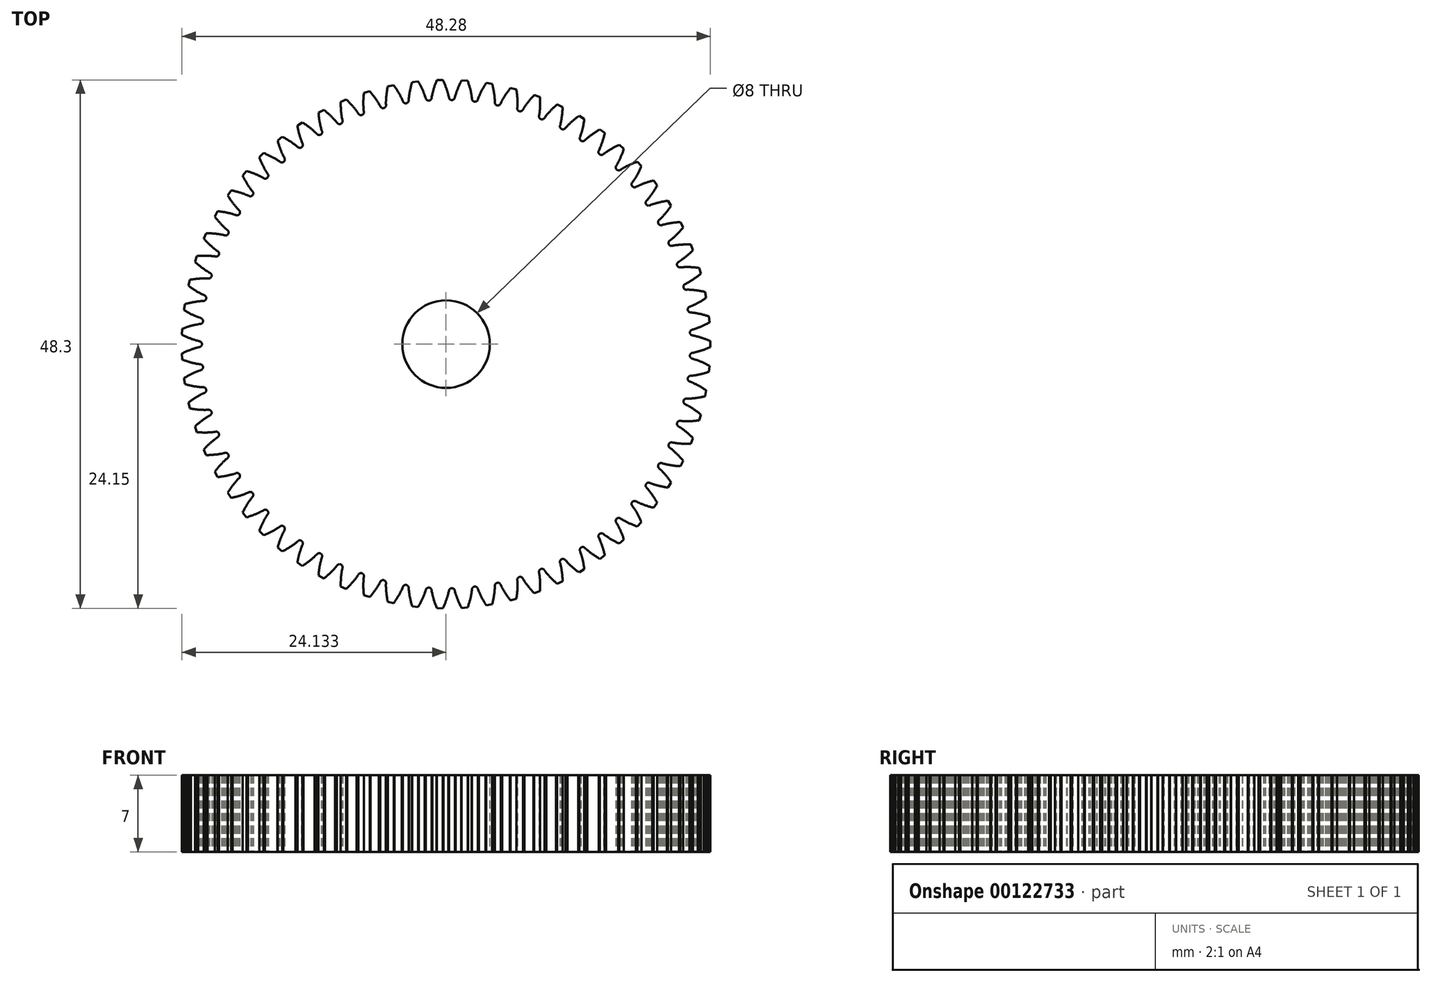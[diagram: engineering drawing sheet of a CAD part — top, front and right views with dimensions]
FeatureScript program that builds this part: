
annotation { "Feature Type Name" : "Feature", "Feature Type Description" : "" }
export const myFeature = defineFeature(function(context is Context, id is Id, definition is map)
    precondition{}
    {
        {
            var Q0;
            Q0=qCreatedBy(makeId("Top.planeOp"),FACE);
            var sketch = newSketch(context, id + "F0", { "sketchPlane" : qUnion([Q0])});
            skLineSegment(sketch, "E0", {"start": v(22.55, -0.79) * mm, "end": v(22.62, -0.77) * mm});
            skLineSegment(sketch, "E1", {"start": v(22.62, -0.77) * mm, "end": v(22.71, -0.75) * mm});
            skLineSegment(sketch, "E2", {"start": v(22.71, -0.75) * mm, "end": v(22.8, -0.73) * mm});
            skLineSegment(sketch, "E3", {"start": v(22.8, -0.73) * mm, "end": v(22.86, -0.72) * mm});
            skLineSegment(sketch, "E4", {"start": v(22.86, -0.72) * mm, "end": v(22.91, -0.7) * mm});
            skLineSegment(sketch, "E5", {"start": v(22.91, -0.7) * mm, "end": v(22.97, -0.7) * mm});
            skLineSegment(sketch, "E6", {"start": v(22.97, -0.7) * mm, "end": v(23.02, -0.68) * mm});
            skLineSegment(sketch, "E7", {"start": v(23.02, -0.68) * mm, "end": v(23.08, -0.66) * mm});
            skLineSegment(sketch, "E8", {"start": v(23.08, -0.66) * mm, "end": v(23.14, -0.64) * mm});
            skLineSegment(sketch, "E9", {"start": v(23.14, -0.64) * mm, "end": v(23.2, -0.63) * mm});
            skLineSegment(sketch, "E10", {"start": v(23.2, -0.63) * mm, "end": v(23.26, -0.6) * mm});
            skLineSegment(sketch, "E11", {"start": v(23.26, -0.6) * mm, "end": v(23.33, -0.59) * mm});
            skLineSegment(sketch, "E12", {"start": v(23.33, -0.59) * mm, "end": v(23.4, -0.57) * mm});
            skLineSegment(sketch, "E13", {"start": v(23.4, -0.57) * mm, "end": v(23.46, -0.54) * mm});
            skLineSegment(sketch, "E14", {"start": v(23.46, -0.54) * mm, "end": v(23.52, -0.52) * mm});
            skLineSegment(sketch, "E15", {"start": v(23.52, -0.52) * mm, "end": v(23.6, -0.5) * mm});
            skLineSegment(sketch, "E16", {"start": v(23.6, -0.5) * mm, "end": v(23.66, -0.47) * mm});
            skLineSegment(sketch, "E17", {"start": v(23.66, -0.47) * mm, "end": v(23.73, -0.44) * mm});
            skLineSegment(sketch, "E18", {"start": v(23.73, -0.44) * mm, "end": v(23.8, -0.42) * mm});
            skLineSegment(sketch, "E19", {"start": v(23.8, -0.42) * mm, "end": v(23.88, -0.39) * mm});
            skLineSegment(sketch, "E20", {"start": v(23.88, -0.39) * mm, "end": v(23.96, -0.36) * mm});
            skLineSegment(sketch, "E21", {"start": v(23.96, -0.36) * mm, "end": v(24.03, -0.32) * mm});
            skLineSegment(sketch, "E22", {"start": v(24.03, -0.32) * mm, "end": v(24.14, -0.28) * mm});
            skLineSegment(sketch, "E23", {"start": v(24.14, -0.28) * mm, "end": v(24.14, 0.28) * mm});
            skLineSegment(sketch, "E24", {"start": v(24.14, 0.28) * mm, "end": v(24.03, 0.32) * mm});
            skLineSegment(sketch, "E25", {"start": v(24.03, 0.32) * mm, "end": v(23.96, 0.36) * mm});
            skLineSegment(sketch, "E26", {"start": v(23.96, 0.36) * mm, "end": v(23.88, 0.39) * mm});
            skLineSegment(sketch, "E27", {"start": v(23.88, 0.39) * mm, "end": v(23.8, 0.42) * mm});
            skLineSegment(sketch, "E28", {"start": v(23.8, 0.42) * mm, "end": v(23.73, 0.44) * mm});
            skLineSegment(sketch, "E29", {"start": v(23.73, 0.44) * mm, "end": v(23.66, 0.47) * mm});
            skLineSegment(sketch, "E30", {"start": v(23.66, 0.47) * mm, "end": v(23.6, 0.5) * mm});
            skLineSegment(sketch, "E31", {"start": v(23.6, 0.5) * mm, "end": v(23.52, 0.52) * mm});
            skLineSegment(sketch, "E32", {"start": v(23.52, 0.52) * mm, "end": v(23.46, 0.54) * mm});
            skLineSegment(sketch, "E33", {"start": v(23.46, 0.54) * mm, "end": v(23.4, 0.57) * mm});
            skLineSegment(sketch, "E34", {"start": v(23.4, 0.57) * mm, "end": v(23.33, 0.59) * mm});
            skLineSegment(sketch, "E35", {"start": v(23.33, 0.59) * mm, "end": v(23.26, 0.6) * mm});
            skLineSegment(sketch, "E36", {"start": v(23.26, 0.6) * mm, "end": v(23.2, 0.63) * mm});
            skLineSegment(sketch, "E37", {"start": v(23.2, 0.63) * mm, "end": v(23.14, 0.64) * mm});
            skLineSegment(sketch, "E38", {"start": v(23.14, 0.64) * mm, "end": v(23.08, 0.66) * mm});
            skLineSegment(sketch, "E39", {"start": v(23.08, 0.66) * mm, "end": v(23.02, 0.68) * mm});
            skLineSegment(sketch, "E40", {"start": v(23.02, 0.68) * mm, "end": v(22.97, 0.7) * mm});
            skLineSegment(sketch, "E41", {"start": v(22.97, 0.7) * mm, "end": v(22.91, 0.7) * mm});
            skLineSegment(sketch, "E42", {"start": v(22.91, 0.7) * mm, "end": v(22.86, 0.72) * mm});
            skLineSegment(sketch, "E43", {"start": v(22.86, 0.72) * mm, "end": v(22.8, 0.73) * mm});
            skLineSegment(sketch, "E44", {"start": v(22.8, 0.73) * mm, "end": v(22.71, 0.75) * mm});
            skLineSegment(sketch, "E45", {"start": v(22.71, 0.75) * mm, "end": v(22.62, 0.77) * mm});
            skLineSegment(sketch, "E46", {"start": v(22.62, 0.77) * mm, "end": v(22.55, 0.79) * mm});
            skArc(sketch, "E47", {"start": v(22.55, 0.79) * mm, "mid": v(22.28, 1.05) * mm, "end": v(22.53, 1.33) * mm});
            skLineSegment(sketch, "E48", {"start": v(22.53, 1.33) * mm, "end": v(22.6, 1.35) * mm});
            skLineSegment(sketch, "E49", {"start": v(22.6, 1.35) * mm, "end": v(22.68, 1.38) * mm});
            skLineSegment(sketch, "E50", {"start": v(22.68, 1.38) * mm, "end": v(22.78, 1.4) * mm});
            skLineSegment(sketch, "E51", {"start": v(22.78, 1.4) * mm, "end": v(22.83, 1.43) * mm});
            skLineSegment(sketch, "E52", {"start": v(22.83, 1.43) * mm, "end": v(22.88, 1.44) * mm});
            skLineSegment(sketch, "E53", {"start": v(22.88, 1.44) * mm, "end": v(22.93, 1.46) * mm});
            skLineSegment(sketch, "E54", {"start": v(22.93, 1.46) * mm, "end": v(22.99, 1.48) * mm});
            skLineSegment(sketch, "E55", {"start": v(22.99, 1.48) * mm, "end": v(23.04, 1.5) * mm});
            skLineSegment(sketch, "E56", {"start": v(23.04, 1.5) * mm, "end": v(23.1, 1.53) * mm});
            skLineSegment(sketch, "E57", {"start": v(23.1, 1.53) * mm, "end": v(23.16, 1.55) * mm});
            skLineSegment(sketch, "E58", {"start": v(23.16, 1.55) * mm, "end": v(23.22, 1.58) * mm});
            skLineSegment(sketch, "E59", {"start": v(23.22, 1.58) * mm, "end": v(23.28, 1.6) * mm});
            skLineSegment(sketch, "E60", {"start": v(23.28, 1.6) * mm, "end": v(23.34, 1.63) * mm});
            skLineSegment(sketch, "E61", {"start": v(23.34, 1.63) * mm, "end": v(23.4, 1.66) * mm});
            skLineSegment(sketch, "E62", {"start": v(23.4, 1.66) * mm, "end": v(23.47, 1.69) * mm});
            skLineSegment(sketch, "E63", {"start": v(23.47, 1.69) * mm, "end": v(23.54, 1.72) * mm});
            skLineSegment(sketch, "E64", {"start": v(23.54, 1.72) * mm, "end": v(23.6, 1.75) * mm});
            skLineSegment(sketch, "E65", {"start": v(23.6, 1.75) * mm, "end": v(23.67, 1.78) * mm});
            skLineSegment(sketch, "E66", {"start": v(23.67, 1.78) * mm, "end": v(23.74, 1.82) * mm});
            skLineSegment(sketch, "E67", {"start": v(23.74, 1.82) * mm, "end": v(23.81, 1.85) * mm});
            skLineSegment(sketch, "E68", {"start": v(23.81, 1.85) * mm, "end": v(23.88, 1.9) * mm});
            skLineSegment(sketch, "E69", {"start": v(23.88, 1.9) * mm, "end": v(23.96, 1.93) * mm});
            skLineSegment(sketch, "E70", {"start": v(23.96, 1.93) * mm, "end": v(24.06, 1.99) * mm});
            skLineSegment(sketch, "E71", {"start": v(24.06, 1.99) * mm, "end": v(24, 2.54) * mm});
            skLineSegment(sketch, "E72", {"start": v(24, 2.54) * mm, "end": v(23.9, 2.57) * mm});
            skLineSegment(sketch, "E73", {"start": v(23.9, 2.57) * mm, "end": v(23.82, 2.6) * mm});
            skLineSegment(sketch, "E74", {"start": v(23.82, 2.6) * mm, "end": v(23.74, 2.62) * mm});
            skLineSegment(sketch, "E75", {"start": v(23.74, 2.62) * mm, "end": v(23.66, 2.64) * mm});
            skLineSegment(sketch, "E76", {"start": v(23.66, 2.64) * mm, "end": v(23.59, 2.66) * mm});
            skLineSegment(sketch, "E77", {"start": v(23.59, 2.66) * mm, "end": v(23.51, 2.68) * mm});
            skLineSegment(sketch, "E78", {"start": v(23.51, 2.68) * mm, "end": v(23.44, 2.7) * mm});
            skLineSegment(sketch, "E79", {"start": v(23.44, 2.7) * mm, "end": v(23.37, 2.72) * mm});
            skLineSegment(sketch, "E80", {"start": v(23.37, 2.72) * mm, "end": v(23.3, 2.74) * mm});
            skLineSegment(sketch, "E81", {"start": v(23.3, 2.74) * mm, "end": v(23.23, 2.75) * mm});
            skLineSegment(sketch, "E82", {"start": v(23.23, 2.75) * mm, "end": v(23.17, 2.77) * mm});
            skLineSegment(sketch, "E83", {"start": v(23.17, 2.77) * mm, "end": v(23.1, 2.78) * mm});
            skLineSegment(sketch, "E84", {"start": v(23.1, 2.78) * mm, "end": v(23.04, 2.8) * mm});
            skLineSegment(sketch, "E85", {"start": v(23.04, 2.8) * mm, "end": v(22.98, 2.8) * mm});
            skLineSegment(sketch, "E86", {"start": v(22.98, 2.8) * mm, "end": v(22.92, 2.82) * mm});
            skLineSegment(sketch, "E87", {"start": v(22.92, 2.82) * mm, "end": v(22.86, 2.83) * mm});
            skLineSegment(sketch, "E88", {"start": v(22.86, 2.83) * mm, "end": v(22.8, 2.84) * mm});
            skLineSegment(sketch, "E89", {"start": v(22.8, 2.84) * mm, "end": v(22.75, 2.85) * mm});
            skLineSegment(sketch, "E90", {"start": v(22.75, 2.85) * mm, "end": v(22.7, 2.86) * mm});
            skLineSegment(sketch, "E91", {"start": v(22.7, 2.86) * mm, "end": v(22.64, 2.86) * mm});
            skLineSegment(sketch, "E92", {"start": v(22.64, 2.86) * mm, "end": v(22.54, 2.88) * mm});
            skLineSegment(sketch, "E93", {"start": v(22.54, 2.88) * mm, "end": v(22.45, 2.89) * mm});
            skLineSegment(sketch, "E94", {"start": v(22.45, 2.89) * mm, "end": v(22.38, 2.9) * mm});
            skArc(sketch, "E95", {"start": v(22.38, 2.9) * mm, "mid": v(22.08, 3.13) * mm, "end": v(22.3, 3.44) * mm});
            skLineSegment(sketch, "E96", {"start": v(22.3, 3.44) * mm, "end": v(22.37, 3.46) * mm});
            skLineSegment(sketch, "E97", {"start": v(22.37, 3.46) * mm, "end": v(22.45, 3.5) * mm});
            skLineSegment(sketch, "E98", {"start": v(22.45, 3.5) * mm, "end": v(22.55, 3.54) * mm});
            skLineSegment(sketch, "E99", {"start": v(22.55, 3.54) * mm, "end": v(22.6, 3.56) * mm});
            skLineSegment(sketch, "E100", {"start": v(22.6, 3.56) * mm, "end": v(22.64, 3.58) * mm});
            skLineSegment(sketch, "E101", {"start": v(22.64, 3.58) * mm, "end": v(22.7, 3.6) * mm});
            skLineSegment(sketch, "E102", {"start": v(22.7, 3.6) * mm, "end": v(22.75, 3.63) * mm});
            skLineSegment(sketch, "E103", {"start": v(22.75, 3.63) * mm, "end": v(22.8, 3.66) * mm});
            skLineSegment(sketch, "E104", {"start": v(22.8, 3.66) * mm, "end": v(22.85, 3.68) * mm});
            skLineSegment(sketch, "E105", {"start": v(22.85, 3.68) * mm, "end": v(22.91, 3.71) * mm});
            skLineSegment(sketch, "E106", {"start": v(22.91, 3.71) * mm, "end": v(22.97, 3.74) * mm});
            skLineSegment(sketch, "E107", {"start": v(22.97, 3.74) * mm, "end": v(23.03, 3.77) * mm});
            skLineSegment(sketch, "E108", {"start": v(23.03, 3.77) * mm, "end": v(23.09, 3.8) * mm});
            skLineSegment(sketch, "E109", {"start": v(23.09, 3.8) * mm, "end": v(23.15, 3.84) * mm});
            skLineSegment(sketch, "E110", {"start": v(23.15, 3.84) * mm, "end": v(23.2, 3.88) * mm});
            skLineSegment(sketch, "E111", {"start": v(23.2, 3.88) * mm, "end": v(23.27, 3.91) * mm});
            skLineSegment(sketch, "E112", {"start": v(23.27, 3.91) * mm, "end": v(23.34, 3.95) * mm});
            skLineSegment(sketch, "E113", {"start": v(23.34, 3.95) * mm, "end": v(23.4, 4) * mm});
            skLineSegment(sketch, "E114", {"start": v(23.4, 4) * mm, "end": v(23.47, 4.03) * mm});
            skLineSegment(sketch, "E115", {"start": v(23.47, 4.03) * mm, "end": v(23.53, 4.08) * mm});
            skLineSegment(sketch, "E116", {"start": v(23.53, 4.08) * mm, "end": v(23.6, 4.12) * mm});
            skLineSegment(sketch, "E117", {"start": v(23.6, 4.12) * mm, "end": v(23.67, 4.16) * mm});
            skLineSegment(sketch, "E118", {"start": v(23.67, 4.16) * mm, "end": v(23.77, 4.23) * mm});
            skLineSegment(sketch, "E119", {"start": v(23.77, 4.23) * mm, "end": v(23.67, 4.77) * mm});
            skLineSegment(sketch, "E120", {"start": v(23.67, 4.77) * mm, "end": v(23.55, 4.8) * mm});
            skLineSegment(sketch, "E121", {"start": v(23.55, 4.8) * mm, "end": v(23.47, 4.82) * mm});
            skLineSegment(sketch, "E122", {"start": v(23.47, 4.82) * mm, "end": v(23.4, 4.83) * mm});
            skLineSegment(sketch, "E123", {"start": v(23.4, 4.83) * mm, "end": v(23.31, 4.85) * mm});
            skLineSegment(sketch, "E124", {"start": v(23.31, 4.85) * mm, "end": v(23.24, 4.86) * mm});
            skLineSegment(sketch, "E125", {"start": v(23.24, 4.86) * mm, "end": v(23.16, 4.88) * mm});
            skLineSegment(sketch, "E126", {"start": v(23.16, 4.88) * mm, "end": v(23.09, 4.89) * mm});
            skLineSegment(sketch, "E127", {"start": v(23.09, 4.89) * mm, "end": v(23.01, 4.9) * mm});
            skLineSegment(sketch, "E128", {"start": v(23.01, 4.9) * mm, "end": v(22.94, 4.9) * mm});
            skLineSegment(sketch, "E129", {"start": v(22.94, 4.9) * mm, "end": v(22.87, 4.92) * mm});
            skLineSegment(sketch, "E130", {"start": v(22.87, 4.92) * mm, "end": v(22.8, 4.93) * mm});
            skLineSegment(sketch, "E131", {"start": v(22.8, 4.93) * mm, "end": v(22.74, 4.93) * mm});
            skLineSegment(sketch, "E132", {"start": v(22.74, 4.93) * mm, "end": v(22.68, 4.94) * mm});
            skLineSegment(sketch, "E133", {"start": v(22.68, 4.94) * mm, "end": v(22.61, 4.95) * mm});
            skLineSegment(sketch, "E134", {"start": v(22.61, 4.95) * mm, "end": v(22.55, 4.95) * mm});
            skLineSegment(sketch, "E135", {"start": v(22.55, 4.95) * mm, "end": v(22.5, 4.96) * mm});
            skLineSegment(sketch, "E136", {"start": v(22.5, 4.96) * mm, "end": v(22.44, 4.96) * mm});
            skLineSegment(sketch, "E137", {"start": v(22.44, 4.96) * mm, "end": v(22.38, 4.97) * mm});
            skLineSegment(sketch, "E138", {"start": v(22.38, 4.97) * mm, "end": v(22.33, 4.97) * mm});
            skLineSegment(sketch, "E139", {"start": v(22.33, 4.97) * mm, "end": v(22.27, 4.97) * mm});
            skLineSegment(sketch, "E140", {"start": v(22.27, 4.97) * mm, "end": v(22.17, 4.98) * mm});
            skLineSegment(sketch, "E141", {"start": v(22.17, 4.98) * mm, "end": v(22.08, 4.98) * mm});
            skLineSegment(sketch, "E142", {"start": v(22.08, 4.98) * mm, "end": v(22.01, 4.98) * mm});
            skArc(sketch, "E143", {"start": v(22.01, 4.98) * mm, "mid": v(21.7, 5.18) * mm, "end": v(21.89, 5.5) * mm});
            skLineSegment(sketch, "E144", {"start": v(21.89, 5.5) * mm, "end": v(21.94, 5.54) * mm});
            skLineSegment(sketch, "E145", {"start": v(21.94, 5.54) * mm, "end": v(22.03, 5.58) * mm});
            skLineSegment(sketch, "E146", {"start": v(22.03, 5.58) * mm, "end": v(22.12, 5.63) * mm});
            skLineSegment(sketch, "E147", {"start": v(22.12, 5.63) * mm, "end": v(22.16, 5.66) * mm});
            skLineSegment(sketch, "E148", {"start": v(22.16, 5.66) * mm, "end": v(22.2, 5.69) * mm});
            skLineSegment(sketch, "E149", {"start": v(22.2, 5.69) * mm, "end": v(22.26, 5.71) * mm});
            skLineSegment(sketch, "E150", {"start": v(22.26, 5.71) * mm, "end": v(22.3, 5.74) * mm});
            skLineSegment(sketch, "E151", {"start": v(22.3, 5.74) * mm, "end": v(22.36, 5.78) * mm});
            skLineSegment(sketch, "E152", {"start": v(22.36, 5.78) * mm, "end": v(22.4, 5.8) * mm});
            skLineSegment(sketch, "E153", {"start": v(22.4, 5.8) * mm, "end": v(22.46, 5.84) * mm});
            skLineSegment(sketch, "E154", {"start": v(22.46, 5.84) * mm, "end": v(22.52, 5.88) * mm});
            skLineSegment(sketch, "E155", {"start": v(22.52, 5.88) * mm, "end": v(22.57, 5.91) * mm});
            skLineSegment(sketch, "E156", {"start": v(22.57, 5.91) * mm, "end": v(22.63, 5.95) * mm});
            skLineSegment(sketch, "E157", {"start": v(22.63, 5.95) * mm, "end": v(22.68, 6) * mm});
            skLineSegment(sketch, "E158", {"start": v(22.68, 6) * mm, "end": v(22.74, 6.03) * mm});
            skLineSegment(sketch, "E159", {"start": v(22.74, 6.03) * mm, "end": v(22.8, 6.08) * mm});
            skLineSegment(sketch, "E160", {"start": v(22.8, 6.08) * mm, "end": v(22.86, 6.12) * mm});
            skLineSegment(sketch, "E161", {"start": v(22.86, 6.12) * mm, "end": v(22.92, 6.17) * mm});
            skLineSegment(sketch, "E162", {"start": v(22.92, 6.17) * mm, "end": v(22.99, 6.21) * mm});
            skLineSegment(sketch, "E163", {"start": v(22.99, 6.21) * mm, "end": v(23.05, 6.26) * mm});
            skLineSegment(sketch, "E164", {"start": v(23.05, 6.26) * mm, "end": v(23.11, 6.31) * mm});
            skLineSegment(sketch, "E165", {"start": v(23.11, 6.31) * mm, "end": v(23.18, 6.36) * mm});
            skLineSegment(sketch, "E166", {"start": v(23.18, 6.36) * mm, "end": v(23.27, 6.44) * mm});
            skLineSegment(sketch, "E167", {"start": v(23.27, 6.44) * mm, "end": v(23.12, 6.97) * mm});
            skLineSegment(sketch, "E168", {"start": v(23.12, 6.97) * mm, "end": v(23, 6.99) * mm});
            skLineSegment(sketch, "E169", {"start": v(23, 6.99) * mm, "end": v(22.92, 7) * mm});
            skLineSegment(sketch, "E170", {"start": v(22.92, 7) * mm, "end": v(22.83, 7) * mm});
            skLineSegment(sketch, "E171", {"start": v(22.83, 7) * mm, "end": v(22.76, 7.01) * mm});
            skLineSegment(sketch, "E172", {"start": v(22.76, 7.01) * mm, "end": v(22.68, 7.02) * mm});
            skLineSegment(sketch, "E173", {"start": v(22.68, 7.02) * mm, "end": v(22.6, 7.02) * mm});
            skLineSegment(sketch, "E174", {"start": v(22.6, 7.02) * mm, "end": v(22.53, 7.03) * mm});
            skLineSegment(sketch, "E175", {"start": v(22.53, 7.03) * mm, "end": v(22.45, 7.03) * mm});
            skLineSegment(sketch, "E176", {"start": v(22.45, 7.03) * mm, "end": v(22.38, 7.04) * mm});
            skLineSegment(sketch, "E177", {"start": v(22.38, 7.04) * mm, "end": v(22.31, 7.04) * mm});
            skLineSegment(sketch, "E178", {"start": v(22.31, 7.04) * mm, "end": v(22.25, 7.04) * mm});
            skLineSegment(sketch, "E179", {"start": v(22.25, 7.04) * mm, "end": v(22.18, 7.04) * mm});
            skLineSegment(sketch, "E180", {"start": v(22.18, 7.04) * mm, "end": v(22.11, 7.04) * mm});
            skLineSegment(sketch, "E181", {"start": v(22.11, 7.04) * mm, "end": v(22.05, 7.04) * mm});
            skLineSegment(sketch, "E182", {"start": v(22.05, 7.04) * mm, "end": v(22, 7.04) * mm});
            skLineSegment(sketch, "E183", {"start": v(22, 7.04) * mm, "end": v(21.93, 7.04) * mm});
            skLineSegment(sketch, "E184", {"start": v(21.93, 7.04) * mm, "end": v(21.87, 7.04) * mm});
            skLineSegment(sketch, "E185", {"start": v(21.87, 7.04) * mm, "end": v(21.82, 7.04) * mm});
            skLineSegment(sketch, "E186", {"start": v(21.82, 7.04) * mm, "end": v(21.76, 7.04) * mm});
            skLineSegment(sketch, "E187", {"start": v(21.76, 7.04) * mm, "end": v(21.7, 7.04) * mm});
            skLineSegment(sketch, "E188", {"start": v(21.7, 7.04) * mm, "end": v(21.6, 7.03) * mm});
            skLineSegment(sketch, "E189", {"start": v(21.6, 7.03) * mm, "end": v(21.52, 7.02) * mm});
            skLineSegment(sketch, "E190", {"start": v(21.52, 7.02) * mm, "end": v(21.45, 7.02) * mm});
            skArc(sketch, "E191", {"start": v(21.45, 7.02) * mm, "mid": v(21.11, 7.2) * mm, "end": v(21.27, 7.54) * mm});
            skLineSegment(sketch, "E192", {"start": v(21.27, 7.54) * mm, "end": v(21.33, 7.57) * mm});
            skLineSegment(sketch, "E193", {"start": v(21.33, 7.57) * mm, "end": v(21.4, 7.62) * mm});
            skLineSegment(sketch, "E194", {"start": v(21.4, 7.62) * mm, "end": v(21.5, 7.68) * mm});
            skLineSegment(sketch, "E195", {"start": v(21.5, 7.68) * mm, "end": v(21.53, 7.7) * mm});
            skLineSegment(sketch, "E196", {"start": v(21.53, 7.7) * mm, "end": v(21.58, 7.74) * mm});
            skLineSegment(sketch, "E197", {"start": v(21.58, 7.74) * mm, "end": v(21.62, 7.77) * mm});
            skLineSegment(sketch, "E198", {"start": v(21.62, 7.77) * mm, "end": v(21.67, 7.8) * mm});
            skLineSegment(sketch, "E199", {"start": v(21.67, 7.8) * mm, "end": v(21.72, 7.84) * mm});
            skLineSegment(sketch, "E200", {"start": v(21.72, 7.84) * mm, "end": v(21.77, 7.88) * mm});
            skLineSegment(sketch, "E201", {"start": v(21.77, 7.88) * mm, "end": v(21.82, 7.92) * mm});
            skLineSegment(sketch, "E202", {"start": v(21.82, 7.92) * mm, "end": v(21.87, 7.96) * mm});
            skLineSegment(sketch, "E203", {"start": v(21.87, 7.96) * mm, "end": v(21.92, 8) * mm});
            skLineSegment(sketch, "E204", {"start": v(21.92, 8) * mm, "end": v(21.97, 8.05) * mm});
            skLineSegment(sketch, "E205", {"start": v(21.97, 8.05) * mm, "end": v(22.02, 8.1) * mm});
            skLineSegment(sketch, "E206", {"start": v(22.02, 8.1) * mm, "end": v(22.08, 8.14) * mm});
            skLineSegment(sketch, "E207", {"start": v(22.08, 8.14) * mm, "end": v(22.13, 8.19) * mm});
            skLineSegment(sketch, "E208", {"start": v(22.13, 8.19) * mm, "end": v(22.19, 8.23) * mm});
            skLineSegment(sketch, "E209", {"start": v(22.19, 8.23) * mm, "end": v(22.25, 8.29) * mm});
            skLineSegment(sketch, "E210", {"start": v(22.25, 8.29) * mm, "end": v(22.3, 8.34) * mm});
            skLineSegment(sketch, "E211", {"start": v(22.3, 8.34) * mm, "end": v(22.36, 8.4) * mm});
            skLineSegment(sketch, "E212", {"start": v(22.36, 8.4) * mm, "end": v(22.42, 8.45) * mm});
            skLineSegment(sketch, "E213", {"start": v(22.42, 8.45) * mm, "end": v(22.48, 8.5) * mm});
            skLineSegment(sketch, "E214", {"start": v(22.48, 8.5) * mm, "end": v(22.56, 8.59) * mm});
            skLineSegment(sketch, "E215", {"start": v(22.56, 8.59) * mm, "end": v(22.36, 9.1) * mm});
            skLineSegment(sketch, "E216", {"start": v(22.36, 9.1) * mm, "end": v(22.24, 9.1) * mm});
            skLineSegment(sketch, "E217", {"start": v(22.24, 9.1) * mm, "end": v(22.16, 9.11) * mm});
            skLineSegment(sketch, "E218", {"start": v(22.16, 9.11) * mm, "end": v(22.08, 9.11) * mm});
            skLineSegment(sketch, "E219", {"start": v(22.08, 9.11) * mm, "end": v(22, 9.11) * mm});
            skLineSegment(sketch, "E220", {"start": v(22, 9.11) * mm, "end": v(21.92, 9.11) * mm});
            skLineSegment(sketch, "E221", {"start": v(21.92, 9.11) * mm, "end": v(21.84, 9.1) * mm});
            skLineSegment(sketch, "E222", {"start": v(21.84, 9.1) * mm, "end": v(21.77, 9.1) * mm});
            skLineSegment(sketch, "E223", {"start": v(21.77, 9.1) * mm, "end": v(21.7, 9.1) * mm});
            skLineSegment(sketch, "E224", {"start": v(21.7, 9.1) * mm, "end": v(21.63, 9.1) * mm});
            skLineSegment(sketch, "E225", {"start": v(21.63, 9.1) * mm, "end": v(21.56, 9.1) * mm});
            skLineSegment(sketch, "E226", {"start": v(21.56, 9.1) * mm, "end": v(21.49, 9.1) * mm});
            skLineSegment(sketch, "E227", {"start": v(21.49, 9.1) * mm, "end": v(21.42, 9.09) * mm});
            skLineSegment(sketch, "E228", {"start": v(21.42, 9.09) * mm, "end": v(21.36, 9.08) * mm});
            skLineSegment(sketch, "E229", {"start": v(21.36, 9.08) * mm, "end": v(21.3, 9.08) * mm});
            skLineSegment(sketch, "E230", {"start": v(21.3, 9.08) * mm, "end": v(21.23, 9.07) * mm});
            skLineSegment(sketch, "E231", {"start": v(21.23, 9.07) * mm, "end": v(21.17, 9.07) * mm});
            skLineSegment(sketch, "E232", {"start": v(21.17, 9.07) * mm, "end": v(21.12, 9.06) * mm});
            skLineSegment(sketch, "E233", {"start": v(21.12, 9.06) * mm, "end": v(21.06, 9.05) * mm});
            skLineSegment(sketch, "E234", {"start": v(21.06, 9.05) * mm, "end": v(21, 9.05) * mm});
            skLineSegment(sketch, "E235", {"start": v(21, 9.05) * mm, "end": v(20.96, 9.04) * mm});
            skLineSegment(sketch, "E236", {"start": v(20.96, 9.04) * mm, "end": v(20.86, 9.02) * mm});
            skLineSegment(sketch, "E237", {"start": v(20.86, 9.02) * mm, "end": v(20.76, 9) * mm});
            skLineSegment(sketch, "E238", {"start": v(20.76, 9) * mm, "end": v(20.7, 9) * mm});
            skArc(sketch, "E239", {"start": v(20.7, 9) * mm, "mid": v(20.35, 9.14) * mm, "end": v(20.47, 9.5) * mm});
            skLineSegment(sketch, "E240", {"start": v(20.47, 9.5) * mm, "end": v(20.53, 9.54) * mm});
            skLineSegment(sketch, "E241", {"start": v(20.53, 9.54) * mm, "end": v(20.6, 9.6) * mm});
            skLineSegment(sketch, "E242", {"start": v(20.6, 9.6) * mm, "end": v(20.68, 9.66) * mm});
            skLineSegment(sketch, "E243", {"start": v(20.68, 9.66) * mm, "end": v(20.72, 9.7) * mm});
            skLineSegment(sketch, "E244", {"start": v(20.72, 9.7) * mm, "end": v(20.76, 9.73) * mm});
            skLineSegment(sketch, "E245", {"start": v(20.76, 9.73) * mm, "end": v(20.8, 9.77) * mm});
            skLineSegment(sketch, "E246", {"start": v(20.8, 9.77) * mm, "end": v(20.84, 9.8) * mm});
            skLineSegment(sketch, "E247", {"start": v(20.84, 9.8) * mm, "end": v(20.89, 9.84) * mm});
            skLineSegment(sketch, "E248", {"start": v(20.89, 9.84) * mm, "end": v(20.93, 9.89) * mm});
            skLineSegment(sketch, "E249", {"start": v(20.93, 9.89) * mm, "end": v(20.98, 9.93) * mm});
            skLineSegment(sketch, "E250", {"start": v(20.98, 9.93) * mm, "end": v(21.02, 9.97) * mm});
            skLineSegment(sketch, "E251", {"start": v(21.02, 9.97) * mm, "end": v(21.07, 10.02) * mm});
            skLineSegment(sketch, "E252", {"start": v(21.07, 10.02) * mm, "end": v(21.12, 10.07) * mm});
            skLineSegment(sketch, "E253", {"start": v(21.12, 10.07) * mm, "end": v(21.17, 10.12) * mm});
            skLineSegment(sketch, "E254", {"start": v(21.17, 10.12) * mm, "end": v(21.22, 10.17) * mm});
            skLineSegment(sketch, "E255", {"start": v(21.22, 10.17) * mm, "end": v(21.27, 10.22) * mm});
            skLineSegment(sketch, "E256", {"start": v(21.27, 10.22) * mm, "end": v(21.32, 10.28) * mm});
            skLineSegment(sketch, "E257", {"start": v(21.32, 10.28) * mm, "end": v(21.37, 10.33) * mm});
            skLineSegment(sketch, "E258", {"start": v(21.37, 10.33) * mm, "end": v(21.42, 10.4) * mm});
            skLineSegment(sketch, "E259", {"start": v(21.42, 10.4) * mm, "end": v(21.48, 10.45) * mm});
            skLineSegment(sketch, "E260", {"start": v(21.48, 10.45) * mm, "end": v(21.53, 10.51) * mm});
            skLineSegment(sketch, "E261", {"start": v(21.53, 10.51) * mm, "end": v(21.58, 10.58) * mm});
            skLineSegment(sketch, "E262", {"start": v(21.58, 10.58) * mm, "end": v(21.66, 10.67) * mm});
            skLineSegment(sketch, "E263", {"start": v(21.66, 10.67) * mm, "end": v(21.41, 11.16) * mm});
            skLineSegment(sketch, "E264", {"start": v(21.41, 11.16) * mm, "end": v(21.3, 11.15) * mm});
            skLineSegment(sketch, "E265", {"start": v(21.3, 11.15) * mm, "end": v(21.2, 11.15) * mm});
            skLineSegment(sketch, "E266", {"start": v(21.2, 11.15) * mm, "end": v(21.13, 11.14) * mm});
            skLineSegment(sketch, "E267", {"start": v(21.13, 11.14) * mm, "end": v(21.05, 11.13) * mm});
            skLineSegment(sketch, "E268", {"start": v(21.05, 11.13) * mm, "end": v(20.97, 11.12) * mm});
            skLineSegment(sketch, "E269", {"start": v(20.97, 11.12) * mm, "end": v(20.9, 11.12) * mm});
            skLineSegment(sketch, "E270", {"start": v(20.9, 11.12) * mm, "end": v(20.82, 11.1) * mm});
            skLineSegment(sketch, "E271", {"start": v(20.82, 11.1) * mm, "end": v(20.75, 11.1) * mm});
            skLineSegment(sketch, "E272", {"start": v(20.75, 11.1) * mm, "end": v(20.68, 11.09) * mm});
            skLineSegment(sketch, "E273", {"start": v(20.68, 11.09) * mm, "end": v(20.6, 11.08) * mm});
            skLineSegment(sketch, "E274", {"start": v(20.6, 11.08) * mm, "end": v(20.54, 11.07) * mm});
            skLineSegment(sketch, "E275", {"start": v(20.54, 11.07) * mm, "end": v(20.48, 11.06) * mm});
            skLineSegment(sketch, "E276", {"start": v(20.48, 11.06) * mm, "end": v(20.41, 11.05) * mm});
            skLineSegment(sketch, "E277", {"start": v(20.41, 11.05) * mm, "end": v(20.35, 11.03) * mm});
            skLineSegment(sketch, "E278", {"start": v(20.35, 11.03) * mm, "end": v(20.3, 11.02) * mm});
            skLineSegment(sketch, "E279", {"start": v(20.3, 11.02) * mm, "end": v(20.23, 11.01) * mm});
            skLineSegment(sketch, "E280", {"start": v(20.23, 11.01) * mm, "end": v(20.18, 11) * mm});
            skLineSegment(sketch, "E281", {"start": v(20.18, 11) * mm, "end": v(20.12, 10.99) * mm});
            skLineSegment(sketch, "E282", {"start": v(20.12, 10.99) * mm, "end": v(20.07, 10.97) * mm});
            skLineSegment(sketch, "E283", {"start": v(20.07, 10.97) * mm, "end": v(20.02, 10.96) * mm});
            skLineSegment(sketch, "E284", {"start": v(20.02, 10.96) * mm, "end": v(19.92, 10.94) * mm});
            skLineSegment(sketch, "E285", {"start": v(19.92, 10.94) * mm, "end": v(19.83, 10.91) * mm});
            skLineSegment(sketch, "E286", {"start": v(19.83, 10.91) * mm, "end": v(19.76, 10.9) * mm});
            skArc(sketch, "E287", {"start": v(19.76, 10.9) * mm, "mid": v(19.4, 11) * mm, "end": v(19.5, 11.37) * mm});
            skLineSegment(sketch, "E288", {"start": v(19.5, 11.37) * mm, "end": v(19.54, 11.42) * mm});
            skLineSegment(sketch, "E289", {"start": v(19.54, 11.42) * mm, "end": v(19.61, 11.48) * mm});
            skLineSegment(sketch, "E290", {"start": v(19.61, 11.48) * mm, "end": v(19.68, 11.55) * mm});
            skLineSegment(sketch, "E291", {"start": v(19.68, 11.55) * mm, "end": v(19.72, 11.6) * mm});
            skLineSegment(sketch, "E292", {"start": v(19.72, 11.6) * mm, "end": v(19.76, 11.63) * mm});
            skLineSegment(sketch, "E293", {"start": v(19.76, 11.63) * mm, "end": v(19.8, 11.67) * mm});
            skLineSegment(sketch, "E294", {"start": v(19.8, 11.67) * mm, "end": v(19.83, 11.71) * mm});
            skLineSegment(sketch, "E295", {"start": v(19.83, 11.71) * mm, "end": v(19.87, 11.76) * mm});
            skLineSegment(sketch, "E296", {"start": v(19.87, 11.76) * mm, "end": v(19.91, 11.8) * mm});
            skLineSegment(sketch, "E297", {"start": v(19.91, 11.8) * mm, "end": v(19.96, 11.85) * mm});
            skLineSegment(sketch, "E298", {"start": v(19.96, 11.85) * mm, "end": v(20, 11.9) * mm});
            skLineSegment(sketch, "E299", {"start": v(20, 11.9) * mm, "end": v(20.04, 11.95) * mm});
            skLineSegment(sketch, "E300", {"start": v(20.04, 11.95) * mm, "end": v(20.08, 12) * mm});
            skLineSegment(sketch, "E301", {"start": v(20.08, 12) * mm, "end": v(20.13, 12.06) * mm});
            skLineSegment(sketch, "E302", {"start": v(20.13, 12.06) * mm, "end": v(20.17, 12.11) * mm});
            skLineSegment(sketch, "E303", {"start": v(20.17, 12.11) * mm, "end": v(20.22, 12.17) * mm});
            skLineSegment(sketch, "E304", {"start": v(20.22, 12.17) * mm, "end": v(20.26, 12.23) * mm});
            skLineSegment(sketch, "E305", {"start": v(20.26, 12.23) * mm, "end": v(20.31, 12.29) * mm});
            skLineSegment(sketch, "E306", {"start": v(20.31, 12.29) * mm, "end": v(20.36, 12.35) * mm});
            skLineSegment(sketch, "E307", {"start": v(20.36, 12.35) * mm, "end": v(20.4, 12.42) * mm});
            skLineSegment(sketch, "E308", {"start": v(20.4, 12.42) * mm, "end": v(20.45, 12.48) * mm});
            skLineSegment(sketch, "E309", {"start": v(20.45, 12.48) * mm, "end": v(20.5, 12.55) * mm});
            skLineSegment(sketch, "E310", {"start": v(20.5, 12.55) * mm, "end": v(20.57, 12.65) * mm});
            skLineSegment(sketch, "E311", {"start": v(20.57, 12.65) * mm, "end": v(20.27, 13.12) * mm});
            skLineSegment(sketch, "E312", {"start": v(20.27, 13.12) * mm, "end": v(20.15, 13.1) * mm});
            skLineSegment(sketch, "E313", {"start": v(20.15, 13.1) * mm, "end": v(20.07, 13.08) * mm});
            skLineSegment(sketch, "E314", {"start": v(20.07, 13.08) * mm, "end": v(20, 13.07) * mm});
            skLineSegment(sketch, "E315", {"start": v(20, 13.07) * mm, "end": v(19.91, 13.05) * mm});
            skLineSegment(sketch, "E316", {"start": v(19.91, 13.05) * mm, "end": v(19.84, 13.04) * mm});
            skLineSegment(sketch, "E317", {"start": v(19.84, 13.04) * mm, "end": v(19.76, 13.02) * mm});
            skLineSegment(sketch, "E318", {"start": v(19.76, 13.02) * mm, "end": v(19.69, 13) * mm});
            skLineSegment(sketch, "E319", {"start": v(19.69, 13) * mm, "end": v(19.62, 13) * mm});
            skLineSegment(sketch, "E320", {"start": v(19.62, 13) * mm, "end": v(19.55, 12.98) * mm});
            skLineSegment(sketch, "E321", {"start": v(19.55, 12.98) * mm, "end": v(19.48, 12.96) * mm});
            skLineSegment(sketch, "E322", {"start": v(19.48, 12.96) * mm, "end": v(19.42, 12.94) * mm});
            skLineSegment(sketch, "E323", {"start": v(19.42, 12.94) * mm, "end": v(19.35, 12.93) * mm});
            skLineSegment(sketch, "E324", {"start": v(19.35, 12.93) * mm, "end": v(19.29, 12.9) * mm});
            skLineSegment(sketch, "E325", {"start": v(19.29, 12.9) * mm, "end": v(19.23, 12.9) * mm});
            skLineSegment(sketch, "E326", {"start": v(19.23, 12.9) * mm, "end": v(19.17, 12.87) * mm});
            skLineSegment(sketch, "E327", {"start": v(19.17, 12.87) * mm, "end": v(19.11, 12.86) * mm});
            skLineSegment(sketch, "E328", {"start": v(19.11, 12.86) * mm, "end": v(19.06, 12.84) * mm});
            skLineSegment(sketch, "E329", {"start": v(19.06, 12.84) * mm, "end": v(19, 12.82) * mm});
            skLineSegment(sketch, "E330", {"start": v(19, 12.82) * mm, "end": v(18.95, 12.8) * mm});
            skLineSegment(sketch, "E331", {"start": v(18.95, 12.8) * mm, "end": v(18.9, 12.79) * mm});
            skLineSegment(sketch, "E332", {"start": v(18.9, 12.79) * mm, "end": v(18.8, 12.76) * mm});
            skLineSegment(sketch, "E333", {"start": v(18.8, 12.76) * mm, "end": v(18.72, 12.72) * mm});
            skLineSegment(sketch, "E334", {"start": v(18.72, 12.72) * mm, "end": v(18.66, 12.7) * mm});
            skArc(sketch, "E335", {"start": v(18.66, 12.7) * mm, "mid": v(18.29, 12.77) * mm, "end": v(18.34, 13.15) * mm});
            skLineSegment(sketch, "E336", {"start": v(18.34, 13.15) * mm, "end": v(18.39, 13.2) * mm});
            skLineSegment(sketch, "E337", {"start": v(18.39, 13.2) * mm, "end": v(18.45, 13.27) * mm});
            skLineSegment(sketch, "E338", {"start": v(18.45, 13.27) * mm, "end": v(18.51, 13.35) * mm});
            skLineSegment(sketch, "E339", {"start": v(18.51, 13.35) * mm, "end": v(18.55, 13.39) * mm});
            skLineSegment(sketch, "E340", {"start": v(18.55, 13.39) * mm, "end": v(18.58, 13.43) * mm});
            skLineSegment(sketch, "E341", {"start": v(18.58, 13.43) * mm, "end": v(18.61, 13.47) * mm});
            skLineSegment(sketch, "E342", {"start": v(18.61, 13.47) * mm, "end": v(18.65, 13.52) * mm});
            skLineSegment(sketch, "E343", {"start": v(18.65, 13.52) * mm, "end": v(18.69, 13.57) * mm});
            skLineSegment(sketch, "E344", {"start": v(18.69, 13.57) * mm, "end": v(18.72, 13.62) * mm});
            skLineSegment(sketch, "E345", {"start": v(18.72, 13.62) * mm, "end": v(18.76, 13.67) * mm});
            skLineSegment(sketch, "E346", {"start": v(18.76, 13.67) * mm, "end": v(18.8, 13.72) * mm});
            skLineSegment(sketch, "E347", {"start": v(18.8, 13.72) * mm, "end": v(18.83, 13.78) * mm});
            skLineSegment(sketch, "E348", {"start": v(18.83, 13.78) * mm, "end": v(18.87, 13.83) * mm});
            skLineSegment(sketch, "E349", {"start": v(18.87, 13.83) * mm, "end": v(18.91, 13.89) * mm});
            skLineSegment(sketch, "E350", {"start": v(18.91, 13.89) * mm, "end": v(18.95, 13.95) * mm});
            skLineSegment(sketch, "E351", {"start": v(18.95, 13.95) * mm, "end": v(19, 14.01) * mm});
            skLineSegment(sketch, "E352", {"start": v(19, 14.01) * mm, "end": v(19.03, 14.07) * mm});
            skLineSegment(sketch, "E353", {"start": v(19.03, 14.07) * mm, "end": v(19.07, 14.14) * mm});
            skLineSegment(sketch, "E354", {"start": v(19.07, 14.14) * mm, "end": v(19.11, 14.2) * mm});
            skLineSegment(sketch, "E355", {"start": v(19.11, 14.2) * mm, "end": v(19.15, 14.27) * mm});
            skLineSegment(sketch, "E356", {"start": v(19.15, 14.27) * mm, "end": v(19.2, 14.34) * mm});
            skLineSegment(sketch, "E357", {"start": v(19.2, 14.34) * mm, "end": v(19.23, 14.42) * mm});
            skLineSegment(sketch, "E358", {"start": v(19.23, 14.42) * mm, "end": v(19.3, 14.52) * mm});
            skLineSegment(sketch, "E359", {"start": v(19.3, 14.52) * mm, "end": v(18.95, 14.96) * mm});
            skLineSegment(sketch, "E360", {"start": v(18.95, 14.96) * mm, "end": v(18.84, 14.93) * mm});
            skLineSegment(sketch, "E361", {"start": v(18.84, 14.93) * mm, "end": v(18.76, 14.9) * mm});
            skLineSegment(sketch, "E362", {"start": v(18.76, 14.9) * mm, "end": v(18.68, 14.88) * mm});
            skLineSegment(sketch, "E363", {"start": v(18.68, 14.88) * mm, "end": v(18.6, 14.86) * mm});
            skLineSegment(sketch, "E364", {"start": v(18.6, 14.86) * mm, "end": v(18.53, 14.84) * mm});
            skLineSegment(sketch, "E365", {"start": v(18.53, 14.84) * mm, "end": v(18.46, 14.82) * mm});
            skLineSegment(sketch, "E366", {"start": v(18.46, 14.82) * mm, "end": v(18.39, 14.8) * mm});
            skLineSegment(sketch, "E367", {"start": v(18.39, 14.8) * mm, "end": v(18.32, 14.77) * mm});
            skLineSegment(sketch, "E368", {"start": v(18.32, 14.77) * mm, "end": v(18.25, 14.75) * mm});
            skLineSegment(sketch, "E369", {"start": v(18.25, 14.75) * mm, "end": v(18.18, 14.73) * mm});
            skLineSegment(sketch, "E370", {"start": v(18.18, 14.73) * mm, "end": v(18.12, 14.7) * mm});
            skLineSegment(sketch, "E371", {"start": v(18.12, 14.7) * mm, "end": v(18.06, 14.68) * mm});
            skLineSegment(sketch, "E372", {"start": v(18.06, 14.68) * mm, "end": v(18, 14.66) * mm});
            skLineSegment(sketch, "E373", {"start": v(18, 14.66) * mm, "end": v(17.94, 14.64) * mm});
            skLineSegment(sketch, "E374", {"start": v(17.94, 14.64) * mm, "end": v(17.88, 14.61) * mm});
            skLineSegment(sketch, "E375", {"start": v(17.88, 14.61) * mm, "end": v(17.82, 14.6) * mm});
            skLineSegment(sketch, "E376", {"start": v(17.82, 14.6) * mm, "end": v(17.77, 14.57) * mm});
            skLineSegment(sketch, "E377", {"start": v(17.77, 14.57) * mm, "end": v(17.72, 14.55) * mm});
            skLineSegment(sketch, "E378", {"start": v(17.72, 14.55) * mm, "end": v(17.67, 14.53) * mm});
            skLineSegment(sketch, "E379", {"start": v(17.67, 14.53) * mm, "end": v(17.62, 14.5) * mm});
            skLineSegment(sketch, "E380", {"start": v(17.62, 14.5) * mm, "end": v(17.53, 14.46) * mm});
            skLineSegment(sketch, "E381", {"start": v(17.53, 14.46) * mm, "end": v(17.45, 14.42) * mm});
            skLineSegment(sketch, "E382", {"start": v(17.45, 14.42) * mm, "end": v(17.39, 14.4) * mm});
            skArc(sketch, "E383", {"start": v(17.39, 14.4) * mm, "mid": v(17, 14.43) * mm, "end": v(17.03, 14.8) * mm});
            skLineSegment(sketch, "E384", {"start": v(17.03, 14.8) * mm, "end": v(17.07, 14.86) * mm});
            skLineSegment(sketch, "E385", {"start": v(17.07, 14.86) * mm, "end": v(17.13, 14.94) * mm});
            skLineSegment(sketch, "E386", {"start": v(17.13, 14.94) * mm, "end": v(17.18, 15.02) * mm});
            skLineSegment(sketch, "E387", {"start": v(17.18, 15.02) * mm, "end": v(17.21, 15.07) * mm});
            skLineSegment(sketch, "E388", {"start": v(17.21, 15.07) * mm, "end": v(17.24, 15.11) * mm});
            skLineSegment(sketch, "E389", {"start": v(17.24, 15.11) * mm, "end": v(17.27, 15.16) * mm});
            skLineSegment(sketch, "E390", {"start": v(17.27, 15.16) * mm, "end": v(17.3, 15.2) * mm});
            skLineSegment(sketch, "E391", {"start": v(17.3, 15.2) * mm, "end": v(17.33, 15.26) * mm});
            skLineSegment(sketch, "E392", {"start": v(17.33, 15.26) * mm, "end": v(17.36, 15.31) * mm});
            skLineSegment(sketch, "E393", {"start": v(17.36, 15.31) * mm, "end": v(17.4, 15.37) * mm});
            skLineSegment(sketch, "E394", {"start": v(17.4, 15.37) * mm, "end": v(17.43, 15.42) * mm});
            skLineSegment(sketch, "E395", {"start": v(17.43, 15.42) * mm, "end": v(17.46, 15.48) * mm});
            skLineSegment(sketch, "E396", {"start": v(17.46, 15.48) * mm, "end": v(17.5, 15.54) * mm});
            skLineSegment(sketch, "E397", {"start": v(17.5, 15.54) * mm, "end": v(17.53, 15.6) * mm});
            skLineSegment(sketch, "E398", {"start": v(17.53, 15.6) * mm, "end": v(17.56, 15.66) * mm});
            skLineSegment(sketch, "E399", {"start": v(17.56, 15.66) * mm, "end": v(17.6, 15.73) * mm});
            skLineSegment(sketch, "E400", {"start": v(17.6, 15.73) * mm, "end": v(17.63, 15.8) * mm});
            skLineSegment(sketch, "E401", {"start": v(17.63, 15.8) * mm, "end": v(17.66, 15.86) * mm});
            skLineSegment(sketch, "E402", {"start": v(17.66, 15.86) * mm, "end": v(17.7, 15.93) * mm});
            skLineSegment(sketch, "E403", {"start": v(17.7, 15.93) * mm, "end": v(17.73, 16) * mm});
            skLineSegment(sketch, "E404", {"start": v(17.73, 16) * mm, "end": v(17.77, 16.08) * mm});
            skLineSegment(sketch, "E405", {"start": v(17.77, 16.08) * mm, "end": v(17.8, 16.15) * mm});
            skLineSegment(sketch, "E406", {"start": v(17.8, 16.15) * mm, "end": v(17.85, 16.26) * mm});
            skLineSegment(sketch, "E407", {"start": v(17.85, 16.26) * mm, "end": v(17.47, 16.67) * mm});
            skLineSegment(sketch, "E408", {"start": v(17.47, 16.67) * mm, "end": v(17.36, 16.63) * mm});
            skLineSegment(sketch, "E409", {"start": v(17.36, 16.63) * mm, "end": v(17.28, 16.6) * mm});
            skLineSegment(sketch, "E410", {"start": v(17.28, 16.6) * mm, "end": v(17.2, 16.57) * mm});
            skLineSegment(sketch, "E411", {"start": v(17.2, 16.57) * mm, "end": v(17.13, 16.54) * mm});
            skLineSegment(sketch, "E412", {"start": v(17.13, 16.54) * mm, "end": v(17.06, 16.51) * mm});
            skLineSegment(sketch, "E413", {"start": v(17.06, 16.51) * mm, "end": v(16.99, 16.48) * mm});
            skLineSegment(sketch, "E414", {"start": v(16.99, 16.48) * mm, "end": v(16.92, 16.45) * mm});
            skLineSegment(sketch, "E415", {"start": v(16.92, 16.45) * mm, "end": v(16.85, 16.42) * mm});
            skLineSegment(sketch, "E416", {"start": v(16.85, 16.42) * mm, "end": v(16.79, 16.4) * mm});
            skLineSegment(sketch, "E417", {"start": v(16.79, 16.4) * mm, "end": v(16.72, 16.37) * mm});
            skLineSegment(sketch, "E418", {"start": v(16.72, 16.37) * mm, "end": v(16.66, 16.34) * mm});
            skLineSegment(sketch, "E419", {"start": v(16.66, 16.34) * mm, "end": v(16.6, 16.3) * mm});
            skLineSegment(sketch, "E420", {"start": v(16.6, 16.3) * mm, "end": v(16.54, 16.28) * mm});
            skLineSegment(sketch, "E421", {"start": v(16.54, 16.28) * mm, "end": v(16.49, 16.25) * mm});
            skLineSegment(sketch, "E422", {"start": v(16.49, 16.25) * mm, "end": v(16.43, 16.22) * mm});
            skLineSegment(sketch, "E423", {"start": v(16.43, 16.22) * mm, "end": v(16.38, 16.2) * mm});
            skLineSegment(sketch, "E424", {"start": v(16.38, 16.2) * mm, "end": v(16.33, 16.17) * mm});
            skLineSegment(sketch, "E425", {"start": v(16.33, 16.17) * mm, "end": v(16.28, 16.14) * mm});
            skLineSegment(sketch, "E426", {"start": v(16.28, 16.14) * mm, "end": v(16.23, 16.12) * mm});
            skLineSegment(sketch, "E427", {"start": v(16.23, 16.12) * mm, "end": v(16.19, 16.1) * mm});
            skLineSegment(sketch, "E428", {"start": v(16.19, 16.1) * mm, "end": v(16.1, 16.04) * mm});
            skLineSegment(sketch, "E429", {"start": v(16.1, 16.04) * mm, "end": v(16.02, 16) * mm});
            skLineSegment(sketch, "E430", {"start": v(16.02, 16) * mm, "end": v(15.96, 15.96) * mm});
            skArc(sketch, "E431", {"start": v(15.96, 15.96) * mm, "mid": v(15.58, 15.96) * mm, "end": v(15.57, 16.34) * mm});
            skLineSegment(sketch, "E432", {"start": v(15.57, 16.34) * mm, "end": v(15.6, 16.4) * mm});
            skLineSegment(sketch, "E433", {"start": v(15.6, 16.4) * mm, "end": v(15.65, 16.48) * mm});
            skLineSegment(sketch, "E434", {"start": v(15.65, 16.48) * mm, "end": v(15.7, 16.57) * mm});
            skLineSegment(sketch, "E435", {"start": v(15.7, 16.57) * mm, "end": v(15.73, 16.61) * mm});
            skLineSegment(sketch, "E436", {"start": v(15.73, 16.61) * mm, "end": v(15.75, 16.66) * mm});
            skLineSegment(sketch, "E437", {"start": v(15.75, 16.66) * mm, "end": v(15.78, 16.71) * mm});
            skLineSegment(sketch, "E438", {"start": v(15.78, 16.71) * mm, "end": v(15.8, 16.76) * mm});
            skLineSegment(sketch, "E439", {"start": v(15.8, 16.76) * mm, "end": v(15.83, 16.82) * mm});
            skLineSegment(sketch, "E440", {"start": v(15.83, 16.82) * mm, "end": v(15.85, 16.87) * mm});
            skLineSegment(sketch, "E441", {"start": v(15.85, 16.87) * mm, "end": v(15.88, 16.93) * mm});
            skLineSegment(sketch, "E442", {"start": v(15.88, 16.93) * mm, "end": v(15.9, 16.99) * mm});
            skLineSegment(sketch, "E443", {"start": v(15.9, 16.99) * mm, "end": v(15.94, 17.05) * mm});
            skLineSegment(sketch, "E444", {"start": v(15.94, 17.05) * mm, "end": v(15.96, 17.1) * mm});
            skLineSegment(sketch, "E445", {"start": v(15.96, 17.1) * mm, "end": v(15.99, 17.17) * mm});
            skLineSegment(sketch, "E446", {"start": v(15.99, 17.17) * mm, "end": v(16.02, 17.24) * mm});
            skLineSegment(sketch, "E447", {"start": v(16.02, 17.24) * mm, "end": v(16.04, 17.3) * mm});
            skLineSegment(sketch, "E448", {"start": v(16.04, 17.3) * mm, "end": v(16.07, 17.38) * mm});
            skLineSegment(sketch, "E449", {"start": v(16.07, 17.38) * mm, "end": v(16.1, 17.45) * mm});
            skLineSegment(sketch, "E450", {"start": v(16.1, 17.45) * mm, "end": v(16.13, 17.52) * mm});
            skLineSegment(sketch, "E451", {"start": v(16.13, 17.52) * mm, "end": v(16.15, 17.6) * mm});
            skLineSegment(sketch, "E452", {"start": v(16.15, 17.6) * mm, "end": v(16.18, 17.67) * mm});
            skLineSegment(sketch, "E453", {"start": v(16.18, 17.67) * mm, "end": v(16.2, 17.75) * mm});
            skLineSegment(sketch, "E454", {"start": v(16.2, 17.75) * mm, "end": v(16.25, 17.86) * mm});
            skLineSegment(sketch, "E455", {"start": v(16.25, 17.86) * mm, "end": v(15.83, 18.23) * mm});
            skLineSegment(sketch, "E456", {"start": v(15.83, 18.23) * mm, "end": v(15.73, 18.18) * mm});
            skLineSegment(sketch, "E457", {"start": v(15.73, 18.18) * mm, "end": v(15.65, 18.14) * mm});
            skLineSegment(sketch, "E458", {"start": v(15.65, 18.14) * mm, "end": v(15.58, 18.1) * mm});
            skLineSegment(sketch, "E459", {"start": v(15.58, 18.1) * mm, "end": v(15.5, 18.07) * mm});
            skLineSegment(sketch, "E460", {"start": v(15.5, 18.07) * mm, "end": v(15.44, 18.04) * mm});
            skLineSegment(sketch, "E461", {"start": v(15.44, 18.04) * mm, "end": v(15.37, 18) * mm});
            skLineSegment(sketch, "E462", {"start": v(15.37, 18) * mm, "end": v(15.3, 17.97) * mm});
            skLineSegment(sketch, "E463", {"start": v(15.3, 17.97) * mm, "end": v(15.24, 17.93) * mm});
            skLineSegment(sketch, "E464", {"start": v(15.24, 17.93) * mm, "end": v(15.18, 17.9) * mm});
            skLineSegment(sketch, "E465", {"start": v(15.18, 17.9) * mm, "end": v(15.12, 17.86) * mm});
            skLineSegment(sketch, "E466", {"start": v(15.12, 17.86) * mm, "end": v(15.06, 17.83) * mm});
            skLineSegment(sketch, "E467", {"start": v(15.06, 17.83) * mm, "end": v(15, 17.8) * mm});
            skLineSegment(sketch, "E468", {"start": v(15, 17.8) * mm, "end": v(14.95, 17.76) * mm});
            skLineSegment(sketch, "E469", {"start": v(14.95, 17.76) * mm, "end": v(14.9, 17.73) * mm});
            skLineSegment(sketch, "E470", {"start": v(14.9, 17.73) * mm, "end": v(14.84, 17.7) * mm});
            skLineSegment(sketch, "E471", {"start": v(14.84, 17.7) * mm, "end": v(14.8, 17.66) * mm});
            skLineSegment(sketch, "E472", {"start": v(14.8, 17.66) * mm, "end": v(14.74, 17.63) * mm});
            skLineSegment(sketch, "E473", {"start": v(14.74, 17.63) * mm, "end": v(14.7, 17.6) * mm});
            skLineSegment(sketch, "E474", {"start": v(14.7, 17.6) * mm, "end": v(14.65, 17.57) * mm});
            skLineSegment(sketch, "E475", {"start": v(14.65, 17.57) * mm, "end": v(14.6, 17.54) * mm});
            skLineSegment(sketch, "E476", {"start": v(14.6, 17.54) * mm, "end": v(14.53, 17.48) * mm});
            skLineSegment(sketch, "E477", {"start": v(14.53, 17.48) * mm, "end": v(14.45, 17.42) * mm});
            skLineSegment(sketch, "E478", {"start": v(14.45, 17.42) * mm, "end": v(14.4, 17.38) * mm});
            skArc(sketch, "E479", {"start": v(14.4, 17.38) * mm, "mid": v(14.02, 17.35) * mm, "end": v(13.97, 17.73) * mm});
            skLineSegment(sketch, "E480", {"start": v(13.97, 17.73) * mm, "end": v(14, 17.79) * mm});
            skLineSegment(sketch, "E481", {"start": v(14, 17.79) * mm, "end": v(14.04, 17.87) * mm});
            skLineSegment(sketch, "E482", {"start": v(14.04, 17.87) * mm, "end": v(14.08, 17.96) * mm});
            skLineSegment(sketch, "E483", {"start": v(14.08, 17.96) * mm, "end": v(14.1, 18.01) * mm});
            skLineSegment(sketch, "E484", {"start": v(14.1, 18.01) * mm, "end": v(14.12, 18.06) * mm});
            skLineSegment(sketch, "E485", {"start": v(14.12, 18.06) * mm, "end": v(14.14, 18.11) * mm});
            skLineSegment(sketch, "E486", {"start": v(14.14, 18.11) * mm, "end": v(14.16, 18.17) * mm});
            skLineSegment(sketch, "E487", {"start": v(14.16, 18.17) * mm, "end": v(14.18, 18.22) * mm});
            skLineSegment(sketch, "E488", {"start": v(14.18, 18.22) * mm, "end": v(14.2, 18.28) * mm});
            skLineSegment(sketch, "E489", {"start": v(14.2, 18.28) * mm, "end": v(14.23, 18.34) * mm});
            skLineSegment(sketch, "E490", {"start": v(14.23, 18.34) * mm, "end": v(14.25, 18.4) * mm});
            skLineSegment(sketch, "E491", {"start": v(14.25, 18.4) * mm, "end": v(14.27, 18.46) * mm});
            skLineSegment(sketch, "E492", {"start": v(14.27, 18.46) * mm, "end": v(14.3, 18.53) * mm});
            skLineSegment(sketch, "E493", {"start": v(14.3, 18.53) * mm, "end": v(14.31, 18.6) * mm});
            skLineSegment(sketch, "E494", {"start": v(14.31, 18.6) * mm, "end": v(14.33, 18.66) * mm});
            skLineSegment(sketch, "E495", {"start": v(14.33, 18.66) * mm, "end": v(14.35, 18.73) * mm});
            skLineSegment(sketch, "E496", {"start": v(14.35, 18.73) * mm, "end": v(14.37, 18.8) * mm});
            skLineSegment(sketch, "E497", {"start": v(14.37, 18.8) * mm, "end": v(14.4, 18.88) * mm});
            skLineSegment(sketch, "E498", {"start": v(14.4, 18.88) * mm, "end": v(14.42, 18.95) * mm});
            skLineSegment(sketch, "E499", {"start": v(14.42, 18.95) * mm, "end": v(14.44, 19.03) * mm});
            skLineSegment(sketch, "E500", {"start": v(14.44, 19.03) * mm, "end": v(14.46, 19.11) * mm});
            skLineSegment(sketch, "E501", {"start": v(14.46, 19.11) * mm, "end": v(14.48, 19.2) * mm});
            skLineSegment(sketch, "E502", {"start": v(14.48, 19.2) * mm, "end": v(14.5, 19.3) * mm});
            skLineSegment(sketch, "E503", {"start": v(14.5, 19.3) * mm, "end": v(14.06, 19.63) * mm});
            skLineSegment(sketch, "E504", {"start": v(14.06, 19.63) * mm, "end": v(13.95, 19.57) * mm});
            skLineSegment(sketch, "E505", {"start": v(13.95, 19.57) * mm, "end": v(13.88, 19.53) * mm});
            skLineSegment(sketch, "E506", {"start": v(13.88, 19.53) * mm, "end": v(13.81, 19.49) * mm});
            skLineSegment(sketch, "E507", {"start": v(13.81, 19.49) * mm, "end": v(13.75, 19.45) * mm});
            skLineSegment(sketch, "E508", {"start": v(13.75, 19.45) * mm, "end": v(13.68, 19.4) * mm});
            skLineSegment(sketch, "E509", {"start": v(13.68, 19.4) * mm, "end": v(13.62, 19.36) * mm});
            skLineSegment(sketch, "E510", {"start": v(13.62, 19.36) * mm, "end": v(13.55, 19.32) * mm});
            skLineSegment(sketch, "E511", {"start": v(13.55, 19.32) * mm, "end": v(13.5, 19.28) * mm});
            skLineSegment(sketch, "E512", {"start": v(13.5, 19.28) * mm, "end": v(13.44, 19.24) * mm});
            skLineSegment(sketch, "E513", {"start": v(13.44, 19.24) * mm, "end": v(13.38, 19.2) * mm});
            skLineSegment(sketch, "E514", {"start": v(13.38, 19.2) * mm, "end": v(13.32, 19.16) * mm});
            skLineSegment(sketch, "E515", {"start": v(13.32, 19.16) * mm, "end": v(13.27, 19.12) * mm});
            skLineSegment(sketch, "E516", {"start": v(13.27, 19.12) * mm, "end": v(13.22, 19.08) * mm});
            skLineSegment(sketch, "E517", {"start": v(13.22, 19.08) * mm, "end": v(13.17, 19.04) * mm});
            skLineSegment(sketch, "E518", {"start": v(13.17, 19.04) * mm, "end": v(13.12, 19) * mm});
            skLineSegment(sketch, "E519", {"start": v(13.12, 19) * mm, "end": v(13.07, 18.97) * mm});
            skLineSegment(sketch, "E520", {"start": v(13.07, 18.97) * mm, "end": v(13.03, 18.93) * mm});
            skLineSegment(sketch, "E521", {"start": v(13.03, 18.93) * mm, "end": v(12.98, 18.9) * mm});
            skLineSegment(sketch, "E522", {"start": v(12.98, 18.9) * mm, "end": v(12.94, 18.86) * mm});
            skLineSegment(sketch, "E523", {"start": v(12.94, 18.86) * mm, "end": v(12.9, 18.83) * mm});
            skLineSegment(sketch, "E524", {"start": v(12.9, 18.83) * mm, "end": v(12.83, 18.76) * mm});
            skLineSegment(sketch, "E525", {"start": v(12.83, 18.76) * mm, "end": v(12.76, 18.7) * mm});
            skLineSegment(sketch, "E526", {"start": v(12.76, 18.7) * mm, "end": v(12.7, 18.65) * mm});
            skArc(sketch, "E527", {"start": v(12.7, 18.65) * mm, "mid": v(12.33, 18.59) * mm, "end": v(12.25, 18.96) * mm});
            skLineSegment(sketch, "E528", {"start": v(12.25, 18.96) * mm, "end": v(12.27, 19.02) * mm});
            skLineSegment(sketch, "E529", {"start": v(12.27, 19.02) * mm, "end": v(12.3, 19.1) * mm});
            skLineSegment(sketch, "E530", {"start": v(12.3, 19.1) * mm, "end": v(12.34, 19.2) * mm});
            skLineSegment(sketch, "E531", {"start": v(12.34, 19.2) * mm, "end": v(12.35, 19.25) * mm});
            skLineSegment(sketch, "E532", {"start": v(12.35, 19.25) * mm, "end": v(12.37, 19.3) * mm});
            skLineSegment(sketch, "E533", {"start": v(12.37, 19.3) * mm, "end": v(12.38, 19.36) * mm});
            skLineSegment(sketch, "E534", {"start": v(12.38, 19.36) * mm, "end": v(12.4, 19.42) * mm});
            skLineSegment(sketch, "E535", {"start": v(12.4, 19.42) * mm, "end": v(12.41, 19.47) * mm});
            skLineSegment(sketch, "E536", {"start": v(12.41, 19.47) * mm, "end": v(12.43, 19.53) * mm});
            skLineSegment(sketch, "E537", {"start": v(12.43, 19.53) * mm, "end": v(12.45, 19.6) * mm});
            skLineSegment(sketch, "E538", {"start": v(12.45, 19.6) * mm, "end": v(12.46, 19.66) * mm});
            skLineSegment(sketch, "E539", {"start": v(12.46, 19.66) * mm, "end": v(12.48, 19.72) * mm});
            skLineSegment(sketch, "E540", {"start": v(12.48, 19.72) * mm, "end": v(12.5, 19.79) * mm});
            skLineSegment(sketch, "E541", {"start": v(12.5, 19.79) * mm, "end": v(12.5, 19.85) * mm});
            skLineSegment(sketch, "E542", {"start": v(12.5, 19.85) * mm, "end": v(12.52, 19.92) * mm});
            skLineSegment(sketch, "E543", {"start": v(12.52, 19.92) * mm, "end": v(12.54, 20) * mm});
            skLineSegment(sketch, "E544", {"start": v(12.54, 20) * mm, "end": v(12.55, 20.07) * mm});
            skLineSegment(sketch, "E545", {"start": v(12.55, 20.07) * mm, "end": v(12.56, 20.14) * mm});
            skLineSegment(sketch, "E546", {"start": v(12.56, 20.14) * mm, "end": v(12.58, 20.22) * mm});
            skLineSegment(sketch, "E547", {"start": v(12.58, 20.22) * mm, "end": v(12.59, 20.3) * mm});
            skLineSegment(sketch, "E548", {"start": v(12.59, 20.3) * mm, "end": v(12.6, 20.38) * mm});
            skLineSegment(sketch, "E549", {"start": v(12.6, 20.38) * mm, "end": v(12.61, 20.46) * mm});
            skLineSegment(sketch, "E550", {"start": v(12.61, 20.46) * mm, "end": v(12.63, 20.58) * mm});
            skLineSegment(sketch, "E551", {"start": v(12.63, 20.58) * mm, "end": v(12.16, 20.86) * mm});
            skLineSegment(sketch, "E552", {"start": v(12.16, 20.86) * mm, "end": v(12.06, 20.8) * mm});
            skLineSegment(sketch, "E553", {"start": v(12.06, 20.8) * mm, "end": v(12, 20.75) * mm});
            skLineSegment(sketch, "E554", {"start": v(12, 20.75) * mm, "end": v(11.93, 20.7) * mm});
            skLineSegment(sketch, "E555", {"start": v(11.93, 20.7) * mm, "end": v(11.86, 20.65) * mm});
            skLineSegment(sketch, "E556", {"start": v(11.86, 20.65) * mm, "end": v(11.8, 20.6) * mm});
            skLineSegment(sketch, "E557", {"start": v(11.8, 20.6) * mm, "end": v(11.74, 20.55) * mm});
            skLineSegment(sketch, "E558", {"start": v(11.74, 20.55) * mm, "end": v(11.69, 20.5) * mm});
            skLineSegment(sketch, "E559", {"start": v(11.69, 20.5) * mm, "end": v(11.63, 20.46) * mm});
            skLineSegment(sketch, "E560", {"start": v(11.63, 20.46) * mm, "end": v(11.57, 20.41) * mm});
            skLineSegment(sketch, "E561", {"start": v(11.57, 20.41) * mm, "end": v(11.52, 20.37) * mm});
            skLineSegment(sketch, "E562", {"start": v(11.52, 20.37) * mm, "end": v(11.47, 20.32) * mm});
            skLineSegment(sketch, "E563", {"start": v(11.47, 20.32) * mm, "end": v(11.42, 20.28) * mm});
            skLineSegment(sketch, "E564", {"start": v(11.42, 20.28) * mm, "end": v(11.37, 20.24) * mm});
            skLineSegment(sketch, "E565", {"start": v(11.37, 20.24) * mm, "end": v(11.33, 20.2) * mm});
            skLineSegment(sketch, "E566", {"start": v(11.33, 20.2) * mm, "end": v(11.28, 20.15) * mm});
            skLineSegment(sketch, "E567", {"start": v(11.28, 20.15) * mm, "end": v(11.24, 20.11) * mm});
            skLineSegment(sketch, "E568", {"start": v(11.24, 20.11) * mm, "end": v(11.2, 20.07) * mm});
            skLineSegment(sketch, "E569", {"start": v(11.2, 20.07) * mm, "end": v(11.16, 20.03) * mm});
            skLineSegment(sketch, "E570", {"start": v(11.16, 20.03) * mm, "end": v(11.12, 20) * mm});
            skLineSegment(sketch, "E571", {"start": v(11.12, 20) * mm, "end": v(11.08, 19.95) * mm});
            skLineSegment(sketch, "E572", {"start": v(11.08, 19.95) * mm, "end": v(11.01, 19.88) * mm});
            skLineSegment(sketch, "E573", {"start": v(11.01, 19.88) * mm, "end": v(10.95, 19.81) * mm});
            skLineSegment(sketch, "E574", {"start": v(10.95, 19.81) * mm, "end": v(10.9, 19.76) * mm});
            skArc(sketch, "E575", {"start": v(10.9, 19.76) * mm, "mid": v(10.54, 19.66) * mm, "end": v(10.42, 20.02) * mm});
            skLineSegment(sketch, "E576", {"start": v(10.42, 20.02) * mm, "end": v(10.44, 20.09) * mm});
            skLineSegment(sketch, "E577", {"start": v(10.44, 20.09) * mm, "end": v(10.46, 20.18) * mm});
            skLineSegment(sketch, "E578", {"start": v(10.46, 20.18) * mm, "end": v(10.48, 20.27) * mm});
            skLineSegment(sketch, "E579", {"start": v(10.48, 20.27) * mm, "end": v(10.5, 20.33) * mm});
            skLineSegment(sketch, "E580", {"start": v(10.5, 20.33) * mm, "end": v(10.5, 20.38) * mm});
            skLineSegment(sketch, "E581", {"start": v(10.5, 20.38) * mm, "end": v(10.52, 20.44) * mm});
            skLineSegment(sketch, "E582", {"start": v(10.52, 20.44) * mm, "end": v(10.53, 20.5) * mm});
            skLineSegment(sketch, "E583", {"start": v(10.53, 20.5) * mm, "end": v(10.54, 20.55) * mm});
            skLineSegment(sketch, "E584", {"start": v(10.54, 20.55) * mm, "end": v(10.55, 20.61) * mm});
            skLineSegment(sketch, "E585", {"start": v(10.55, 20.61) * mm, "end": v(10.56, 20.67) * mm});
            skLineSegment(sketch, "E586", {"start": v(10.56, 20.67) * mm, "end": v(10.57, 20.74) * mm});
            skLineSegment(sketch, "E587", {"start": v(10.57, 20.74) * mm, "end": v(10.58, 20.8) * mm});
            skLineSegment(sketch, "E588", {"start": v(10.58, 20.8) * mm, "end": v(10.58, 20.87) * mm});
            skLineSegment(sketch, "E589", {"start": v(10.58, 20.87) * mm, "end": v(10.6, 20.94) * mm});
            skLineSegment(sketch, "E590", {"start": v(10.6, 20.94) * mm, "end": v(10.6, 21.01) * mm});
            skLineSegment(sketch, "E591", {"start": v(10.6, 21.01) * mm, "end": v(10.6, 21.08) * mm});
            skLineSegment(sketch, "E592", {"start": v(10.6, 21.08) * mm, "end": v(10.62, 21.16) * mm});
            skLineSegment(sketch, "E593", {"start": v(10.62, 21.16) * mm, "end": v(10.62, 21.23) * mm});
            skLineSegment(sketch, "E594", {"start": v(10.62, 21.23) * mm, "end": v(10.63, 21.31) * mm});
            skLineSegment(sketch, "E595", {"start": v(10.63, 21.31) * mm, "end": v(10.63, 21.4) * mm});
            skLineSegment(sketch, "E596", {"start": v(10.63, 21.4) * mm, "end": v(10.64, 21.47) * mm});
            skLineSegment(sketch, "E597", {"start": v(10.64, 21.47) * mm, "end": v(10.64, 21.55) * mm});
            skLineSegment(sketch, "E598", {"start": v(10.64, 21.55) * mm, "end": v(10.65, 21.67) * mm});
            skLineSegment(sketch, "E599", {"start": v(10.65, 21.67) * mm, "end": v(10.15, 21.91) * mm});
            skLineSegment(sketch, "E600", {"start": v(10.15, 21.91) * mm, "end": v(10.06, 21.83) * mm});
            skLineSegment(sketch, "E601", {"start": v(10.06, 21.83) * mm, "end": v(10, 21.78) * mm});
            skLineSegment(sketch, "E602", {"start": v(10, 21.78) * mm, "end": v(9.94, 21.72) * mm});
            skLineSegment(sketch, "E603", {"start": v(9.94, 21.72) * mm, "end": v(9.88, 21.67) * mm});
            skLineSegment(sketch, "E604", {"start": v(9.88, 21.67) * mm, "end": v(9.82, 21.62) * mm});
            skLineSegment(sketch, "E605", {"start": v(9.82, 21.62) * mm, "end": v(9.77, 21.56) * mm});
            skLineSegment(sketch, "E606", {"start": v(9.77, 21.56) * mm, "end": v(9.71, 21.5) * mm});
            skLineSegment(sketch, "E607", {"start": v(9.71, 21.5) * mm, "end": v(9.66, 21.46) * mm});
            skLineSegment(sketch, "E608", {"start": v(9.66, 21.46) * mm, "end": v(9.61, 21.4) * mm});
            skLineSegment(sketch, "E609", {"start": v(9.61, 21.4) * mm, "end": v(9.56, 21.36) * mm});
            skLineSegment(sketch, "E610", {"start": v(9.56, 21.36) * mm, "end": v(9.52, 21.3) * mm});
            skLineSegment(sketch, "E611", {"start": v(9.52, 21.3) * mm, "end": v(9.47, 21.26) * mm});
            skLineSegment(sketch, "E612", {"start": v(9.47, 21.26) * mm, "end": v(9.43, 21.21) * mm});
            skLineSegment(sketch, "E613", {"start": v(9.43, 21.21) * mm, "end": v(9.39, 21.17) * mm});
            skLineSegment(sketch, "E614", {"start": v(9.39, 21.17) * mm, "end": v(9.35, 21.12) * mm});
            skLineSegment(sketch, "E615", {"start": v(9.35, 21.12) * mm, "end": v(9.3, 21.07) * mm});
            skLineSegment(sketch, "E616", {"start": v(9.3, 21.07) * mm, "end": v(9.27, 21.03) * mm});
            skLineSegment(sketch, "E617", {"start": v(9.27, 21.03) * mm, "end": v(9.23, 20.99) * mm});
            skLineSegment(sketch, "E618", {"start": v(9.23, 20.99) * mm, "end": v(9.2, 20.95) * mm});
            skLineSegment(sketch, "E619", {"start": v(9.2, 20.95) * mm, "end": v(9.16, 20.9) * mm});
            skLineSegment(sketch, "E620", {"start": v(9.16, 20.9) * mm, "end": v(9.1, 20.83) * mm});
            skLineSegment(sketch, "E621", {"start": v(9.1, 20.83) * mm, "end": v(9.04, 20.75) * mm});
            skLineSegment(sketch, "E622", {"start": v(9.04, 20.75) * mm, "end": v(9, 20.7) * mm});
            skArc(sketch, "E623", {"start": v(9, 20.7) * mm, "mid": v(8.65, 20.56) * mm, "end": v(8.5, 20.91) * mm});
            skLineSegment(sketch, "E624", {"start": v(8.5, 20.91) * mm, "end": v(8.51, 20.98) * mm});
            skLineSegment(sketch, "E625", {"start": v(8.51, 20.98) * mm, "end": v(8.53, 21.07) * mm});
            skLineSegment(sketch, "E626", {"start": v(8.53, 21.07) * mm, "end": v(8.54, 21.17) * mm});
            skLineSegment(sketch, "E627", {"start": v(8.54, 21.17) * mm, "end": v(8.54, 21.22) * mm});
            skLineSegment(sketch, "E628", {"start": v(8.54, 21.22) * mm, "end": v(8.55, 21.27) * mm});
            skLineSegment(sketch, "E629", {"start": v(8.55, 21.27) * mm, "end": v(8.56, 21.33) * mm});
            skLineSegment(sketch, "E630", {"start": v(8.56, 21.33) * mm, "end": v(8.56, 21.39) * mm});
            skLineSegment(sketch, "E631", {"start": v(8.56, 21.39) * mm, "end": v(8.57, 21.45) * mm});
            skLineSegment(sketch, "E632", {"start": v(8.57, 21.45) * mm, "end": v(8.57, 21.5) * mm});
            skLineSegment(sketch, "E633", {"start": v(8.57, 21.5) * mm, "end": v(8.57, 21.57) * mm});
            skLineSegment(sketch, "E634", {"start": v(8.57, 21.57) * mm, "end": v(8.58, 21.64) * mm});
            skLineSegment(sketch, "E635", {"start": v(8.58, 21.64) * mm, "end": v(8.58, 21.7) * mm});
            skLineSegment(sketch, "E636", {"start": v(8.58, 21.7) * mm, "end": v(8.58, 21.77) * mm});
            skLineSegment(sketch, "E637", {"start": v(8.58, 21.77) * mm, "end": v(8.59, 21.84) * mm});
            skLineSegment(sketch, "E638", {"start": v(8.59, 21.84) * mm, "end": v(8.59, 21.91) * mm});
            skLineSegment(sketch, "E639", {"start": v(8.59, 21.91) * mm, "end": v(8.59, 21.98) * mm});
            skLineSegment(sketch, "E640", {"start": v(8.59, 21.98) * mm, "end": v(8.59, 22.06) * mm});
            skLineSegment(sketch, "E641", {"start": v(8.59, 22.06) * mm, "end": v(8.59, 22.14) * mm});
            skLineSegment(sketch, "E642", {"start": v(8.59, 22.14) * mm, "end": v(8.59, 22.21) * mm});
            skLineSegment(sketch, "E643", {"start": v(8.59, 22.21) * mm, "end": v(8.58, 22.3) * mm});
            skLineSegment(sketch, "E644", {"start": v(8.58, 22.3) * mm, "end": v(8.58, 22.37) * mm});
            skLineSegment(sketch, "E645", {"start": v(8.58, 22.37) * mm, "end": v(8.58, 22.46) * mm});
            skLineSegment(sketch, "E646", {"start": v(8.58, 22.46) * mm, "end": v(8.57, 22.58) * mm});
            skLineSegment(sketch, "E647", {"start": v(8.57, 22.58) * mm, "end": v(8.05, 22.77) * mm});
            skLineSegment(sketch, "E648", {"start": v(8.05, 22.77) * mm, "end": v(7.97, 22.68) * mm});
            skLineSegment(sketch, "E649", {"start": v(7.97, 22.68) * mm, "end": v(7.91, 22.62) * mm});
            skLineSegment(sketch, "E650", {"start": v(7.91, 22.62) * mm, "end": v(7.86, 22.56) * mm});
            skLineSegment(sketch, "E651", {"start": v(7.86, 22.56) * mm, "end": v(7.8, 22.5) * mm});
            skLineSegment(sketch, "E652", {"start": v(7.8, 22.5) * mm, "end": v(7.76, 22.44) * mm});
            skLineSegment(sketch, "E653", {"start": v(7.76, 22.44) * mm, "end": v(7.7, 22.38) * mm});
            skLineSegment(sketch, "E654", {"start": v(7.7, 22.38) * mm, "end": v(7.66, 22.33) * mm});
            skLineSegment(sketch, "E655", {"start": v(7.66, 22.33) * mm, "end": v(7.61, 22.27) * mm});
            skLineSegment(sketch, "E656", {"start": v(7.61, 22.27) * mm, "end": v(7.57, 22.21) * mm});
            skLineSegment(sketch, "E657", {"start": v(7.57, 22.21) * mm, "end": v(7.52, 22.16) * mm});
            skLineSegment(sketch, "E658", {"start": v(7.52, 22.16) * mm, "end": v(7.48, 22.1) * mm});
            skLineSegment(sketch, "E659", {"start": v(7.48, 22.1) * mm, "end": v(7.44, 22.05) * mm});
            skLineSegment(sketch, "E660", {"start": v(7.44, 22.05) * mm, "end": v(7.4, 22) * mm});
            skLineSegment(sketch, "E661", {"start": v(7.4, 22) * mm, "end": v(7.36, 21.95) * mm});
            skLineSegment(sketch, "E662", {"start": v(7.36, 21.95) * mm, "end": v(7.33, 21.9) * mm});
            skLineSegment(sketch, "E663", {"start": v(7.33, 21.9) * mm, "end": v(7.3, 21.85) * mm});
            skLineSegment(sketch, "E664", {"start": v(7.3, 21.85) * mm, "end": v(7.26, 21.8) * mm});
            skLineSegment(sketch, "E665", {"start": v(7.26, 21.8) * mm, "end": v(7.23, 21.76) * mm});
            skLineSegment(sketch, "E666", {"start": v(7.23, 21.76) * mm, "end": v(7.2, 21.72) * mm});
            skLineSegment(sketch, "E667", {"start": v(7.2, 21.72) * mm, "end": v(7.17, 21.67) * mm});
            skLineSegment(sketch, "E668", {"start": v(7.17, 21.67) * mm, "end": v(7.11, 21.59) * mm});
            skLineSegment(sketch, "E669", {"start": v(7.11, 21.59) * mm, "end": v(7.06, 21.5) * mm});
            skLineSegment(sketch, "E670", {"start": v(7.06, 21.5) * mm, "end": v(7.03, 21.45) * mm});
            skArc(sketch, "E671", {"start": v(7.03, 21.45) * mm, "mid": v(6.69, 21.28) * mm, "end": v(6.5, 21.62) * mm});
            skLineSegment(sketch, "E672", {"start": v(6.5, 21.62) * mm, "end": v(6.51, 21.68) * mm});
            skLineSegment(sketch, "E673", {"start": v(6.51, 21.68) * mm, "end": v(6.52, 21.77) * mm});
            skLineSegment(sketch, "E674", {"start": v(6.52, 21.77) * mm, "end": v(6.52, 21.88) * mm});
            skLineSegment(sketch, "E675", {"start": v(6.52, 21.88) * mm, "end": v(6.52, 21.93) * mm});
            skLineSegment(sketch, "E676", {"start": v(6.52, 21.93) * mm, "end": v(6.52, 21.98) * mm});
            skLineSegment(sketch, "E677", {"start": v(6.52, 21.98) * mm, "end": v(6.52, 22.04) * mm});
            skLineSegment(sketch, "E678", {"start": v(6.52, 22.04) * mm, "end": v(6.52, 22.1) * mm});
            skLineSegment(sketch, "E679", {"start": v(6.52, 22.1) * mm, "end": v(6.52, 22.16) * mm});
            skLineSegment(sketch, "E680", {"start": v(6.52, 22.16) * mm, "end": v(6.52, 22.22) * mm});
            skLineSegment(sketch, "E681", {"start": v(6.52, 22.22) * mm, "end": v(6.52, 22.28) * mm});
            skLineSegment(sketch, "E682", {"start": v(6.52, 22.28) * mm, "end": v(6.51, 22.34) * mm});
            skLineSegment(sketch, "E683", {"start": v(6.51, 22.34) * mm, "end": v(6.51, 22.41) * mm});
            skLineSegment(sketch, "E684", {"start": v(6.51, 22.41) * mm, "end": v(6.5, 22.48) * mm});
            skLineSegment(sketch, "E685", {"start": v(6.5, 22.48) * mm, "end": v(6.5, 22.55) * mm});
            skLineSegment(sketch, "E686", {"start": v(6.5, 22.55) * mm, "end": v(6.5, 22.62) * mm});
            skLineSegment(sketch, "E687", {"start": v(6.5, 22.62) * mm, "end": v(6.5, 22.7) * mm});
            skLineSegment(sketch, "E688", {"start": v(6.5, 22.7) * mm, "end": v(6.48, 22.77) * mm});
            skLineSegment(sketch, "E689", {"start": v(6.48, 22.77) * mm, "end": v(6.48, 22.84) * mm});
            skLineSegment(sketch, "E690", {"start": v(6.48, 22.84) * mm, "end": v(6.47, 22.92) * mm});
            skLineSegment(sketch, "E691", {"start": v(6.47, 22.92) * mm, "end": v(6.46, 23) * mm});
            skLineSegment(sketch, "E692", {"start": v(6.46, 23) * mm, "end": v(6.45, 23.08) * mm});
            skLineSegment(sketch, "E693", {"start": v(6.45, 23.08) * mm, "end": v(6.44, 23.16) * mm});
            skLineSegment(sketch, "E694", {"start": v(6.44, 23.16) * mm, "end": v(6.42, 23.28) * mm});
            skLineSegment(sketch, "E695", {"start": v(6.42, 23.28) * mm, "end": v(5.88, 23.42) * mm});
            skLineSegment(sketch, "E696", {"start": v(5.88, 23.42) * mm, "end": v(5.81, 23.33) * mm});
            skLineSegment(sketch, "E697", {"start": v(5.81, 23.33) * mm, "end": v(5.76, 23.26) * mm});
            skLineSegment(sketch, "E698", {"start": v(5.76, 23.26) * mm, "end": v(5.71, 23.2) * mm});
            skLineSegment(sketch, "E699", {"start": v(5.71, 23.2) * mm, "end": v(5.67, 23.13) * mm});
            skLineSegment(sketch, "E700", {"start": v(5.67, 23.13) * mm, "end": v(5.62, 23.07) * mm});
            skLineSegment(sketch, "E701", {"start": v(5.62, 23.07) * mm, "end": v(5.58, 23) * mm});
            skLineSegment(sketch, "E702", {"start": v(5.58, 23) * mm, "end": v(5.53, 22.95) * mm});
            skLineSegment(sketch, "E703", {"start": v(5.53, 22.95) * mm, "end": v(5.5, 22.88) * mm});
            skLineSegment(sketch, "E704", {"start": v(5.5, 22.88) * mm, "end": v(5.45, 22.83) * mm});
            skLineSegment(sketch, "E705", {"start": v(5.45, 22.83) * mm, "end": v(5.41, 22.77) * mm});
            skLineSegment(sketch, "E706", {"start": v(5.41, 22.77) * mm, "end": v(5.38, 22.71) * mm});
            skLineSegment(sketch, "E707", {"start": v(5.38, 22.71) * mm, "end": v(5.34, 22.65) * mm});
            skLineSegment(sketch, "E708", {"start": v(5.34, 22.65) * mm, "end": v(5.3, 22.6) * mm});
            skLineSegment(sketch, "E709", {"start": v(5.3, 22.6) * mm, "end": v(5.27, 22.55) * mm});
            skLineSegment(sketch, "E710", {"start": v(5.27, 22.55) * mm, "end": v(5.24, 22.5) * mm});
            skLineSegment(sketch, "E711", {"start": v(5.24, 22.5) * mm, "end": v(5.21, 22.44) * mm});
            skLineSegment(sketch, "E712", {"start": v(5.21, 22.44) * mm, "end": v(5.18, 22.4) * mm});
            skLineSegment(sketch, "E713", {"start": v(5.18, 22.4) * mm, "end": v(5.16, 22.34) * mm});
            skLineSegment(sketch, "E714", {"start": v(5.16, 22.34) * mm, "end": v(5.13, 22.3) * mm});
            skLineSegment(sketch, "E715", {"start": v(5.13, 22.3) * mm, "end": v(5.1, 22.25) * mm});
            skLineSegment(sketch, "E716", {"start": v(5.1, 22.25) * mm, "end": v(5.06, 22.16) * mm});
            skLineSegment(sketch, "E717", {"start": v(5.06, 22.16) * mm, "end": v(5.02, 22.07) * mm});
            skLineSegment(sketch, "E718", {"start": v(5.02, 22.07) * mm, "end": v(4.99, 22.02) * mm});
            skArc(sketch, "E719", {"start": v(4.99, 22.02) * mm, "mid": v(4.67, 21.82) * mm, "end": v(4.45, 22.13) * mm});
            skLineSegment(sketch, "E720", {"start": v(4.45, 22.13) * mm, "end": v(4.45, 22.2) * mm});
            skLineSegment(sketch, "E721", {"start": v(4.45, 22.2) * mm, "end": v(4.45, 22.29) * mm});
            skLineSegment(sketch, "E722", {"start": v(4.45, 22.29) * mm, "end": v(4.44, 22.4) * mm});
            skLineSegment(sketch, "E723", {"start": v(4.44, 22.4) * mm, "end": v(4.44, 22.44) * mm});
            skLineSegment(sketch, "E724", {"start": v(4.44, 22.44) * mm, "end": v(4.43, 22.5) * mm});
            skLineSegment(sketch, "E725", {"start": v(4.43, 22.5) * mm, "end": v(4.43, 22.55) * mm});
            skLineSegment(sketch, "E726", {"start": v(4.43, 22.55) * mm, "end": v(4.42, 22.61) * mm});
            skLineSegment(sketch, "E727", {"start": v(4.42, 22.61) * mm, "end": v(4.42, 22.67) * mm});
            skLineSegment(sketch, "E728", {"start": v(4.42, 22.67) * mm, "end": v(4.4, 22.73) * mm});
            skLineSegment(sketch, "E729", {"start": v(4.4, 22.73) * mm, "end": v(4.4, 22.8) * mm});
            skLineSegment(sketch, "E730", {"start": v(4.4, 22.8) * mm, "end": v(4.4, 22.86) * mm});
            skLineSegment(sketch, "E731", {"start": v(4.4, 22.86) * mm, "end": v(4.38, 22.92) * mm});
            skLineSegment(sketch, "E732", {"start": v(4.38, 22.92) * mm, "end": v(4.37, 23) * mm});
            skLineSegment(sketch, "E733", {"start": v(4.37, 23) * mm, "end": v(4.36, 23.06) * mm});
            skLineSegment(sketch, "E734", {"start": v(4.36, 23.06) * mm, "end": v(4.35, 23.13) * mm});
            skLineSegment(sketch, "E735", {"start": v(4.35, 23.13) * mm, "end": v(4.34, 23.2) * mm});
            skLineSegment(sketch, "E736", {"start": v(4.34, 23.2) * mm, "end": v(4.32, 23.27) * mm});
            skLineSegment(sketch, "E737", {"start": v(4.32, 23.27) * mm, "end": v(4.3, 23.35) * mm});
            skLineSegment(sketch, "E738", {"start": v(4.3, 23.35) * mm, "end": v(4.3, 23.43) * mm});
            skLineSegment(sketch, "E739", {"start": v(4.3, 23.43) * mm, "end": v(4.28, 23.5) * mm});
            skLineSegment(sketch, "E740", {"start": v(4.28, 23.5) * mm, "end": v(4.26, 23.58) * mm});
            skLineSegment(sketch, "E741", {"start": v(4.26, 23.58) * mm, "end": v(4.24, 23.66) * mm});
            skLineSegment(sketch, "E742", {"start": v(4.24, 23.66) * mm, "end": v(4.21, 23.78) * mm});
            skLineSegment(sketch, "E743", {"start": v(4.21, 23.78) * mm, "end": v(3.67, 23.87) * mm});
            skLineSegment(sketch, "E744", {"start": v(3.67, 23.87) * mm, "end": v(3.6, 23.77) * mm});
            skLineSegment(sketch, "E745", {"start": v(3.6, 23.77) * mm, "end": v(3.56, 23.7) * mm});
            skLineSegment(sketch, "E746", {"start": v(3.56, 23.7) * mm, "end": v(3.52, 23.63) * mm});
            skLineSegment(sketch, "E747", {"start": v(3.52, 23.63) * mm, "end": v(3.47, 23.56) * mm});
            skLineSegment(sketch, "E748", {"start": v(3.47, 23.56) * mm, "end": v(3.43, 23.5) * mm});
            skLineSegment(sketch, "E749", {"start": v(3.43, 23.5) * mm, "end": v(3.4, 23.43) * mm});
            skLineSegment(sketch, "E750", {"start": v(3.4, 23.43) * mm, "end": v(3.36, 23.36) * mm});
            skLineSegment(sketch, "E751", {"start": v(3.36, 23.36) * mm, "end": v(3.32, 23.3) * mm});
            skLineSegment(sketch, "E752", {"start": v(3.32, 23.3) * mm, "end": v(3.3, 23.24) * mm});
            skLineSegment(sketch, "E753", {"start": v(3.3, 23.24) * mm, "end": v(3.26, 23.17) * mm});
            skLineSegment(sketch, "E754", {"start": v(3.26, 23.17) * mm, "end": v(3.23, 23.11) * mm});
            skLineSegment(sketch, "E755", {"start": v(3.23, 23.11) * mm, "end": v(3.2, 23.06) * mm});
            skLineSegment(sketch, "E756", {"start": v(3.2, 23.06) * mm, "end": v(3.17, 23) * mm});
            skLineSegment(sketch, "E757", {"start": v(3.17, 23) * mm, "end": v(3.14, 22.94) * mm});
            skLineSegment(sketch, "E758", {"start": v(3.14, 22.94) * mm, "end": v(3.11, 22.89) * mm});
            skLineSegment(sketch, "E759", {"start": v(3.11, 22.89) * mm, "end": v(3.09, 22.83) * mm});
            skLineSegment(sketch, "E760", {"start": v(3.09, 22.83) * mm, "end": v(3.06, 22.78) * mm});
            skLineSegment(sketch, "E761", {"start": v(3.06, 22.78) * mm, "end": v(3.04, 22.73) * mm});
            skLineSegment(sketch, "E762", {"start": v(3.04, 22.73) * mm, "end": v(3.02, 22.68) * mm});
            skLineSegment(sketch, "E763", {"start": v(3.02, 22.68) * mm, "end": v(3, 22.63) * mm});
            skLineSegment(sketch, "E764", {"start": v(3, 22.63) * mm, "end": v(2.96, 22.54) * mm});
            skLineSegment(sketch, "E765", {"start": v(2.96, 22.54) * mm, "end": v(2.93, 22.45) * mm});
            skLineSegment(sketch, "E766", {"start": v(2.93, 22.45) * mm, "end": v(2.9, 22.39) * mm});
            skArc(sketch, "E767", {"start": v(2.9, 22.39) * mm, "mid": v(2.6, 22.16) * mm, "end": v(2.36, 22.45) * mm});
            skLineSegment(sketch, "E768", {"start": v(2.36, 22.45) * mm, "end": v(2.35, 22.52) * mm});
            skLineSegment(sketch, "E769", {"start": v(2.35, 22.52) * mm, "end": v(2.34, 22.6) * mm});
            skLineSegment(sketch, "E770", {"start": v(2.34, 22.6) * mm, "end": v(2.33, 22.7) * mm});
            skLineSegment(sketch, "E771", {"start": v(2.33, 22.7) * mm, "end": v(2.32, 22.76) * mm});
            skLineSegment(sketch, "E772", {"start": v(2.32, 22.76) * mm, "end": v(2.3, 22.81) * mm});
            skLineSegment(sketch, "E773", {"start": v(2.3, 22.81) * mm, "end": v(2.3, 22.87) * mm});
            skLineSegment(sketch, "E774", {"start": v(2.3, 22.87) * mm, "end": v(2.29, 22.93) * mm});
            skLineSegment(sketch, "E775", {"start": v(2.29, 22.93) * mm, "end": v(2.27, 22.98) * mm});
            skLineSegment(sketch, "E776", {"start": v(2.27, 22.98) * mm, "end": v(2.26, 23.04) * mm});
            skLineSegment(sketch, "E777", {"start": v(2.26, 23.04) * mm, "end": v(2.25, 23.1) * mm});
            skLineSegment(sketch, "E778", {"start": v(2.25, 23.1) * mm, "end": v(2.23, 23.17) * mm});
            skLineSegment(sketch, "E779", {"start": v(2.23, 23.17) * mm, "end": v(2.22, 23.23) * mm});
            skLineSegment(sketch, "E780", {"start": v(2.22, 23.23) * mm, "end": v(2.2, 23.3) * mm});
            skLineSegment(sketch, "E781", {"start": v(2.2, 23.3) * mm, "end": v(2.18, 23.37) * mm});
            skLineSegment(sketch, "E782", {"start": v(2.18, 23.37) * mm, "end": v(2.17, 23.44) * mm});
            skLineSegment(sketch, "E783", {"start": v(2.17, 23.44) * mm, "end": v(2.15, 23.5) * mm});
            skLineSegment(sketch, "E784", {"start": v(2.15, 23.5) * mm, "end": v(2.13, 23.58) * mm});
            skLineSegment(sketch, "E785", {"start": v(2.13, 23.58) * mm, "end": v(2.1, 23.65) * mm});
            skLineSegment(sketch, "E786", {"start": v(2.1, 23.65) * mm, "end": v(2.08, 23.73) * mm});
            skLineSegment(sketch, "E787", {"start": v(2.08, 23.73) * mm, "end": v(2.06, 23.8) * mm});
            skLineSegment(sketch, "E788", {"start": v(2.06, 23.8) * mm, "end": v(2.03, 23.88) * mm});
            skLineSegment(sketch, "E789", {"start": v(2.03, 23.88) * mm, "end": v(2, 23.96) * mm});
            skLineSegment(sketch, "E790", {"start": v(2, 23.96) * mm, "end": v(1.97, 24.07) * mm});
            skLineSegment(sketch, "E791", {"start": v(1.97, 24.07) * mm, "end": v(1.41, 24.1) * mm});
            skLineSegment(sketch, "E792", {"start": v(1.41, 24.1) * mm, "end": v(1.36, 24) * mm});
            skLineSegment(sketch, "E793", {"start": v(1.36, 24) * mm, "end": v(1.32, 23.93) * mm});
            skLineSegment(sketch, "E794", {"start": v(1.32, 23.93) * mm, "end": v(1.29, 23.86) * mm});
            skLineSegment(sketch, "E795", {"start": v(1.29, 23.86) * mm, "end": v(1.25, 23.78) * mm});
            skLineSegment(sketch, "E796", {"start": v(1.25, 23.78) * mm, "end": v(1.22, 23.71) * mm});
            skLineSegment(sketch, "E797", {"start": v(1.22, 23.71) * mm, "end": v(1.19, 23.64) * mm});
            skLineSegment(sketch, "E798", {"start": v(1.19, 23.64) * mm, "end": v(1.16, 23.58) * mm});
            skLineSegment(sketch, "E799", {"start": v(1.16, 23.58) * mm, "end": v(1.13, 23.5) * mm});
            skLineSegment(sketch, "E800", {"start": v(1.13, 23.5) * mm, "end": v(1.1, 23.44) * mm});
            skLineSegment(sketch, "E801", {"start": v(1.1, 23.44) * mm, "end": v(1.07, 23.38) * mm});
            skLineSegment(sketch, "E802", {"start": v(1.07, 23.38) * mm, "end": v(1.05, 23.32) * mm});
            skLineSegment(sketch, "E803", {"start": v(1.05, 23.32) * mm, "end": v(1.02, 23.25) * mm});
            skLineSegment(sketch, "E804", {"start": v(1.02, 23.25) * mm, "end": v(1, 23.2) * mm});
            skLineSegment(sketch, "E805", {"start": v(1, 23.2) * mm, "end": v(0.98, 23.13) * mm});
            skLineSegment(sketch, "E806", {"start": v(0.98, 23.13) * mm, "end": v(0.96, 23.08) * mm});
            skLineSegment(sketch, "E807", {"start": v(0.96, 23.08) * mm, "end": v(0.94, 23.02) * mm});
            skLineSegment(sketch, "E808", {"start": v(0.94, 23.02) * mm, "end": v(0.92, 22.97) * mm});
            skLineSegment(sketch, "E809", {"start": v(0.92, 22.97) * mm, "end": v(0.9, 22.91) * mm});
            skLineSegment(sketch, "E810", {"start": v(0.9, 22.91) * mm, "end": v(0.88, 22.86) * mm});
            skLineSegment(sketch, "E811", {"start": v(0.88, 22.86) * mm, "end": v(0.87, 22.81) * mm});
            skLineSegment(sketch, "E812", {"start": v(0.87, 22.81) * mm, "end": v(0.84, 22.71) * mm});
            skLineSegment(sketch, "E813", {"start": v(0.84, 22.71) * mm, "end": v(0.81, 22.62) * mm});
            skLineSegment(sketch, "E814", {"start": v(0.81, 22.62) * mm, "end": v(0.8, 22.56) * mm});
            skArc(sketch, "E815", {"start": v(0.8, 22.56) * mm, "mid": v(0.52, 22.3) * mm, "end": v(0.25, 22.57) * mm});
            skLineSegment(sketch, "E816", {"start": v(0.25, 22.57) * mm, "end": v(0.24, 22.64) * mm});
            skLineSegment(sketch, "E817", {"start": v(0.24, 22.64) * mm, "end": v(0.21, 22.73) * mm});
            skLineSegment(sketch, "E818", {"start": v(0.21, 22.73) * mm, "end": v(0.19, 22.83) * mm});
            skLineSegment(sketch, "E819", {"start": v(0.19, 22.83) * mm, "end": v(0.18, 22.88) * mm});
            skLineSegment(sketch, "E820", {"start": v(0.18, 22.88) * mm, "end": v(0.16, 22.93) * mm});
            skLineSegment(sketch, "E821", {"start": v(0.16, 22.93) * mm, "end": v(0.15, 22.98) * mm});
            skLineSegment(sketch, "E822", {"start": v(0.15, 22.98) * mm, "end": v(0.13, 23.04) * mm});
            skLineSegment(sketch, "E823", {"start": v(0.13, 23.04) * mm, "end": v(0.11, 23.1) * mm});
            skLineSegment(sketch, "E824", {"start": v(0.11, 23.1) * mm, "end": v(0.1, 23.16) * mm});
            skLineSegment(sketch, "E825", {"start": v(0.1, 23.16) * mm, "end": v(0.07, 23.22) * mm});
            skLineSegment(sketch, "E826", {"start": v(0.07, 23.22) * mm, "end": v(0.05, 23.28) * mm});
            skLineSegment(sketch, "E827", {"start": v(0.05, 23.28) * mm, "end": v(0.03, 23.34) * mm});
            skLineSegment(sketch, "E828", {"start": v(0.03, 23.34) * mm, "end": v(0, 23.4) * mm});
            skLineSegment(sketch, "E829", {"start": v(0, 23.4) * mm, "end": v(-0.01, 23.47) * mm});
            skLineSegment(sketch, "E830", {"start": v(-0.01, 23.47) * mm, "end": v(-0.04, 23.54) * mm});
            skLineSegment(sketch, "E831", {"start": v(-0.04, 23.54) * mm, "end": v(-0.06, 23.6) * mm});
            skLineSegment(sketch, "E832", {"start": v(-0.06, 23.6) * mm, "end": v(-0.1, 23.67) * mm});
            skLineSegment(sketch, "E833", {"start": v(-0.1, 23.67) * mm, "end": v(-0.12, 23.74) * mm});
            skLineSegment(sketch, "E834", {"start": v(-0.12, 23.74) * mm, "end": v(-0.15, 23.82) * mm});
            skLineSegment(sketch, "E835", {"start": v(-0.15, 23.82) * mm, "end": v(-0.18, 23.9) * mm});
            skLineSegment(sketch, "E836", {"start": v(-0.18, 23.9) * mm, "end": v(-0.21, 23.96) * mm});
            skLineSegment(sketch, "E837", {"start": v(-0.21, 23.96) * mm, "end": v(-0.25, 24.04) * mm});
            skLineSegment(sketch, "E838", {"start": v(-0.25, 24.04) * mm, "end": v(-0.3, 24.15) * mm});
            skLineSegment(sketch, "E839", {"start": v(-0.3, 24.15) * mm, "end": v(-0.85, 24.14) * mm});
            skLineSegment(sketch, "E840", {"start": v(-0.85, 24.14) * mm, "end": v(-0.9, 24.03) * mm});
            skLineSegment(sketch, "E841", {"start": v(-0.9, 24.03) * mm, "end": v(-0.92, 23.95) * mm});
            skLineSegment(sketch, "E842", {"start": v(-0.92, 23.95) * mm, "end": v(-0.95, 23.87) * mm});
            skLineSegment(sketch, "E843", {"start": v(-0.95, 23.87) * mm, "end": v(-0.98, 23.8) * mm});
            skLineSegment(sketch, "E844", {"start": v(-0.98, 23.8) * mm, "end": v(-1, 23.72) * mm});
            skLineSegment(sketch, "E845", {"start": v(-1, 23.72) * mm, "end": v(-1.03, 23.65) * mm});
            skLineSegment(sketch, "E846", {"start": v(-1.03, 23.65) * mm, "end": v(-1.06, 23.58) * mm});
            skLineSegment(sketch, "E847", {"start": v(-1.06, 23.58) * mm, "end": v(-1.08, 23.51) * mm});
            skLineSegment(sketch, "E848", {"start": v(-1.08, 23.51) * mm, "end": v(-1.1, 23.44) * mm});
            skLineSegment(sketch, "E849", {"start": v(-1.1, 23.44) * mm, "end": v(-1.12, 23.38) * mm});
            skLineSegment(sketch, "E850", {"start": v(-1.12, 23.38) * mm, "end": v(-1.14, 23.31) * mm});
            skLineSegment(sketch, "E851", {"start": v(-1.14, 23.31) * mm, "end": v(-1.16, 23.25) * mm});
            skLineSegment(sketch, "E852", {"start": v(-1.16, 23.25) * mm, "end": v(-1.18, 23.19) * mm});
            skLineSegment(sketch, "E853", {"start": v(-1.18, 23.19) * mm, "end": v(-1.2, 23.13) * mm});
            skLineSegment(sketch, "E854", {"start": v(-1.2, 23.13) * mm, "end": v(-1.2, 23.07) * mm});
            skLineSegment(sketch, "E855", {"start": v(-1.2, 23.07) * mm, "end": v(-1.22, 23) * mm});
            skLineSegment(sketch, "E856", {"start": v(-1.22, 23) * mm, "end": v(-1.24, 22.95) * mm});
            skLineSegment(sketch, "E857", {"start": v(-1.24, 22.95) * mm, "end": v(-1.25, 22.9) * mm});
            skLineSegment(sketch, "E858", {"start": v(-1.25, 22.9) * mm, "end": v(-1.26, 22.84) * mm});
            skLineSegment(sketch, "E859", {"start": v(-1.26, 22.84) * mm, "end": v(-1.27, 22.8) * mm});
            skLineSegment(sketch, "E860", {"start": v(-1.27, 22.8) * mm, "end": v(-1.3, 22.7) * mm});
            skLineSegment(sketch, "E861", {"start": v(-1.3, 22.7) * mm, "end": v(-1.3, 22.6) * mm});
            skLineSegment(sketch, "E862", {"start": v(-1.3, 22.6) * mm, "end": v(-1.32, 22.54) * mm});
            skArc(sketch, "E863", {"start": v(-1.32, 22.54) * mm, "mid": v(-1.57, 22.26) * mm, "end": v(-1.87, 22.5) * mm});
            skLineSegment(sketch, "E864", {"start": v(-1.87, 22.5) * mm, "end": v(-1.89, 22.56) * mm});
            skLineSegment(sketch, "E865", {"start": v(-1.89, 22.56) * mm, "end": v(-1.92, 22.65) * mm});
            skLineSegment(sketch, "E866", {"start": v(-1.92, 22.65) * mm, "end": v(-1.95, 22.75) * mm});
            skLineSegment(sketch, "E867", {"start": v(-1.95, 22.75) * mm, "end": v(-1.97, 22.8) * mm});
            skLineSegment(sketch, "E868", {"start": v(-1.97, 22.8) * mm, "end": v(-1.99, 22.85) * mm});
            skLineSegment(sketch, "E869", {"start": v(-1.99, 22.85) * mm, "end": v(-2, 22.9) * mm});
            skLineSegment(sketch, "E870", {"start": v(-2, 22.9) * mm, "end": v(-2.03, 22.95) * mm});
            skLineSegment(sketch, "E871", {"start": v(-2.03, 22.95) * mm, "end": v(-2.05, 23) * mm});
            skLineSegment(sketch, "E872", {"start": v(-2.05, 23) * mm, "end": v(-2.08, 23.06) * mm});
            skLineSegment(sketch, "E873", {"start": v(-2.08, 23.06) * mm, "end": v(-2.1, 23.12) * mm});
            skLineSegment(sketch, "E874", {"start": v(-2.1, 23.12) * mm, "end": v(-2.13, 23.18) * mm});
            skLineSegment(sketch, "E875", {"start": v(-2.13, 23.18) * mm, "end": v(-2.15, 23.24) * mm});
            skLineSegment(sketch, "E876", {"start": v(-2.15, 23.24) * mm, "end": v(-2.18, 23.3) * mm});
            skLineSegment(sketch, "E877", {"start": v(-2.18, 23.3) * mm, "end": v(-2.21, 23.37) * mm});
            skLineSegment(sketch, "E878", {"start": v(-2.21, 23.37) * mm, "end": v(-2.24, 23.43) * mm});
            skLineSegment(sketch, "E879", {"start": v(-2.24, 23.43) * mm, "end": v(-2.27, 23.5) * mm});
            skLineSegment(sketch, "E880", {"start": v(-2.27, 23.5) * mm, "end": v(-2.3, 23.56) * mm});
            skLineSegment(sketch, "E881", {"start": v(-2.3, 23.56) * mm, "end": v(-2.34, 23.63) * mm});
            skLineSegment(sketch, "E882", {"start": v(-2.34, 23.63) * mm, "end": v(-2.38, 23.7) * mm});
            skLineSegment(sketch, "E883", {"start": v(-2.38, 23.7) * mm, "end": v(-2.42, 23.77) * mm});
            skLineSegment(sketch, "E884", {"start": v(-2.42, 23.77) * mm, "end": v(-2.46, 23.84) * mm});
            skLineSegment(sketch, "E885", {"start": v(-2.46, 23.84) * mm, "end": v(-2.5, 23.91) * mm});
            skLineSegment(sketch, "E886", {"start": v(-2.5, 23.91) * mm, "end": v(-2.56, 24.02) * mm});
            skLineSegment(sketch, "E887", {"start": v(-2.56, 24.02) * mm, "end": v(-3.1, 23.95) * mm});
            skLineSegment(sketch, "E888", {"start": v(-3.1, 23.95) * mm, "end": v(-3.14, 23.84) * mm});
            skLineSegment(sketch, "E889", {"start": v(-3.14, 23.84) * mm, "end": v(-3.16, 23.76) * mm});
            skLineSegment(sketch, "E890", {"start": v(-3.16, 23.76) * mm, "end": v(-3.18, 23.68) * mm});
            skLineSegment(sketch, "E891", {"start": v(-3.18, 23.68) * mm, "end": v(-3.2, 23.6) * mm});
            skLineSegment(sketch, "E892", {"start": v(-3.2, 23.6) * mm, "end": v(-3.22, 23.53) * mm});
            skLineSegment(sketch, "E893", {"start": v(-3.22, 23.53) * mm, "end": v(-3.24, 23.45) * mm});
            skLineSegment(sketch, "E894", {"start": v(-3.24, 23.45) * mm, "end": v(-3.26, 23.38) * mm});
            skLineSegment(sketch, "E895", {"start": v(-3.26, 23.38) * mm, "end": v(-3.28, 23.3) * mm});
            skLineSegment(sketch, "E896", {"start": v(-3.28, 23.3) * mm, "end": v(-3.3, 23.24) * mm});
            skLineSegment(sketch, "E897", {"start": v(-3.3, 23.24) * mm, "end": v(-3.3, 23.17) * mm});
            skLineSegment(sketch, "E898", {"start": v(-3.3, 23.17) * mm, "end": v(-3.32, 23.1) * mm});
            skLineSegment(sketch, "E899", {"start": v(-3.32, 23.1) * mm, "end": v(-3.33, 23.04) * mm});
            skLineSegment(sketch, "E900", {"start": v(-3.33, 23.04) * mm, "end": v(-3.34, 22.97) * mm});
            skLineSegment(sketch, "E901", {"start": v(-3.34, 22.97) * mm, "end": v(-3.35, 22.91) * mm});
            skLineSegment(sketch, "E902", {"start": v(-3.35, 22.91) * mm, "end": v(-3.36, 22.85) * mm});
            skLineSegment(sketch, "E903", {"start": v(-3.36, 22.85) * mm, "end": v(-3.37, 22.8) * mm});
            skLineSegment(sketch, "E904", {"start": v(-3.37, 22.8) * mm, "end": v(-3.38, 22.74) * mm});
            skLineSegment(sketch, "E905", {"start": v(-3.38, 22.74) * mm, "end": v(-3.39, 22.68) * mm});
            skLineSegment(sketch, "E906", {"start": v(-3.39, 22.68) * mm, "end": v(-3.4, 22.63) * mm});
            skLineSegment(sketch, "E907", {"start": v(-3.4, 22.63) * mm, "end": v(-3.4, 22.57) * mm});
            skLineSegment(sketch, "E908", {"start": v(-3.4, 22.57) * mm, "end": v(-3.41, 22.47) * mm});
            skLineSegment(sketch, "E909", {"start": v(-3.41, 22.47) * mm, "end": v(-3.42, 22.38) * mm});
            skLineSegment(sketch, "E910", {"start": v(-3.42, 22.38) * mm, "end": v(-3.43, 22.31) * mm});
            skArc(sketch, "E911", {"start": v(-3.43, 22.31) * mm, "mid": v(-3.65, 22.01) * mm, "end": v(-3.96, 22.23) * mm});
            skLineSegment(sketch, "E912", {"start": v(-3.96, 22.23) * mm, "end": v(-4, 22.29) * mm});
            skLineSegment(sketch, "E913", {"start": v(-4, 22.29) * mm, "end": v(-4.03, 22.37) * mm});
            skLineSegment(sketch, "E914", {"start": v(-4.03, 22.37) * mm, "end": v(-4.07, 22.46) * mm});
            skLineSegment(sketch, "E915", {"start": v(-4.07, 22.46) * mm, "end": v(-4.1, 22.51) * mm});
            skLineSegment(sketch, "E916", {"start": v(-4.1, 22.51) * mm, "end": v(-4.12, 22.56) * mm});
            skLineSegment(sketch, "E917", {"start": v(-4.12, 22.56) * mm, "end": v(-4.14, 22.61) * mm});
            skLineSegment(sketch, "E918", {"start": v(-4.14, 22.61) * mm, "end": v(-4.17, 22.66) * mm});
            skLineSegment(sketch, "E919", {"start": v(-4.17, 22.66) * mm, "end": v(-4.2, 22.71) * mm});
            skLineSegment(sketch, "E920", {"start": v(-4.2, 22.71) * mm, "end": v(-4.23, 22.77) * mm});
            skLineSegment(sketch, "E921", {"start": v(-4.23, 22.77) * mm, "end": v(-4.26, 22.82) * mm});
            skLineSegment(sketch, "E922", {"start": v(-4.26, 22.82) * mm, "end": v(-4.29, 22.88) * mm});
            skLineSegment(sketch, "E923", {"start": v(-4.29, 22.88) * mm, "end": v(-4.32, 22.94) * mm});
            skLineSegment(sketch, "E924", {"start": v(-4.32, 22.94) * mm, "end": v(-4.35, 23) * mm});
            skLineSegment(sketch, "E925", {"start": v(-4.35, 23) * mm, "end": v(-4.39, 23.06) * mm});
            skLineSegment(sketch, "E926", {"start": v(-4.39, 23.06) * mm, "end": v(-4.43, 23.12) * mm});
            skLineSegment(sketch, "E927", {"start": v(-4.43, 23.12) * mm, "end": v(-4.46, 23.18) * mm});
            skLineSegment(sketch, "E928", {"start": v(-4.46, 23.18) * mm, "end": v(-4.5, 23.24) * mm});
            skLineSegment(sketch, "E929", {"start": v(-4.5, 23.24) * mm, "end": v(-4.55, 23.3) * mm});
            skLineSegment(sketch, "E930", {"start": v(-4.55, 23.3) * mm, "end": v(-4.59, 23.37) * mm});
            skLineSegment(sketch, "E931", {"start": v(-4.59, 23.37) * mm, "end": v(-4.63, 23.44) * mm});
            skLineSegment(sketch, "E932", {"start": v(-4.63, 23.44) * mm, "end": v(-4.68, 23.5) * mm});
            skLineSegment(sketch, "E933", {"start": v(-4.68, 23.5) * mm, "end": v(-4.73, 23.57) * mm});
            skLineSegment(sketch, "E934", {"start": v(-4.73, 23.57) * mm, "end": v(-4.8, 23.67) * mm});
            skLineSegment(sketch, "E935", {"start": v(-4.8, 23.67) * mm, "end": v(-5.34, 23.55) * mm});
            skLineSegment(sketch, "E936", {"start": v(-5.34, 23.55) * mm, "end": v(-5.36, 23.44) * mm});
            skLineSegment(sketch, "E937", {"start": v(-5.36, 23.44) * mm, "end": v(-5.37, 23.36) * mm});
            skLineSegment(sketch, "E938", {"start": v(-5.37, 23.36) * mm, "end": v(-5.39, 23.28) * mm});
            skLineSegment(sketch, "E939", {"start": v(-5.39, 23.28) * mm, "end": v(-5.4, 23.2) * mm});
            skLineSegment(sketch, "E940", {"start": v(-5.4, 23.2) * mm, "end": v(-5.41, 23.12) * mm});
            skLineSegment(sketch, "E941", {"start": v(-5.41, 23.12) * mm, "end": v(-5.42, 23.05) * mm});
            skLineSegment(sketch, "E942", {"start": v(-5.42, 23.05) * mm, "end": v(-5.43, 22.97) * mm});
            skLineSegment(sketch, "E943", {"start": v(-5.43, 22.97) * mm, "end": v(-5.44, 22.9) * mm});
            skLineSegment(sketch, "E944", {"start": v(-5.44, 22.9) * mm, "end": v(-5.45, 22.83) * mm});
            skLineSegment(sketch, "E945", {"start": v(-5.45, 22.83) * mm, "end": v(-5.46, 22.76) * mm});
            skLineSegment(sketch, "E946", {"start": v(-5.46, 22.76) * mm, "end": v(-5.47, 22.7) * mm});
            skLineSegment(sketch, "E947", {"start": v(-5.47, 22.7) * mm, "end": v(-5.47, 22.63) * mm});
            skLineSegment(sketch, "E948", {"start": v(-5.47, 22.63) * mm, "end": v(-5.48, 22.56) * mm});
            skLineSegment(sketch, "E949", {"start": v(-5.48, 22.56) * mm, "end": v(-5.48, 22.5) * mm});
            skLineSegment(sketch, "E950", {"start": v(-5.48, 22.5) * mm, "end": v(-5.49, 22.44) * mm});
            skLineSegment(sketch, "E951", {"start": v(-5.49, 22.44) * mm, "end": v(-5.5, 22.38) * mm});
            skLineSegment(sketch, "E952", {"start": v(-5.5, 22.38) * mm, "end": v(-5.5, 22.32) * mm});
            skLineSegment(sketch, "E953", {"start": v(-5.5, 22.32) * mm, "end": v(-5.5, 22.26) * mm});
            skLineSegment(sketch, "E954", {"start": v(-5.5, 22.26) * mm, "end": v(-5.5, 22.2) * mm});
            skLineSegment(sketch, "E955", {"start": v(-5.5, 22.2) * mm, "end": v(-5.5, 22.16) * mm});
            skLineSegment(sketch, "E956", {"start": v(-5.5, 22.16) * mm, "end": v(-5.5, 22.06) * mm});
            skLineSegment(sketch, "E957", {"start": v(-5.5, 22.06) * mm, "end": v(-5.5, 21.96) * mm});
            skLineSegment(sketch, "E958", {"start": v(-5.5, 21.96) * mm, "end": v(-5.5, 21.9) * mm});
            skArc(sketch, "E959", {"start": v(-5.5, 21.9) * mm, "mid": v(-5.7, 21.57) * mm, "end": v(-6.03, 21.76) * mm});
            skLineSegment(sketch, "E960", {"start": v(-6.03, 21.76) * mm, "end": v(-6.06, 21.82) * mm});
            skLineSegment(sketch, "E961", {"start": v(-6.06, 21.82) * mm, "end": v(-6.1, 21.9) * mm});
            skLineSegment(sketch, "E962", {"start": v(-6.1, 21.9) * mm, "end": v(-6.16, 21.98) * mm});
            skLineSegment(sketch, "E963", {"start": v(-6.16, 21.98) * mm, "end": v(-6.18, 22.03) * mm});
            skLineSegment(sketch, "E964", {"start": v(-6.18, 22.03) * mm, "end": v(-6.21, 22.08) * mm});
            skLineSegment(sketch, "E965", {"start": v(-6.21, 22.08) * mm, "end": v(-6.24, 22.12) * mm});
            skLineSegment(sketch, "E966", {"start": v(-6.24, 22.12) * mm, "end": v(-6.27, 22.17) * mm});
            skLineSegment(sketch, "E967", {"start": v(-6.27, 22.17) * mm, "end": v(-6.3, 22.22) * mm});
            skLineSegment(sketch, "E968", {"start": v(-6.3, 22.22) * mm, "end": v(-6.34, 22.27) * mm});
            skLineSegment(sketch, "E969", {"start": v(-6.34, 22.27) * mm, "end": v(-6.37, 22.33) * mm});
            skLineSegment(sketch, "E970", {"start": v(-6.37, 22.33) * mm, "end": v(-6.41, 22.38) * mm});
            skLineSegment(sketch, "E971", {"start": v(-6.41, 22.38) * mm, "end": v(-6.45, 22.43) * mm});
            skLineSegment(sketch, "E972", {"start": v(-6.45, 22.43) * mm, "end": v(-6.49, 22.49) * mm});
            skLineSegment(sketch, "E973", {"start": v(-6.49, 22.49) * mm, "end": v(-6.53, 22.54) * mm});
            skLineSegment(sketch, "E974", {"start": v(-6.53, 22.54) * mm, "end": v(-6.57, 22.6) * mm});
            skLineSegment(sketch, "E975", {"start": v(-6.57, 22.6) * mm, "end": v(-6.62, 22.66) * mm});
            skLineSegment(sketch, "E976", {"start": v(-6.62, 22.66) * mm, "end": v(-6.66, 22.72) * mm});
            skLineSegment(sketch, "E977", {"start": v(-6.66, 22.72) * mm, "end": v(-6.7, 22.78) * mm});
            skLineSegment(sketch, "E978", {"start": v(-6.7, 22.78) * mm, "end": v(-6.76, 22.84) * mm});
            skLineSegment(sketch, "E979", {"start": v(-6.76, 22.84) * mm, "end": v(-6.8, 22.9) * mm});
            skLineSegment(sketch, "E980", {"start": v(-6.8, 22.9) * mm, "end": v(-6.86, 22.97) * mm});
            skLineSegment(sketch, "E981", {"start": v(-6.86, 22.97) * mm, "end": v(-6.91, 23.03) * mm});
            skLineSegment(sketch, "E982", {"start": v(-6.91, 23.03) * mm, "end": v(-6.99, 23.12) * mm});
            skLineSegment(sketch, "E983", {"start": v(-6.99, 23.12) * mm, "end": v(-7.52, 22.95) * mm});
            skLineSegment(sketch, "E984", {"start": v(-7.52, 22.95) * mm, "end": v(-7.53, 22.83) * mm});
            skLineSegment(sketch, "E985", {"start": v(-7.53, 22.83) * mm, "end": v(-7.54, 22.75) * mm});
            skLineSegment(sketch, "E986", {"start": v(-7.54, 22.75) * mm, "end": v(-7.54, 22.67) * mm});
            skLineSegment(sketch, "E987", {"start": v(-7.54, 22.67) * mm, "end": v(-7.55, 22.6) * mm});
            skLineSegment(sketch, "E988", {"start": v(-7.55, 22.6) * mm, "end": v(-7.55, 22.51) * mm});
            skLineSegment(sketch, "E989", {"start": v(-7.55, 22.51) * mm, "end": v(-7.56, 22.44) * mm});
            skLineSegment(sketch, "E990", {"start": v(-7.56, 22.44) * mm, "end": v(-7.56, 22.36) * mm});
            skLineSegment(sketch, "E991", {"start": v(-7.56, 22.36) * mm, "end": v(-7.56, 22.29) * mm});
            skLineSegment(sketch, "E992", {"start": v(-7.56, 22.29) * mm, "end": v(-7.57, 22.22) * mm});
            skLineSegment(sketch, "E993", {"start": v(-7.57, 22.22) * mm, "end": v(-7.57, 22.15) * mm});
            skLineSegment(sketch, "E994", {"start": v(-7.57, 22.15) * mm, "end": v(-7.57, 22.08) * mm});
            skLineSegment(sketch, "E995", {"start": v(-7.57, 22.08) * mm, "end": v(-7.57, 22.01) * mm});
            skLineSegment(sketch, "E996", {"start": v(-7.57, 22.01) * mm, "end": v(-7.57, 21.95) * mm});
            skLineSegment(sketch, "E997", {"start": v(-7.57, 21.95) * mm, "end": v(-7.57, 21.89) * mm});
            skLineSegment(sketch, "E998", {"start": v(-7.57, 21.89) * mm, "end": v(-7.57, 21.83) * mm});
            skLineSegment(sketch, "E999", {"start": v(-7.57, 21.83) * mm, "end": v(-7.56, 21.77) * mm});
            skLineSegment(sketch, "E1000", {"start": v(-7.56, 21.77) * mm, "end": v(-7.56, 21.7) * mm});
            skLineSegment(sketch, "E1001", {"start": v(-7.56, 21.7) * mm, "end": v(-7.56, 21.65) * mm});
            skLineSegment(sketch, "E1002", {"start": v(-7.56, 21.65) * mm, "end": v(-7.55, 21.6) * mm});
            skLineSegment(sketch, "E1003", {"start": v(-7.55, 21.6) * mm, "end": v(-7.55, 21.55) * mm});
            skLineSegment(sketch, "E1004", {"start": v(-7.55, 21.55) * mm, "end": v(-7.54, 21.44) * mm});
            skLineSegment(sketch, "E1005", {"start": v(-7.54, 21.44) * mm, "end": v(-7.53, 21.35) * mm});
            skLineSegment(sketch, "E1006", {"start": v(-7.53, 21.35) * mm, "end": v(-7.53, 21.29) * mm});
            skArc(sketch, "E1007", {"start": v(-7.53, 21.29) * mm, "mid": v(-7.7, 20.95) * mm, "end": v(-8.04, 21.1) * mm});
            skLineSegment(sketch, "E1008", {"start": v(-8.04, 21.1) * mm, "end": v(-8.08, 21.15) * mm});
            skLineSegment(sketch, "E1009", {"start": v(-8.08, 21.15) * mm, "end": v(-8.13, 21.23) * mm});
            skLineSegment(sketch, "E1010", {"start": v(-8.13, 21.23) * mm, "end": v(-8.19, 21.31) * mm});
            skLineSegment(sketch, "E1011", {"start": v(-8.19, 21.31) * mm, "end": v(-8.22, 21.35) * mm});
            skLineSegment(sketch, "E1012", {"start": v(-8.22, 21.35) * mm, "end": v(-8.25, 21.4) * mm});
            skLineSegment(sketch, "E1013", {"start": v(-8.25, 21.4) * mm, "end": v(-8.29, 21.44) * mm});
            skLineSegment(sketch, "E1014", {"start": v(-8.29, 21.44) * mm, "end": v(-8.32, 21.49) * mm});
            skLineSegment(sketch, "E1015", {"start": v(-8.32, 21.49) * mm, "end": v(-8.36, 21.53) * mm});
            skLineSegment(sketch, "E1016", {"start": v(-8.36, 21.53) * mm, "end": v(-8.4, 21.58) * mm});
            skLineSegment(sketch, "E1017", {"start": v(-8.4, 21.58) * mm, "end": v(-8.44, 21.63) * mm});
            skLineSegment(sketch, "E1018", {"start": v(-8.44, 21.63) * mm, "end": v(-8.48, 21.68) * mm});
            skLineSegment(sketch, "E1019", {"start": v(-8.48, 21.68) * mm, "end": v(-8.52, 21.73) * mm});
            skLineSegment(sketch, "E1020", {"start": v(-8.52, 21.73) * mm, "end": v(-8.57, 21.78) * mm});
            skLineSegment(sketch, "E1021", {"start": v(-8.57, 21.78) * mm, "end": v(-8.61, 21.83) * mm});
            skLineSegment(sketch, "E1022", {"start": v(-8.61, 21.83) * mm, "end": v(-8.66, 21.89) * mm});
            skLineSegment(sketch, "E1023", {"start": v(-8.66, 21.89) * mm, "end": v(-8.7, 21.94) * mm});
            skLineSegment(sketch, "E1024", {"start": v(-8.7, 21.94) * mm, "end": v(-8.76, 22) * mm});
            skLineSegment(sketch, "E1025", {"start": v(-8.76, 22) * mm, "end": v(-8.81, 22.05) * mm});
            skLineSegment(sketch, "E1026", {"start": v(-8.81, 22.05) * mm, "end": v(-8.87, 22.1) * mm});
            skLineSegment(sketch, "E1027", {"start": v(-8.87, 22.1) * mm, "end": v(-8.92, 22.17) * mm});
            skLineSegment(sketch, "E1028", {"start": v(-8.92, 22.17) * mm, "end": v(-8.98, 22.22) * mm});
            skLineSegment(sketch, "E1029", {"start": v(-8.98, 22.22) * mm, "end": v(-9.04, 22.28) * mm});
            skLineSegment(sketch, "E1030", {"start": v(-9.04, 22.28) * mm, "end": v(-9.12, 22.36) * mm});
            skLineSegment(sketch, "E1031", {"start": v(-9.12, 22.36) * mm, "end": v(-9.63, 22.15) * mm});
            skLineSegment(sketch, "E1032", {"start": v(-9.63, 22.15) * mm, "end": v(-9.63, 22.03) * mm});
            skLineSegment(sketch, "E1033", {"start": v(-9.63, 22.03) * mm, "end": v(-9.63, 21.95) * mm});
            skLineSegment(sketch, "E1034", {"start": v(-9.63, 21.95) * mm, "end": v(-9.63, 21.87) * mm});
            skLineSegment(sketch, "E1035", {"start": v(-9.63, 21.87) * mm, "end": v(-9.63, 21.79) * mm});
            skLineSegment(sketch, "E1036", {"start": v(-9.63, 21.79) * mm, "end": v(-9.63, 21.7) * mm});
            skLineSegment(sketch, "E1037", {"start": v(-9.63, 21.7) * mm, "end": v(-9.63, 21.63) * mm});
            skLineSegment(sketch, "E1038", {"start": v(-9.63, 21.63) * mm, "end": v(-9.62, 21.56) * mm});
            skLineSegment(sketch, "E1039", {"start": v(-9.62, 21.56) * mm, "end": v(-9.62, 21.48) * mm});
            skLineSegment(sketch, "E1040", {"start": v(-9.62, 21.48) * mm, "end": v(-9.61, 21.41) * mm});
            skLineSegment(sketch, "E1041", {"start": v(-9.61, 21.41) * mm, "end": v(-9.6, 21.34) * mm});
            skLineSegment(sketch, "E1042", {"start": v(-9.6, 21.34) * mm, "end": v(-9.6, 21.28) * mm});
            skLineSegment(sketch, "E1043", {"start": v(-9.6, 21.28) * mm, "end": v(-9.6, 21.2) * mm});
            skLineSegment(sketch, "E1044", {"start": v(-9.6, 21.2) * mm, "end": v(-9.59, 21.15) * mm});
            skLineSegment(sketch, "E1045", {"start": v(-9.59, 21.15) * mm, "end": v(-9.58, 21.08) * mm});
            skLineSegment(sketch, "E1046", {"start": v(-9.58, 21.08) * mm, "end": v(-9.58, 21.02) * mm});
            skLineSegment(sketch, "E1047", {"start": v(-9.58, 21.02) * mm, "end": v(-9.57, 20.96) * mm});
            skLineSegment(sketch, "E1048", {"start": v(-9.57, 20.96) * mm, "end": v(-9.56, 20.9) * mm});
            skLineSegment(sketch, "E1049", {"start": v(-9.56, 20.9) * mm, "end": v(-9.55, 20.85) * mm});
            skLineSegment(sketch, "E1050", {"start": v(-9.55, 20.85) * mm, "end": v(-9.54, 20.8) * mm});
            skLineSegment(sketch, "E1051", {"start": v(-9.54, 20.8) * mm, "end": v(-9.54, 20.74) * mm});
            skLineSegment(sketch, "E1052", {"start": v(-9.54, 20.74) * mm, "end": v(-9.52, 20.64) * mm});
            skLineSegment(sketch, "E1053", {"start": v(-9.52, 20.64) * mm, "end": v(-9.5, 20.55) * mm});
            skLineSegment(sketch, "E1054", {"start": v(-9.5, 20.55) * mm, "end": v(-9.49, 20.49) * mm});
            skArc(sketch, "E1055", {"start": v(-9.49, 20.49) * mm, "mid": v(-9.62, 20.13) * mm, "end": v(-9.98, 20.25) * mm});
            skLineSegment(sketch, "E1056", {"start": v(-9.98, 20.25) * mm, "end": v(-10.02, 20.3) * mm});
            skLineSegment(sketch, "E1057", {"start": v(-10.02, 20.3) * mm, "end": v(-10.08, 20.38) * mm});
            skLineSegment(sketch, "E1058", {"start": v(-10.08, 20.38) * mm, "end": v(-10.15, 20.45) * mm});
            skLineSegment(sketch, "E1059", {"start": v(-10.15, 20.45) * mm, "end": v(-10.18, 20.5) * mm});
            skLineSegment(sketch, "E1060", {"start": v(-10.18, 20.5) * mm, "end": v(-10.22, 20.53) * mm});
            skLineSegment(sketch, "E1061", {"start": v(-10.22, 20.53) * mm, "end": v(-10.26, 20.57) * mm});
            skLineSegment(sketch, "E1062", {"start": v(-10.26, 20.57) * mm, "end": v(-10.3, 20.62) * mm});
            skLineSegment(sketch, "E1063", {"start": v(-10.3, 20.62) * mm, "end": v(-10.34, 20.66) * mm});
            skLineSegment(sketch, "E1064", {"start": v(-10.34, 20.66) * mm, "end": v(-10.38, 20.7) * mm});
            skLineSegment(sketch, "E1065", {"start": v(-10.38, 20.7) * mm, "end": v(-10.43, 20.75) * mm});
            skLineSegment(sketch, "E1066", {"start": v(-10.43, 20.75) * mm, "end": v(-10.47, 20.8) * mm});
            skLineSegment(sketch, "E1067", {"start": v(-10.47, 20.8) * mm, "end": v(-10.52, 20.84) * mm});
            skLineSegment(sketch, "E1068", {"start": v(-10.52, 20.84) * mm, "end": v(-10.57, 20.89) * mm});
            skLineSegment(sketch, "E1069", {"start": v(-10.57, 20.89) * mm, "end": v(-10.62, 20.93) * mm});
            skLineSegment(sketch, "E1070", {"start": v(-10.62, 20.93) * mm, "end": v(-10.67, 20.98) * mm});
            skLineSegment(sketch, "E1071", {"start": v(-10.67, 20.98) * mm, "end": v(-10.73, 21.03) * mm});
            skLineSegment(sketch, "E1072", {"start": v(-10.73, 21.03) * mm, "end": v(-10.78, 21.08) * mm});
            skLineSegment(sketch, "E1073", {"start": v(-10.78, 21.08) * mm, "end": v(-10.84, 21.13) * mm});
            skLineSegment(sketch, "E1074", {"start": v(-10.84, 21.13) * mm, "end": v(-10.9, 21.18) * mm});
            skLineSegment(sketch, "E1075", {"start": v(-10.9, 21.18) * mm, "end": v(-10.96, 21.23) * mm});
            skLineSegment(sketch, "E1076", {"start": v(-10.96, 21.23) * mm, "end": v(-11.02, 21.28) * mm});
            skLineSegment(sketch, "E1077", {"start": v(-11.02, 21.28) * mm, "end": v(-11.09, 21.34) * mm});
            skLineSegment(sketch, "E1078", {"start": v(-11.09, 21.34) * mm, "end": v(-11.18, 21.41) * mm});
            skLineSegment(sketch, "E1079", {"start": v(-11.18, 21.41) * mm, "end": v(-11.67, 21.15) * mm});
            skLineSegment(sketch, "E1080", {"start": v(-11.67, 21.15) * mm, "end": v(-11.66, 21.03) * mm});
            skLineSegment(sketch, "E1081", {"start": v(-11.66, 21.03) * mm, "end": v(-11.65, 20.95) * mm});
            skLineSegment(sketch, "E1082", {"start": v(-11.65, 20.95) * mm, "end": v(-11.64, 20.87) * mm});
            skLineSegment(sketch, "E1083", {"start": v(-11.64, 20.87) * mm, "end": v(-11.63, 20.79) * mm});
            skLineSegment(sketch, "E1084", {"start": v(-11.63, 20.79) * mm, "end": v(-11.62, 20.71) * mm});
            skLineSegment(sketch, "E1085", {"start": v(-11.62, 20.71) * mm, "end": v(-11.6, 20.64) * mm});
            skLineSegment(sketch, "E1086", {"start": v(-11.6, 20.64) * mm, "end": v(-11.6, 20.56) * mm});
            skLineSegment(sketch, "E1087", {"start": v(-11.6, 20.56) * mm, "end": v(-11.59, 20.49) * mm});
            skLineSegment(sketch, "E1088", {"start": v(-11.59, 20.49) * mm, "end": v(-11.58, 20.42) * mm});
            skLineSegment(sketch, "E1089", {"start": v(-11.58, 20.42) * mm, "end": v(-11.56, 20.35) * mm});
            skLineSegment(sketch, "E1090", {"start": v(-11.56, 20.35) * mm, "end": v(-11.55, 20.28) * mm});
            skLineSegment(sketch, "E1091", {"start": v(-11.55, 20.28) * mm, "end": v(-11.54, 20.22) * mm});
            skLineSegment(sketch, "E1092", {"start": v(-11.54, 20.22) * mm, "end": v(-11.53, 20.16) * mm});
            skLineSegment(sketch, "E1093", {"start": v(-11.53, 20.16) * mm, "end": v(-11.52, 20.1) * mm});
            skLineSegment(sketch, "E1094", {"start": v(-11.52, 20.1) * mm, "end": v(-11.5, 20.03) * mm});
            skLineSegment(sketch, "E1095", {"start": v(-11.5, 20.03) * mm, "end": v(-11.49, 19.98) * mm});
            skLineSegment(sketch, "E1096", {"start": v(-11.49, 19.98) * mm, "end": v(-11.48, 19.92) * mm});
            skLineSegment(sketch, "E1097", {"start": v(-11.48, 19.92) * mm, "end": v(-11.46, 19.86) * mm});
            skLineSegment(sketch, "E1098", {"start": v(-11.46, 19.86) * mm, "end": v(-11.45, 19.81) * mm});
            skLineSegment(sketch, "E1099", {"start": v(-11.45, 19.81) * mm, "end": v(-11.44, 19.76) * mm});
            skLineSegment(sketch, "E1100", {"start": v(-11.44, 19.76) * mm, "end": v(-11.4, 19.66) * mm});
            skLineSegment(sketch, "E1101", {"start": v(-11.4, 19.66) * mm, "end": v(-11.38, 19.57) * mm});
            skLineSegment(sketch, "E1102", {"start": v(-11.38, 19.57) * mm, "end": v(-11.36, 19.51) * mm});
            skArc(sketch, "E1103", {"start": v(-11.36, 19.51) * mm, "mid": v(-11.46, 19.15) * mm, "end": v(-11.83, 19.23) * mm});
            skLineSegment(sketch, "E1104", {"start": v(-11.83, 19.23) * mm, "end": v(-11.88, 19.28) * mm});
            skLineSegment(sketch, "E1105", {"start": v(-11.88, 19.28) * mm, "end": v(-11.95, 19.34) * mm});
            skLineSegment(sketch, "E1106", {"start": v(-11.95, 19.34) * mm, "end": v(-12.02, 19.41) * mm});
            skLineSegment(sketch, "E1107", {"start": v(-12.02, 19.41) * mm, "end": v(-12.06, 19.45) * mm});
            skLineSegment(sketch, "E1108", {"start": v(-12.06, 19.45) * mm, "end": v(-12.1, 19.49) * mm});
            skLineSegment(sketch, "E1109", {"start": v(-12.1, 19.49) * mm, "end": v(-12.14, 19.52) * mm});
            skLineSegment(sketch, "E1110", {"start": v(-12.14, 19.52) * mm, "end": v(-12.18, 19.56) * mm});
            skLineSegment(sketch, "E1111", {"start": v(-12.18, 19.56) * mm, "end": v(-12.23, 19.6) * mm});
            skLineSegment(sketch, "E1112", {"start": v(-12.23, 19.6) * mm, "end": v(-12.27, 19.64) * mm});
            skLineSegment(sketch, "E1113", {"start": v(-12.27, 19.64) * mm, "end": v(-12.32, 19.68) * mm});
            skLineSegment(sketch, "E1114", {"start": v(-12.32, 19.68) * mm, "end": v(-12.37, 19.72) * mm});
            skLineSegment(sketch, "E1115", {"start": v(-12.37, 19.72) * mm, "end": v(-12.42, 19.76) * mm});
            skLineSegment(sketch, "E1116", {"start": v(-12.42, 19.76) * mm, "end": v(-12.48, 19.8) * mm});
            skLineSegment(sketch, "E1117", {"start": v(-12.48, 19.8) * mm, "end": v(-12.53, 19.85) * mm});
            skLineSegment(sketch, "E1118", {"start": v(-12.53, 19.85) * mm, "end": v(-12.59, 19.9) * mm});
            skLineSegment(sketch, "E1119", {"start": v(-12.59, 19.9) * mm, "end": v(-12.65, 19.93) * mm});
            skLineSegment(sketch, "E1120", {"start": v(-12.65, 19.93) * mm, "end": v(-12.7, 19.98) * mm});
            skLineSegment(sketch, "E1121", {"start": v(-12.7, 19.98) * mm, "end": v(-12.77, 20.02) * mm});
            skLineSegment(sketch, "E1122", {"start": v(-12.77, 20.02) * mm, "end": v(-12.83, 20.07) * mm});
            skLineSegment(sketch, "E1123", {"start": v(-12.83, 20.07) * mm, "end": v(-12.9, 20.11) * mm});
            skLineSegment(sketch, "E1124", {"start": v(-12.9, 20.11) * mm, "end": v(-12.97, 20.16) * mm});
            skLineSegment(sketch, "E1125", {"start": v(-12.97, 20.16) * mm, "end": v(-13.03, 20.2) * mm});
            skLineSegment(sketch, "E1126", {"start": v(-13.03, 20.2) * mm, "end": v(-13.13, 20.27) * mm});
            skLineSegment(sketch, "E1127", {"start": v(-13.13, 20.27) * mm, "end": v(-13.6, 19.96) * mm});
            skLineSegment(sketch, "E1128", {"start": v(-13.6, 19.96) * mm, "end": v(-13.57, 19.85) * mm});
            skLineSegment(sketch, "E1129", {"start": v(-13.57, 19.85) * mm, "end": v(-13.56, 19.77) * mm});
            skLineSegment(sketch, "E1130", {"start": v(-13.56, 19.77) * mm, "end": v(-13.54, 19.69) * mm});
            skLineSegment(sketch, "E1131", {"start": v(-13.54, 19.69) * mm, "end": v(-13.52, 19.6) * mm});
            skLineSegment(sketch, "E1132", {"start": v(-13.52, 19.6) * mm, "end": v(-13.5, 19.53) * mm});
            skLineSegment(sketch, "E1133", {"start": v(-13.5, 19.53) * mm, "end": v(-13.5, 19.46) * mm});
            skLineSegment(sketch, "E1134", {"start": v(-13.5, 19.46) * mm, "end": v(-13.47, 19.39) * mm});
            skLineSegment(sketch, "E1135", {"start": v(-13.47, 19.39) * mm, "end": v(-13.46, 19.32) * mm});
            skLineSegment(sketch, "E1136", {"start": v(-13.46, 19.32) * mm, "end": v(-13.44, 19.25) * mm});
            skLineSegment(sketch, "E1137", {"start": v(-13.44, 19.25) * mm, "end": v(-13.42, 19.18) * mm});
            skLineSegment(sketch, "E1138", {"start": v(-13.42, 19.18) * mm, "end": v(-13.4, 19.11) * mm});
            skLineSegment(sketch, "E1139", {"start": v(-13.4, 19.11) * mm, "end": v(-13.38, 19.05) * mm});
            skLineSegment(sketch, "E1140", {"start": v(-13.38, 19.05) * mm, "end": v(-13.36, 18.99) * mm});
            skLineSegment(sketch, "E1141", {"start": v(-13.36, 18.99) * mm, "end": v(-13.35, 18.93) * mm});
            skLineSegment(sketch, "E1142", {"start": v(-13.35, 18.93) * mm, "end": v(-13.33, 18.87) * mm});
            skLineSegment(sketch, "E1143", {"start": v(-13.33, 18.87) * mm, "end": v(-13.3, 18.81) * mm});
            skLineSegment(sketch, "E1144", {"start": v(-13.3, 18.81) * mm, "end": v(-13.3, 18.76) * mm});
            skLineSegment(sketch, "E1145", {"start": v(-13.3, 18.76) * mm, "end": v(-13.27, 18.7) * mm});
            skLineSegment(sketch, "E1146", {"start": v(-13.27, 18.7) * mm, "end": v(-13.25, 18.65) * mm});
            skLineSegment(sketch, "E1147", {"start": v(-13.25, 18.65) * mm, "end": v(-13.24, 18.6) * mm});
            skLineSegment(sketch, "E1148", {"start": v(-13.24, 18.6) * mm, "end": v(-13.2, 18.5) * mm});
            skLineSegment(sketch, "E1149", {"start": v(-13.2, 18.5) * mm, "end": v(-13.17, 18.42) * mm});
            skLineSegment(sketch, "E1150", {"start": v(-13.17, 18.42) * mm, "end": v(-13.14, 18.36) * mm});
            skArc(sketch, "E1151", {"start": v(-13.14, 18.36) * mm, "mid": v(-13.2, 17.99) * mm, "end": v(-13.58, 18.04) * mm});
            skLineSegment(sketch, "E1152", {"start": v(-13.58, 18.04) * mm, "end": v(-13.63, 18.08) * mm});
            skLineSegment(sketch, "E1153", {"start": v(-13.63, 18.08) * mm, "end": v(-13.7, 18.14) * mm});
            skLineSegment(sketch, "E1154", {"start": v(-13.7, 18.14) * mm, "end": v(-13.78, 18.2) * mm});
            skLineSegment(sketch, "E1155", {"start": v(-13.78, 18.2) * mm, "end": v(-13.83, 18.23) * mm});
            skLineSegment(sketch, "E1156", {"start": v(-13.83, 18.23) * mm, "end": v(-13.87, 18.27) * mm});
            skLineSegment(sketch, "E1157", {"start": v(-13.87, 18.27) * mm, "end": v(-13.91, 18.3) * mm});
            skLineSegment(sketch, "E1158", {"start": v(-13.91, 18.3) * mm, "end": v(-13.96, 18.33) * mm});
            skLineSegment(sketch, "E1159", {"start": v(-13.96, 18.33) * mm, "end": v(-14, 18.37) * mm});
            skLineSegment(sketch, "E1160", {"start": v(-14, 18.37) * mm, "end": v(-14.06, 18.4) * mm});
            skLineSegment(sketch, "E1161", {"start": v(-14.06, 18.4) * mm, "end": v(-14.11, 18.44) * mm});
            skLineSegment(sketch, "E1162", {"start": v(-14.11, 18.44) * mm, "end": v(-14.16, 18.48) * mm});
            skLineSegment(sketch, "E1163", {"start": v(-14.16, 18.48) * mm, "end": v(-14.22, 18.51) * mm});
            skLineSegment(sketch, "E1164", {"start": v(-14.22, 18.51) * mm, "end": v(-14.28, 18.55) * mm});
            skLineSegment(sketch, "E1165", {"start": v(-14.28, 18.55) * mm, "end": v(-14.34, 18.59) * mm});
            skLineSegment(sketch, "E1166", {"start": v(-14.34, 18.59) * mm, "end": v(-14.4, 18.62) * mm});
            skLineSegment(sketch, "E1167", {"start": v(-14.4, 18.62) * mm, "end": v(-14.46, 18.66) * mm});
            skLineSegment(sketch, "E1168", {"start": v(-14.46, 18.66) * mm, "end": v(-14.52, 18.7) * mm});
            skLineSegment(sketch, "E1169", {"start": v(-14.52, 18.7) * mm, "end": v(-14.59, 18.74) * mm});
            skLineSegment(sketch, "E1170", {"start": v(-14.59, 18.74) * mm, "end": v(-14.66, 18.78) * mm});
            skLineSegment(sketch, "E1171", {"start": v(-14.66, 18.78) * mm, "end": v(-14.73, 18.82) * mm});
            skLineSegment(sketch, "E1172", {"start": v(-14.73, 18.82) * mm, "end": v(-14.8, 18.86) * mm});
            skLineSegment(sketch, "E1173", {"start": v(-14.8, 18.86) * mm, "end": v(-14.87, 18.9) * mm});
            skLineSegment(sketch, "E1174", {"start": v(-14.87, 18.9) * mm, "end": v(-14.97, 18.95) * mm});
            skLineSegment(sketch, "E1175", {"start": v(-14.97, 18.95) * mm, "end": v(-15.4, 18.6) * mm});
            skLineSegment(sketch, "E1176", {"start": v(-15.4, 18.6) * mm, "end": v(-15.37, 18.5) * mm});
            skLineSegment(sketch, "E1177", {"start": v(-15.37, 18.5) * mm, "end": v(-15.35, 18.41) * mm});
            skLineSegment(sketch, "E1178", {"start": v(-15.35, 18.41) * mm, "end": v(-15.33, 18.33) * mm});
            skLineSegment(sketch, "E1179", {"start": v(-15.33, 18.33) * mm, "end": v(-15.3, 18.26) * mm});
            skLineSegment(sketch, "E1180", {"start": v(-15.3, 18.26) * mm, "end": v(-15.28, 18.18) * mm});
            skLineSegment(sketch, "E1181", {"start": v(-15.28, 18.18) * mm, "end": v(-15.25, 18.11) * mm});
            skLineSegment(sketch, "E1182", {"start": v(-15.25, 18.11) * mm, "end": v(-15.23, 18.04) * mm});
            skLineSegment(sketch, "E1183", {"start": v(-15.23, 18.04) * mm, "end": v(-15.2, 17.97) * mm});
            skLineSegment(sketch, "E1184", {"start": v(-15.2, 17.97) * mm, "end": v(-15.18, 17.9) * mm});
            skLineSegment(sketch, "E1185", {"start": v(-15.18, 17.9) * mm, "end": v(-15.16, 17.84) * mm});
            skLineSegment(sketch, "E1186", {"start": v(-15.16, 17.84) * mm, "end": v(-15.13, 17.78) * mm});
            skLineSegment(sketch, "E1187", {"start": v(-15.13, 17.78) * mm, "end": v(-15.1, 17.71) * mm});
            skLineSegment(sketch, "E1188", {"start": v(-15.1, 17.71) * mm, "end": v(-15.08, 17.65) * mm});
            skLineSegment(sketch, "E1189", {"start": v(-15.08, 17.65) * mm, "end": v(-15.06, 17.6) * mm});
            skLineSegment(sketch, "E1190", {"start": v(-15.06, 17.6) * mm, "end": v(-15.04, 17.54) * mm});
            skLineSegment(sketch, "E1191", {"start": v(-15.04, 17.54) * mm, "end": v(-15.01, 17.48) * mm});
            skLineSegment(sketch, "E1192", {"start": v(-15.01, 17.48) * mm, "end": v(-14.99, 17.43) * mm});
            skLineSegment(sketch, "E1193", {"start": v(-14.99, 17.43) * mm, "end": v(-14.97, 17.38) * mm});
            skLineSegment(sketch, "E1194", {"start": v(-14.97, 17.38) * mm, "end": v(-14.94, 17.33) * mm});
            skLineSegment(sketch, "E1195", {"start": v(-14.94, 17.33) * mm, "end": v(-14.92, 17.28) * mm});
            skLineSegment(sketch, "E1196", {"start": v(-14.92, 17.28) * mm, "end": v(-14.88, 17.2) * mm});
            skLineSegment(sketch, "E1197", {"start": v(-14.88, 17.2) * mm, "end": v(-14.83, 17.1) * mm});
            skLineSegment(sketch, "E1198", {"start": v(-14.83, 17.1) * mm, "end": v(-14.8, 17.05) * mm});
            skArc(sketch, "E1199", {"start": v(-14.8, 17.05) * mm, "mid": v(-14.83, 16.67) * mm, "end": v(-15.21, 16.69) * mm});
            skLineSegment(sketch, "E1200", {"start": v(-15.21, 16.69) * mm, "end": v(-15.26, 16.73) * mm});
            skLineSegment(sketch, "E1201", {"start": v(-15.26, 16.73) * mm, "end": v(-15.34, 16.78) * mm});
            skLineSegment(sketch, "E1202", {"start": v(-15.34, 16.78) * mm, "end": v(-15.43, 16.83) * mm});
            skLineSegment(sketch, "E1203", {"start": v(-15.43, 16.83) * mm, "end": v(-15.47, 16.86) * mm});
            skLineSegment(sketch, "E1204", {"start": v(-15.47, 16.86) * mm, "end": v(-15.52, 16.89) * mm});
            skLineSegment(sketch, "E1205", {"start": v(-15.52, 16.89) * mm, "end": v(-15.57, 16.92) * mm});
            skLineSegment(sketch, "E1206", {"start": v(-15.57, 16.92) * mm, "end": v(-15.62, 16.95) * mm});
            skLineSegment(sketch, "E1207", {"start": v(-15.62, 16.95) * mm, "end": v(-15.67, 16.98) * mm});
            skLineSegment(sketch, "E1208", {"start": v(-15.67, 16.98) * mm, "end": v(-15.72, 17) * mm});
            skLineSegment(sketch, "E1209", {"start": v(-15.72, 17) * mm, "end": v(-15.78, 17.04) * mm});
            skLineSegment(sketch, "E1210", {"start": v(-15.78, 17.04) * mm, "end": v(-15.83, 17.07) * mm});
            skLineSegment(sketch, "E1211", {"start": v(-15.83, 17.07) * mm, "end": v(-15.9, 17.1) * mm});
            skLineSegment(sketch, "E1212", {"start": v(-15.9, 17.1) * mm, "end": v(-15.95, 17.13) * mm});
            skLineSegment(sketch, "E1213", {"start": v(-15.95, 17.13) * mm, "end": v(-16.01, 17.16) * mm});
            skLineSegment(sketch, "E1214", {"start": v(-16.01, 17.16) * mm, "end": v(-16.08, 17.2) * mm});
            skLineSegment(sketch, "E1215", {"start": v(-16.08, 17.2) * mm, "end": v(-16.14, 17.23) * mm});
            skLineSegment(sketch, "E1216", {"start": v(-16.14, 17.23) * mm, "end": v(-16.21, 17.26) * mm});
            skLineSegment(sketch, "E1217", {"start": v(-16.21, 17.26) * mm, "end": v(-16.28, 17.3) * mm});
            skLineSegment(sketch, "E1218", {"start": v(-16.28, 17.3) * mm, "end": v(-16.35, 17.33) * mm});
            skLineSegment(sketch, "E1219", {"start": v(-16.35, 17.33) * mm, "end": v(-16.42, 17.36) * mm});
            skLineSegment(sketch, "E1220", {"start": v(-16.42, 17.36) * mm, "end": v(-16.5, 17.4) * mm});
            skLineSegment(sketch, "E1221", {"start": v(-16.5, 17.4) * mm, "end": v(-16.57, 17.42) * mm});
            skLineSegment(sketch, "E1222", {"start": v(-16.57, 17.42) * mm, "end": v(-16.68, 17.47) * mm});
            skLineSegment(sketch, "E1223", {"start": v(-16.68, 17.47) * mm, "end": v(-17.08, 17.08) * mm});
            skLineSegment(sketch, "E1224", {"start": v(-17.08, 17.08) * mm, "end": v(-17.04, 16.97) * mm});
            skLineSegment(sketch, "E1225", {"start": v(-17.04, 16.97) * mm, "end": v(-17, 16.9) * mm});
            skLineSegment(sketch, "E1226", {"start": v(-17, 16.9) * mm, "end": v(-16.97, 16.82) * mm});
            skLineSegment(sketch, "E1227", {"start": v(-16.97, 16.82) * mm, "end": v(-16.94, 16.74) * mm});
            skLineSegment(sketch, "E1228", {"start": v(-16.94, 16.74) * mm, "end": v(-16.91, 16.67) * mm});
            skLineSegment(sketch, "E1229", {"start": v(-16.91, 16.67) * mm, "end": v(-16.88, 16.6) * mm});
            skLineSegment(sketch, "E1230", {"start": v(-16.88, 16.6) * mm, "end": v(-16.85, 16.54) * mm});
            skLineSegment(sketch, "E1231", {"start": v(-16.85, 16.54) * mm, "end": v(-16.82, 16.47) * mm});
            skLineSegment(sketch, "E1232", {"start": v(-16.82, 16.47) * mm, "end": v(-16.8, 16.4) * mm});
            skLineSegment(sketch, "E1233", {"start": v(-16.8, 16.4) * mm, "end": v(-16.76, 16.34) * mm});
            skLineSegment(sketch, "E1234", {"start": v(-16.76, 16.34) * mm, "end": v(-16.73, 16.28) * mm});
            skLineSegment(sketch, "E1235", {"start": v(-16.73, 16.28) * mm, "end": v(-16.7, 16.22) * mm});
            skLineSegment(sketch, "E1236", {"start": v(-16.7, 16.22) * mm, "end": v(-16.67, 16.16) * mm});
            skLineSegment(sketch, "E1237", {"start": v(-16.67, 16.16) * mm, "end": v(-16.64, 16.1) * mm});
            skLineSegment(sketch, "E1238", {"start": v(-16.64, 16.1) * mm, "end": v(-16.61, 16.05) * mm});
            skLineSegment(sketch, "E1239", {"start": v(-16.61, 16.05) * mm, "end": v(-16.58, 16) * mm});
            skLineSegment(sketch, "E1240", {"start": v(-16.58, 16) * mm, "end": v(-16.56, 15.95) * mm});
            skLineSegment(sketch, "E1241", {"start": v(-16.56, 15.95) * mm, "end": v(-16.53, 15.9) * mm});
            skLineSegment(sketch, "E1242", {"start": v(-16.53, 15.9) * mm, "end": v(-16.5, 15.86) * mm});
            skLineSegment(sketch, "E1243", {"start": v(-16.5, 15.86) * mm, "end": v(-16.47, 15.81) * mm});
            skLineSegment(sketch, "E1244", {"start": v(-16.47, 15.81) * mm, "end": v(-16.42, 15.72) * mm});
            skLineSegment(sketch, "E1245", {"start": v(-16.42, 15.72) * mm, "end": v(-16.37, 15.65) * mm});
            skLineSegment(sketch, "E1246", {"start": v(-16.37, 15.65) * mm, "end": v(-16.33, 15.6) * mm});
            skArc(sketch, "E1247", {"start": v(-16.33, 15.6) * mm, "mid": v(-16.33, 15.21) * mm, "end": v(-16.7, 15.2) * mm});
            skLineSegment(sketch, "E1248", {"start": v(-16.7, 15.2) * mm, "end": v(-16.76, 15.22) * mm});
            skLineSegment(sketch, "E1249", {"start": v(-16.76, 15.22) * mm, "end": v(-16.85, 15.27) * mm});
            skLineSegment(sketch, "E1250", {"start": v(-16.85, 15.27) * mm, "end": v(-16.94, 15.31) * mm});
            skLineSegment(sketch, "E1251", {"start": v(-16.94, 15.31) * mm, "end": v(-16.98, 15.34) * mm});
            skLineSegment(sketch, "E1252", {"start": v(-16.98, 15.34) * mm, "end": v(-17.03, 15.36) * mm});
            skLineSegment(sketch, "E1253", {"start": v(-17.03, 15.36) * mm, "end": v(-17.08, 15.39) * mm});
            skLineSegment(sketch, "E1254", {"start": v(-17.08, 15.39) * mm, "end": v(-17.13, 15.41) * mm});
            skLineSegment(sketch, "E1255", {"start": v(-17.13, 15.41) * mm, "end": v(-17.19, 15.44) * mm});
            skLineSegment(sketch, "E1256", {"start": v(-17.19, 15.44) * mm, "end": v(-17.24, 15.46) * mm});
            skLineSegment(sketch, "E1257", {"start": v(-17.24, 15.46) * mm, "end": v(-17.3, 15.49) * mm});
            skLineSegment(sketch, "E1258", {"start": v(-17.3, 15.49) * mm, "end": v(-17.36, 15.51) * mm});
            skLineSegment(sketch, "E1259", {"start": v(-17.36, 15.51) * mm, "end": v(-17.42, 15.54) * mm});
            skLineSegment(sketch, "E1260", {"start": v(-17.42, 15.54) * mm, "end": v(-17.49, 15.56) * mm});
            skLineSegment(sketch, "E1261", {"start": v(-17.49, 15.56) * mm, "end": v(-17.55, 15.59) * mm});
            skLineSegment(sketch, "E1262", {"start": v(-17.55, 15.59) * mm, "end": v(-17.62, 15.62) * mm});
            skLineSegment(sketch, "E1263", {"start": v(-17.62, 15.62) * mm, "end": v(-17.69, 15.64) * mm});
            skLineSegment(sketch, "E1264", {"start": v(-17.69, 15.64) * mm, "end": v(-17.76, 15.67) * mm});
            skLineSegment(sketch, "E1265", {"start": v(-17.76, 15.67) * mm, "end": v(-17.83, 15.7) * mm});
            skLineSegment(sketch, "E1266", {"start": v(-17.83, 15.7) * mm, "end": v(-17.9, 15.72) * mm});
            skLineSegment(sketch, "E1267", {"start": v(-17.9, 15.72) * mm, "end": v(-17.98, 15.74) * mm});
            skLineSegment(sketch, "E1268", {"start": v(-17.98, 15.74) * mm, "end": v(-18.05, 15.77) * mm});
            skLineSegment(sketch, "E1269", {"start": v(-18.05, 15.77) * mm, "end": v(-18.13, 15.8) * mm});
            skLineSegment(sketch, "E1270", {"start": v(-18.13, 15.8) * mm, "end": v(-18.25, 15.83) * mm});
            skLineSegment(sketch, "E1271", {"start": v(-18.25, 15.83) * mm, "end": v(-18.6, 15.4) * mm});
            skLineSegment(sketch, "E1272", {"start": v(-18.6, 15.4) * mm, "end": v(-18.55, 15.3) * mm});
            skLineSegment(sketch, "E1273", {"start": v(-18.55, 15.3) * mm, "end": v(-18.51, 15.23) * mm});
            skLineSegment(sketch, "E1274", {"start": v(-18.51, 15.23) * mm, "end": v(-18.48, 15.16) * mm});
            skLineSegment(sketch, "E1275", {"start": v(-18.48, 15.16) * mm, "end": v(-18.44, 15.09) * mm});
            skLineSegment(sketch, "E1276", {"start": v(-18.44, 15.09) * mm, "end": v(-18.4, 15.02) * mm});
            skLineSegment(sketch, "E1277", {"start": v(-18.4, 15.02) * mm, "end": v(-18.36, 14.95) * mm});
            skLineSegment(sketch, "E1278", {"start": v(-18.36, 14.95) * mm, "end": v(-18.33, 14.89) * mm});
            skLineSegment(sketch, "E1279", {"start": v(-18.33, 14.89) * mm, "end": v(-18.29, 14.82) * mm});
            skLineSegment(sketch, "E1280", {"start": v(-18.29, 14.82) * mm, "end": v(-18.25, 14.76) * mm});
            skLineSegment(sketch, "E1281", {"start": v(-18.25, 14.76) * mm, "end": v(-18.22, 14.7) * mm});
            skLineSegment(sketch, "E1282", {"start": v(-18.22, 14.7) * mm, "end": v(-18.18, 14.64) * mm});
            skLineSegment(sketch, "E1283", {"start": v(-18.18, 14.64) * mm, "end": v(-18.15, 14.59) * mm});
            skLineSegment(sketch, "E1284", {"start": v(-18.15, 14.59) * mm, "end": v(-18.11, 14.53) * mm});
            skLineSegment(sketch, "E1285", {"start": v(-18.11, 14.53) * mm, "end": v(-18.08, 14.48) * mm});
            skLineSegment(sketch, "E1286", {"start": v(-18.08, 14.48) * mm, "end": v(-18.04, 14.43) * mm});
            skLineSegment(sketch, "E1287", {"start": v(-18.04, 14.43) * mm, "end": v(-18, 14.38) * mm});
            skLineSegment(sketch, "E1288", {"start": v(-18, 14.38) * mm, "end": v(-17.98, 14.33) * mm});
            skLineSegment(sketch, "E1289", {"start": v(-17.98, 14.33) * mm, "end": v(-17.94, 14.29) * mm});
            skLineSegment(sketch, "E1290", {"start": v(-17.94, 14.29) * mm, "end": v(-17.91, 14.24) * mm});
            skLineSegment(sketch, "E1291", {"start": v(-17.91, 14.24) * mm, "end": v(-17.88, 14.2) * mm});
            skLineSegment(sketch, "E1292", {"start": v(-17.88, 14.2) * mm, "end": v(-17.82, 14.12) * mm});
            skLineSegment(sketch, "E1293", {"start": v(-17.82, 14.12) * mm, "end": v(-17.76, 14.04) * mm});
            skLineSegment(sketch, "E1294", {"start": v(-17.76, 14.04) * mm, "end": v(-17.72, 14) * mm});
            skArc(sketch, "E1295", {"start": v(-17.72, 14) * mm, "mid": v(-17.68, 13.62) * mm, "end": v(-18.06, 13.56) * mm});
            skLineSegment(sketch, "E1296", {"start": v(-18.06, 13.56) * mm, "end": v(-18.12, 13.59) * mm});
            skLineSegment(sketch, "E1297", {"start": v(-18.12, 13.59) * mm, "end": v(-18.2, 13.62) * mm});
            skLineSegment(sketch, "E1298", {"start": v(-18.2, 13.62) * mm, "end": v(-18.3, 13.66) * mm});
            skLineSegment(sketch, "E1299", {"start": v(-18.3, 13.66) * mm, "end": v(-18.34, 13.68) * mm});
            skLineSegment(sketch, "E1300", {"start": v(-18.34, 13.68) * mm, "end": v(-18.4, 13.7) * mm});
            skLineSegment(sketch, "E1301", {"start": v(-18.4, 13.7) * mm, "end": v(-18.45, 13.72) * mm});
            skLineSegment(sketch, "E1302", {"start": v(-18.45, 13.72) * mm, "end": v(-18.5, 13.74) * mm});
            skLineSegment(sketch, "E1303", {"start": v(-18.5, 13.74) * mm, "end": v(-18.56, 13.76) * mm});
            skLineSegment(sketch, "E1304", {"start": v(-18.56, 13.76) * mm, "end": v(-18.62, 13.78) * mm});
            skLineSegment(sketch, "E1305", {"start": v(-18.62, 13.78) * mm, "end": v(-18.68, 13.8) * mm});
            skLineSegment(sketch, "E1306", {"start": v(-18.68, 13.8) * mm, "end": v(-18.74, 13.82) * mm});
            skLineSegment(sketch, "E1307", {"start": v(-18.74, 13.82) * mm, "end": v(-18.8, 13.84) * mm});
            skLineSegment(sketch, "E1308", {"start": v(-18.8, 13.84) * mm, "end": v(-18.87, 13.86) * mm});
            skLineSegment(sketch, "E1309", {"start": v(-18.87, 13.86) * mm, "end": v(-18.93, 13.88) * mm});
            skLineSegment(sketch, "E1310", {"start": v(-18.93, 13.88) * mm, "end": v(-19, 13.9) * mm});
            skLineSegment(sketch, "E1311", {"start": v(-19, 13.9) * mm, "end": v(-19.07, 13.92) * mm});
            skLineSegment(sketch, "E1312", {"start": v(-19.07, 13.92) * mm, "end": v(-19.14, 13.94) * mm});
            skLineSegment(sketch, "E1313", {"start": v(-19.14, 13.94) * mm, "end": v(-19.22, 13.96) * mm});
            skLineSegment(sketch, "E1314", {"start": v(-19.22, 13.96) * mm, "end": v(-19.3, 13.97) * mm});
            skLineSegment(sketch, "E1315", {"start": v(-19.3, 13.97) * mm, "end": v(-19.37, 14) * mm});
            skLineSegment(sketch, "E1316", {"start": v(-19.37, 14) * mm, "end": v(-19.45, 14.01) * mm});
            skLineSegment(sketch, "E1317", {"start": v(-19.45, 14.01) * mm, "end": v(-19.53, 14.03) * mm});
            skLineSegment(sketch, "E1318", {"start": v(-19.53, 14.03) * mm, "end": v(-19.65, 14.05) * mm});
            skLineSegment(sketch, "E1319", {"start": v(-19.65, 14.05) * mm, "end": v(-19.96, 13.6) * mm});
            skLineSegment(sketch, "E1320", {"start": v(-19.96, 13.6) * mm, "end": v(-19.9, 13.5) * mm});
            skLineSegment(sketch, "E1321", {"start": v(-19.9, 13.5) * mm, "end": v(-19.86, 13.43) * mm});
            skLineSegment(sketch, "E1322", {"start": v(-19.86, 13.43) * mm, "end": v(-19.81, 13.36) * mm});
            skLineSegment(sketch, "E1323", {"start": v(-19.81, 13.36) * mm, "end": v(-19.77, 13.3) * mm});
            skLineSegment(sketch, "E1324", {"start": v(-19.77, 13.3) * mm, "end": v(-19.73, 13.23) * mm});
            skLineSegment(sketch, "E1325", {"start": v(-19.73, 13.23) * mm, "end": v(-19.68, 13.17) * mm});
            skLineSegment(sketch, "E1326", {"start": v(-19.68, 13.17) * mm, "end": v(-19.64, 13.1) * mm});
            skLineSegment(sketch, "E1327", {"start": v(-19.64, 13.1) * mm, "end": v(-19.6, 13.05) * mm});
            skLineSegment(sketch, "E1328", {"start": v(-19.6, 13.05) * mm, "end": v(-19.56, 12.99) * mm});
            skLineSegment(sketch, "E1329", {"start": v(-19.56, 12.99) * mm, "end": v(-19.51, 12.93) * mm});
            skLineSegment(sketch, "E1330", {"start": v(-19.51, 12.93) * mm, "end": v(-19.47, 12.88) * mm});
            skLineSegment(sketch, "E1331", {"start": v(-19.47, 12.88) * mm, "end": v(-19.43, 12.82) * mm});
            skLineSegment(sketch, "E1332", {"start": v(-19.43, 12.82) * mm, "end": v(-19.4, 12.77) * mm});
            skLineSegment(sketch, "E1333", {"start": v(-19.4, 12.77) * mm, "end": v(-19.35, 12.72) * mm});
            skLineSegment(sketch, "E1334", {"start": v(-19.35, 12.72) * mm, "end": v(-19.31, 12.68) * mm});
            skLineSegment(sketch, "E1335", {"start": v(-19.31, 12.68) * mm, "end": v(-19.28, 12.63) * mm});
            skLineSegment(sketch, "E1336", {"start": v(-19.28, 12.63) * mm, "end": v(-19.24, 12.59) * mm});
            skLineSegment(sketch, "E1337", {"start": v(-19.24, 12.59) * mm, "end": v(-19.2, 12.54) * mm});
            skLineSegment(sketch, "E1338", {"start": v(-19.2, 12.54) * mm, "end": v(-19.17, 12.5) * mm});
            skLineSegment(sketch, "E1339", {"start": v(-19.17, 12.5) * mm, "end": v(-19.13, 12.46) * mm});
            skLineSegment(sketch, "E1340", {"start": v(-19.13, 12.46) * mm, "end": v(-19.06, 12.39) * mm});
            skLineSegment(sketch, "E1341", {"start": v(-19.06, 12.39) * mm, "end": v(-19, 12.32) * mm});
            skLineSegment(sketch, "E1342", {"start": v(-19, 12.32) * mm, "end": v(-18.95, 12.27) * mm});
            skArc(sketch, "E1343", {"start": v(-18.95, 12.27) * mm, "mid": v(-18.88, 11.9) * mm, "end": v(-19.25, 11.81) * mm});
            skLineSegment(sketch, "E1344", {"start": v(-19.25, 11.81) * mm, "end": v(-19.3, 11.83) * mm});
            skLineSegment(sketch, "E1345", {"start": v(-19.3, 11.83) * mm, "end": v(-19.4, 11.86) * mm});
            skLineSegment(sketch, "E1346", {"start": v(-19.4, 11.86) * mm, "end": v(-19.5, 11.89) * mm});
            skLineSegment(sketch, "E1347", {"start": v(-19.5, 11.89) * mm, "end": v(-19.55, 11.9) * mm});
            skLineSegment(sketch, "E1348", {"start": v(-19.55, 11.9) * mm, "end": v(-19.6, 11.92) * mm});
            skLineSegment(sketch, "E1349", {"start": v(-19.6, 11.92) * mm, "end": v(-19.65, 11.93) * mm});
            skLineSegment(sketch, "E1350", {"start": v(-19.65, 11.93) * mm, "end": v(-19.7, 11.95) * mm});
            skLineSegment(sketch, "E1351", {"start": v(-19.7, 11.95) * mm, "end": v(-19.77, 11.96) * mm});
            skLineSegment(sketch, "E1352", {"start": v(-19.77, 11.96) * mm, "end": v(-19.83, 11.98) * mm});
            skLineSegment(sketch, "E1353", {"start": v(-19.83, 11.98) * mm, "end": v(-19.89, 12) * mm});
            skLineSegment(sketch, "E1354", {"start": v(-19.89, 12) * mm, "end": v(-19.95, 12) * mm});
            skLineSegment(sketch, "E1355", {"start": v(-19.95, 12) * mm, "end": v(-20.01, 12.02) * mm});
            skLineSegment(sketch, "E1356", {"start": v(-20.01, 12.02) * mm, "end": v(-20.08, 12.03) * mm});
            skLineSegment(sketch, "E1357", {"start": v(-20.08, 12.03) * mm, "end": v(-20.15, 12.04) * mm});
            skLineSegment(sketch, "E1358", {"start": v(-20.15, 12.04) * mm, "end": v(-20.22, 12.06) * mm});
            skLineSegment(sketch, "E1359", {"start": v(-20.22, 12.06) * mm, "end": v(-20.3, 12.07) * mm});
            skLineSegment(sketch, "E1360", {"start": v(-20.3, 12.07) * mm, "end": v(-20.37, 12.08) * mm});
            skLineSegment(sketch, "E1361", {"start": v(-20.37, 12.08) * mm, "end": v(-20.44, 12.1) * mm});
            skLineSegment(sketch, "E1362", {"start": v(-20.44, 12.1) * mm, "end": v(-20.52, 12.1) * mm});
            skLineSegment(sketch, "E1363", {"start": v(-20.52, 12.1) * mm, "end": v(-20.6, 12.12) * mm});
            skLineSegment(sketch, "E1364", {"start": v(-20.6, 12.12) * mm, "end": v(-20.68, 12.13) * mm});
            skLineSegment(sketch, "E1365", {"start": v(-20.68, 12.13) * mm, "end": v(-20.76, 12.14) * mm});
            skLineSegment(sketch, "E1366", {"start": v(-20.76, 12.14) * mm, "end": v(-20.88, 12.15) * mm});
            skLineSegment(sketch, "E1367", {"start": v(-20.88, 12.15) * mm, "end": v(-21.15, 11.67) * mm});
            skLineSegment(sketch, "E1368", {"start": v(-21.15, 11.67) * mm, "end": v(-21.08, 11.58) * mm});
            skLineSegment(sketch, "E1369", {"start": v(-21.08, 11.58) * mm, "end": v(-21.03, 11.51) * mm});
            skLineSegment(sketch, "E1370", {"start": v(-21.03, 11.51) * mm, "end": v(-20.98, 11.45) * mm});
            skLineSegment(sketch, "E1371", {"start": v(-20.98, 11.45) * mm, "end": v(-20.93, 11.38) * mm});
            skLineSegment(sketch, "E1372", {"start": v(-20.93, 11.38) * mm, "end": v(-20.88, 11.32) * mm});
            skLineSegment(sketch, "E1373", {"start": v(-20.88, 11.32) * mm, "end": v(-20.83, 11.27) * mm});
            skLineSegment(sketch, "E1374", {"start": v(-20.83, 11.27) * mm, "end": v(-20.78, 11.2) * mm});
            skLineSegment(sketch, "E1375", {"start": v(-20.78, 11.2) * mm, "end": v(-20.73, 11.15) * mm});
            skLineSegment(sketch, "E1376", {"start": v(-20.73, 11.15) * mm, "end": v(-20.69, 11.1) * mm});
            skLineSegment(sketch, "E1377", {"start": v(-20.69, 11.1) * mm, "end": v(-20.64, 11.05) * mm});
            skLineSegment(sketch, "E1378", {"start": v(-20.64, 11.05) * mm, "end": v(-20.6, 11) * mm});
            skLineSegment(sketch, "E1379", {"start": v(-20.6, 11) * mm, "end": v(-20.55, 10.95) * mm});
            skLineSegment(sketch, "E1380", {"start": v(-20.55, 10.95) * mm, "end": v(-20.5, 10.9) * mm});
            skLineSegment(sketch, "E1381", {"start": v(-20.5, 10.9) * mm, "end": v(-20.46, 10.86) * mm});
            skLineSegment(sketch, "E1382", {"start": v(-20.46, 10.86) * mm, "end": v(-20.42, 10.81) * mm});
            skLineSegment(sketch, "E1383", {"start": v(-20.42, 10.81) * mm, "end": v(-20.37, 10.77) * mm});
            skLineSegment(sketch, "E1384", {"start": v(-20.37, 10.77) * mm, "end": v(-20.33, 10.73) * mm});
            skLineSegment(sketch, "E1385", {"start": v(-20.33, 10.73) * mm, "end": v(-20.3, 10.7) * mm});
            skLineSegment(sketch, "E1386", {"start": v(-20.3, 10.7) * mm, "end": v(-20.25, 10.65) * mm});
            skLineSegment(sketch, "E1387", {"start": v(-20.25, 10.65) * mm, "end": v(-20.22, 10.62) * mm});
            skLineSegment(sketch, "E1388", {"start": v(-20.22, 10.62) * mm, "end": v(-20.14, 10.55) * mm});
            skLineSegment(sketch, "E1389", {"start": v(-20.14, 10.55) * mm, "end": v(-20.07, 10.49) * mm});
            skLineSegment(sketch, "E1390", {"start": v(-20.07, 10.49) * mm, "end": v(-20.02, 10.44) * mm});
            skArc(sketch, "E1391", {"start": v(-20.02, 10.44) * mm, "mid": v(-19.9, 10.08) * mm, "end": v(-20.27, 9.96) * mm});
            skLineSegment(sketch, "E1392", {"start": v(-20.27, 9.96) * mm, "end": v(-20.33, 9.97) * mm});
            skLineSegment(sketch, "E1393", {"start": v(-20.33, 9.97) * mm, "end": v(-20.42, 10) * mm});
            skLineSegment(sketch, "E1394", {"start": v(-20.42, 10) * mm, "end": v(-20.52, 10.01) * mm});
            skLineSegment(sketch, "E1395", {"start": v(-20.52, 10.01) * mm, "end": v(-20.57, 10.02) * mm});
            skLineSegment(sketch, "E1396", {"start": v(-20.57, 10.02) * mm, "end": v(-20.63, 10.03) * mm});
            skLineSegment(sketch, "E1397", {"start": v(-20.63, 10.03) * mm, "end": v(-20.68, 10.04) * mm});
            skLineSegment(sketch, "E1398", {"start": v(-20.68, 10.04) * mm, "end": v(-20.74, 10.05) * mm});
            skLineSegment(sketch, "E1399", {"start": v(-20.74, 10.05) * mm, "end": v(-20.8, 10.06) * mm});
            skLineSegment(sketch, "E1400", {"start": v(-20.8, 10.06) * mm, "end": v(-20.86, 10.07) * mm});
            skLineSegment(sketch, "E1401", {"start": v(-20.86, 10.07) * mm, "end": v(-20.92, 10.08) * mm});
            skLineSegment(sketch, "E1402", {"start": v(-20.92, 10.08) * mm, "end": v(-20.99, 10.08) * mm});
            skLineSegment(sketch, "E1403", {"start": v(-20.99, 10.08) * mm, "end": v(-21.05, 10.1) * mm});
            skLineSegment(sketch, "E1404", {"start": v(-21.05, 10.1) * mm, "end": v(-21.12, 10.1) * mm});
            skLineSegment(sketch, "E1405", {"start": v(-21.12, 10.1) * mm, "end": v(-21.19, 10.1) * mm});
            skLineSegment(sketch, "E1406", {"start": v(-21.19, 10.1) * mm, "end": v(-21.26, 10.11) * mm});
            skLineSegment(sketch, "E1407", {"start": v(-21.26, 10.11) * mm, "end": v(-21.33, 10.12) * mm});
            skLineSegment(sketch, "E1408", {"start": v(-21.33, 10.12) * mm, "end": v(-21.4, 10.12) * mm});
            skLineSegment(sketch, "E1409", {"start": v(-21.4, 10.12) * mm, "end": v(-21.48, 10.13) * mm});
            skLineSegment(sketch, "E1410", {"start": v(-21.48, 10.13) * mm, "end": v(-21.56, 10.13) * mm});
            skLineSegment(sketch, "E1411", {"start": v(-21.56, 10.13) * mm, "end": v(-21.64, 10.14) * mm});
            skLineSegment(sketch, "E1412", {"start": v(-21.64, 10.14) * mm, "end": v(-21.72, 10.14) * mm});
            skLineSegment(sketch, "E1413", {"start": v(-21.72, 10.14) * mm, "end": v(-21.8, 10.14) * mm});
            skLineSegment(sketch, "E1414", {"start": v(-21.8, 10.14) * mm, "end": v(-21.92, 10.14) * mm});
            skLineSegment(sketch, "E1415", {"start": v(-21.92, 10.14) * mm, "end": v(-22.15, 9.64) * mm});
            skLineSegment(sketch, "E1416", {"start": v(-22.15, 9.64) * mm, "end": v(-22.07, 9.55) * mm});
            skLineSegment(sketch, "E1417", {"start": v(-22.07, 9.55) * mm, "end": v(-22.01, 9.5) * mm});
            skLineSegment(sketch, "E1418", {"start": v(-22.01, 9.5) * mm, "end": v(-21.96, 9.43) * mm});
            skLineSegment(sketch, "E1419", {"start": v(-21.96, 9.43) * mm, "end": v(-21.9, 9.38) * mm});
            skLineSegment(sketch, "E1420", {"start": v(-21.9, 9.38) * mm, "end": v(-21.85, 9.32) * mm});
            skLineSegment(sketch, "E1421", {"start": v(-21.85, 9.32) * mm, "end": v(-21.8, 9.27) * mm});
            skLineSegment(sketch, "E1422", {"start": v(-21.8, 9.27) * mm, "end": v(-21.74, 9.21) * mm});
            skLineSegment(sketch, "E1423", {"start": v(-21.74, 9.21) * mm, "end": v(-21.69, 9.16) * mm});
            skLineSegment(sketch, "E1424", {"start": v(-21.69, 9.16) * mm, "end": v(-21.63, 9.11) * mm});
            skLineSegment(sketch, "E1425", {"start": v(-21.63, 9.11) * mm, "end": v(-21.58, 9.07) * mm});
            skLineSegment(sketch, "E1426", {"start": v(-21.58, 9.07) * mm, "end": v(-21.53, 9.02) * mm});
            skLineSegment(sketch, "E1427", {"start": v(-21.53, 9.02) * mm, "end": v(-21.48, 8.98) * mm});
            skLineSegment(sketch, "E1428", {"start": v(-21.48, 8.98) * mm, "end": v(-21.43, 8.93) * mm});
            skLineSegment(sketch, "E1429", {"start": v(-21.43, 8.93) * mm, "end": v(-21.39, 8.9) * mm});
            skLineSegment(sketch, "E1430", {"start": v(-21.39, 8.9) * mm, "end": v(-21.34, 8.85) * mm});
            skLineSegment(sketch, "E1431", {"start": v(-21.34, 8.85) * mm, "end": v(-21.3, 8.82) * mm});
            skLineSegment(sketch, "E1432", {"start": v(-21.3, 8.82) * mm, "end": v(-21.25, 8.78) * mm});
            skLineSegment(sketch, "E1433", {"start": v(-21.25, 8.78) * mm, "end": v(-21.2, 8.74) * mm});
            skLineSegment(sketch, "E1434", {"start": v(-21.2, 8.74) * mm, "end": v(-21.16, 8.71) * mm});
            skLineSegment(sketch, "E1435", {"start": v(-21.16, 8.71) * mm, "end": v(-21.12, 8.68) * mm});
            skLineSegment(sketch, "E1436", {"start": v(-21.12, 8.68) * mm, "end": v(-21.04, 8.62) * mm});
            skLineSegment(sketch, "E1437", {"start": v(-21.04, 8.62) * mm, "end": v(-20.96, 8.56) * mm});
            skLineSegment(sketch, "E1438", {"start": v(-20.96, 8.56) * mm, "end": v(-20.91, 8.52) * mm});
            skArc(sketch, "E1439", {"start": v(-20.91, 8.52) * mm, "mid": v(-20.77, 8.17) * mm, "end": v(-21.11, 8.02) * mm});
            skLineSegment(sketch, "E1440", {"start": v(-21.11, 8.02) * mm, "end": v(-21.18, 8.03) * mm});
            skLineSegment(sketch, "E1441", {"start": v(-21.18, 8.03) * mm, "end": v(-21.27, 8.04) * mm});
            skLineSegment(sketch, "E1442", {"start": v(-21.27, 8.04) * mm, "end": v(-21.37, 8.05) * mm});
            skLineSegment(sketch, "E1443", {"start": v(-21.37, 8.05) * mm, "end": v(-21.42, 8.05) * mm});
            skLineSegment(sketch, "E1444", {"start": v(-21.42, 8.05) * mm, "end": v(-21.48, 8.06) * mm});
            skLineSegment(sketch, "E1445", {"start": v(-21.48, 8.06) * mm, "end": v(-21.53, 8.06) * mm});
            skLineSegment(sketch, "E1446", {"start": v(-21.53, 8.06) * mm, "end": v(-21.6, 8.06) * mm});
            skLineSegment(sketch, "E1447", {"start": v(-21.6, 8.06) * mm, "end": v(-21.65, 8.07) * mm});
            skLineSegment(sketch, "E1448", {"start": v(-21.65, 8.07) * mm, "end": v(-21.71, 8.07) * mm});
            skLineSegment(sketch, "E1449", {"start": v(-21.71, 8.07) * mm, "end": v(-21.77, 8.07) * mm});
            skLineSegment(sketch, "E1450", {"start": v(-21.77, 8.07) * mm, "end": v(-21.84, 8.08) * mm});
            skLineSegment(sketch, "E1451", {"start": v(-21.84, 8.08) * mm, "end": v(-21.9, 8.08) * mm});
            skLineSegment(sketch, "E1452", {"start": v(-21.9, 8.08) * mm, "end": v(-21.97, 8.08) * mm});
            skLineSegment(sketch, "E1453", {"start": v(-21.97, 8.08) * mm, "end": v(-22.04, 8.08) * mm});
            skLineSegment(sketch, "E1454", {"start": v(-22.04, 8.08) * mm, "end": v(-22.11, 8.08) * mm});
            skLineSegment(sketch, "E1455", {"start": v(-22.11, 8.08) * mm, "end": v(-22.19, 8.08) * mm});
            skLineSegment(sketch, "E1456", {"start": v(-22.19, 8.08) * mm, "end": v(-22.26, 8.07) * mm});
            skLineSegment(sketch, "E1457", {"start": v(-22.26, 8.07) * mm, "end": v(-22.34, 8.07) * mm});
            skLineSegment(sketch, "E1458", {"start": v(-22.34, 8.07) * mm, "end": v(-22.42, 8.07) * mm});
            skLineSegment(sketch, "E1459", {"start": v(-22.42, 8.07) * mm, "end": v(-22.5, 8.07) * mm});
            skLineSegment(sketch, "E1460", {"start": v(-22.5, 8.07) * mm, "end": v(-22.58, 8.06) * mm});
            skLineSegment(sketch, "E1461", {"start": v(-22.58, 8.06) * mm, "end": v(-22.66, 8.06) * mm});
            skLineSegment(sketch, "E1462", {"start": v(-22.66, 8.06) * mm, "end": v(-22.78, 8.05) * mm});
            skLineSegment(sketch, "E1463", {"start": v(-22.78, 8.05) * mm, "end": v(-22.96, 7.52) * mm});
            skLineSegment(sketch, "E1464", {"start": v(-22.96, 7.52) * mm, "end": v(-22.87, 7.44) * mm});
            skLineSegment(sketch, "E1465", {"start": v(-22.87, 7.44) * mm, "end": v(-22.8, 7.39) * mm});
            skLineSegment(sketch, "E1466", {"start": v(-22.8, 7.39) * mm, "end": v(-22.74, 7.34) * mm});
            skLineSegment(sketch, "E1467", {"start": v(-22.74, 7.34) * mm, "end": v(-22.68, 7.28) * mm});
            skLineSegment(sketch, "E1468", {"start": v(-22.68, 7.28) * mm, "end": v(-22.62, 7.23) * mm});
            skLineSegment(sketch, "E1469", {"start": v(-22.62, 7.23) * mm, "end": v(-22.56, 7.19) * mm});
            skLineSegment(sketch, "E1470", {"start": v(-22.56, 7.19) * mm, "end": v(-22.5, 7.14) * mm});
            skLineSegment(sketch, "E1471", {"start": v(-22.5, 7.14) * mm, "end": v(-22.45, 7.1) * mm});
            skLineSegment(sketch, "E1472", {"start": v(-22.45, 7.1) * mm, "end": v(-22.4, 7.05) * mm});
            skLineSegment(sketch, "E1473", {"start": v(-22.4, 7.05) * mm, "end": v(-22.34, 7) * mm});
            skLineSegment(sketch, "E1474", {"start": v(-22.34, 7) * mm, "end": v(-22.28, 6.97) * mm});
            skLineSegment(sketch, "E1475", {"start": v(-22.28, 6.97) * mm, "end": v(-22.23, 6.93) * mm});
            skLineSegment(sketch, "E1476", {"start": v(-22.23, 6.93) * mm, "end": v(-22.18, 6.89) * mm});
            skLineSegment(sketch, "E1477", {"start": v(-22.18, 6.89) * mm, "end": v(-22.13, 6.85) * mm});
            skLineSegment(sketch, "E1478", {"start": v(-22.13, 6.85) * mm, "end": v(-22.08, 6.82) * mm});
            skLineSegment(sketch, "E1479", {"start": v(-22.08, 6.82) * mm, "end": v(-22.03, 6.78) * mm});
            skLineSegment(sketch, "E1480", {"start": v(-22.03, 6.78) * mm, "end": v(-21.98, 6.75) * mm});
            skLineSegment(sketch, "E1481", {"start": v(-21.98, 6.75) * mm, "end": v(-21.93, 6.72) * mm});
            skLineSegment(sketch, "E1482", {"start": v(-21.93, 6.72) * mm, "end": v(-21.89, 6.7) * mm});
            skLineSegment(sketch, "E1483", {"start": v(-21.89, 6.7) * mm, "end": v(-21.84, 6.66) * mm});
            skLineSegment(sketch, "E1484", {"start": v(-21.84, 6.66) * mm, "end": v(-21.75, 6.61) * mm});
            skLineSegment(sketch, "E1485", {"start": v(-21.75, 6.61) * mm, "end": v(-21.67, 6.56) * mm});
            skLineSegment(sketch, "E1486", {"start": v(-21.67, 6.56) * mm, "end": v(-21.62, 6.53) * mm});
            skArc(sketch, "E1487", {"start": v(-21.62, 6.53) * mm, "mid": v(-21.44, 6.2) * mm, "end": v(-21.77, 6) * mm});
            skLineSegment(sketch, "E1488", {"start": v(-21.77, 6) * mm, "end": v(-21.83, 6) * mm});
            skLineSegment(sketch, "E1489", {"start": v(-21.83, 6) * mm, "end": v(-21.93, 6.01) * mm});
            skLineSegment(sketch, "E1490", {"start": v(-21.93, 6.01) * mm, "end": v(-22.03, 6.01) * mm});
            skLineSegment(sketch, "E1491", {"start": v(-22.03, 6.01) * mm, "end": v(-22.08, 6.01) * mm});
            skLineSegment(sketch, "E1492", {"start": v(-22.08, 6.01) * mm, "end": v(-22.14, 6.01) * mm});
            skLineSegment(sketch, "E1493", {"start": v(-22.14, 6.01) * mm, "end": v(-22.2, 6) * mm});
            skLineSegment(sketch, "E1494", {"start": v(-22.2, 6) * mm, "end": v(-22.25, 6) * mm});
            skLineSegment(sketch, "E1495", {"start": v(-22.25, 6) * mm, "end": v(-22.3, 6) * mm});
            skLineSegment(sketch, "E1496", {"start": v(-22.3, 6) * mm, "end": v(-22.37, 6) * mm});
            skLineSegment(sketch, "E1497", {"start": v(-22.37, 6) * mm, "end": v(-22.43, 6) * mm});
            skLineSegment(sketch, "E1498", {"start": v(-22.43, 6) * mm, "end": v(-22.5, 6) * mm});
            skLineSegment(sketch, "E1499", {"start": v(-22.5, 6) * mm, "end": v(-22.56, 6) * mm});
            skLineSegment(sketch, "E1500", {"start": v(-22.56, 6) * mm, "end": v(-22.63, 5.99) * mm});
            skLineSegment(sketch, "E1501", {"start": v(-22.63, 5.99) * mm, "end": v(-22.7, 5.98) * mm});
            skLineSegment(sketch, "E1502", {"start": v(-22.7, 5.98) * mm, "end": v(-22.77, 5.97) * mm});
            skLineSegment(sketch, "E1503", {"start": v(-22.77, 5.97) * mm, "end": v(-22.85, 5.96) * mm});
            skLineSegment(sketch, "E1504", {"start": v(-22.85, 5.96) * mm, "end": v(-22.92, 5.96) * mm});
            skLineSegment(sketch, "E1505", {"start": v(-22.92, 5.96) * mm, "end": v(-23, 5.95) * mm});
            skLineSegment(sketch, "E1506", {"start": v(-23, 5.95) * mm, "end": v(-23.07, 5.94) * mm});
            skLineSegment(sketch, "E1507", {"start": v(-23.07, 5.94) * mm, "end": v(-23.15, 5.92) * mm});
            skLineSegment(sketch, "E1508", {"start": v(-23.15, 5.92) * mm, "end": v(-23.23, 5.91) * mm});
            skLineSegment(sketch, "E1509", {"start": v(-23.23, 5.91) * mm, "end": v(-23.31, 5.9) * mm});
            skLineSegment(sketch, "E1510", {"start": v(-23.31, 5.9) * mm, "end": v(-23.43, 5.88) * mm});
            skLineSegment(sketch, "E1511", {"start": v(-23.43, 5.88) * mm, "end": v(-23.56, 5.34) * mm});
            skLineSegment(sketch, "E1512", {"start": v(-23.56, 5.34) * mm, "end": v(-23.46, 5.27) * mm});
            skLineSegment(sketch, "E1513", {"start": v(-23.46, 5.27) * mm, "end": v(-23.4, 5.22) * mm});
            skLineSegment(sketch, "E1514", {"start": v(-23.4, 5.22) * mm, "end": v(-23.33, 5.17) * mm});
            skLineSegment(sketch, "E1515", {"start": v(-23.33, 5.17) * mm, "end": v(-23.27, 5.13) * mm});
            skLineSegment(sketch, "E1516", {"start": v(-23.27, 5.13) * mm, "end": v(-23.2, 5.08) * mm});
            skLineSegment(sketch, "E1517", {"start": v(-23.2, 5.08) * mm, "end": v(-23.14, 5.04) * mm});
            skLineSegment(sketch, "E1518", {"start": v(-23.14, 5.04) * mm, "end": v(-23.08, 5) * mm});
            skLineSegment(sketch, "E1519", {"start": v(-23.08, 5) * mm, "end": v(-23.01, 4.96) * mm});
            skLineSegment(sketch, "E1520", {"start": v(-23.01, 4.96) * mm, "end": v(-22.95, 4.92) * mm});
            skLineSegment(sketch, "E1521", {"start": v(-22.95, 4.92) * mm, "end": v(-22.9, 4.89) * mm});
            skLineSegment(sketch, "E1522", {"start": v(-22.9, 4.89) * mm, "end": v(-22.84, 4.85) * mm});
            skLineSegment(sketch, "E1523", {"start": v(-22.84, 4.85) * mm, "end": v(-22.78, 4.82) * mm});
            skLineSegment(sketch, "E1524", {"start": v(-22.78, 4.82) * mm, "end": v(-22.72, 4.78) * mm});
            skLineSegment(sketch, "E1525", {"start": v(-22.72, 4.78) * mm, "end": v(-22.67, 4.75) * mm});
            skLineSegment(sketch, "E1526", {"start": v(-22.67, 4.75) * mm, "end": v(-22.62, 4.72) * mm});
            skLineSegment(sketch, "E1527", {"start": v(-22.62, 4.72) * mm, "end": v(-22.56, 4.7) * mm});
            skLineSegment(sketch, "E1528", {"start": v(-22.56, 4.7) * mm, "end": v(-22.51, 4.66) * mm});
            skLineSegment(sketch, "E1529", {"start": v(-22.51, 4.66) * mm, "end": v(-22.46, 4.64) * mm});
            skLineSegment(sketch, "E1530", {"start": v(-22.46, 4.64) * mm, "end": v(-22.42, 4.61) * mm});
            skLineSegment(sketch, "E1531", {"start": v(-22.42, 4.61) * mm, "end": v(-22.37, 4.59) * mm});
            skLineSegment(sketch, "E1532", {"start": v(-22.37, 4.59) * mm, "end": v(-22.28, 4.54) * mm});
            skLineSegment(sketch, "E1533", {"start": v(-22.28, 4.54) * mm, "end": v(-22.2, 4.5) * mm});
            skLineSegment(sketch, "E1534", {"start": v(-22.2, 4.5) * mm, "end": v(-22.13, 4.48) * mm});
            skArc(sketch, "E1535", {"start": v(-22.13, 4.48) * mm, "mid": v(-21.93, 4.16) * mm, "end": v(-22.24, 3.94) * mm});
            skLineSegment(sketch, "E1536", {"start": v(-22.24, 3.94) * mm, "end": v(-22.3, 3.94) * mm});
            skLineSegment(sketch, "E1537", {"start": v(-22.3, 3.94) * mm, "end": v(-22.4, 3.93) * mm});
            skLineSegment(sketch, "E1538", {"start": v(-22.4, 3.93) * mm, "end": v(-22.5, 3.92) * mm});
            skLineSegment(sketch, "E1539", {"start": v(-22.5, 3.92) * mm, "end": v(-22.55, 3.92) * mm});
            skLineSegment(sketch, "E1540", {"start": v(-22.55, 3.92) * mm, "end": v(-22.6, 3.91) * mm});
            skLineSegment(sketch, "E1541", {"start": v(-22.6, 3.91) * mm, "end": v(-22.66, 3.9) * mm});
            skLineSegment(sketch, "E1542", {"start": v(-22.66, 3.9) * mm, "end": v(-22.72, 3.9) * mm});
            skLineSegment(sketch, "E1543", {"start": v(-22.72, 3.9) * mm, "end": v(-22.77, 3.9) * mm});
            skLineSegment(sketch, "E1544", {"start": v(-22.77, 3.9) * mm, "end": v(-22.84, 3.88) * mm});
            skLineSegment(sketch, "E1545", {"start": v(-22.84, 3.88) * mm, "end": v(-22.9, 3.87) * mm});
            skLineSegment(sketch, "E1546", {"start": v(-22.9, 3.87) * mm, "end": v(-22.96, 3.86) * mm});
            skLineSegment(sketch, "E1547", {"start": v(-22.96, 3.86) * mm, "end": v(-23.03, 3.85) * mm});
            skLineSegment(sketch, "E1548", {"start": v(-23.03, 3.85) * mm, "end": v(-23.1, 3.84) * mm});
            skLineSegment(sketch, "E1549", {"start": v(-23.1, 3.84) * mm, "end": v(-23.16, 3.83) * mm});
            skLineSegment(sketch, "E1550", {"start": v(-23.16, 3.83) * mm, "end": v(-23.23, 3.81) * mm});
            skLineSegment(sketch, "E1551", {"start": v(-23.23, 3.81) * mm, "end": v(-23.3, 3.8) * mm});
            skLineSegment(sketch, "E1552", {"start": v(-23.3, 3.8) * mm, "end": v(-23.38, 3.78) * mm});
            skLineSegment(sketch, "E1553", {"start": v(-23.38, 3.78) * mm, "end": v(-23.45, 3.77) * mm});
            skLineSegment(sketch, "E1554", {"start": v(-23.45, 3.77) * mm, "end": v(-23.53, 3.75) * mm});
            skLineSegment(sketch, "E1555", {"start": v(-23.53, 3.75) * mm, "end": v(-23.6, 3.73) * mm});
            skLineSegment(sketch, "E1556", {"start": v(-23.6, 3.73) * mm, "end": v(-23.68, 3.71) * mm});
            skLineSegment(sketch, "E1557", {"start": v(-23.68, 3.71) * mm, "end": v(-23.76, 3.7) * mm});
            skLineSegment(sketch, "E1558", {"start": v(-23.76, 3.7) * mm, "end": v(-23.88, 3.66) * mm});
            skLineSegment(sketch, "E1559", {"start": v(-23.88, 3.66) * mm, "end": v(-23.96, 3.11) * mm});
            skLineSegment(sketch, "E1560", {"start": v(-23.96, 3.11) * mm, "end": v(-23.85, 3.05) * mm});
            skLineSegment(sketch, "E1561", {"start": v(-23.85, 3.05) * mm, "end": v(-23.78, 3) * mm});
            skLineSegment(sketch, "E1562", {"start": v(-23.78, 3) * mm, "end": v(-23.71, 2.97) * mm});
            skLineSegment(sketch, "E1563", {"start": v(-23.71, 2.97) * mm, "end": v(-23.64, 2.93) * mm});
            skLineSegment(sketch, "E1564", {"start": v(-23.64, 2.93) * mm, "end": v(-23.58, 2.89) * mm});
            skLineSegment(sketch, "E1565", {"start": v(-23.58, 2.89) * mm, "end": v(-23.5, 2.85) * mm});
            skLineSegment(sketch, "E1566", {"start": v(-23.5, 2.85) * mm, "end": v(-23.44, 2.82) * mm});
            skLineSegment(sketch, "E1567", {"start": v(-23.44, 2.82) * mm, "end": v(-23.38, 2.78) * mm});
            skLineSegment(sketch, "E1568", {"start": v(-23.38, 2.78) * mm, "end": v(-23.31, 2.75) * mm});
            skLineSegment(sketch, "E1569", {"start": v(-23.31, 2.75) * mm, "end": v(-23.25, 2.72) * mm});
            skLineSegment(sketch, "E1570", {"start": v(-23.25, 2.72) * mm, "end": v(-23.2, 2.7) * mm});
            skLineSegment(sketch, "E1571", {"start": v(-23.2, 2.7) * mm, "end": v(-23.13, 2.66) * mm});
            skLineSegment(sketch, "E1572", {"start": v(-23.13, 2.66) * mm, "end": v(-23.07, 2.63) * mm});
            skLineSegment(sketch, "E1573", {"start": v(-23.07, 2.63) * mm, "end": v(-23.02, 2.6) * mm});
            skLineSegment(sketch, "E1574", {"start": v(-23.02, 2.6) * mm, "end": v(-22.96, 2.58) * mm});
            skLineSegment(sketch, "E1575", {"start": v(-22.96, 2.58) * mm, "end": v(-22.9, 2.56) * mm});
            skLineSegment(sketch, "E1576", {"start": v(-22.9, 2.56) * mm, "end": v(-22.85, 2.54) * mm});
            skLineSegment(sketch, "E1577", {"start": v(-22.85, 2.54) * mm, "end": v(-22.8, 2.52) * mm});
            skLineSegment(sketch, "E1578", {"start": v(-22.8, 2.52) * mm, "end": v(-22.75, 2.5) * mm});
            skLineSegment(sketch, "E1579", {"start": v(-22.75, 2.5) * mm, "end": v(-22.7, 2.48) * mm});
            skLineSegment(sketch, "E1580", {"start": v(-22.7, 2.48) * mm, "end": v(-22.6, 2.44) * mm});
            skLineSegment(sketch, "E1581", {"start": v(-22.6, 2.44) * mm, "end": v(-22.52, 2.4) * mm});
            skLineSegment(sketch, "E1582", {"start": v(-22.52, 2.4) * mm, "end": v(-22.46, 2.39) * mm});
            skArc(sketch, "E1583", {"start": v(-22.46, 2.39) * mm, "mid": v(-22.22, 2.09) * mm, "end": v(-22.5, 1.84) * mm});
            skLineSegment(sketch, "E1584", {"start": v(-22.5, 1.84) * mm, "end": v(-22.57, 1.83) * mm});
            skLineSegment(sketch, "E1585", {"start": v(-22.57, 1.83) * mm, "end": v(-22.66, 1.82) * mm});
            skLineSegment(sketch, "E1586", {"start": v(-22.66, 1.82) * mm, "end": v(-22.76, 1.8) * mm});
            skLineSegment(sketch, "E1587", {"start": v(-22.76, 1.8) * mm, "end": v(-22.82, 1.79) * mm});
            skLineSegment(sketch, "E1588", {"start": v(-22.82, 1.79) * mm, "end": v(-22.87, 1.78) * mm});
            skLineSegment(sketch, "E1589", {"start": v(-22.87, 1.78) * mm, "end": v(-22.92, 1.77) * mm});
            skLineSegment(sketch, "E1590", {"start": v(-22.92, 1.77) * mm, "end": v(-22.98, 1.75) * mm});
            skLineSegment(sketch, "E1591", {"start": v(-22.98, 1.75) * mm, "end": v(-23.04, 1.74) * mm});
            skLineSegment(sketch, "E1592", {"start": v(-23.04, 1.74) * mm, "end": v(-23.1, 1.73) * mm});
            skLineSegment(sketch, "E1593", {"start": v(-23.1, 1.73) * mm, "end": v(-23.16, 1.71) * mm});
            skLineSegment(sketch, "E1594", {"start": v(-23.16, 1.71) * mm, "end": v(-23.22, 1.7) * mm});
            skLineSegment(sketch, "E1595", {"start": v(-23.22, 1.7) * mm, "end": v(-23.29, 1.68) * mm});
            skLineSegment(sketch, "E1596", {"start": v(-23.29, 1.68) * mm, "end": v(-23.35, 1.66) * mm});
            skLineSegment(sketch, "E1597", {"start": v(-23.35, 1.66) * mm, "end": v(-23.42, 1.64) * mm});
            skLineSegment(sketch, "E1598", {"start": v(-23.42, 1.64) * mm, "end": v(-23.49, 1.62) * mm});
            skLineSegment(sketch, "E1599", {"start": v(-23.49, 1.62) * mm, "end": v(-23.56, 1.6) * mm});
            skLineSegment(sketch, "E1600", {"start": v(-23.56, 1.6) * mm, "end": v(-23.63, 1.58) * mm});
            skLineSegment(sketch, "E1601", {"start": v(-23.63, 1.58) * mm, "end": v(-23.7, 1.56) * mm});
            skLineSegment(sketch, "E1602", {"start": v(-23.7, 1.56) * mm, "end": v(-23.77, 1.53) * mm});
            skLineSegment(sketch, "E1603", {"start": v(-23.77, 1.53) * mm, "end": v(-23.85, 1.5) * mm});
            skLineSegment(sketch, "E1604", {"start": v(-23.85, 1.5) * mm, "end": v(-23.93, 1.48) * mm});
            skLineSegment(sketch, "E1605", {"start": v(-23.93, 1.48) * mm, "end": v(-24, 1.45) * mm});
            skLineSegment(sketch, "E1606", {"start": v(-24, 1.45) * mm, "end": v(-24.12, 1.4) * mm});
            skLineSegment(sketch, "E1607", {"start": v(-24.12, 1.4) * mm, "end": v(-24.14, 0.86) * mm});
            skLineSegment(sketch, "E1608", {"start": v(-24.14, 0.86) * mm, "end": v(-24.04, 0.8) * mm});
            skLineSegment(sketch, "E1609", {"start": v(-24.04, 0.8) * mm, "end": v(-23.96, 0.77) * mm});
            skLineSegment(sketch, "E1610", {"start": v(-23.96, 0.77) * mm, "end": v(-23.89, 0.73) * mm});
            skLineSegment(sketch, "E1611", {"start": v(-23.89, 0.73) * mm, "end": v(-23.81, 0.7) * mm});
            skLineSegment(sketch, "E1612", {"start": v(-23.81, 0.7) * mm, "end": v(-23.74, 0.67) * mm});
            skLineSegment(sketch, "E1613", {"start": v(-23.74, 0.67) * mm, "end": v(-23.67, 0.64) * mm});
            skLineSegment(sketch, "E1614", {"start": v(-23.67, 0.64) * mm, "end": v(-23.6, 0.61) * mm});
            skLineSegment(sketch, "E1615", {"start": v(-23.6, 0.61) * mm, "end": v(-23.54, 0.58) * mm});
            skLineSegment(sketch, "E1616", {"start": v(-23.54, 0.58) * mm, "end": v(-23.47, 0.56) * mm});
            skLineSegment(sketch, "E1617", {"start": v(-23.47, 0.56) * mm, "end": v(-23.4, 0.53) * mm});
            skLineSegment(sketch, "E1618", {"start": v(-23.4, 0.53) * mm, "end": v(-23.34, 0.5) * mm});
            skLineSegment(sketch, "E1619", {"start": v(-23.34, 0.5) * mm, "end": v(-23.28, 0.48) * mm});
            skLineSegment(sketch, "E1620", {"start": v(-23.28, 0.48) * mm, "end": v(-23.22, 0.46) * mm});
            skLineSegment(sketch, "E1621", {"start": v(-23.22, 0.46) * mm, "end": v(-23.16, 0.44) * mm});
            skLineSegment(sketch, "E1622", {"start": v(-23.16, 0.44) * mm, "end": v(-23.1, 0.42) * mm});
            skLineSegment(sketch, "E1623", {"start": v(-23.1, 0.42) * mm, "end": v(-23.04, 0.4) * mm});
            skLineSegment(sketch, "E1624", {"start": v(-23.04, 0.4) * mm, "end": v(-22.99, 0.39) * mm});
            skLineSegment(sketch, "E1625", {"start": v(-22.99, 0.39) * mm, "end": v(-22.94, 0.37) * mm});
            skLineSegment(sketch, "E1626", {"start": v(-22.94, 0.37) * mm, "end": v(-22.88, 0.35) * mm});
            skLineSegment(sketch, "E1627", {"start": v(-22.88, 0.35) * mm, "end": v(-22.83, 0.34) * mm});
            skLineSegment(sketch, "E1628", {"start": v(-22.83, 0.34) * mm, "end": v(-22.74, 0.31) * mm});
            skLineSegment(sketch, "E1629", {"start": v(-22.74, 0.31) * mm, "end": v(-22.64, 0.29) * mm});
            skLineSegment(sketch, "E1630", {"start": v(-22.64, 0.29) * mm, "end": v(-22.58, 0.27) * mm});
            skArc(sketch, "E1631", {"start": v(-22.58, 0.27) * mm, "mid": v(-22.32, 0) * mm, "end": v(-22.58, -0.27) * mm});
            skLineSegment(sketch, "E1632", {"start": v(-22.58, -0.27) * mm, "end": v(-22.64, -0.29) * mm});
            skLineSegment(sketch, "E1633", {"start": v(-22.64, -0.29) * mm, "end": v(-22.74, -0.31) * mm});
            skLineSegment(sketch, "E1634", {"start": v(-22.74, -0.31) * mm, "end": v(-22.83, -0.34) * mm});
            skLineSegment(sketch, "E1635", {"start": v(-22.83, -0.34) * mm, "end": v(-22.88, -0.35) * mm});
            skLineSegment(sketch, "E1636", {"start": v(-22.88, -0.35) * mm, "end": v(-22.94, -0.37) * mm});
            skLineSegment(sketch, "E1637", {"start": v(-22.94, -0.37) * mm, "end": v(-22.99, -0.39) * mm});
            skLineSegment(sketch, "E1638", {"start": v(-22.99, -0.39) * mm, "end": v(-23.04, -0.4) * mm});
            skLineSegment(sketch, "E1639", {"start": v(-23.04, -0.4) * mm, "end": v(-23.1, -0.42) * mm});
            skLineSegment(sketch, "E1640", {"start": v(-23.1, -0.42) * mm, "end": v(-23.16, -0.44) * mm});
            skLineSegment(sketch, "E1641", {"start": v(-23.16, -0.44) * mm, "end": v(-23.22, -0.46) * mm});
            skLineSegment(sketch, "E1642", {"start": v(-23.22, -0.46) * mm, "end": v(-23.28, -0.48) * mm});
            skLineSegment(sketch, "E1643", {"start": v(-23.28, -0.48) * mm, "end": v(-23.34, -0.5) * mm});
            skLineSegment(sketch, "E1644", {"start": v(-23.34, -0.5) * mm, "end": v(-23.4, -0.53) * mm});
            skLineSegment(sketch, "E1645", {"start": v(-23.4, -0.53) * mm, "end": v(-23.47, -0.56) * mm});
            skLineSegment(sketch, "E1646", {"start": v(-23.47, -0.56) * mm, "end": v(-23.54, -0.58) * mm});
            skLineSegment(sketch, "E1647", {"start": v(-23.54, -0.58) * mm, "end": v(-23.6, -0.61) * mm});
            skLineSegment(sketch, "E1648", {"start": v(-23.6, -0.61) * mm, "end": v(-23.67, -0.64) * mm});
            skLineSegment(sketch, "E1649", {"start": v(-23.67, -0.64) * mm, "end": v(-23.74, -0.67) * mm});
            skLineSegment(sketch, "E1650", {"start": v(-23.74, -0.67) * mm, "end": v(-23.81, -0.7) * mm});
            skLineSegment(sketch, "E1651", {"start": v(-23.81, -0.7) * mm, "end": v(-23.89, -0.73) * mm});
            skLineSegment(sketch, "E1652", {"start": v(-23.89, -0.73) * mm, "end": v(-23.96, -0.77) * mm});
            skLineSegment(sketch, "E1653", {"start": v(-23.96, -0.77) * mm, "end": v(-24.04, -0.8) * mm});
            skLineSegment(sketch, "E1654", {"start": v(-24.04, -0.8) * mm, "end": v(-24.14, -0.86) * mm});
            skLineSegment(sketch, "E1655", {"start": v(-24.14, -0.86) * mm, "end": v(-24.12, -1.4) * mm});
            skLineSegment(sketch, "E1656", {"start": v(-24.12, -1.4) * mm, "end": v(-24, -1.45) * mm});
            skLineSegment(sketch, "E1657", {"start": v(-24, -1.45) * mm, "end": v(-23.93, -1.48) * mm});
            skLineSegment(sketch, "E1658", {"start": v(-23.93, -1.48) * mm, "end": v(-23.85, -1.5) * mm});
            skLineSegment(sketch, "E1659", {"start": v(-23.85, -1.5) * mm, "end": v(-23.77, -1.53) * mm});
            skLineSegment(sketch, "E1660", {"start": v(-23.77, -1.53) * mm, "end": v(-23.7, -1.56) * mm});
            skLineSegment(sketch, "E1661", {"start": v(-23.7, -1.56) * mm, "end": v(-23.63, -1.58) * mm});
            skLineSegment(sketch, "E1662", {"start": v(-23.63, -1.58) * mm, "end": v(-23.56, -1.6) * mm});
            skLineSegment(sketch, "E1663", {"start": v(-23.56, -1.6) * mm, "end": v(-23.49, -1.62) * mm});
            skLineSegment(sketch, "E1664", {"start": v(-23.49, -1.62) * mm, "end": v(-23.42, -1.64) * mm});
            skLineSegment(sketch, "E1665", {"start": v(-23.42, -1.64) * mm, "end": v(-23.35, -1.66) * mm});
            skLineSegment(sketch, "E1666", {"start": v(-23.35, -1.66) * mm, "end": v(-23.29, -1.68) * mm});
            skLineSegment(sketch, "E1667", {"start": v(-23.29, -1.68) * mm, "end": v(-23.22, -1.7) * mm});
            skLineSegment(sketch, "E1668", {"start": v(-23.22, -1.7) * mm, "end": v(-23.16, -1.71) * mm});
            skLineSegment(sketch, "E1669", {"start": v(-23.16, -1.71) * mm, "end": v(-23.1, -1.73) * mm});
            skLineSegment(sketch, "E1670", {"start": v(-23.1, -1.73) * mm, "end": v(-23.04, -1.74) * mm});
            skLineSegment(sketch, "E1671", {"start": v(-23.04, -1.74) * mm, "end": v(-22.98, -1.75) * mm});
            skLineSegment(sketch, "E1672", {"start": v(-22.98, -1.75) * mm, "end": v(-22.92, -1.77) * mm});
            skLineSegment(sketch, "E1673", {"start": v(-22.92, -1.77) * mm, "end": v(-22.87, -1.78) * mm});
            skLineSegment(sketch, "E1674", {"start": v(-22.87, -1.78) * mm, "end": v(-22.82, -1.79) * mm});
            skLineSegment(sketch, "E1675", {"start": v(-22.82, -1.79) * mm, "end": v(-22.76, -1.8) * mm});
            skLineSegment(sketch, "E1676", {"start": v(-22.76, -1.8) * mm, "end": v(-22.66, -1.82) * mm});
            skLineSegment(sketch, "E1677", {"start": v(-22.66, -1.82) * mm, "end": v(-22.57, -1.83) * mm});
            skLineSegment(sketch, "E1678", {"start": v(-22.57, -1.83) * mm, "end": v(-22.5, -1.84) * mm});
            skArc(sketch, "E1679", {"start": v(-22.5, -1.84) * mm, "mid": v(-22.22, -2.09) * mm, "end": v(-22.46, -2.39) * mm});
            skLineSegment(sketch, "E1680", {"start": v(-22.46, -2.39) * mm, "end": v(-22.52, -2.4) * mm});
            skLineSegment(sketch, "E1681", {"start": v(-22.52, -2.4) * mm, "end": v(-22.6, -2.44) * mm});
            skLineSegment(sketch, "E1682", {"start": v(-22.6, -2.44) * mm, "end": v(-22.7, -2.48) * mm});
            skLineSegment(sketch, "E1683", {"start": v(-22.7, -2.48) * mm, "end": v(-22.75, -2.5) * mm});
            skLineSegment(sketch, "E1684", {"start": v(-22.75, -2.5) * mm, "end": v(-22.8, -2.52) * mm});
            skLineSegment(sketch, "E1685", {"start": v(-22.8, -2.52) * mm, "end": v(-22.85, -2.54) * mm});
            skLineSegment(sketch, "E1686", {"start": v(-22.85, -2.54) * mm, "end": v(-22.9, -2.56) * mm});
            skLineSegment(sketch, "E1687", {"start": v(-22.9, -2.56) * mm, "end": v(-22.96, -2.58) * mm});
            skLineSegment(sketch, "E1688", {"start": v(-22.96, -2.58) * mm, "end": v(-23.02, -2.6) * mm});
            skLineSegment(sketch, "E1689", {"start": v(-23.02, -2.6) * mm, "end": v(-23.07, -2.63) * mm});
            skLineSegment(sketch, "E1690", {"start": v(-23.07, -2.63) * mm, "end": v(-23.13, -2.66) * mm});
            skLineSegment(sketch, "E1691", {"start": v(-23.13, -2.66) * mm, "end": v(-23.2, -2.7) * mm});
            skLineSegment(sketch, "E1692", {"start": v(-23.2, -2.7) * mm, "end": v(-23.25, -2.72) * mm});
            skLineSegment(sketch, "E1693", {"start": v(-23.25, -2.72) * mm, "end": v(-23.31, -2.75) * mm});
            skLineSegment(sketch, "E1694", {"start": v(-23.31, -2.75) * mm, "end": v(-23.38, -2.78) * mm});
            skLineSegment(sketch, "E1695", {"start": v(-23.38, -2.78) * mm, "end": v(-23.44, -2.82) * mm});
            skLineSegment(sketch, "E1696", {"start": v(-23.44, -2.82) * mm, "end": v(-23.5, -2.85) * mm});
            skLineSegment(sketch, "E1697", {"start": v(-23.5, -2.85) * mm, "end": v(-23.58, -2.89) * mm});
            skLineSegment(sketch, "E1698", {"start": v(-23.58, -2.89) * mm, "end": v(-23.64, -2.93) * mm});
            skLineSegment(sketch, "E1699", {"start": v(-23.64, -2.93) * mm, "end": v(-23.71, -2.97) * mm});
            skLineSegment(sketch, "E1700", {"start": v(-23.71, -2.97) * mm, "end": v(-23.78, -3) * mm});
            skLineSegment(sketch, "E1701", {"start": v(-23.78, -3) * mm, "end": v(-23.85, -3.05) * mm});
            skLineSegment(sketch, "E1702", {"start": v(-23.85, -3.05) * mm, "end": v(-23.96, -3.11) * mm});
            skLineSegment(sketch, "E1703", {"start": v(-23.96, -3.11) * mm, "end": v(-23.88, -3.66) * mm});
            skLineSegment(sketch, "E1704", {"start": v(-23.88, -3.66) * mm, "end": v(-23.76, -3.7) * mm});
            skLineSegment(sketch, "E1705", {"start": v(-23.76, -3.7) * mm, "end": v(-23.68, -3.71) * mm});
            skLineSegment(sketch, "E1706", {"start": v(-23.68, -3.71) * mm, "end": v(-23.6, -3.73) * mm});
            skLineSegment(sketch, "E1707", {"start": v(-23.6, -3.73) * mm, "end": v(-23.53, -3.75) * mm});
            skLineSegment(sketch, "E1708", {"start": v(-23.53, -3.75) * mm, "end": v(-23.45, -3.77) * mm});
            skLineSegment(sketch, "E1709", {"start": v(-23.45, -3.77) * mm, "end": v(-23.38, -3.78) * mm});
            skLineSegment(sketch, "E1710", {"start": v(-23.38, -3.78) * mm, "end": v(-23.3, -3.8) * mm});
            skLineSegment(sketch, "E1711", {"start": v(-23.3, -3.8) * mm, "end": v(-23.23, -3.81) * mm});
            skLineSegment(sketch, "E1712", {"start": v(-23.23, -3.81) * mm, "end": v(-23.16, -3.83) * mm});
            skLineSegment(sketch, "E1713", {"start": v(-23.16, -3.83) * mm, "end": v(-23.1, -3.84) * mm});
            skLineSegment(sketch, "E1714", {"start": v(-23.1, -3.84) * mm, "end": v(-23.03, -3.85) * mm});
            skLineSegment(sketch, "E1715", {"start": v(-23.03, -3.85) * mm, "end": v(-22.96, -3.86) * mm});
            skLineSegment(sketch, "E1716", {"start": v(-22.96, -3.86) * mm, "end": v(-22.9, -3.87) * mm});
            skLineSegment(sketch, "E1717", {"start": v(-22.9, -3.87) * mm, "end": v(-22.84, -3.88) * mm});
            skLineSegment(sketch, "E1718", {"start": v(-22.84, -3.88) * mm, "end": v(-22.77, -3.9) * mm});
            skLineSegment(sketch, "E1719", {"start": v(-22.77, -3.9) * mm, "end": v(-22.72, -3.9) * mm});
            skLineSegment(sketch, "E1720", {"start": v(-22.72, -3.9) * mm, "end": v(-22.66, -3.9) * mm});
            skLineSegment(sketch, "E1721", {"start": v(-22.66, -3.9) * mm, "end": v(-22.6, -3.91) * mm});
            skLineSegment(sketch, "E1722", {"start": v(-22.6, -3.91) * mm, "end": v(-22.55, -3.92) * mm});
            skLineSegment(sketch, "E1723", {"start": v(-22.55, -3.92) * mm, "end": v(-22.5, -3.92) * mm});
            skLineSegment(sketch, "E1724", {"start": v(-22.5, -3.92) * mm, "end": v(-22.4, -3.93) * mm});
            skLineSegment(sketch, "E1725", {"start": v(-22.4, -3.93) * mm, "end": v(-22.3, -3.94) * mm});
            skLineSegment(sketch, "E1726", {"start": v(-22.3, -3.94) * mm, "end": v(-22.24, -3.94) * mm});
            skArc(sketch, "E1727", {"start": v(-22.24, -3.94) * mm, "mid": v(-21.93, -4.16) * mm, "end": v(-22.13, -4.48) * mm});
            skLineSegment(sketch, "E1728", {"start": v(-22.13, -4.48) * mm, "end": v(-22.2, -4.5) * mm});
            skLineSegment(sketch, "E1729", {"start": v(-22.2, -4.5) * mm, "end": v(-22.28, -4.54) * mm});
            skLineSegment(sketch, "E1730", {"start": v(-22.28, -4.54) * mm, "end": v(-22.37, -4.59) * mm});
            skLineSegment(sketch, "E1731", {"start": v(-22.37, -4.59) * mm, "end": v(-22.42, -4.61) * mm});
            skLineSegment(sketch, "E1732", {"start": v(-22.42, -4.61) * mm, "end": v(-22.46, -4.64) * mm});
            skLineSegment(sketch, "E1733", {"start": v(-22.46, -4.64) * mm, "end": v(-22.51, -4.66) * mm});
            skLineSegment(sketch, "E1734", {"start": v(-22.51, -4.66) * mm, "end": v(-22.56, -4.7) * mm});
            skLineSegment(sketch, "E1735", {"start": v(-22.56, -4.7) * mm, "end": v(-22.62, -4.72) * mm});
            skLineSegment(sketch, "E1736", {"start": v(-22.62, -4.72) * mm, "end": v(-22.67, -4.75) * mm});
            skLineSegment(sketch, "E1737", {"start": v(-22.67, -4.75) * mm, "end": v(-22.72, -4.78) * mm});
            skLineSegment(sketch, "E1738", {"start": v(-22.72, -4.78) * mm, "end": v(-22.78, -4.82) * mm});
            skLineSegment(sketch, "E1739", {"start": v(-22.78, -4.82) * mm, "end": v(-22.84, -4.85) * mm});
            skLineSegment(sketch, "E1740", {"start": v(-22.84, -4.85) * mm, "end": v(-22.9, -4.89) * mm});
            skLineSegment(sketch, "E1741", {"start": v(-22.9, -4.89) * mm, "end": v(-22.95, -4.92) * mm});
            skLineSegment(sketch, "E1742", {"start": v(-22.95, -4.92) * mm, "end": v(-23.01, -4.96) * mm});
            skLineSegment(sketch, "E1743", {"start": v(-23.01, -4.96) * mm, "end": v(-23.08, -5) * mm});
            skLineSegment(sketch, "E1744", {"start": v(-23.08, -5) * mm, "end": v(-23.14, -5.04) * mm});
            skLineSegment(sketch, "E1745", {"start": v(-23.14, -5.04) * mm, "end": v(-23.2, -5.08) * mm});
            skLineSegment(sketch, "E1746", {"start": v(-23.2, -5.08) * mm, "end": v(-23.27, -5.13) * mm});
            skLineSegment(sketch, "E1747", {"start": v(-23.27, -5.13) * mm, "end": v(-23.33, -5.17) * mm});
            skLineSegment(sketch, "E1748", {"start": v(-23.33, -5.17) * mm, "end": v(-23.4, -5.22) * mm});
            skLineSegment(sketch, "E1749", {"start": v(-23.4, -5.22) * mm, "end": v(-23.46, -5.27) * mm});
            skLineSegment(sketch, "E1750", {"start": v(-23.46, -5.27) * mm, "end": v(-23.56, -5.34) * mm});
            skLineSegment(sketch, "E1751", {"start": v(-23.56, -5.34) * mm, "end": v(-23.43, -5.88) * mm});
            skLineSegment(sketch, "E1752", {"start": v(-23.43, -5.88) * mm, "end": v(-23.31, -5.9) * mm});
            skLineSegment(sketch, "E1753", {"start": v(-23.31, -5.9) * mm, "end": v(-23.23, -5.91) * mm});
            skLineSegment(sketch, "E1754", {"start": v(-23.23, -5.91) * mm, "end": v(-23.15, -5.92) * mm});
            skLineSegment(sketch, "E1755", {"start": v(-23.15, -5.92) * mm, "end": v(-23.07, -5.94) * mm});
            skLineSegment(sketch, "E1756", {"start": v(-23.07, -5.94) * mm, "end": v(-23, -5.95) * mm});
            skLineSegment(sketch, "E1757", {"start": v(-23, -5.95) * mm, "end": v(-22.92, -5.96) * mm});
            skLineSegment(sketch, "E1758", {"start": v(-22.92, -5.96) * mm, "end": v(-22.85, -5.96) * mm});
            skLineSegment(sketch, "E1759", {"start": v(-22.85, -5.96) * mm, "end": v(-22.77, -5.97) * mm});
            skLineSegment(sketch, "E1760", {"start": v(-22.77, -5.97) * mm, "end": v(-22.7, -5.98) * mm});
            skLineSegment(sketch, "E1761", {"start": v(-22.7, -5.98) * mm, "end": v(-22.63, -5.99) * mm});
            skLineSegment(sketch, "E1762", {"start": v(-22.63, -5.99) * mm, "end": v(-22.56, -6) * mm});
            skLineSegment(sketch, "E1763", {"start": v(-22.56, -6) * mm, "end": v(-22.5, -6) * mm});
            skLineSegment(sketch, "E1764", {"start": v(-22.5, -6) * mm, "end": v(-22.43, -6) * mm});
            skLineSegment(sketch, "E1765", {"start": v(-22.43, -6) * mm, "end": v(-22.37, -6) * mm});
            skLineSegment(sketch, "E1766", {"start": v(-22.37, -6) * mm, "end": v(-22.3, -6) * mm});
            skLineSegment(sketch, "E1767", {"start": v(-22.3, -6) * mm, "end": v(-22.25, -6) * mm});
            skLineSegment(sketch, "E1768", {"start": v(-22.25, -6) * mm, "end": v(-22.2, -6) * mm});
            skLineSegment(sketch, "E1769", {"start": v(-22.2, -6) * mm, "end": v(-22.14, -6.01) * mm});
            skLineSegment(sketch, "E1770", {"start": v(-22.14, -6.01) * mm, "end": v(-22.08, -6.01) * mm});
            skLineSegment(sketch, "E1771", {"start": v(-22.08, -6.01) * mm, "end": v(-22.03, -6.01) * mm});
            skLineSegment(sketch, "E1772", {"start": v(-22.03, -6.01) * mm, "end": v(-21.93, -6.01) * mm});
            skLineSegment(sketch, "E1773", {"start": v(-21.93, -6.01) * mm, "end": v(-21.83, -6) * mm});
            skLineSegment(sketch, "E1774", {"start": v(-21.83, -6) * mm, "end": v(-21.77, -6) * mm});
            skArc(sketch, "E1775", {"start": v(-21.77, -6) * mm, "mid": v(-21.44, -6.2) * mm, "end": v(-21.62, -6.53) * mm});
            skLineSegment(sketch, "E1776", {"start": v(-21.62, -6.53) * mm, "end": v(-21.67, -6.56) * mm});
            skLineSegment(sketch, "E1777", {"start": v(-21.67, -6.56) * mm, "end": v(-21.75, -6.61) * mm});
            skLineSegment(sketch, "E1778", {"start": v(-21.75, -6.61) * mm, "end": v(-21.84, -6.66) * mm});
            skLineSegment(sketch, "E1779", {"start": v(-21.84, -6.66) * mm, "end": v(-21.89, -6.7) * mm});
            skLineSegment(sketch, "E1780", {"start": v(-21.89, -6.7) * mm, "end": v(-21.93, -6.72) * mm});
            skLineSegment(sketch, "E1781", {"start": v(-21.93, -6.72) * mm, "end": v(-21.98, -6.75) * mm});
            skLineSegment(sketch, "E1782", {"start": v(-21.98, -6.75) * mm, "end": v(-22.03, -6.78) * mm});
            skLineSegment(sketch, "E1783", {"start": v(-22.03, -6.78) * mm, "end": v(-22.08, -6.82) * mm});
            skLineSegment(sketch, "E1784", {"start": v(-22.08, -6.82) * mm, "end": v(-22.13, -6.85) * mm});
            skLineSegment(sketch, "E1785", {"start": v(-22.13, -6.85) * mm, "end": v(-22.18, -6.89) * mm});
            skLineSegment(sketch, "E1786", {"start": v(-22.18, -6.89) * mm, "end": v(-22.23, -6.93) * mm});
            skLineSegment(sketch, "E1787", {"start": v(-22.23, -6.93) * mm, "end": v(-22.28, -6.97) * mm});
            skLineSegment(sketch, "E1788", {"start": v(-22.28, -6.97) * mm, "end": v(-22.34, -7) * mm});
            skLineSegment(sketch, "E1789", {"start": v(-22.34, -7) * mm, "end": v(-22.4, -7.05) * mm});
            skLineSegment(sketch, "E1790", {"start": v(-22.4, -7.05) * mm, "end": v(-22.45, -7.1) * mm});
            skLineSegment(sketch, "E1791", {"start": v(-22.45, -7.1) * mm, "end": v(-22.5, -7.14) * mm});
            skLineSegment(sketch, "E1792", {"start": v(-22.5, -7.14) * mm, "end": v(-22.56, -7.19) * mm});
            skLineSegment(sketch, "E1793", {"start": v(-22.56, -7.19) * mm, "end": v(-22.62, -7.23) * mm});
            skLineSegment(sketch, "E1794", {"start": v(-22.62, -7.23) * mm, "end": v(-22.68, -7.28) * mm});
            skLineSegment(sketch, "E1795", {"start": v(-22.68, -7.28) * mm, "end": v(-22.74, -7.34) * mm});
            skLineSegment(sketch, "E1796", {"start": v(-22.74, -7.34) * mm, "end": v(-22.8, -7.39) * mm});
            skLineSegment(sketch, "E1797", {"start": v(-22.8, -7.39) * mm, "end": v(-22.87, -7.44) * mm});
            skLineSegment(sketch, "E1798", {"start": v(-22.87, -7.44) * mm, "end": v(-22.96, -7.52) * mm});
            skLineSegment(sketch, "E1799", {"start": v(-22.96, -7.52) * mm, "end": v(-22.78, -8.05) * mm});
            skLineSegment(sketch, "E1800", {"start": v(-22.78, -8.05) * mm, "end": v(-22.66, -8.06) * mm});
            skLineSegment(sketch, "E1801", {"start": v(-22.66, -8.06) * mm, "end": v(-22.58, -8.06) * mm});
            skLineSegment(sketch, "E1802", {"start": v(-22.58, -8.06) * mm, "end": v(-22.5, -8.07) * mm});
            skLineSegment(sketch, "E1803", {"start": v(-22.5, -8.07) * mm, "end": v(-22.42, -8.07) * mm});
            skLineSegment(sketch, "E1804", {"start": v(-22.42, -8.07) * mm, "end": v(-22.34, -8.07) * mm});
            skLineSegment(sketch, "E1805", {"start": v(-22.34, -8.07) * mm, "end": v(-22.26, -8.07) * mm});
            skLineSegment(sketch, "E1806", {"start": v(-22.26, -8.07) * mm, "end": v(-22.19, -8.08) * mm});
            skLineSegment(sketch, "E1807", {"start": v(-22.19, -8.08) * mm, "end": v(-22.11, -8.08) * mm});
            skLineSegment(sketch, "E1808", {"start": v(-22.11, -8.08) * mm, "end": v(-22.04, -8.08) * mm});
            skLineSegment(sketch, "E1809", {"start": v(-22.04, -8.08) * mm, "end": v(-21.97, -8.08) * mm});
            skLineSegment(sketch, "E1810", {"start": v(-21.97, -8.08) * mm, "end": v(-21.9, -8.08) * mm});
            skLineSegment(sketch, "E1811", {"start": v(-21.9, -8.08) * mm, "end": v(-21.84, -8.08) * mm});
            skLineSegment(sketch, "E1812", {"start": v(-21.84, -8.08) * mm, "end": v(-21.77, -8.07) * mm});
            skLineSegment(sketch, "E1813", {"start": v(-21.77, -8.07) * mm, "end": v(-21.71, -8.07) * mm});
            skLineSegment(sketch, "E1814", {"start": v(-21.71, -8.07) * mm, "end": v(-21.65, -8.07) * mm});
            skLineSegment(sketch, "E1815", {"start": v(-21.65, -8.07) * mm, "end": v(-21.6, -8.06) * mm});
            skLineSegment(sketch, "E1816", {"start": v(-21.6, -8.06) * mm, "end": v(-21.53, -8.06) * mm});
            skLineSegment(sketch, "E1817", {"start": v(-21.53, -8.06) * mm, "end": v(-21.48, -8.06) * mm});
            skLineSegment(sketch, "E1818", {"start": v(-21.48, -8.06) * mm, "end": v(-21.42, -8.05) * mm});
            skLineSegment(sketch, "E1819", {"start": v(-21.42, -8.05) * mm, "end": v(-21.37, -8.05) * mm});
            skLineSegment(sketch, "E1820", {"start": v(-21.37, -8.05) * mm, "end": v(-21.27, -8.04) * mm});
            skLineSegment(sketch, "E1821", {"start": v(-21.27, -8.04) * mm, "end": v(-21.18, -8.03) * mm});
            skLineSegment(sketch, "E1822", {"start": v(-21.18, -8.03) * mm, "end": v(-21.11, -8.02) * mm});
            skArc(sketch, "E1823", {"start": v(-21.11, -8.02) * mm, "mid": v(-20.77, -8.17) * mm, "end": v(-20.91, -8.52) * mm});
            skLineSegment(sketch, "E1824", {"start": v(-20.91, -8.52) * mm, "end": v(-20.96, -8.56) * mm});
            skLineSegment(sketch, "E1825", {"start": v(-20.96, -8.56) * mm, "end": v(-21.04, -8.62) * mm});
            skLineSegment(sketch, "E1826", {"start": v(-21.04, -8.62) * mm, "end": v(-21.12, -8.68) * mm});
            skLineSegment(sketch, "E1827", {"start": v(-21.12, -8.68) * mm, "end": v(-21.16, -8.71) * mm});
            skLineSegment(sketch, "E1828", {"start": v(-21.16, -8.71) * mm, "end": v(-21.2, -8.74) * mm});
            skLineSegment(sketch, "E1829", {"start": v(-21.2, -8.74) * mm, "end": v(-21.25, -8.78) * mm});
            skLineSegment(sketch, "E1830", {"start": v(-21.25, -8.78) * mm, "end": v(-21.3, -8.82) * mm});
            skLineSegment(sketch, "E1831", {"start": v(-21.3, -8.82) * mm, "end": v(-21.34, -8.85) * mm});
            skLineSegment(sketch, "E1832", {"start": v(-21.34, -8.85) * mm, "end": v(-21.39, -8.9) * mm});
            skLineSegment(sketch, "E1833", {"start": v(-21.39, -8.9) * mm, "end": v(-21.43, -8.94) * mm});
            skLineSegment(sketch, "E1834", {"start": v(-21.43, -8.94) * mm, "end": v(-21.48, -8.98) * mm});
            skLineSegment(sketch, "E1835", {"start": v(-21.48, -8.98) * mm, "end": v(-21.53, -9.02) * mm});
            skLineSegment(sketch, "E1836", {"start": v(-21.53, -9.02) * mm, "end": v(-21.58, -9.07) * mm});
            skLineSegment(sketch, "E1837", {"start": v(-21.58, -9.07) * mm, "end": v(-21.63, -9.11) * mm});
            skLineSegment(sketch, "E1838", {"start": v(-21.63, -9.11) * mm, "end": v(-21.69, -9.16) * mm});
            skLineSegment(sketch, "E1839", {"start": v(-21.69, -9.16) * mm, "end": v(-21.74, -9.21) * mm});
            skLineSegment(sketch, "E1840", {"start": v(-21.74, -9.21) * mm, "end": v(-21.8, -9.27) * mm});
            skLineSegment(sketch, "E1841", {"start": v(-21.8, -9.27) * mm, "end": v(-21.85, -9.32) * mm});
            skLineSegment(sketch, "E1842", {"start": v(-21.85, -9.32) * mm, "end": v(-21.9, -9.38) * mm});
            skLineSegment(sketch, "E1843", {"start": v(-21.9, -9.38) * mm, "end": v(-21.96, -9.43) * mm});
            skLineSegment(sketch, "E1844", {"start": v(-21.96, -9.43) * mm, "end": v(-22.01, -9.5) * mm});
            skLineSegment(sketch, "E1845", {"start": v(-22.01, -9.5) * mm, "end": v(-22.07, -9.55) * mm});
            skLineSegment(sketch, "E1846", {"start": v(-22.07, -9.55) * mm, "end": v(-22.15, -9.64) * mm});
            skLineSegment(sketch, "E1847", {"start": v(-22.15, -9.64) * mm, "end": v(-21.92, -10.14) * mm});
            skLineSegment(sketch, "E1848", {"start": v(-21.92, -10.14) * mm, "end": v(-21.8, -10.14) * mm});
            skLineSegment(sketch, "E1849", {"start": v(-21.8, -10.14) * mm, "end": v(-21.72, -10.14) * mm});
            skLineSegment(sketch, "E1850", {"start": v(-21.72, -10.14) * mm, "end": v(-21.64, -10.14) * mm});
            skLineSegment(sketch, "E1851", {"start": v(-21.64, -10.14) * mm, "end": v(-21.56, -10.13) * mm});
            skLineSegment(sketch, "E1852", {"start": v(-21.56, -10.13) * mm, "end": v(-21.48, -10.13) * mm});
            skLineSegment(sketch, "E1853", {"start": v(-21.48, -10.13) * mm, "end": v(-21.4, -10.12) * mm});
            skLineSegment(sketch, "E1854", {"start": v(-21.4, -10.12) * mm, "end": v(-21.33, -10.12) * mm});
            skLineSegment(sketch, "E1855", {"start": v(-21.33, -10.12) * mm, "end": v(-21.26, -10.11) * mm});
            skLineSegment(sketch, "E1856", {"start": v(-21.26, -10.11) * mm, "end": v(-21.19, -10.1) * mm});
            skLineSegment(sketch, "E1857", {"start": v(-21.19, -10.1) * mm, "end": v(-21.12, -10.1) * mm});
            skLineSegment(sketch, "E1858", {"start": v(-21.12, -10.1) * mm, "end": v(-21.05, -10.1) * mm});
            skLineSegment(sketch, "E1859", {"start": v(-21.05, -10.1) * mm, "end": v(-20.99, -10.08) * mm});
            skLineSegment(sketch, "E1860", {"start": v(-20.99, -10.08) * mm, "end": v(-20.92, -10.08) * mm});
            skLineSegment(sketch, "E1861", {"start": v(-20.92, -10.08) * mm, "end": v(-20.86, -10.07) * mm});
            skLineSegment(sketch, "E1862", {"start": v(-20.86, -10.07) * mm, "end": v(-20.8, -10.06) * mm});
            skLineSegment(sketch, "E1863", {"start": v(-20.8, -10.06) * mm, "end": v(-20.74, -10.05) * mm});
            skLineSegment(sketch, "E1864", {"start": v(-20.74, -10.05) * mm, "end": v(-20.68, -10.04) * mm});
            skLineSegment(sketch, "E1865", {"start": v(-20.68, -10.04) * mm, "end": v(-20.63, -10.03) * mm});
            skLineSegment(sketch, "E1866", {"start": v(-20.63, -10.03) * mm, "end": v(-20.57, -10.02) * mm});
            skLineSegment(sketch, "E1867", {"start": v(-20.57, -10.02) * mm, "end": v(-20.52, -10.01) * mm});
            skLineSegment(sketch, "E1868", {"start": v(-20.52, -10.01) * mm, "end": v(-20.42, -10) * mm});
            skLineSegment(sketch, "E1869", {"start": v(-20.42, -10) * mm, "end": v(-20.33, -9.97) * mm});
            skLineSegment(sketch, "E1870", {"start": v(-20.33, -9.97) * mm, "end": v(-20.27, -9.96) * mm});
            skArc(sketch, "E1871", {"start": v(-20.27, -9.96) * mm, "mid": v(-19.9, -10.08) * mm, "end": v(-20.02, -10.44) * mm});
            skLineSegment(sketch, "E1872", {"start": v(-20.02, -10.44) * mm, "end": v(-20.07, -10.49) * mm});
            skLineSegment(sketch, "E1873", {"start": v(-20.07, -10.49) * mm, "end": v(-20.14, -10.55) * mm});
            skLineSegment(sketch, "E1874", {"start": v(-20.14, -10.55) * mm, "end": v(-20.22, -10.62) * mm});
            skLineSegment(sketch, "E1875", {"start": v(-20.22, -10.62) * mm, "end": v(-20.25, -10.65) * mm});
            skLineSegment(sketch, "E1876", {"start": v(-20.25, -10.65) * mm, "end": v(-20.3, -10.7) * mm});
            skLineSegment(sketch, "E1877", {"start": v(-20.3, -10.7) * mm, "end": v(-20.33, -10.73) * mm});
            skLineSegment(sketch, "E1878", {"start": v(-20.33, -10.73) * mm, "end": v(-20.37, -10.77) * mm});
            skLineSegment(sketch, "E1879", {"start": v(-20.37, -10.77) * mm, "end": v(-20.42, -10.81) * mm});
            skLineSegment(sketch, "E1880", {"start": v(-20.42, -10.81) * mm, "end": v(-20.46, -10.86) * mm});
            skLineSegment(sketch, "E1881", {"start": v(-20.46, -10.86) * mm, "end": v(-20.5, -10.9) * mm});
            skLineSegment(sketch, "E1882", {"start": v(-20.5, -10.9) * mm, "end": v(-20.55, -10.95) * mm});
            skLineSegment(sketch, "E1883", {"start": v(-20.55, -10.95) * mm, "end": v(-20.6, -11) * mm});
            skLineSegment(sketch, "E1884", {"start": v(-20.6, -11) * mm, "end": v(-20.64, -11.05) * mm});
            skLineSegment(sketch, "E1885", {"start": v(-20.64, -11.05) * mm, "end": v(-20.69, -11.1) * mm});
            skLineSegment(sketch, "E1886", {"start": v(-20.69, -11.1) * mm, "end": v(-20.73, -11.15) * mm});
            skLineSegment(sketch, "E1887", {"start": v(-20.73, -11.15) * mm, "end": v(-20.78, -11.2) * mm});
            skLineSegment(sketch, "E1888", {"start": v(-20.78, -11.2) * mm, "end": v(-20.83, -11.27) * mm});
            skLineSegment(sketch, "E1889", {"start": v(-20.83, -11.27) * mm, "end": v(-20.88, -11.32) * mm});
            skLineSegment(sketch, "E1890", {"start": v(-20.88, -11.32) * mm, "end": v(-20.93, -11.38) * mm});
            skLineSegment(sketch, "E1891", {"start": v(-20.93, -11.38) * mm, "end": v(-20.98, -11.45) * mm});
            skLineSegment(sketch, "E1892", {"start": v(-20.98, -11.45) * mm, "end": v(-21.03, -11.51) * mm});
            skLineSegment(sketch, "E1893", {"start": v(-21.03, -11.51) * mm, "end": v(-21.08, -11.58) * mm});
            skLineSegment(sketch, "E1894", {"start": v(-21.08, -11.58) * mm, "end": v(-21.15, -11.67) * mm});
            skLineSegment(sketch, "E1895", {"start": v(-21.15, -11.67) * mm, "end": v(-20.88, -12.15) * mm});
            skLineSegment(sketch, "E1896", {"start": v(-20.88, -12.15) * mm, "end": v(-20.76, -12.14) * mm});
            skLineSegment(sketch, "E1897", {"start": v(-20.76, -12.14) * mm, "end": v(-20.68, -12.13) * mm});
            skLineSegment(sketch, "E1898", {"start": v(-20.68, -12.13) * mm, "end": v(-20.6, -12.12) * mm});
            skLineSegment(sketch, "E1899", {"start": v(-20.6, -12.12) * mm, "end": v(-20.52, -12.1) * mm});
            skLineSegment(sketch, "E1900", {"start": v(-20.52, -12.1) * mm, "end": v(-20.44, -12.1) * mm});
            skLineSegment(sketch, "E1901", {"start": v(-20.44, -12.1) * mm, "end": v(-20.37, -12.08) * mm});
            skLineSegment(sketch, "E1902", {"start": v(-20.37, -12.08) * mm, "end": v(-20.3, -12.07) * mm});
            skLineSegment(sketch, "E1903", {"start": v(-20.3, -12.07) * mm, "end": v(-20.22, -12.06) * mm});
            skLineSegment(sketch, "E1904", {"start": v(-20.22, -12.06) * mm, "end": v(-20.15, -12.04) * mm});
            skLineSegment(sketch, "E1905", {"start": v(-20.15, -12.04) * mm, "end": v(-20.08, -12.03) * mm});
            skLineSegment(sketch, "E1906", {"start": v(-20.08, -12.03) * mm, "end": v(-20.01, -12.02) * mm});
            skLineSegment(sketch, "E1907", {"start": v(-20.01, -12.02) * mm, "end": v(-19.95, -12) * mm});
            skLineSegment(sketch, "E1908", {"start": v(-19.95, -12) * mm, "end": v(-19.89, -12) * mm});
            skLineSegment(sketch, "E1909", {"start": v(-19.89, -12) * mm, "end": v(-19.83, -11.98) * mm});
            skLineSegment(sketch, "E1910", {"start": v(-19.83, -11.98) * mm, "end": v(-19.77, -11.96) * mm});
            skLineSegment(sketch, "E1911", {"start": v(-19.77, -11.96) * mm, "end": v(-19.7, -11.95) * mm});
            skLineSegment(sketch, "E1912", {"start": v(-19.7, -11.95) * mm, "end": v(-19.65, -11.93) * mm});
            skLineSegment(sketch, "E1913", {"start": v(-19.65, -11.93) * mm, "end": v(-19.6, -11.92) * mm});
            skLineSegment(sketch, "E1914", {"start": v(-19.6, -11.92) * mm, "end": v(-19.55, -11.9) * mm});
            skLineSegment(sketch, "E1915", {"start": v(-19.55, -11.9) * mm, "end": v(-19.5, -11.89) * mm});
            skLineSegment(sketch, "E1916", {"start": v(-19.5, -11.89) * mm, "end": v(-19.4, -11.86) * mm});
            skLineSegment(sketch, "E1917", {"start": v(-19.4, -11.86) * mm, "end": v(-19.3, -11.83) * mm});
            skLineSegment(sketch, "E1918", {"start": v(-19.3, -11.83) * mm, "end": v(-19.25, -11.81) * mm});
            skArc(sketch, "E1919", {"start": v(-19.25, -11.81) * mm, "mid": v(-18.88, -11.9) * mm, "end": v(-18.95, -12.27) * mm});
            skLineSegment(sketch, "E1920", {"start": v(-18.95, -12.27) * mm, "end": v(-19, -12.32) * mm});
            skLineSegment(sketch, "E1921", {"start": v(-19, -12.32) * mm, "end": v(-19.06, -12.39) * mm});
            skLineSegment(sketch, "E1922", {"start": v(-19.06, -12.39) * mm, "end": v(-19.13, -12.46) * mm});
            skLineSegment(sketch, "E1923", {"start": v(-19.13, -12.46) * mm, "end": v(-19.17, -12.5) * mm});
            skLineSegment(sketch, "E1924", {"start": v(-19.17, -12.5) * mm, "end": v(-19.2, -12.54) * mm});
            skLineSegment(sketch, "E1925", {"start": v(-19.2, -12.54) * mm, "end": v(-19.24, -12.59) * mm});
            skLineSegment(sketch, "E1926", {"start": v(-19.24, -12.59) * mm, "end": v(-19.28, -12.63) * mm});
            skLineSegment(sketch, "E1927", {"start": v(-19.28, -12.63) * mm, "end": v(-19.31, -12.68) * mm});
            skLineSegment(sketch, "E1928", {"start": v(-19.31, -12.68) * mm, "end": v(-19.35, -12.72) * mm});
            skLineSegment(sketch, "E1929", {"start": v(-19.35, -12.72) * mm, "end": v(-19.4, -12.77) * mm});
            skLineSegment(sketch, "E1930", {"start": v(-19.4, -12.77) * mm, "end": v(-19.43, -12.82) * mm});
            skLineSegment(sketch, "E1931", {"start": v(-19.43, -12.82) * mm, "end": v(-19.47, -12.88) * mm});
            skLineSegment(sketch, "E1932", {"start": v(-19.47, -12.88) * mm, "end": v(-19.51, -12.93) * mm});
            skLineSegment(sketch, "E1933", {"start": v(-19.51, -12.93) * mm, "end": v(-19.56, -12.99) * mm});
            skLineSegment(sketch, "E1934", {"start": v(-19.56, -12.99) * mm, "end": v(-19.6, -13.05) * mm});
            skLineSegment(sketch, "E1935", {"start": v(-19.6, -13.05) * mm, "end": v(-19.64, -13.1) * mm});
            skLineSegment(sketch, "E1936", {"start": v(-19.64, -13.1) * mm, "end": v(-19.68, -13.17) * mm});
            skLineSegment(sketch, "E1937", {"start": v(-19.68, -13.17) * mm, "end": v(-19.73, -13.23) * mm});
            skLineSegment(sketch, "E1938", {"start": v(-19.73, -13.23) * mm, "end": v(-19.77, -13.3) * mm});
            skLineSegment(sketch, "E1939", {"start": v(-19.77, -13.3) * mm, "end": v(-19.81, -13.36) * mm});
            skLineSegment(sketch, "E1940", {"start": v(-19.81, -13.36) * mm, "end": v(-19.86, -13.43) * mm});
            skLineSegment(sketch, "E1941", {"start": v(-19.86, -13.43) * mm, "end": v(-19.9, -13.5) * mm});
            skLineSegment(sketch, "E1942", {"start": v(-19.9, -13.5) * mm, "end": v(-19.96, -13.6) * mm});
            skLineSegment(sketch, "E1943", {"start": v(-19.96, -13.6) * mm, "end": v(-19.65, -14.05) * mm});
            skLineSegment(sketch, "E1944", {"start": v(-19.65, -14.05) * mm, "end": v(-19.53, -14.03) * mm});
            skLineSegment(sketch, "E1945", {"start": v(-19.53, -14.03) * mm, "end": v(-19.45, -14.01) * mm});
            skLineSegment(sketch, "E1946", {"start": v(-19.45, -14.01) * mm, "end": v(-19.37, -14) * mm});
            skLineSegment(sketch, "E1947", {"start": v(-19.37, -14) * mm, "end": v(-19.3, -13.97) * mm});
            skLineSegment(sketch, "E1948", {"start": v(-19.3, -13.97) * mm, "end": v(-19.22, -13.96) * mm});
            skLineSegment(sketch, "E1949", {"start": v(-19.22, -13.96) * mm, "end": v(-19.14, -13.94) * mm});
            skLineSegment(sketch, "E1950", {"start": v(-19.14, -13.94) * mm, "end": v(-19.07, -13.92) * mm});
            skLineSegment(sketch, "E1951", {"start": v(-19.07, -13.92) * mm, "end": v(-19, -13.9) * mm});
            skLineSegment(sketch, "E1952", {"start": v(-19, -13.9) * mm, "end": v(-18.93, -13.88) * mm});
            skLineSegment(sketch, "E1953", {"start": v(-18.93, -13.88) * mm, "end": v(-18.87, -13.86) * mm});
            skLineSegment(sketch, "E1954", {"start": v(-18.87, -13.86) * mm, "end": v(-18.8, -13.84) * mm});
            skLineSegment(sketch, "E1955", {"start": v(-18.8, -13.84) * mm, "end": v(-18.74, -13.82) * mm});
            skLineSegment(sketch, "E1956", {"start": v(-18.74, -13.82) * mm, "end": v(-18.68, -13.8) * mm});
            skLineSegment(sketch, "E1957", {"start": v(-18.68, -13.8) * mm, "end": v(-18.62, -13.78) * mm});
            skLineSegment(sketch, "E1958", {"start": v(-18.62, -13.78) * mm, "end": v(-18.56, -13.76) * mm});
            skLineSegment(sketch, "E1959", {"start": v(-18.56, -13.76) * mm, "end": v(-18.5, -13.74) * mm});
            skLineSegment(sketch, "E1960", {"start": v(-18.5, -13.74) * mm, "end": v(-18.45, -13.72) * mm});
            skLineSegment(sketch, "E1961", {"start": v(-18.45, -13.72) * mm, "end": v(-18.4, -13.7) * mm});
            skLineSegment(sketch, "E1962", {"start": v(-18.4, -13.7) * mm, "end": v(-18.34, -13.68) * mm});
            skLineSegment(sketch, "E1963", {"start": v(-18.34, -13.68) * mm, "end": v(-18.3, -13.66) * mm});
            skLineSegment(sketch, "E1964", {"start": v(-18.3, -13.66) * mm, "end": v(-18.2, -13.62) * mm});
            skLineSegment(sketch, "E1965", {"start": v(-18.2, -13.62) * mm, "end": v(-18.12, -13.59) * mm});
            skLineSegment(sketch, "E1966", {"start": v(-18.12, -13.59) * mm, "end": v(-18.06, -13.56) * mm});
            skArc(sketch, "E1967", {"start": v(-18.06, -13.56) * mm, "mid": v(-17.68, -13.62) * mm, "end": v(-17.72, -14) * mm});
            skLineSegment(sketch, "E1968", {"start": v(-17.72, -14) * mm, "end": v(-17.76, -14.04) * mm});
            skLineSegment(sketch, "E1969", {"start": v(-17.76, -14.04) * mm, "end": v(-17.82, -14.12) * mm});
            skLineSegment(sketch, "E1970", {"start": v(-17.82, -14.12) * mm, "end": v(-17.88, -14.2) * mm});
            skLineSegment(sketch, "E1971", {"start": v(-17.88, -14.2) * mm, "end": v(-17.91, -14.24) * mm});
            skLineSegment(sketch, "E1972", {"start": v(-17.91, -14.24) * mm, "end": v(-17.94, -14.29) * mm});
            skLineSegment(sketch, "E1973", {"start": v(-17.94, -14.29) * mm, "end": v(-17.98, -14.33) * mm});
            skLineSegment(sketch, "E1974", {"start": v(-17.98, -14.33) * mm, "end": v(-18, -14.38) * mm});
            skLineSegment(sketch, "E1975", {"start": v(-18, -14.38) * mm, "end": v(-18.04, -14.43) * mm});
            skLineSegment(sketch, "E1976", {"start": v(-18.04, -14.43) * mm, "end": v(-18.08, -14.48) * mm});
            skLineSegment(sketch, "E1977", {"start": v(-18.08, -14.48) * mm, "end": v(-18.11, -14.53) * mm});
            skLineSegment(sketch, "E1978", {"start": v(-18.11, -14.53) * mm, "end": v(-18.15, -14.59) * mm});
            skLineSegment(sketch, "E1979", {"start": v(-18.15, -14.59) * mm, "end": v(-18.18, -14.64) * mm});
            skLineSegment(sketch, "E1980", {"start": v(-18.18, -14.64) * mm, "end": v(-18.22, -14.7) * mm});
            skLineSegment(sketch, "E1981", {"start": v(-18.22, -14.7) * mm, "end": v(-18.25, -14.76) * mm});
            skLineSegment(sketch, "E1982", {"start": v(-18.25, -14.76) * mm, "end": v(-18.29, -14.82) * mm});
            skLineSegment(sketch, "E1983", {"start": v(-18.29, -14.82) * mm, "end": v(-18.33, -14.89) * mm});
            skLineSegment(sketch, "E1984", {"start": v(-18.33, -14.89) * mm, "end": v(-18.36, -14.95) * mm});
            skLineSegment(sketch, "E1985", {"start": v(-18.36, -14.95) * mm, "end": v(-18.4, -15.02) * mm});
            skLineSegment(sketch, "E1986", {"start": v(-18.4, -15.02) * mm, "end": v(-18.44, -15.09) * mm});
            skLineSegment(sketch, "E1987", {"start": v(-18.44, -15.09) * mm, "end": v(-18.48, -15.16) * mm});
            skLineSegment(sketch, "E1988", {"start": v(-18.48, -15.16) * mm, "end": v(-18.51, -15.23) * mm});
            skLineSegment(sketch, "E1989", {"start": v(-18.51, -15.23) * mm, "end": v(-18.55, -15.3) * mm});
            skLineSegment(sketch, "E1990", {"start": v(-18.55, -15.3) * mm, "end": v(-18.6, -15.4) * mm});
            skLineSegment(sketch, "E1991", {"start": v(-18.6, -15.4) * mm, "end": v(-18.25, -15.83) * mm});
            skLineSegment(sketch, "E1992", {"start": v(-18.25, -15.83) * mm, "end": v(-18.13, -15.8) * mm});
            skLineSegment(sketch, "E1993", {"start": v(-18.13, -15.8) * mm, "end": v(-18.05, -15.77) * mm});
            skLineSegment(sketch, "E1994", {"start": v(-18.05, -15.77) * mm, "end": v(-17.98, -15.74) * mm});
            skLineSegment(sketch, "E1995", {"start": v(-17.98, -15.74) * mm, "end": v(-17.9, -15.72) * mm});
            skLineSegment(sketch, "E1996", {"start": v(-17.9, -15.72) * mm, "end": v(-17.83, -15.7) * mm});
            skLineSegment(sketch, "E1997", {"start": v(-17.83, -15.7) * mm, "end": v(-17.76, -15.67) * mm});
            skLineSegment(sketch, "E1998", {"start": v(-17.76, -15.67) * mm, "end": v(-17.69, -15.64) * mm});
            skLineSegment(sketch, "E1999", {"start": v(-17.69, -15.64) * mm, "end": v(-17.62, -15.62) * mm});
            skLineSegment(sketch, "E2000", {"start": v(-17.62, -15.62) * mm, "end": v(-17.55, -15.59) * mm});
            skLineSegment(sketch, "E2001", {"start": v(-17.55, -15.59) * mm, "end": v(-17.49, -15.56) * mm});
            skLineSegment(sketch, "E2002", {"start": v(-17.49, -15.56) * mm, "end": v(-17.42, -15.54) * mm});
            skLineSegment(sketch, "E2003", {"start": v(-17.42, -15.54) * mm, "end": v(-17.36, -15.51) * mm});
            skLineSegment(sketch, "E2004", {"start": v(-17.36, -15.51) * mm, "end": v(-17.3, -15.49) * mm});
            skLineSegment(sketch, "E2005", {"start": v(-17.3, -15.49) * mm, "end": v(-17.24, -15.46) * mm});
            skLineSegment(sketch, "E2006", {"start": v(-17.24, -15.46) * mm, "end": v(-17.19, -15.44) * mm});
            skLineSegment(sketch, "E2007", {"start": v(-17.19, -15.44) * mm, "end": v(-17.13, -15.41) * mm});
            skLineSegment(sketch, "E2008", {"start": v(-17.13, -15.41) * mm, "end": v(-17.08, -15.39) * mm});
            skLineSegment(sketch, "E2009", {"start": v(-17.08, -15.39) * mm, "end": v(-17.03, -15.36) * mm});
            skLineSegment(sketch, "E2010", {"start": v(-17.03, -15.36) * mm, "end": v(-16.98, -15.34) * mm});
            skLineSegment(sketch, "E2011", {"start": v(-16.98, -15.34) * mm, "end": v(-16.94, -15.31) * mm});
            skLineSegment(sketch, "E2012", {"start": v(-16.94, -15.31) * mm, "end": v(-16.85, -15.27) * mm});
            skLineSegment(sketch, "E2013", {"start": v(-16.85, -15.27) * mm, "end": v(-16.76, -15.22) * mm});
            skLineSegment(sketch, "E2014", {"start": v(-16.76, -15.22) * mm, "end": v(-16.7, -15.2) * mm});
            skArc(sketch, "E2015", {"start": v(-16.7, -15.2) * mm, "mid": v(-16.33, -15.21) * mm, "end": v(-16.33, -15.6) * mm});
            skLineSegment(sketch, "E2016", {"start": v(-16.33, -15.6) * mm, "end": v(-16.37, -15.65) * mm});
            skLineSegment(sketch, "E2017", {"start": v(-16.37, -15.65) * mm, "end": v(-16.42, -15.72) * mm});
            skLineSegment(sketch, "E2018", {"start": v(-16.42, -15.72) * mm, "end": v(-16.47, -15.81) * mm});
            skLineSegment(sketch, "E2019", {"start": v(-16.47, -15.81) * mm, "end": v(-16.5, -15.86) * mm});
            skLineSegment(sketch, "E2020", {"start": v(-16.5, -15.86) * mm, "end": v(-16.53, -15.9) * mm});
            skLineSegment(sketch, "E2021", {"start": v(-16.53, -15.9) * mm, "end": v(-16.56, -15.95) * mm});
            skLineSegment(sketch, "E2022", {"start": v(-16.56, -15.95) * mm, "end": v(-16.58, -16) * mm});
            skLineSegment(sketch, "E2023", {"start": v(-16.58, -16) * mm, "end": v(-16.61, -16.05) * mm});
            skLineSegment(sketch, "E2024", {"start": v(-16.61, -16.05) * mm, "end": v(-16.64, -16.1) * mm});
            skLineSegment(sketch, "E2025", {"start": v(-16.64, -16.1) * mm, "end": v(-16.67, -16.16) * mm});
            skLineSegment(sketch, "E2026", {"start": v(-16.67, -16.16) * mm, "end": v(-16.7, -16.22) * mm});
            skLineSegment(sketch, "E2027", {"start": v(-16.7, -16.22) * mm, "end": v(-16.73, -16.28) * mm});
            skLineSegment(sketch, "E2028", {"start": v(-16.73, -16.28) * mm, "end": v(-16.76, -16.34) * mm});
            skLineSegment(sketch, "E2029", {"start": v(-16.76, -16.34) * mm, "end": v(-16.8, -16.4) * mm});
            skLineSegment(sketch, "E2030", {"start": v(-16.8, -16.4) * mm, "end": v(-16.82, -16.47) * mm});
            skLineSegment(sketch, "E2031", {"start": v(-16.82, -16.47) * mm, "end": v(-16.85, -16.54) * mm});
            skLineSegment(sketch, "E2032", {"start": v(-16.85, -16.54) * mm, "end": v(-16.88, -16.6) * mm});
            skLineSegment(sketch, "E2033", {"start": v(-16.88, -16.6) * mm, "end": v(-16.91, -16.67) * mm});
            skLineSegment(sketch, "E2034", {"start": v(-16.91, -16.67) * mm, "end": v(-16.94, -16.74) * mm});
            skLineSegment(sketch, "E2035", {"start": v(-16.94, -16.74) * mm, "end": v(-16.97, -16.82) * mm});
            skLineSegment(sketch, "E2036", {"start": v(-16.97, -16.82) * mm, "end": v(-17, -16.9) * mm});
            skLineSegment(sketch, "E2037", {"start": v(-17, -16.9) * mm, "end": v(-17.04, -16.97) * mm});
            skLineSegment(sketch, "E2038", {"start": v(-17.04, -16.97) * mm, "end": v(-17.08, -17.08) * mm});
            skLineSegment(sketch, "E2039", {"start": v(-17.08, -17.08) * mm, "end": v(-16.68, -17.47) * mm});
            skLineSegment(sketch, "E2040", {"start": v(-16.68, -17.47) * mm, "end": v(-16.57, -17.42) * mm});
            skLineSegment(sketch, "E2041", {"start": v(-16.57, -17.42) * mm, "end": v(-16.5, -17.4) * mm});
            skLineSegment(sketch, "E2042", {"start": v(-16.5, -17.4) * mm, "end": v(-16.42, -17.36) * mm});
            skLineSegment(sketch, "E2043", {"start": v(-16.42, -17.36) * mm, "end": v(-16.35, -17.33) * mm});
            skLineSegment(sketch, "E2044", {"start": v(-16.35, -17.33) * mm, "end": v(-16.28, -17.3) * mm});
            skLineSegment(sketch, "E2045", {"start": v(-16.28, -17.3) * mm, "end": v(-16.21, -17.26) * mm});
            skLineSegment(sketch, "E2046", {"start": v(-16.21, -17.26) * mm, "end": v(-16.14, -17.23) * mm});
            skLineSegment(sketch, "E2047", {"start": v(-16.14, -17.23) * mm, "end": v(-16.08, -17.2) * mm});
            skLineSegment(sketch, "E2048", {"start": v(-16.08, -17.2) * mm, "end": v(-16.01, -17.16) * mm});
            skLineSegment(sketch, "E2049", {"start": v(-16.01, -17.16) * mm, "end": v(-15.95, -17.13) * mm});
            skLineSegment(sketch, "E2050", {"start": v(-15.95, -17.13) * mm, "end": v(-15.9, -17.1) * mm});
            skLineSegment(sketch, "E2051", {"start": v(-15.9, -17.1) * mm, "end": v(-15.83, -17.07) * mm});
            skLineSegment(sketch, "E2052", {"start": v(-15.83, -17.07) * mm, "end": v(-15.78, -17.04) * mm});
            skLineSegment(sketch, "E2053", {"start": v(-15.78, -17.04) * mm, "end": v(-15.72, -17) * mm});
            skLineSegment(sketch, "E2054", {"start": v(-15.72, -17) * mm, "end": v(-15.67, -16.98) * mm});
            skLineSegment(sketch, "E2055", {"start": v(-15.67, -16.98) * mm, "end": v(-15.62, -16.95) * mm});
            skLineSegment(sketch, "E2056", {"start": v(-15.62, -16.95) * mm, "end": v(-15.57, -16.92) * mm});
            skLineSegment(sketch, "E2057", {"start": v(-15.57, -16.92) * mm, "end": v(-15.52, -16.89) * mm});
            skLineSegment(sketch, "E2058", {"start": v(-15.52, -16.89) * mm, "end": v(-15.47, -16.86) * mm});
            skLineSegment(sketch, "E2059", {"start": v(-15.47, -16.86) * mm, "end": v(-15.43, -16.83) * mm});
            skLineSegment(sketch, "E2060", {"start": v(-15.43, -16.83) * mm, "end": v(-15.34, -16.78) * mm});
            skLineSegment(sketch, "E2061", {"start": v(-15.34, -16.78) * mm, "end": v(-15.26, -16.73) * mm});
            skLineSegment(sketch, "E2062", {"start": v(-15.26, -16.73) * mm, "end": v(-15.21, -16.69) * mm});
            skArc(sketch, "E2063", {"start": v(-15.21, -16.69) * mm, "mid": v(-14.83, -16.67) * mm, "end": v(-14.8, -17.05) * mm});
            skLineSegment(sketch, "E2064", {"start": v(-14.8, -17.05) * mm, "end": v(-14.83, -17.1) * mm});
            skLineSegment(sketch, "E2065", {"start": v(-14.83, -17.1) * mm, "end": v(-14.88, -17.2) * mm});
            skLineSegment(sketch, "E2066", {"start": v(-14.88, -17.2) * mm, "end": v(-14.92, -17.28) * mm});
            skLineSegment(sketch, "E2067", {"start": v(-14.92, -17.28) * mm, "end": v(-14.94, -17.33) * mm});
            skLineSegment(sketch, "E2068", {"start": v(-14.94, -17.33) * mm, "end": v(-14.97, -17.38) * mm});
            skLineSegment(sketch, "E2069", {"start": v(-14.97, -17.38) * mm, "end": v(-14.99, -17.43) * mm});
            skLineSegment(sketch, "E2070", {"start": v(-14.99, -17.43) * mm, "end": v(-15.01, -17.48) * mm});
            skLineSegment(sketch, "E2071", {"start": v(-15.01, -17.48) * mm, "end": v(-15.04, -17.54) * mm});
            skLineSegment(sketch, "E2072", {"start": v(-15.04, -17.54) * mm, "end": v(-15.06, -17.6) * mm});
            skLineSegment(sketch, "E2073", {"start": v(-15.06, -17.6) * mm, "end": v(-15.08, -17.65) * mm});
            skLineSegment(sketch, "E2074", {"start": v(-15.08, -17.65) * mm, "end": v(-15.1, -17.71) * mm});
            skLineSegment(sketch, "E2075", {"start": v(-15.1, -17.71) * mm, "end": v(-15.13, -17.78) * mm});
            skLineSegment(sketch, "E2076", {"start": v(-15.13, -17.78) * mm, "end": v(-15.16, -17.84) * mm});
            skLineSegment(sketch, "E2077", {"start": v(-15.16, -17.84) * mm, "end": v(-15.18, -17.9) * mm});
            skLineSegment(sketch, "E2078", {"start": v(-15.18, -17.9) * mm, "end": v(-15.2, -17.97) * mm});
            skLineSegment(sketch, "E2079", {"start": v(-15.2, -17.97) * mm, "end": v(-15.23, -18.04) * mm});
            skLineSegment(sketch, "E2080", {"start": v(-15.23, -18.04) * mm, "end": v(-15.25, -18.11) * mm});
            skLineSegment(sketch, "E2081", {"start": v(-15.25, -18.11) * mm, "end": v(-15.28, -18.18) * mm});
            skLineSegment(sketch, "E2082", {"start": v(-15.28, -18.18) * mm, "end": v(-15.3, -18.26) * mm});
            skLineSegment(sketch, "E2083", {"start": v(-15.3, -18.26) * mm, "end": v(-15.33, -18.33) * mm});
            skLineSegment(sketch, "E2084", {"start": v(-15.33, -18.33) * mm, "end": v(-15.35, -18.41) * mm});
            skLineSegment(sketch, "E2085", {"start": v(-15.35, -18.41) * mm, "end": v(-15.37, -18.5) * mm});
            skLineSegment(sketch, "E2086", {"start": v(-15.37, -18.5) * mm, "end": v(-15.4, -18.6) * mm});
            skLineSegment(sketch, "E2087", {"start": v(-15.4, -18.6) * mm, "end": v(-14.97, -18.95) * mm});
            skLineSegment(sketch, "E2088", {"start": v(-14.97, -18.95) * mm, "end": v(-14.87, -18.9) * mm});
            skLineSegment(sketch, "E2089", {"start": v(-14.87, -18.9) * mm, "end": v(-14.8, -18.86) * mm});
            skLineSegment(sketch, "E2090", {"start": v(-14.8, -18.86) * mm, "end": v(-14.73, -18.82) * mm});
            skLineSegment(sketch, "E2091", {"start": v(-14.73, -18.82) * mm, "end": v(-14.66, -18.78) * mm});
            skLineSegment(sketch, "E2092", {"start": v(-14.66, -18.78) * mm, "end": v(-14.59, -18.74) * mm});
            skLineSegment(sketch, "E2093", {"start": v(-14.59, -18.74) * mm, "end": v(-14.52, -18.7) * mm});
            skLineSegment(sketch, "E2094", {"start": v(-14.52, -18.7) * mm, "end": v(-14.46, -18.66) * mm});
            skLineSegment(sketch, "E2095", {"start": v(-14.46, -18.66) * mm, "end": v(-14.4, -18.62) * mm});
            skLineSegment(sketch, "E2096", {"start": v(-14.4, -18.62) * mm, "end": v(-14.34, -18.59) * mm});
            skLineSegment(sketch, "E2097", {"start": v(-14.34, -18.59) * mm, "end": v(-14.28, -18.55) * mm});
            skLineSegment(sketch, "E2098", {"start": v(-14.28, -18.55) * mm, "end": v(-14.22, -18.51) * mm});
            skLineSegment(sketch, "E2099", {"start": v(-14.22, -18.51) * mm, "end": v(-14.16, -18.48) * mm});
            skLineSegment(sketch, "E2100", {"start": v(-14.16, -18.48) * mm, "end": v(-14.11, -18.44) * mm});
            skLineSegment(sketch, "E2101", {"start": v(-14.11, -18.44) * mm, "end": v(-14.06, -18.4) * mm});
            skLineSegment(sketch, "E2102", {"start": v(-14.06, -18.4) * mm, "end": v(-14, -18.37) * mm});
            skLineSegment(sketch, "E2103", {"start": v(-14, -18.37) * mm, "end": v(-13.96, -18.33) * mm});
            skLineSegment(sketch, "E2104", {"start": v(-13.96, -18.33) * mm, "end": v(-13.91, -18.3) * mm});
            skLineSegment(sketch, "E2105", {"start": v(-13.91, -18.3) * mm, "end": v(-13.87, -18.27) * mm});
            skLineSegment(sketch, "E2106", {"start": v(-13.87, -18.27) * mm, "end": v(-13.83, -18.23) * mm});
            skLineSegment(sketch, "E2107", {"start": v(-13.83, -18.23) * mm, "end": v(-13.78, -18.2) * mm});
            skLineSegment(sketch, "E2108", {"start": v(-13.78, -18.2) * mm, "end": v(-13.7, -18.14) * mm});
            skLineSegment(sketch, "E2109", {"start": v(-13.7, -18.14) * mm, "end": v(-13.63, -18.08) * mm});
            skLineSegment(sketch, "E2110", {"start": v(-13.63, -18.08) * mm, "end": v(-13.58, -18.04) * mm});
            skArc(sketch, "E2111", {"start": v(-13.58, -18.04) * mm, "mid": v(-13.2, -17.99) * mm, "end": v(-13.14, -18.36) * mm});
            skLineSegment(sketch, "E2112", {"start": v(-13.14, -18.36) * mm, "end": v(-13.17, -18.42) * mm});
            skLineSegment(sketch, "E2113", {"start": v(-13.17, -18.42) * mm, "end": v(-13.2, -18.5) * mm});
            skLineSegment(sketch, "E2114", {"start": v(-13.2, -18.5) * mm, "end": v(-13.24, -18.6) * mm});
            skLineSegment(sketch, "E2115", {"start": v(-13.24, -18.6) * mm, "end": v(-13.25, -18.65) * mm});
            skLineSegment(sketch, "E2116", {"start": v(-13.25, -18.65) * mm, "end": v(-13.27, -18.7) * mm});
            skLineSegment(sketch, "E2117", {"start": v(-13.27, -18.7) * mm, "end": v(-13.3, -18.76) * mm});
            skLineSegment(sketch, "E2118", {"start": v(-13.3, -18.76) * mm, "end": v(-13.3, -18.81) * mm});
            skLineSegment(sketch, "E2119", {"start": v(-13.3, -18.81) * mm, "end": v(-13.33, -18.87) * mm});
            skLineSegment(sketch, "E2120", {"start": v(-13.33, -18.87) * mm, "end": v(-13.35, -18.93) * mm});
            skLineSegment(sketch, "E2121", {"start": v(-13.35, -18.93) * mm, "end": v(-13.36, -18.99) * mm});
            skLineSegment(sketch, "E2122", {"start": v(-13.36, -18.99) * mm, "end": v(-13.38, -19.05) * mm});
            skLineSegment(sketch, "E2123", {"start": v(-13.38, -19.05) * mm, "end": v(-13.4, -19.11) * mm});
            skLineSegment(sketch, "E2124", {"start": v(-13.4, -19.11) * mm, "end": v(-13.42, -19.18) * mm});
            skLineSegment(sketch, "E2125", {"start": v(-13.42, -19.18) * mm, "end": v(-13.44, -19.25) * mm});
            skLineSegment(sketch, "E2126", {"start": v(-13.44, -19.25) * mm, "end": v(-13.46, -19.32) * mm});
            skLineSegment(sketch, "E2127", {"start": v(-13.46, -19.32) * mm, "end": v(-13.47, -19.39) * mm});
            skLineSegment(sketch, "E2128", {"start": v(-13.47, -19.39) * mm, "end": v(-13.5, -19.46) * mm});
            skLineSegment(sketch, "E2129", {"start": v(-13.5, -19.46) * mm, "end": v(-13.5, -19.53) * mm});
            skLineSegment(sketch, "E2130", {"start": v(-13.5, -19.53) * mm, "end": v(-13.52, -19.6) * mm});
            skLineSegment(sketch, "E2131", {"start": v(-13.52, -19.6) * mm, "end": v(-13.54, -19.69) * mm});
            skLineSegment(sketch, "E2132", {"start": v(-13.54, -19.69) * mm, "end": v(-13.56, -19.77) * mm});
            skLineSegment(sketch, "E2133", {"start": v(-13.56, -19.77) * mm, "end": v(-13.57, -19.85) * mm});
            skLineSegment(sketch, "E2134", {"start": v(-13.57, -19.85) * mm, "end": v(-13.6, -19.96) * mm});
            skLineSegment(sketch, "E2135", {"start": v(-13.6, -19.96) * mm, "end": v(-13.13, -20.27) * mm});
            skLineSegment(sketch, "E2136", {"start": v(-13.13, -20.27) * mm, "end": v(-13.03, -20.2) * mm});
            skLineSegment(sketch, "E2137", {"start": v(-13.03, -20.2) * mm, "end": v(-12.97, -20.16) * mm});
            skLineSegment(sketch, "E2138", {"start": v(-12.97, -20.16) * mm, "end": v(-12.9, -20.11) * mm});
            skLineSegment(sketch, "E2139", {"start": v(-12.9, -20.11) * mm, "end": v(-12.83, -20.07) * mm});
            skLineSegment(sketch, "E2140", {"start": v(-12.83, -20.07) * mm, "end": v(-12.77, -20.02) * mm});
            skLineSegment(sketch, "E2141", {"start": v(-12.77, -20.02) * mm, "end": v(-12.7, -19.98) * mm});
            skLineSegment(sketch, "E2142", {"start": v(-12.7, -19.98) * mm, "end": v(-12.65, -19.93) * mm});
            skLineSegment(sketch, "E2143", {"start": v(-12.65, -19.93) * mm, "end": v(-12.59, -19.9) * mm});
            skLineSegment(sketch, "E2144", {"start": v(-12.59, -19.9) * mm, "end": v(-12.53, -19.85) * mm});
            skLineSegment(sketch, "E2145", {"start": v(-12.53, -19.85) * mm, "end": v(-12.48, -19.8) * mm});
            skLineSegment(sketch, "E2146", {"start": v(-12.48, -19.8) * mm, "end": v(-12.42, -19.76) * mm});
            skLineSegment(sketch, "E2147", {"start": v(-12.42, -19.76) * mm, "end": v(-12.37, -19.72) * mm});
            skLineSegment(sketch, "E2148", {"start": v(-12.37, -19.72) * mm, "end": v(-12.32, -19.68) * mm});
            skLineSegment(sketch, "E2149", {"start": v(-12.32, -19.68) * mm, "end": v(-12.27, -19.64) * mm});
            skLineSegment(sketch, "E2150", {"start": v(-12.27, -19.64) * mm, "end": v(-12.23, -19.6) * mm});
            skLineSegment(sketch, "E2151", {"start": v(-12.23, -19.6) * mm, "end": v(-12.18, -19.56) * mm});
            skLineSegment(sketch, "E2152", {"start": v(-12.18, -19.56) * mm, "end": v(-12.14, -19.52) * mm});
            skLineSegment(sketch, "E2153", {"start": v(-12.14, -19.52) * mm, "end": v(-12.1, -19.49) * mm});
            skLineSegment(sketch, "E2154", {"start": v(-12.1, -19.49) * mm, "end": v(-12.06, -19.45) * mm});
            skLineSegment(sketch, "E2155", {"start": v(-12.06, -19.45) * mm, "end": v(-12.02, -19.41) * mm});
            skLineSegment(sketch, "E2156", {"start": v(-12.02, -19.41) * mm, "end": v(-11.95, -19.34) * mm});
            skLineSegment(sketch, "E2157", {"start": v(-11.95, -19.34) * mm, "end": v(-11.88, -19.28) * mm});
            skLineSegment(sketch, "E2158", {"start": v(-11.88, -19.28) * mm, "end": v(-11.83, -19.23) * mm});
            skArc(sketch, "E2159", {"start": v(-11.83, -19.23) * mm, "mid": v(-11.46, -19.15) * mm, "end": v(-11.36, -19.51) * mm});
            skLineSegment(sketch, "E2160", {"start": v(-11.36, -19.51) * mm, "end": v(-11.38, -19.57) * mm});
            skLineSegment(sketch, "E2161", {"start": v(-11.38, -19.57) * mm, "end": v(-11.4, -19.66) * mm});
            skLineSegment(sketch, "E2162", {"start": v(-11.4, -19.66) * mm, "end": v(-11.44, -19.76) * mm});
            skLineSegment(sketch, "E2163", {"start": v(-11.44, -19.76) * mm, "end": v(-11.45, -19.81) * mm});
            skLineSegment(sketch, "E2164", {"start": v(-11.45, -19.81) * mm, "end": v(-11.46, -19.86) * mm});
            skLineSegment(sketch, "E2165", {"start": v(-11.46, -19.86) * mm, "end": v(-11.48, -19.92) * mm});
            skLineSegment(sketch, "E2166", {"start": v(-11.48, -19.92) * mm, "end": v(-11.49, -19.98) * mm});
            skLineSegment(sketch, "E2167", {"start": v(-11.49, -19.98) * mm, "end": v(-11.5, -20.03) * mm});
            skLineSegment(sketch, "E2168", {"start": v(-11.5, -20.03) * mm, "end": v(-11.52, -20.1) * mm});
            skLineSegment(sketch, "E2169", {"start": v(-11.52, -20.1) * mm, "end": v(-11.53, -20.16) * mm});
            skLineSegment(sketch, "E2170", {"start": v(-11.53, -20.16) * mm, "end": v(-11.54, -20.22) * mm});
            skLineSegment(sketch, "E2171", {"start": v(-11.54, -20.22) * mm, "end": v(-11.55, -20.28) * mm});
            skLineSegment(sketch, "E2172", {"start": v(-11.55, -20.28) * mm, "end": v(-11.56, -20.35) * mm});
            skLineSegment(sketch, "E2173", {"start": v(-11.56, -20.35) * mm, "end": v(-11.58, -20.42) * mm});
            skLineSegment(sketch, "E2174", {"start": v(-11.58, -20.42) * mm, "end": v(-11.59, -20.49) * mm});
            skLineSegment(sketch, "E2175", {"start": v(-11.59, -20.49) * mm, "end": v(-11.6, -20.56) * mm});
            skLineSegment(sketch, "E2176", {"start": v(-11.6, -20.56) * mm, "end": v(-11.6, -20.64) * mm});
            skLineSegment(sketch, "E2177", {"start": v(-11.6, -20.64) * mm, "end": v(-11.62, -20.71) * mm});
            skLineSegment(sketch, "E2178", {"start": v(-11.62, -20.71) * mm, "end": v(-11.63, -20.79) * mm});
            skLineSegment(sketch, "E2179", {"start": v(-11.63, -20.79) * mm, "end": v(-11.64, -20.87) * mm});
            skLineSegment(sketch, "E2180", {"start": v(-11.64, -20.87) * mm, "end": v(-11.65, -20.95) * mm});
            skLineSegment(sketch, "E2181", {"start": v(-11.65, -20.95) * mm, "end": v(-11.66, -21.03) * mm});
            skLineSegment(sketch, "E2182", {"start": v(-11.66, -21.03) * mm, "end": v(-11.67, -21.15) * mm});
            skLineSegment(sketch, "E2183", {"start": v(-11.67, -21.15) * mm, "end": v(-11.18, -21.41) * mm});
            skLineSegment(sketch, "E2184", {"start": v(-11.18, -21.41) * mm, "end": v(-11.09, -21.34) * mm});
            skLineSegment(sketch, "E2185", {"start": v(-11.09, -21.34) * mm, "end": v(-11.02, -21.28) * mm});
            skLineSegment(sketch, "E2186", {"start": v(-11.02, -21.28) * mm, "end": v(-10.96, -21.23) * mm});
            skLineSegment(sketch, "E2187", {"start": v(-10.96, -21.23) * mm, "end": v(-10.9, -21.18) * mm});
            skLineSegment(sketch, "E2188", {"start": v(-10.9, -21.18) * mm, "end": v(-10.84, -21.13) * mm});
            skLineSegment(sketch, "E2189", {"start": v(-10.84, -21.13) * mm, "end": v(-10.78, -21.08) * mm});
            skLineSegment(sketch, "E2190", {"start": v(-10.78, -21.08) * mm, "end": v(-10.73, -21.03) * mm});
            skLineSegment(sketch, "E2191", {"start": v(-10.73, -21.03) * mm, "end": v(-10.67, -20.98) * mm});
            skLineSegment(sketch, "E2192", {"start": v(-10.67, -20.98) * mm, "end": v(-10.62, -20.93) * mm});
            skLineSegment(sketch, "E2193", {"start": v(-10.62, -20.93) * mm, "end": v(-10.57, -20.89) * mm});
            skLineSegment(sketch, "E2194", {"start": v(-10.57, -20.89) * mm, "end": v(-10.52, -20.84) * mm});
            skLineSegment(sketch, "E2195", {"start": v(-10.52, -20.84) * mm, "end": v(-10.47, -20.8) * mm});
            skLineSegment(sketch, "E2196", {"start": v(-10.47, -20.8) * mm, "end": v(-10.43, -20.75) * mm});
            skLineSegment(sketch, "E2197", {"start": v(-10.43, -20.75) * mm, "end": v(-10.38, -20.7) * mm});
            skLineSegment(sketch, "E2198", {"start": v(-10.38, -20.7) * mm, "end": v(-10.34, -20.66) * mm});
            skLineSegment(sketch, "E2199", {"start": v(-10.34, -20.66) * mm, "end": v(-10.3, -20.62) * mm});
            skLineSegment(sketch, "E2200", {"start": v(-10.3, -20.62) * mm, "end": v(-10.26, -20.57) * mm});
            skLineSegment(sketch, "E2201", {"start": v(-10.26, -20.57) * mm, "end": v(-10.22, -20.53) * mm});
            skLineSegment(sketch, "E2202", {"start": v(-10.22, -20.53) * mm, "end": v(-10.18, -20.5) * mm});
            skLineSegment(sketch, "E2203", {"start": v(-10.18, -20.5) * mm, "end": v(-10.15, -20.45) * mm});
            skLineSegment(sketch, "E2204", {"start": v(-10.15, -20.45) * mm, "end": v(-10.08, -20.38) * mm});
            skLineSegment(sketch, "E2205", {"start": v(-10.08, -20.38) * mm, "end": v(-10.02, -20.3) * mm});
            skLineSegment(sketch, "E2206", {"start": v(-10.02, -20.3) * mm, "end": v(-9.98, -20.25) * mm});
            skArc(sketch, "E2207", {"start": v(-9.98, -20.25) * mm, "mid": v(-9.62, -20.13) * mm, "end": v(-9.49, -20.49) * mm});
            skLineSegment(sketch, "E2208", {"start": v(-9.49, -20.49) * mm, "end": v(-9.5, -20.55) * mm});
            skLineSegment(sketch, "E2209", {"start": v(-9.5, -20.55) * mm, "end": v(-9.52, -20.64) * mm});
            skLineSegment(sketch, "E2210", {"start": v(-9.52, -20.64) * mm, "end": v(-9.54, -20.74) * mm});
            skLineSegment(sketch, "E2211", {"start": v(-9.54, -20.74) * mm, "end": v(-9.54, -20.8) * mm});
            skLineSegment(sketch, "E2212", {"start": v(-9.54, -20.8) * mm, "end": v(-9.55, -20.85) * mm});
            skLineSegment(sketch, "E2213", {"start": v(-9.55, -20.85) * mm, "end": v(-9.56, -20.9) * mm});
            skLineSegment(sketch, "E2214", {"start": v(-9.56, -20.9) * mm, "end": v(-9.57, -20.96) * mm});
            skLineSegment(sketch, "E2215", {"start": v(-9.57, -20.96) * mm, "end": v(-9.58, -21.02) * mm});
            skLineSegment(sketch, "E2216", {"start": v(-9.58, -21.02) * mm, "end": v(-9.58, -21.08) * mm});
            skLineSegment(sketch, "E2217", {"start": v(-9.58, -21.08) * mm, "end": v(-9.59, -21.15) * mm});
            skLineSegment(sketch, "E2218", {"start": v(-9.59, -21.15) * mm, "end": v(-9.6, -21.2) * mm});
            skLineSegment(sketch, "E2219", {"start": v(-9.6, -21.2) * mm, "end": v(-9.6, -21.28) * mm});
            skLineSegment(sketch, "E2220", {"start": v(-9.6, -21.28) * mm, "end": v(-9.6, -21.34) * mm});
            skLineSegment(sketch, "E2221", {"start": v(-9.6, -21.34) * mm, "end": v(-9.61, -21.41) * mm});
            skLineSegment(sketch, "E2222", {"start": v(-9.61, -21.41) * mm, "end": v(-9.62, -21.48) * mm});
            skLineSegment(sketch, "E2223", {"start": v(-9.62, -21.48) * mm, "end": v(-9.62, -21.56) * mm});
            skLineSegment(sketch, "E2224", {"start": v(-9.62, -21.56) * mm, "end": v(-9.63, -21.63) * mm});
            skLineSegment(sketch, "E2225", {"start": v(-9.63, -21.63) * mm, "end": v(-9.63, -21.7) * mm});
            skLineSegment(sketch, "E2226", {"start": v(-9.63, -21.7) * mm, "end": v(-9.63, -21.79) * mm});
            skLineSegment(sketch, "E2227", {"start": v(-9.63, -21.79) * mm, "end": v(-9.63, -21.87) * mm});
            skLineSegment(sketch, "E2228", {"start": v(-9.63, -21.87) * mm, "end": v(-9.63, -21.95) * mm});
            skLineSegment(sketch, "E2229", {"start": v(-9.63, -21.95) * mm, "end": v(-9.63, -22.03) * mm});
            skLineSegment(sketch, "E2230", {"start": v(-9.63, -22.03) * mm, "end": v(-9.63, -22.15) * mm});
            skLineSegment(sketch, "E2231", {"start": v(-9.63, -22.15) * mm, "end": v(-9.12, -22.36) * mm});
            skLineSegment(sketch, "E2232", {"start": v(-9.12, -22.36) * mm, "end": v(-9.04, -22.28) * mm});
            skLineSegment(sketch, "E2233", {"start": v(-9.04, -22.28) * mm, "end": v(-8.98, -22.22) * mm});
            skLineSegment(sketch, "E2234", {"start": v(-8.98, -22.22) * mm, "end": v(-8.92, -22.17) * mm});
            skLineSegment(sketch, "E2235", {"start": v(-8.92, -22.17) * mm, "end": v(-8.87, -22.1) * mm});
            skLineSegment(sketch, "E2236", {"start": v(-8.87, -22.1) * mm, "end": v(-8.81, -22.05) * mm});
            skLineSegment(sketch, "E2237", {"start": v(-8.81, -22.05) * mm, "end": v(-8.76, -22) * mm});
            skLineSegment(sketch, "E2238", {"start": v(-8.76, -22) * mm, "end": v(-8.7, -21.94) * mm});
            skLineSegment(sketch, "E2239", {"start": v(-8.7, -21.94) * mm, "end": v(-8.66, -21.89) * mm});
            skLineSegment(sketch, "E2240", {"start": v(-8.66, -21.89) * mm, "end": v(-8.61, -21.83) * mm});
            skLineSegment(sketch, "E2241", {"start": v(-8.61, -21.83) * mm, "end": v(-8.57, -21.78) * mm});
            skLineSegment(sketch, "E2242", {"start": v(-8.57, -21.78) * mm, "end": v(-8.52, -21.73) * mm});
            skLineSegment(sketch, "E2243", {"start": v(-8.52, -21.73) * mm, "end": v(-8.48, -21.68) * mm});
            skLineSegment(sketch, "E2244", {"start": v(-8.48, -21.68) * mm, "end": v(-8.44, -21.63) * mm});
            skLineSegment(sketch, "E2245", {"start": v(-8.44, -21.63) * mm, "end": v(-8.4, -21.58) * mm});
            skLineSegment(sketch, "E2246", {"start": v(-8.4, -21.58) * mm, "end": v(-8.36, -21.53) * mm});
            skLineSegment(sketch, "E2247", {"start": v(-8.36, -21.53) * mm, "end": v(-8.32, -21.49) * mm});
            skLineSegment(sketch, "E2248", {"start": v(-8.32, -21.49) * mm, "end": v(-8.29, -21.44) * mm});
            skLineSegment(sketch, "E2249", {"start": v(-8.29, -21.44) * mm, "end": v(-8.25, -21.4) * mm});
            skLineSegment(sketch, "E2250", {"start": v(-8.25, -21.4) * mm, "end": v(-8.22, -21.35) * mm});
            skLineSegment(sketch, "E2251", {"start": v(-8.22, -21.35) * mm, "end": v(-8.19, -21.31) * mm});
            skLineSegment(sketch, "E2252", {"start": v(-8.19, -21.31) * mm, "end": v(-8.13, -21.23) * mm});
            skLineSegment(sketch, "E2253", {"start": v(-8.13, -21.23) * mm, "end": v(-8.08, -21.15) * mm});
            skLineSegment(sketch, "E2254", {"start": v(-8.08, -21.15) * mm, "end": v(-8.04, -21.1) * mm});
            skArc(sketch, "E2255", {"start": v(-8.04, -21.1) * mm, "mid": v(-7.7, -20.95) * mm, "end": v(-7.53, -21.29) * mm});
            skLineSegment(sketch, "E2256", {"start": v(-7.53, -21.29) * mm, "end": v(-7.53, -21.35) * mm});
            skLineSegment(sketch, "E2257", {"start": v(-7.53, -21.35) * mm, "end": v(-7.54, -21.44) * mm});
            skLineSegment(sketch, "E2258", {"start": v(-7.54, -21.44) * mm, "end": v(-7.55, -21.55) * mm});
            skLineSegment(sketch, "E2259", {"start": v(-7.55, -21.55) * mm, "end": v(-7.55, -21.6) * mm});
            skLineSegment(sketch, "E2260", {"start": v(-7.55, -21.6) * mm, "end": v(-7.56, -21.65) * mm});
            skLineSegment(sketch, "E2261", {"start": v(-7.56, -21.65) * mm, "end": v(-7.56, -21.7) * mm});
            skLineSegment(sketch, "E2262", {"start": v(-7.56, -21.7) * mm, "end": v(-7.56, -21.77) * mm});
            skLineSegment(sketch, "E2263", {"start": v(-7.56, -21.77) * mm, "end": v(-7.57, -21.83) * mm});
            skLineSegment(sketch, "E2264", {"start": v(-7.57, -21.83) * mm, "end": v(-7.57, -21.89) * mm});
            skLineSegment(sketch, "E2265", {"start": v(-7.57, -21.89) * mm, "end": v(-7.57, -21.95) * mm});
            skLineSegment(sketch, "E2266", {"start": v(-7.57, -21.95) * mm, "end": v(-7.57, -22.01) * mm});
            skLineSegment(sketch, "E2267", {"start": v(-7.57, -22.01) * mm, "end": v(-7.57, -22.08) * mm});
            skLineSegment(sketch, "E2268", {"start": v(-7.57, -22.08) * mm, "end": v(-7.57, -22.15) * mm});
            skLineSegment(sketch, "E2269", {"start": v(-7.57, -22.15) * mm, "end": v(-7.57, -22.22) * mm});
            skLineSegment(sketch, "E2270", {"start": v(-7.57, -22.22) * mm, "end": v(-7.56, -22.29) * mm});
            skLineSegment(sketch, "E2271", {"start": v(-7.56, -22.29) * mm, "end": v(-7.56, -22.36) * mm});
            skLineSegment(sketch, "E2272", {"start": v(-7.56, -22.36) * mm, "end": v(-7.56, -22.44) * mm});
            skLineSegment(sketch, "E2273", {"start": v(-7.56, -22.44) * mm, "end": v(-7.55, -22.51) * mm});
            skLineSegment(sketch, "E2274", {"start": v(-7.55, -22.51) * mm, "end": v(-7.55, -22.6) * mm});
            skLineSegment(sketch, "E2275", {"start": v(-7.55, -22.6) * mm, "end": v(-7.54, -22.67) * mm});
            skLineSegment(sketch, "E2276", {"start": v(-7.54, -22.67) * mm, "end": v(-7.54, -22.75) * mm});
            skLineSegment(sketch, "E2277", {"start": v(-7.54, -22.75) * mm, "end": v(-7.53, -22.83) * mm});
            skLineSegment(sketch, "E2278", {"start": v(-7.53, -22.83) * mm, "end": v(-7.52, -22.95) * mm});
            skLineSegment(sketch, "E2279", {"start": v(-7.52, -22.95) * mm, "end": v(-6.99, -23.12) * mm});
            skLineSegment(sketch, "E2280", {"start": v(-6.99, -23.12) * mm, "end": v(-6.91, -23.03) * mm});
            skLineSegment(sketch, "E2281", {"start": v(-6.91, -23.03) * mm, "end": v(-6.86, -22.97) * mm});
            skLineSegment(sketch, "E2282", {"start": v(-6.86, -22.97) * mm, "end": v(-6.8, -22.9) * mm});
            skLineSegment(sketch, "E2283", {"start": v(-6.8, -22.9) * mm, "end": v(-6.76, -22.84) * mm});
            skLineSegment(sketch, "E2284", {"start": v(-6.76, -22.84) * mm, "end": v(-6.7, -22.78) * mm});
            skLineSegment(sketch, "E2285", {"start": v(-6.7, -22.78) * mm, "end": v(-6.66, -22.72) * mm});
            skLineSegment(sketch, "E2286", {"start": v(-6.66, -22.72) * mm, "end": v(-6.62, -22.66) * mm});
            skLineSegment(sketch, "E2287", {"start": v(-6.62, -22.66) * mm, "end": v(-6.57, -22.6) * mm});
            skLineSegment(sketch, "E2288", {"start": v(-6.57, -22.6) * mm, "end": v(-6.53, -22.54) * mm});
            skLineSegment(sketch, "E2289", {"start": v(-6.53, -22.54) * mm, "end": v(-6.49, -22.49) * mm});
            skLineSegment(sketch, "E2290", {"start": v(-6.49, -22.49) * mm, "end": v(-6.45, -22.43) * mm});
            skLineSegment(sketch, "E2291", {"start": v(-6.45, -22.43) * mm, "end": v(-6.41, -22.38) * mm});
            skLineSegment(sketch, "E2292", {"start": v(-6.41, -22.38) * mm, "end": v(-6.37, -22.33) * mm});
            skLineSegment(sketch, "E2293", {"start": v(-6.37, -22.33) * mm, "end": v(-6.34, -22.27) * mm});
            skLineSegment(sketch, "E2294", {"start": v(-6.34, -22.27) * mm, "end": v(-6.3, -22.22) * mm});
            skLineSegment(sketch, "E2295", {"start": v(-6.3, -22.22) * mm, "end": v(-6.27, -22.17) * mm});
            skLineSegment(sketch, "E2296", {"start": v(-6.27, -22.17) * mm, "end": v(-6.24, -22.12) * mm});
            skLineSegment(sketch, "E2297", {"start": v(-6.24, -22.12) * mm, "end": v(-6.21, -22.08) * mm});
            skLineSegment(sketch, "E2298", {"start": v(-6.21, -22.08) * mm, "end": v(-6.18, -22.03) * mm});
            skLineSegment(sketch, "E2299", {"start": v(-6.18, -22.03) * mm, "end": v(-6.16, -21.98) * mm});
            skLineSegment(sketch, "E2300", {"start": v(-6.16, -21.98) * mm, "end": v(-6.1, -21.9) * mm});
            skLineSegment(sketch, "E2301", {"start": v(-6.1, -21.9) * mm, "end": v(-6.06, -21.82) * mm});
            skLineSegment(sketch, "E2302", {"start": v(-6.06, -21.82) * mm, "end": v(-6.03, -21.76) * mm});
            skArc(sketch, "E2303", {"start": v(-6.03, -21.76) * mm, "mid": v(-5.7, -21.57) * mm, "end": v(-5.5, -21.9) * mm});
            skLineSegment(sketch, "E2304", {"start": v(-5.5, -21.9) * mm, "end": v(-5.5, -21.96) * mm});
            skLineSegment(sketch, "E2305", {"start": v(-5.5, -21.96) * mm, "end": v(-5.5, -22.06) * mm});
            skLineSegment(sketch, "E2306", {"start": v(-5.5, -22.06) * mm, "end": v(-5.5, -22.16) * mm});
            skLineSegment(sketch, "E2307", {"start": v(-5.5, -22.16) * mm, "end": v(-5.5, -22.2) * mm});
            skLineSegment(sketch, "E2308", {"start": v(-5.5, -22.2) * mm, "end": v(-5.5, -22.26) * mm});
            skLineSegment(sketch, "E2309", {"start": v(-5.5, -22.26) * mm, "end": v(-5.5, -22.32) * mm});
            skLineSegment(sketch, "E2310", {"start": v(-5.5, -22.32) * mm, "end": v(-5.5, -22.38) * mm});
            skLineSegment(sketch, "E2311", {"start": v(-5.5, -22.38) * mm, "end": v(-5.49, -22.44) * mm});
            skLineSegment(sketch, "E2312", {"start": v(-5.49, -22.44) * mm, "end": v(-5.48, -22.5) * mm});
            skLineSegment(sketch, "E2313", {"start": v(-5.48, -22.5) * mm, "end": v(-5.48, -22.56) * mm});
            skLineSegment(sketch, "E2314", {"start": v(-5.48, -22.56) * mm, "end": v(-5.47, -22.63) * mm});
            skLineSegment(sketch, "E2315", {"start": v(-5.47, -22.63) * mm, "end": v(-5.47, -22.7) * mm});
            skLineSegment(sketch, "E2316", {"start": v(-5.47, -22.7) * mm, "end": v(-5.46, -22.76) * mm});
            skLineSegment(sketch, "E2317", {"start": v(-5.46, -22.76) * mm, "end": v(-5.45, -22.83) * mm});
            skLineSegment(sketch, "E2318", {"start": v(-5.45, -22.83) * mm, "end": v(-5.44, -22.9) * mm});
            skLineSegment(sketch, "E2319", {"start": v(-5.44, -22.9) * mm, "end": v(-5.43, -22.97) * mm});
            skLineSegment(sketch, "E2320", {"start": v(-5.43, -22.97) * mm, "end": v(-5.42, -23.05) * mm});
            skLineSegment(sketch, "E2321", {"start": v(-5.42, -23.05) * mm, "end": v(-5.41, -23.12) * mm});
            skLineSegment(sketch, "E2322", {"start": v(-5.41, -23.12) * mm, "end": v(-5.4, -23.2) * mm});
            skLineSegment(sketch, "E2323", {"start": v(-5.4, -23.2) * mm, "end": v(-5.39, -23.28) * mm});
            skLineSegment(sketch, "E2324", {"start": v(-5.39, -23.28) * mm, "end": v(-5.37, -23.36) * mm});
            skLineSegment(sketch, "E2325", {"start": v(-5.37, -23.36) * mm, "end": v(-5.36, -23.44) * mm});
            skLineSegment(sketch, "E2326", {"start": v(-5.36, -23.44) * mm, "end": v(-5.34, -23.55) * mm});
            skLineSegment(sketch, "E2327", {"start": v(-5.34, -23.55) * mm, "end": v(-4.8, -23.67) * mm});
            skLineSegment(sketch, "E2328", {"start": v(-4.8, -23.67) * mm, "end": v(-4.73, -23.57) * mm});
            skLineSegment(sketch, "E2329", {"start": v(-4.73, -23.57) * mm, "end": v(-4.68, -23.5) * mm});
            skLineSegment(sketch, "E2330", {"start": v(-4.68, -23.5) * mm, "end": v(-4.63, -23.44) * mm});
            skLineSegment(sketch, "E2331", {"start": v(-4.63, -23.44) * mm, "end": v(-4.59, -23.37) * mm});
            skLineSegment(sketch, "E2332", {"start": v(-4.59, -23.37) * mm, "end": v(-4.55, -23.3) * mm});
            skLineSegment(sketch, "E2333", {"start": v(-4.55, -23.3) * mm, "end": v(-4.5, -23.24) * mm});
            skLineSegment(sketch, "E2334", {"start": v(-4.5, -23.24) * mm, "end": v(-4.46, -23.18) * mm});
            skLineSegment(sketch, "E2335", {"start": v(-4.46, -23.18) * mm, "end": v(-4.43, -23.12) * mm});
            skLineSegment(sketch, "E2336", {"start": v(-4.43, -23.12) * mm, "end": v(-4.39, -23.06) * mm});
            skLineSegment(sketch, "E2337", {"start": v(-4.39, -23.06) * mm, "end": v(-4.35, -23) * mm});
            skLineSegment(sketch, "E2338", {"start": v(-4.35, -23) * mm, "end": v(-4.32, -22.94) * mm});
            skLineSegment(sketch, "E2339", {"start": v(-4.32, -22.94) * mm, "end": v(-4.29, -22.88) * mm});
            skLineSegment(sketch, "E2340", {"start": v(-4.29, -22.88) * mm, "end": v(-4.26, -22.82) * mm});
            skLineSegment(sketch, "E2341", {"start": v(-4.26, -22.82) * mm, "end": v(-4.23, -22.77) * mm});
            skLineSegment(sketch, "E2342", {"start": v(-4.23, -22.77) * mm, "end": v(-4.2, -22.71) * mm});
            skLineSegment(sketch, "E2343", {"start": v(-4.2, -22.71) * mm, "end": v(-4.17, -22.66) * mm});
            skLineSegment(sketch, "E2344", {"start": v(-4.17, -22.66) * mm, "end": v(-4.14, -22.61) * mm});
            skLineSegment(sketch, "E2345", {"start": v(-4.14, -22.61) * mm, "end": v(-4.12, -22.56) * mm});
            skLineSegment(sketch, "E2346", {"start": v(-4.12, -22.56) * mm, "end": v(-4.1, -22.51) * mm});
            skLineSegment(sketch, "E2347", {"start": v(-4.1, -22.51) * mm, "end": v(-4.07, -22.46) * mm});
            skLineSegment(sketch, "E2348", {"start": v(-4.07, -22.46) * mm, "end": v(-4.03, -22.37) * mm});
            skLineSegment(sketch, "E2349", {"start": v(-4.03, -22.37) * mm, "end": v(-4, -22.29) * mm});
            skLineSegment(sketch, "E2350", {"start": v(-4, -22.29) * mm, "end": v(-3.96, -22.23) * mm});
            skArc(sketch, "E2351", {"start": v(-3.96, -22.23) * mm, "mid": v(-3.65, -22.01) * mm, "end": v(-3.43, -22.31) * mm});
            skLineSegment(sketch, "E2352", {"start": v(-3.43, -22.31) * mm, "end": v(-3.42, -22.38) * mm});
            skLineSegment(sketch, "E2353", {"start": v(-3.42, -22.38) * mm, "end": v(-3.41, -22.47) * mm});
            skLineSegment(sketch, "E2354", {"start": v(-3.41, -22.47) * mm, "end": v(-3.4, -22.57) * mm});
            skLineSegment(sketch, "E2355", {"start": v(-3.4, -22.57) * mm, "end": v(-3.4, -22.63) * mm});
            skLineSegment(sketch, "E2356", {"start": v(-3.4, -22.63) * mm, "end": v(-3.39, -22.68) * mm});
            skLineSegment(sketch, "E2357", {"start": v(-3.39, -22.68) * mm, "end": v(-3.38, -22.74) * mm});
            skLineSegment(sketch, "E2358", {"start": v(-3.38, -22.74) * mm, "end": v(-3.37, -22.8) * mm});
            skLineSegment(sketch, "E2359", {"start": v(-3.37, -22.8) * mm, "end": v(-3.36, -22.85) * mm});
            skLineSegment(sketch, "E2360", {"start": v(-3.36, -22.85) * mm, "end": v(-3.35, -22.91) * mm});
            skLineSegment(sketch, "E2361", {"start": v(-3.35, -22.91) * mm, "end": v(-3.34, -22.97) * mm});
            skLineSegment(sketch, "E2362", {"start": v(-3.34, -22.97) * mm, "end": v(-3.33, -23.04) * mm});
            skLineSegment(sketch, "E2363", {"start": v(-3.33, -23.04) * mm, "end": v(-3.32, -23.1) * mm});
            skLineSegment(sketch, "E2364", {"start": v(-3.32, -23.1) * mm, "end": v(-3.3, -23.17) * mm});
            skLineSegment(sketch, "E2365", {"start": v(-3.3, -23.17) * mm, "end": v(-3.3, -23.24) * mm});
            skLineSegment(sketch, "E2366", {"start": v(-3.3, -23.24) * mm, "end": v(-3.28, -23.3) * mm});
            skLineSegment(sketch, "E2367", {"start": v(-3.28, -23.3) * mm, "end": v(-3.26, -23.38) * mm});
            skLineSegment(sketch, "E2368", {"start": v(-3.26, -23.38) * mm, "end": v(-3.24, -23.45) * mm});
            skLineSegment(sketch, "E2369", {"start": v(-3.24, -23.45) * mm, "end": v(-3.22, -23.53) * mm});
            skLineSegment(sketch, "E2370", {"start": v(-3.22, -23.53) * mm, "end": v(-3.2, -23.6) * mm});
            skLineSegment(sketch, "E2371", {"start": v(-3.2, -23.6) * mm, "end": v(-3.18, -23.68) * mm});
            skLineSegment(sketch, "E2372", {"start": v(-3.18, -23.68) * mm, "end": v(-3.16, -23.76) * mm});
            skLineSegment(sketch, "E2373", {"start": v(-3.16, -23.76) * mm, "end": v(-3.14, -23.84) * mm});
            skLineSegment(sketch, "E2374", {"start": v(-3.14, -23.84) * mm, "end": v(-3.1, -23.95) * mm});
            skLineSegment(sketch, "E2375", {"start": v(-3.1, -23.95) * mm, "end": v(-2.56, -24.02) * mm});
            skLineSegment(sketch, "E2376", {"start": v(-2.56, -24.02) * mm, "end": v(-2.5, -23.91) * mm});
            skLineSegment(sketch, "E2377", {"start": v(-2.5, -23.91) * mm, "end": v(-2.46, -23.84) * mm});
            skLineSegment(sketch, "E2378", {"start": v(-2.46, -23.84) * mm, "end": v(-2.42, -23.77) * mm});
            skLineSegment(sketch, "E2379", {"start": v(-2.42, -23.77) * mm, "end": v(-2.38, -23.7) * mm});
            skLineSegment(sketch, "E2380", {"start": v(-2.38, -23.7) * mm, "end": v(-2.34, -23.63) * mm});
            skLineSegment(sketch, "E2381", {"start": v(-2.34, -23.63) * mm, "end": v(-2.3, -23.56) * mm});
            skLineSegment(sketch, "E2382", {"start": v(-2.3, -23.56) * mm, "end": v(-2.27, -23.5) * mm});
            skLineSegment(sketch, "E2383", {"start": v(-2.27, -23.5) * mm, "end": v(-2.24, -23.43) * mm});
            skLineSegment(sketch, "E2384", {"start": v(-2.24, -23.43) * mm, "end": v(-2.21, -23.37) * mm});
            skLineSegment(sketch, "E2385", {"start": v(-2.21, -23.37) * mm, "end": v(-2.18, -23.3) * mm});
            skLineSegment(sketch, "E2386", {"start": v(-2.18, -23.3) * mm, "end": v(-2.15, -23.24) * mm});
            skLineSegment(sketch, "E2387", {"start": v(-2.15, -23.24) * mm, "end": v(-2.13, -23.18) * mm});
            skLineSegment(sketch, "E2388", {"start": v(-2.13, -23.18) * mm, "end": v(-2.1, -23.12) * mm});
            skLineSegment(sketch, "E2389", {"start": v(-2.1, -23.12) * mm, "end": v(-2.08, -23.06) * mm});
            skLineSegment(sketch, "E2390", {"start": v(-2.08, -23.06) * mm, "end": v(-2.05, -23) * mm});
            skLineSegment(sketch, "E2391", {"start": v(-2.05, -23) * mm, "end": v(-2.03, -22.95) * mm});
            skLineSegment(sketch, "E2392", {"start": v(-2.03, -22.95) * mm, "end": v(-2, -22.9) * mm});
            skLineSegment(sketch, "E2393", {"start": v(-2, -22.9) * mm, "end": v(-1.99, -22.85) * mm});
            skLineSegment(sketch, "E2394", {"start": v(-1.99, -22.85) * mm, "end": v(-1.97, -22.8) * mm});
            skLineSegment(sketch, "E2395", {"start": v(-1.97, -22.8) * mm, "end": v(-1.95, -22.75) * mm});
            skLineSegment(sketch, "E2396", {"start": v(-1.95, -22.75) * mm, "end": v(-1.92, -22.65) * mm});
            skLineSegment(sketch, "E2397", {"start": v(-1.92, -22.65) * mm, "end": v(-1.89, -22.56) * mm});
            skLineSegment(sketch, "E2398", {"start": v(-1.89, -22.56) * mm, "end": v(-1.87, -22.5) * mm});
            skArc(sketch, "E2399", {"start": v(-1.87, -22.5) * mm, "mid": v(-1.57, -22.26) * mm, "end": v(-1.32, -22.54) * mm});
            skLineSegment(sketch, "E2400", {"start": v(-1.32, -22.54) * mm, "end": v(-1.3, -22.6) * mm});
            skLineSegment(sketch, "E2401", {"start": v(-1.3, -22.6) * mm, "end": v(-1.3, -22.7) * mm});
            skLineSegment(sketch, "E2402", {"start": v(-1.3, -22.7) * mm, "end": v(-1.27, -22.8) * mm});
            skLineSegment(sketch, "E2403", {"start": v(-1.27, -22.8) * mm, "end": v(-1.26, -22.84) * mm});
            skLineSegment(sketch, "E2404", {"start": v(-1.26, -22.84) * mm, "end": v(-1.25, -22.9) * mm});
            skLineSegment(sketch, "E2405", {"start": v(-1.25, -22.9) * mm, "end": v(-1.24, -22.95) * mm});
            skLineSegment(sketch, "E2406", {"start": v(-1.24, -22.95) * mm, "end": v(-1.22, -23) * mm});
            skLineSegment(sketch, "E2407", {"start": v(-1.22, -23) * mm, "end": v(-1.2, -23.07) * mm});
            skLineSegment(sketch, "E2408", {"start": v(-1.2, -23.07) * mm, "end": v(-1.2, -23.13) * mm});
            skLineSegment(sketch, "E2409", {"start": v(-1.2, -23.13) * mm, "end": v(-1.18, -23.19) * mm});
            skLineSegment(sketch, "E2410", {"start": v(-1.18, -23.19) * mm, "end": v(-1.16, -23.25) * mm});
            skLineSegment(sketch, "E2411", {"start": v(-1.16, -23.25) * mm, "end": v(-1.14, -23.31) * mm});
            skLineSegment(sketch, "E2412", {"start": v(-1.14, -23.31) * mm, "end": v(-1.12, -23.38) * mm});
            skLineSegment(sketch, "E2413", {"start": v(-1.12, -23.38) * mm, "end": v(-1.1, -23.44) * mm});
            skLineSegment(sketch, "E2414", {"start": v(-1.1, -23.44) * mm, "end": v(-1.08, -23.51) * mm});
            skLineSegment(sketch, "E2415", {"start": v(-1.08, -23.51) * mm, "end": v(-1.06, -23.58) * mm});
            skLineSegment(sketch, "E2416", {"start": v(-1.06, -23.58) * mm, "end": v(-1.03, -23.65) * mm});
            skLineSegment(sketch, "E2417", {"start": v(-1.03, -23.65) * mm, "end": v(-1, -23.72) * mm});
            skLineSegment(sketch, "E2418", {"start": v(-1, -23.72) * mm, "end": v(-0.98, -23.8) * mm});
            skLineSegment(sketch, "E2419", {"start": v(-0.98, -23.8) * mm, "end": v(-0.95, -23.87) * mm});
            skLineSegment(sketch, "E2420", {"start": v(-0.95, -23.87) * mm, "end": v(-0.92, -23.95) * mm});
            skLineSegment(sketch, "E2421", {"start": v(-0.92, -23.95) * mm, "end": v(-0.9, -24.03) * mm});
            skLineSegment(sketch, "E2422", {"start": v(-0.9, -24.03) * mm, "end": v(-0.85, -24.14) * mm});
            skLineSegment(sketch, "E2423", {"start": v(-0.85, -24.14) * mm, "end": v(-0.3, -24.15) * mm});
            skLineSegment(sketch, "E2424", {"start": v(-0.3, -24.15) * mm, "end": v(-0.25, -24.04) * mm});
            skLineSegment(sketch, "E2425", {"start": v(-0.25, -24.04) * mm, "end": v(-0.21, -23.96) * mm});
            skLineSegment(sketch, "E2426", {"start": v(-0.21, -23.96) * mm, "end": v(-0.18, -23.9) * mm});
            skLineSegment(sketch, "E2427", {"start": v(-0.18, -23.9) * mm, "end": v(-0.15, -23.82) * mm});
            skLineSegment(sketch, "E2428", {"start": v(-0.15, -23.82) * mm, "end": v(-0.12, -23.74) * mm});
            skLineSegment(sketch, "E2429", {"start": v(-0.12, -23.74) * mm, "end": v(-0.1, -23.67) * mm});
            skLineSegment(sketch, "E2430", {"start": v(-0.1, -23.67) * mm, "end": v(-0.06, -23.6) * mm});
            skLineSegment(sketch, "E2431", {"start": v(-0.06, -23.6) * mm, "end": v(-0.04, -23.54) * mm});
            skLineSegment(sketch, "E2432", {"start": v(-0.04, -23.54) * mm, "end": v(-0.01, -23.47) * mm});
            skLineSegment(sketch, "E2433", {"start": v(-0.01, -23.47) * mm, "end": v(0, -23.4) * mm});
            skLineSegment(sketch, "E2434", {"start": v(0, -23.4) * mm, "end": v(0.03, -23.34) * mm});
            skLineSegment(sketch, "E2435", {"start": v(0.03, -23.34) * mm, "end": v(0.05, -23.28) * mm});
            skLineSegment(sketch, "E2436", {"start": v(0.05, -23.28) * mm, "end": v(0.07, -23.22) * mm});
            skLineSegment(sketch, "E2437", {"start": v(0.07, -23.22) * mm, "end": v(0.1, -23.16) * mm});
            skLineSegment(sketch, "E2438", {"start": v(0.1, -23.16) * mm, "end": v(0.11, -23.1) * mm});
            skLineSegment(sketch, "E2439", {"start": v(0.11, -23.1) * mm, "end": v(0.13, -23.04) * mm});
            skLineSegment(sketch, "E2440", {"start": v(0.13, -23.04) * mm, "end": v(0.15, -22.98) * mm});
            skLineSegment(sketch, "E2441", {"start": v(0.15, -22.98) * mm, "end": v(0.16, -22.93) * mm});
            skLineSegment(sketch, "E2442", {"start": v(0.16, -22.93) * mm, "end": v(0.18, -22.88) * mm});
            skLineSegment(sketch, "E2443", {"start": v(0.18, -22.88) * mm, "end": v(0.19, -22.83) * mm});
            skLineSegment(sketch, "E2444", {"start": v(0.19, -22.83) * mm, "end": v(0.21, -22.73) * mm});
            skLineSegment(sketch, "E2445", {"start": v(0.21, -22.73) * mm, "end": v(0.24, -22.64) * mm});
            skLineSegment(sketch, "E2446", {"start": v(0.24, -22.64) * mm, "end": v(0.25, -22.57) * mm});
            skArc(sketch, "E2447", {"start": v(0.25, -22.57) * mm, "mid": v(0.52, -22.3) * mm, "end": v(0.8, -22.56) * mm});
            skLineSegment(sketch, "E2448", {"start": v(0.8, -22.56) * mm, "end": v(0.81, -22.62) * mm});
            skLineSegment(sketch, "E2449", {"start": v(0.81, -22.62) * mm, "end": v(0.84, -22.71) * mm});
            skLineSegment(sketch, "E2450", {"start": v(0.84, -22.71) * mm, "end": v(0.87, -22.81) * mm});
            skLineSegment(sketch, "E2451", {"start": v(0.87, -22.81) * mm, "end": v(0.88, -22.86) * mm});
            skLineSegment(sketch, "E2452", {"start": v(0.88, -22.86) * mm, "end": v(0.9, -22.91) * mm});
            skLineSegment(sketch, "E2453", {"start": v(0.9, -22.91) * mm, "end": v(0.92, -22.97) * mm});
            skLineSegment(sketch, "E2454", {"start": v(0.92, -22.97) * mm, "end": v(0.94, -23.02) * mm});
            skLineSegment(sketch, "E2455", {"start": v(0.94, -23.02) * mm, "end": v(0.96, -23.08) * mm});
            skLineSegment(sketch, "E2456", {"start": v(0.96, -23.08) * mm, "end": v(0.98, -23.14) * mm});
            skLineSegment(sketch, "E2457", {"start": v(0.98, -23.14) * mm, "end": v(1, -23.2) * mm});
            skLineSegment(sketch, "E2458", {"start": v(1, -23.2) * mm, "end": v(1.02, -23.25) * mm});
            skLineSegment(sketch, "E2459", {"start": v(1.02, -23.25) * mm, "end": v(1.05, -23.32) * mm});
            skLineSegment(sketch, "E2460", {"start": v(1.05, -23.32) * mm, "end": v(1.07, -23.38) * mm});
            skLineSegment(sketch, "E2461", {"start": v(1.07, -23.38) * mm, "end": v(1.1, -23.44) * mm});
            skLineSegment(sketch, "E2462", {"start": v(1.1, -23.44) * mm, "end": v(1.13, -23.5) * mm});
            skLineSegment(sketch, "E2463", {"start": v(1.13, -23.5) * mm, "end": v(1.16, -23.58) * mm});
            skLineSegment(sketch, "E2464", {"start": v(1.16, -23.58) * mm, "end": v(1.19, -23.64) * mm});
            skLineSegment(sketch, "E2465", {"start": v(1.19, -23.64) * mm, "end": v(1.22, -23.71) * mm});
            skLineSegment(sketch, "E2466", {"start": v(1.22, -23.71) * mm, "end": v(1.25, -23.78) * mm});
            skLineSegment(sketch, "E2467", {"start": v(1.25, -23.78) * mm, "end": v(1.29, -23.86) * mm});
            skLineSegment(sketch, "E2468", {"start": v(1.29, -23.86) * mm, "end": v(1.32, -23.93) * mm});
            skLineSegment(sketch, "E2469", {"start": v(1.32, -23.93) * mm, "end": v(1.36, -24) * mm});
            skLineSegment(sketch, "E2470", {"start": v(1.36, -24) * mm, "end": v(1.41, -24.1) * mm});
            skLineSegment(sketch, "E2471", {"start": v(1.41, -24.1) * mm, "end": v(1.97, -24.07) * mm});
            skLineSegment(sketch, "E2472", {"start": v(1.97, -24.07) * mm, "end": v(2, -23.96) * mm});
            skLineSegment(sketch, "E2473", {"start": v(2, -23.96) * mm, "end": v(2.03, -23.88) * mm});
            skLineSegment(sketch, "E2474", {"start": v(2.03, -23.88) * mm, "end": v(2.06, -23.8) * mm});
            skLineSegment(sketch, "E2475", {"start": v(2.06, -23.8) * mm, "end": v(2.08, -23.73) * mm});
            skLineSegment(sketch, "E2476", {"start": v(2.08, -23.73) * mm, "end": v(2.1, -23.65) * mm});
            skLineSegment(sketch, "E2477", {"start": v(2.1, -23.65) * mm, "end": v(2.13, -23.58) * mm});
            skLineSegment(sketch, "E2478", {"start": v(2.13, -23.58) * mm, "end": v(2.15, -23.5) * mm});
            skLineSegment(sketch, "E2479", {"start": v(2.15, -23.5) * mm, "end": v(2.17, -23.44) * mm});
            skLineSegment(sketch, "E2480", {"start": v(2.17, -23.44) * mm, "end": v(2.18, -23.37) * mm});
            skLineSegment(sketch, "E2481", {"start": v(2.18, -23.37) * mm, "end": v(2.2, -23.3) * mm});
            skLineSegment(sketch, "E2482", {"start": v(2.2, -23.3) * mm, "end": v(2.22, -23.23) * mm});
            skLineSegment(sketch, "E2483", {"start": v(2.22, -23.23) * mm, "end": v(2.23, -23.17) * mm});
            skLineSegment(sketch, "E2484", {"start": v(2.23, -23.17) * mm, "end": v(2.25, -23.1) * mm});
            skLineSegment(sketch, "E2485", {"start": v(2.25, -23.1) * mm, "end": v(2.26, -23.04) * mm});
            skLineSegment(sketch, "E2486", {"start": v(2.26, -23.04) * mm, "end": v(2.27, -22.98) * mm});
            skLineSegment(sketch, "E2487", {"start": v(2.27, -22.98) * mm, "end": v(2.29, -22.93) * mm});
            skLineSegment(sketch, "E2488", {"start": v(2.29, -22.93) * mm, "end": v(2.3, -22.87) * mm});
            skLineSegment(sketch, "E2489", {"start": v(2.3, -22.87) * mm, "end": v(2.3, -22.81) * mm});
            skLineSegment(sketch, "E2490", {"start": v(2.3, -22.81) * mm, "end": v(2.32, -22.76) * mm});
            skLineSegment(sketch, "E2491", {"start": v(2.32, -22.76) * mm, "end": v(2.33, -22.7) * mm});
            skLineSegment(sketch, "E2492", {"start": v(2.33, -22.7) * mm, "end": v(2.34, -22.6) * mm});
            skLineSegment(sketch, "E2493", {"start": v(2.34, -22.6) * mm, "end": v(2.35, -22.52) * mm});
            skLineSegment(sketch, "E2494", {"start": v(2.35, -22.52) * mm, "end": v(2.36, -22.45) * mm});
            skArc(sketch, "E2495", {"start": v(2.36, -22.45) * mm, "mid": v(2.6, -22.16) * mm, "end": v(2.9, -22.39) * mm});
            skLineSegment(sketch, "E2496", {"start": v(2.9, -22.39) * mm, "end": v(2.93, -22.45) * mm});
            skLineSegment(sketch, "E2497", {"start": v(2.93, -22.45) * mm, "end": v(2.96, -22.54) * mm});
            skLineSegment(sketch, "E2498", {"start": v(2.96, -22.54) * mm, "end": v(3, -22.63) * mm});
            skLineSegment(sketch, "E2499", {"start": v(3, -22.63) * mm, "end": v(3.02, -22.68) * mm});
            skLineSegment(sketch, "E2500", {"start": v(3.02, -22.68) * mm, "end": v(3.04, -22.73) * mm});
            skLineSegment(sketch, "E2501", {"start": v(3.04, -22.73) * mm, "end": v(3.06, -22.78) * mm});
            skLineSegment(sketch, "E2502", {"start": v(3.06, -22.78) * mm, "end": v(3.09, -22.83) * mm});
            skLineSegment(sketch, "E2503", {"start": v(3.09, -22.83) * mm, "end": v(3.11, -22.89) * mm});
            skLineSegment(sketch, "E2504", {"start": v(3.11, -22.89) * mm, "end": v(3.14, -22.94) * mm});
            skLineSegment(sketch, "E2505", {"start": v(3.14, -22.94) * mm, "end": v(3.17, -23) * mm});
            skLineSegment(sketch, "E2506", {"start": v(3.17, -23) * mm, "end": v(3.2, -23.06) * mm});
            skLineSegment(sketch, "E2507", {"start": v(3.2, -23.06) * mm, "end": v(3.23, -23.11) * mm});
            skLineSegment(sketch, "E2508", {"start": v(3.23, -23.11) * mm, "end": v(3.26, -23.17) * mm});
            skLineSegment(sketch, "E2509", {"start": v(3.26, -23.17) * mm, "end": v(3.3, -23.24) * mm});
            skLineSegment(sketch, "E2510", {"start": v(3.3, -23.24) * mm, "end": v(3.32, -23.3) * mm});
            skLineSegment(sketch, "E2511", {"start": v(3.32, -23.3) * mm, "end": v(3.36, -23.36) * mm});
            skLineSegment(sketch, "E2512", {"start": v(3.36, -23.36) * mm, "end": v(3.4, -23.43) * mm});
            skLineSegment(sketch, "E2513", {"start": v(3.4, -23.43) * mm, "end": v(3.43, -23.5) * mm});
            skLineSegment(sketch, "E2514", {"start": v(3.43, -23.5) * mm, "end": v(3.47, -23.56) * mm});
            skLineSegment(sketch, "E2515", {"start": v(3.47, -23.56) * mm, "end": v(3.52, -23.63) * mm});
            skLineSegment(sketch, "E2516", {"start": v(3.52, -23.63) * mm, "end": v(3.56, -23.7) * mm});
            skLineSegment(sketch, "E2517", {"start": v(3.56, -23.7) * mm, "end": v(3.6, -23.77) * mm});
            skLineSegment(sketch, "E2518", {"start": v(3.6, -23.77) * mm, "end": v(3.67, -23.87) * mm});
            skLineSegment(sketch, "E2519", {"start": v(3.67, -23.87) * mm, "end": v(4.21, -23.78) * mm});
            skLineSegment(sketch, "E2520", {"start": v(4.21, -23.78) * mm, "end": v(4.24, -23.66) * mm});
            skLineSegment(sketch, "E2521", {"start": v(4.24, -23.66) * mm, "end": v(4.26, -23.58) * mm});
            skLineSegment(sketch, "E2522", {"start": v(4.26, -23.58) * mm, "end": v(4.28, -23.5) * mm});
            skLineSegment(sketch, "E2523", {"start": v(4.28, -23.5) * mm, "end": v(4.3, -23.43) * mm});
            skLineSegment(sketch, "E2524", {"start": v(4.3, -23.43) * mm, "end": v(4.3, -23.35) * mm});
            skLineSegment(sketch, "E2525", {"start": v(4.3, -23.35) * mm, "end": v(4.32, -23.27) * mm});
            skLineSegment(sketch, "E2526", {"start": v(4.32, -23.27) * mm, "end": v(4.34, -23.2) * mm});
            skLineSegment(sketch, "E2527", {"start": v(4.34, -23.2) * mm, "end": v(4.35, -23.13) * mm});
            skLineSegment(sketch, "E2528", {"start": v(4.35, -23.13) * mm, "end": v(4.36, -23.06) * mm});
            skLineSegment(sketch, "E2529", {"start": v(4.36, -23.06) * mm, "end": v(4.37, -23) * mm});
            skLineSegment(sketch, "E2530", {"start": v(4.37, -23) * mm, "end": v(4.38, -22.92) * mm});
            skLineSegment(sketch, "E2531", {"start": v(4.38, -22.92) * mm, "end": v(4.4, -22.86) * mm});
            skLineSegment(sketch, "E2532", {"start": v(4.4, -22.86) * mm, "end": v(4.4, -22.8) * mm});
            skLineSegment(sketch, "E2533", {"start": v(4.4, -22.8) * mm, "end": v(4.4, -22.73) * mm});
            skLineSegment(sketch, "E2534", {"start": v(4.4, -22.73) * mm, "end": v(4.42, -22.67) * mm});
            skLineSegment(sketch, "E2535", {"start": v(4.42, -22.67) * mm, "end": v(4.42, -22.61) * mm});
            skLineSegment(sketch, "E2536", {"start": v(4.42, -22.61) * mm, "end": v(4.43, -22.55) * mm});
            skLineSegment(sketch, "E2537", {"start": v(4.43, -22.55) * mm, "end": v(4.43, -22.5) * mm});
            skLineSegment(sketch, "E2538", {"start": v(4.43, -22.5) * mm, "end": v(4.44, -22.44) * mm});
            skLineSegment(sketch, "E2539", {"start": v(4.44, -22.44) * mm, "end": v(4.44, -22.4) * mm});
            skLineSegment(sketch, "E2540", {"start": v(4.44, -22.4) * mm, "end": v(4.45, -22.29) * mm});
            skLineSegment(sketch, "E2541", {"start": v(4.45, -22.29) * mm, "end": v(4.45, -22.2) * mm});
            skLineSegment(sketch, "E2542", {"start": v(4.45, -22.2) * mm, "end": v(4.45, -22.13) * mm});
            skArc(sketch, "E2543", {"start": v(4.45, -22.13) * mm, "mid": v(4.67, -21.82) * mm, "end": v(4.99, -22.02) * mm});
            skLineSegment(sketch, "E2544", {"start": v(4.99, -22.02) * mm, "end": v(5.02, -22.07) * mm});
            skLineSegment(sketch, "E2545", {"start": v(5.02, -22.07) * mm, "end": v(5.06, -22.16) * mm});
            skLineSegment(sketch, "E2546", {"start": v(5.06, -22.16) * mm, "end": v(5.1, -22.25) * mm});
            skLineSegment(sketch, "E2547", {"start": v(5.1, -22.25) * mm, "end": v(5.13, -22.3) * mm});
            skLineSegment(sketch, "E2548", {"start": v(5.13, -22.3) * mm, "end": v(5.16, -22.34) * mm});
            skLineSegment(sketch, "E2549", {"start": v(5.16, -22.34) * mm, "end": v(5.18, -22.4) * mm});
            skLineSegment(sketch, "E2550", {"start": v(5.18, -22.4) * mm, "end": v(5.21, -22.44) * mm});
            skLineSegment(sketch, "E2551", {"start": v(5.21, -22.44) * mm, "end": v(5.24, -22.5) * mm});
            skLineSegment(sketch, "E2552", {"start": v(5.24, -22.5) * mm, "end": v(5.27, -22.55) * mm});
            skLineSegment(sketch, "E2553", {"start": v(5.27, -22.55) * mm, "end": v(5.3, -22.6) * mm});
            skLineSegment(sketch, "E2554", {"start": v(5.3, -22.6) * mm, "end": v(5.34, -22.65) * mm});
            skLineSegment(sketch, "E2555", {"start": v(5.34, -22.65) * mm, "end": v(5.38, -22.71) * mm});
            skLineSegment(sketch, "E2556", {"start": v(5.38, -22.71) * mm, "end": v(5.41, -22.77) * mm});
            skLineSegment(sketch, "E2557", {"start": v(5.41, -22.77) * mm, "end": v(5.45, -22.83) * mm});
            skLineSegment(sketch, "E2558", {"start": v(5.45, -22.83) * mm, "end": v(5.5, -22.88) * mm});
            skLineSegment(sketch, "E2559", {"start": v(5.5, -22.88) * mm, "end": v(5.53, -22.95) * mm});
            skLineSegment(sketch, "E2560", {"start": v(5.53, -22.95) * mm, "end": v(5.58, -23) * mm});
            skLineSegment(sketch, "E2561", {"start": v(5.58, -23) * mm, "end": v(5.62, -23.07) * mm});
            skLineSegment(sketch, "E2562", {"start": v(5.62, -23.07) * mm, "end": v(5.67, -23.13) * mm});
            skLineSegment(sketch, "E2563", {"start": v(5.67, -23.13) * mm, "end": v(5.71, -23.2) * mm});
            skLineSegment(sketch, "E2564", {"start": v(5.71, -23.2) * mm, "end": v(5.76, -23.26) * mm});
            skLineSegment(sketch, "E2565", {"start": v(5.76, -23.26) * mm, "end": v(5.81, -23.33) * mm});
            skLineSegment(sketch, "E2566", {"start": v(5.81, -23.33) * mm, "end": v(5.88, -23.42) * mm});
            skLineSegment(sketch, "E2567", {"start": v(5.88, -23.42) * mm, "end": v(6.42, -23.28) * mm});
            skLineSegment(sketch, "E2568", {"start": v(6.42, -23.28) * mm, "end": v(6.44, -23.16) * mm});
            skLineSegment(sketch, "E2569", {"start": v(6.44, -23.16) * mm, "end": v(6.45, -23.08) * mm});
            skLineSegment(sketch, "E2570", {"start": v(6.45, -23.08) * mm, "end": v(6.46, -23) * mm});
            skLineSegment(sketch, "E2571", {"start": v(6.46, -23) * mm, "end": v(6.47, -22.92) * mm});
            skLineSegment(sketch, "E2572", {"start": v(6.47, -22.92) * mm, "end": v(6.48, -22.84) * mm});
            skLineSegment(sketch, "E2573", {"start": v(6.48, -22.84) * mm, "end": v(6.48, -22.77) * mm});
            skLineSegment(sketch, "E2574", {"start": v(6.48, -22.77) * mm, "end": v(6.5, -22.7) * mm});
            skLineSegment(sketch, "E2575", {"start": v(6.5, -22.7) * mm, "end": v(6.5, -22.62) * mm});
            skLineSegment(sketch, "E2576", {"start": v(6.5, -22.62) * mm, "end": v(6.5, -22.55) * mm});
            skLineSegment(sketch, "E2577", {"start": v(6.5, -22.55) * mm, "end": v(6.5, -22.48) * mm});
            skLineSegment(sketch, "E2578", {"start": v(6.5, -22.48) * mm, "end": v(6.51, -22.41) * mm});
            skLineSegment(sketch, "E2579", {"start": v(6.51, -22.41) * mm, "end": v(6.51, -22.34) * mm});
            skLineSegment(sketch, "E2580", {"start": v(6.51, -22.34) * mm, "end": v(6.52, -22.28) * mm});
            skLineSegment(sketch, "E2581", {"start": v(6.52, -22.28) * mm, "end": v(6.52, -22.22) * mm});
            skLineSegment(sketch, "E2582", {"start": v(6.52, -22.22) * mm, "end": v(6.52, -22.16) * mm});
            skLineSegment(sketch, "E2583", {"start": v(6.52, -22.16) * mm, "end": v(6.52, -22.1) * mm});
            skLineSegment(sketch, "E2584", {"start": v(6.52, -22.1) * mm, "end": v(6.52, -22.04) * mm});
            skLineSegment(sketch, "E2585", {"start": v(6.52, -22.04) * mm, "end": v(6.52, -21.98) * mm});
            skLineSegment(sketch, "E2586", {"start": v(6.52, -21.98) * mm, "end": v(6.52, -21.93) * mm});
            skLineSegment(sketch, "E2587", {"start": v(6.52, -21.93) * mm, "end": v(6.52, -21.88) * mm});
            skLineSegment(sketch, "E2588", {"start": v(6.52, -21.88) * mm, "end": v(6.52, -21.77) * mm});
            skLineSegment(sketch, "E2589", {"start": v(6.52, -21.77) * mm, "end": v(6.51, -21.68) * mm});
            skLineSegment(sketch, "E2590", {"start": v(6.51, -21.68) * mm, "end": v(6.5, -21.61) * mm});
            skArc(sketch, "E2591", {"start": v(6.5, -21.61) * mm, "mid": v(6.69, -21.28) * mm, "end": v(7.03, -21.45) * mm});
            skLineSegment(sketch, "E2592", {"start": v(7.03, -21.45) * mm, "end": v(7.06, -21.5) * mm});
            skLineSegment(sketch, "E2593", {"start": v(7.06, -21.5) * mm, "end": v(7.11, -21.59) * mm});
            skLineSegment(sketch, "E2594", {"start": v(7.11, -21.59) * mm, "end": v(7.17, -21.67) * mm});
            skLineSegment(sketch, "E2595", {"start": v(7.17, -21.67) * mm, "end": v(7.2, -21.72) * mm});
            skLineSegment(sketch, "E2596", {"start": v(7.2, -21.72) * mm, "end": v(7.23, -21.76) * mm});
            skLineSegment(sketch, "E2597", {"start": v(7.23, -21.76) * mm, "end": v(7.26, -21.8) * mm});
            skLineSegment(sketch, "E2598", {"start": v(7.26, -21.8) * mm, "end": v(7.3, -21.85) * mm});
            skLineSegment(sketch, "E2599", {"start": v(7.3, -21.85) * mm, "end": v(7.33, -21.9) * mm});
            skLineSegment(sketch, "E2600", {"start": v(7.33, -21.9) * mm, "end": v(7.36, -21.95) * mm});
            skLineSegment(sketch, "E2601", {"start": v(7.36, -21.95) * mm, "end": v(7.4, -22) * mm});
            skLineSegment(sketch, "E2602", {"start": v(7.4, -22) * mm, "end": v(7.44, -22.05) * mm});
            skLineSegment(sketch, "E2603", {"start": v(7.44, -22.05) * mm, "end": v(7.48, -22.1) * mm});
            skLineSegment(sketch, "E2604", {"start": v(7.48, -22.1) * mm, "end": v(7.52, -22.16) * mm});
            skLineSegment(sketch, "E2605", {"start": v(7.52, -22.16) * mm, "end": v(7.57, -22.21) * mm});
            skLineSegment(sketch, "E2606", {"start": v(7.57, -22.21) * mm, "end": v(7.61, -22.27) * mm});
            skLineSegment(sketch, "E2607", {"start": v(7.61, -22.27) * mm, "end": v(7.66, -22.33) * mm});
            skLineSegment(sketch, "E2608", {"start": v(7.66, -22.33) * mm, "end": v(7.7, -22.38) * mm});
            skLineSegment(sketch, "E2609", {"start": v(7.7, -22.38) * mm, "end": v(7.76, -22.44) * mm});
            skLineSegment(sketch, "E2610", {"start": v(7.76, -22.44) * mm, "end": v(7.8, -22.5) * mm});
            skLineSegment(sketch, "E2611", {"start": v(7.8, -22.5) * mm, "end": v(7.86, -22.56) * mm});
            skLineSegment(sketch, "E2612", {"start": v(7.86, -22.56) * mm, "end": v(7.91, -22.62) * mm});
            skLineSegment(sketch, "E2613", {"start": v(7.91, -22.62) * mm, "end": v(7.97, -22.68) * mm});
            skLineSegment(sketch, "E2614", {"start": v(7.97, -22.68) * mm, "end": v(8.05, -22.77) * mm});
            skLineSegment(sketch, "E2615", {"start": v(8.05, -22.77) * mm, "end": v(8.57, -22.58) * mm});
            skLineSegment(sketch, "E2616", {"start": v(8.57, -22.58) * mm, "end": v(8.58, -22.46) * mm});
            skLineSegment(sketch, "E2617", {"start": v(8.58, -22.46) * mm, "end": v(8.58, -22.37) * mm});
            skLineSegment(sketch, "E2618", {"start": v(8.58, -22.37) * mm, "end": v(8.58, -22.3) * mm});
            skLineSegment(sketch, "E2619", {"start": v(8.58, -22.3) * mm, "end": v(8.59, -22.21) * mm});
            skLineSegment(sketch, "E2620", {"start": v(8.59, -22.21) * mm, "end": v(8.59, -22.14) * mm});
            skLineSegment(sketch, "E2621", {"start": v(8.59, -22.14) * mm, "end": v(8.59, -22.06) * mm});
            skLineSegment(sketch, "E2622", {"start": v(8.59, -22.06) * mm, "end": v(8.59, -21.98) * mm});
            skLineSegment(sketch, "E2623", {"start": v(8.59, -21.98) * mm, "end": v(8.59, -21.91) * mm});
            skLineSegment(sketch, "E2624", {"start": v(8.59, -21.91) * mm, "end": v(8.59, -21.84) * mm});
            skLineSegment(sketch, "E2625", {"start": v(8.59, -21.84) * mm, "end": v(8.58, -21.77) * mm});
            skLineSegment(sketch, "E2626", {"start": v(8.58, -21.77) * mm, "end": v(8.58, -21.7) * mm});
            skLineSegment(sketch, "E2627", {"start": v(8.58, -21.7) * mm, "end": v(8.58, -21.64) * mm});
            skLineSegment(sketch, "E2628", {"start": v(8.58, -21.64) * mm, "end": v(8.57, -21.57) * mm});
            skLineSegment(sketch, "E2629", {"start": v(8.57, -21.57) * mm, "end": v(8.57, -21.5) * mm});
            skLineSegment(sketch, "E2630", {"start": v(8.57, -21.5) * mm, "end": v(8.57, -21.45) * mm});
            skLineSegment(sketch, "E2631", {"start": v(8.57, -21.45) * mm, "end": v(8.56, -21.39) * mm});
            skLineSegment(sketch, "E2632", {"start": v(8.56, -21.39) * mm, "end": v(8.56, -21.33) * mm});
            skLineSegment(sketch, "E2633", {"start": v(8.56, -21.33) * mm, "end": v(8.55, -21.27) * mm});
            skLineSegment(sketch, "E2634", {"start": v(8.55, -21.27) * mm, "end": v(8.54, -21.22) * mm});
            skLineSegment(sketch, "E2635", {"start": v(8.54, -21.22) * mm, "end": v(8.54, -21.17) * mm});
            skLineSegment(sketch, "E2636", {"start": v(8.54, -21.17) * mm, "end": v(8.53, -21.07) * mm});
            skLineSegment(sketch, "E2637", {"start": v(8.53, -21.07) * mm, "end": v(8.51, -20.98) * mm});
            skLineSegment(sketch, "E2638", {"start": v(8.51, -20.98) * mm, "end": v(8.5, -20.91) * mm});
            skArc(sketch, "E2639", {"start": v(8.5, -20.91) * mm, "mid": v(8.65, -20.56) * mm, "end": v(9, -20.7) * mm});
            skLineSegment(sketch, "E2640", {"start": v(9, -20.7) * mm, "end": v(9.04, -20.75) * mm});
            skLineSegment(sketch, "E2641", {"start": v(9.04, -20.75) * mm, "end": v(9.1, -20.83) * mm});
            skLineSegment(sketch, "E2642", {"start": v(9.1, -20.83) * mm, "end": v(9.16, -20.9) * mm});
            skLineSegment(sketch, "E2643", {"start": v(9.16, -20.9) * mm, "end": v(9.2, -20.95) * mm});
            skLineSegment(sketch, "E2644", {"start": v(9.2, -20.95) * mm, "end": v(9.23, -20.99) * mm});
            skLineSegment(sketch, "E2645", {"start": v(9.23, -20.99) * mm, "end": v(9.27, -21.03) * mm});
            skLineSegment(sketch, "E2646", {"start": v(9.27, -21.03) * mm, "end": v(9.3, -21.07) * mm});
            skLineSegment(sketch, "E2647", {"start": v(9.3, -21.07) * mm, "end": v(9.35, -21.12) * mm});
            skLineSegment(sketch, "E2648", {"start": v(9.35, -21.12) * mm, "end": v(9.39, -21.17) * mm});
            skLineSegment(sketch, "E2649", {"start": v(9.39, -21.17) * mm, "end": v(9.43, -21.21) * mm});
            skLineSegment(sketch, "E2650", {"start": v(9.43, -21.21) * mm, "end": v(9.47, -21.26) * mm});
            skLineSegment(sketch, "E2651", {"start": v(9.47, -21.26) * mm, "end": v(9.52, -21.3) * mm});
            skLineSegment(sketch, "E2652", {"start": v(9.52, -21.3) * mm, "end": v(9.56, -21.36) * mm});
            skLineSegment(sketch, "E2653", {"start": v(9.56, -21.36) * mm, "end": v(9.61, -21.4) * mm});
            skLineSegment(sketch, "E2654", {"start": v(9.61, -21.4) * mm, "end": v(9.66, -21.46) * mm});
            skLineSegment(sketch, "E2655", {"start": v(9.66, -21.46) * mm, "end": v(9.71, -21.5) * mm});
            skLineSegment(sketch, "E2656", {"start": v(9.71, -21.5) * mm, "end": v(9.77, -21.56) * mm});
            skLineSegment(sketch, "E2657", {"start": v(9.77, -21.56) * mm, "end": v(9.82, -21.61) * mm});
            skLineSegment(sketch, "E2658", {"start": v(9.82, -21.61) * mm, "end": v(9.88, -21.67) * mm});
            skLineSegment(sketch, "E2659", {"start": v(9.88, -21.67) * mm, "end": v(9.94, -21.72) * mm});
            skLineSegment(sketch, "E2660", {"start": v(9.94, -21.72) * mm, "end": v(10, -21.78) * mm});
            skLineSegment(sketch, "E2661", {"start": v(10, -21.78) * mm, "end": v(10.06, -21.83) * mm});
            skLineSegment(sketch, "E2662", {"start": v(10.06, -21.83) * mm, "end": v(10.15, -21.91) * mm});
            skLineSegment(sketch, "E2663", {"start": v(10.15, -21.91) * mm, "end": v(10.65, -21.67) * mm});
            skLineSegment(sketch, "E2664", {"start": v(10.65, -21.67) * mm, "end": v(10.64, -21.55) * mm});
            skLineSegment(sketch, "E2665", {"start": v(10.64, -21.55) * mm, "end": v(10.64, -21.47) * mm});
            skLineSegment(sketch, "E2666", {"start": v(10.64, -21.47) * mm, "end": v(10.63, -21.4) * mm});
            skLineSegment(sketch, "E2667", {"start": v(10.63, -21.4) * mm, "end": v(10.63, -21.31) * mm});
            skLineSegment(sketch, "E2668", {"start": v(10.63, -21.31) * mm, "end": v(10.62, -21.23) * mm});
            skLineSegment(sketch, "E2669", {"start": v(10.62, -21.23) * mm, "end": v(10.62, -21.16) * mm});
            skLineSegment(sketch, "E2670", {"start": v(10.62, -21.16) * mm, "end": v(10.6, -21.08) * mm});
            skLineSegment(sketch, "E2671", {"start": v(10.6, -21.08) * mm, "end": v(10.6, -21.01) * mm});
            skLineSegment(sketch, "E2672", {"start": v(10.6, -21.01) * mm, "end": v(10.6, -20.94) * mm});
            skLineSegment(sketch, "E2673", {"start": v(10.6, -20.94) * mm, "end": v(10.58, -20.87) * mm});
            skLineSegment(sketch, "E2674", {"start": v(10.58, -20.87) * mm, "end": v(10.58, -20.8) * mm});
            skLineSegment(sketch, "E2675", {"start": v(10.58, -20.8) * mm, "end": v(10.57, -20.74) * mm});
            skLineSegment(sketch, "E2676", {"start": v(10.57, -20.74) * mm, "end": v(10.56, -20.67) * mm});
            skLineSegment(sketch, "E2677", {"start": v(10.56, -20.67) * mm, "end": v(10.55, -20.61) * mm});
            skLineSegment(sketch, "E2678", {"start": v(10.55, -20.61) * mm, "end": v(10.54, -20.55) * mm});
            skLineSegment(sketch, "E2679", {"start": v(10.54, -20.55) * mm, "end": v(10.53, -20.5) * mm});
            skLineSegment(sketch, "E2680", {"start": v(10.53, -20.5) * mm, "end": v(10.52, -20.44) * mm});
            skLineSegment(sketch, "E2681", {"start": v(10.52, -20.44) * mm, "end": v(10.5, -20.38) * mm});
            skLineSegment(sketch, "E2682", {"start": v(10.5, -20.38) * mm, "end": v(10.5, -20.33) * mm});
            skLineSegment(sketch, "E2683", {"start": v(10.5, -20.33) * mm, "end": v(10.48, -20.27) * mm});
            skLineSegment(sketch, "E2684", {"start": v(10.48, -20.27) * mm, "end": v(10.46, -20.18) * mm});
            skLineSegment(sketch, "E2685", {"start": v(10.46, -20.18) * mm, "end": v(10.44, -20.09) * mm});
            skLineSegment(sketch, "E2686", {"start": v(10.44, -20.09) * mm, "end": v(10.42, -20.02) * mm});
            skArc(sketch, "E2687", {"start": v(10.42, -20.02) * mm, "mid": v(10.54, -19.66) * mm, "end": v(10.9, -19.76) * mm});
            skLineSegment(sketch, "E2688", {"start": v(10.9, -19.76) * mm, "end": v(10.95, -19.81) * mm});
            skLineSegment(sketch, "E2689", {"start": v(10.95, -19.81) * mm, "end": v(11.01, -19.88) * mm});
            skLineSegment(sketch, "E2690", {"start": v(11.01, -19.88) * mm, "end": v(11.08, -19.95) * mm});
            skLineSegment(sketch, "E2691", {"start": v(11.08, -19.95) * mm, "end": v(11.12, -20) * mm});
            skLineSegment(sketch, "E2692", {"start": v(11.12, -20) * mm, "end": v(11.16, -20.03) * mm});
            skLineSegment(sketch, "E2693", {"start": v(11.16, -20.03) * mm, "end": v(11.2, -20.07) * mm});
            skLineSegment(sketch, "E2694", {"start": v(11.2, -20.07) * mm, "end": v(11.24, -20.11) * mm});
            skLineSegment(sketch, "E2695", {"start": v(11.24, -20.11) * mm, "end": v(11.28, -20.15) * mm});
            skLineSegment(sketch, "E2696", {"start": v(11.28, -20.15) * mm, "end": v(11.33, -20.2) * mm});
            skLineSegment(sketch, "E2697", {"start": v(11.33, -20.2) * mm, "end": v(11.37, -20.24) * mm});
            skLineSegment(sketch, "E2698", {"start": v(11.37, -20.24) * mm, "end": v(11.42, -20.28) * mm});
            skLineSegment(sketch, "E2699", {"start": v(11.42, -20.28) * mm, "end": v(11.47, -20.32) * mm});
            skLineSegment(sketch, "E2700", {"start": v(11.47, -20.32) * mm, "end": v(11.52, -20.37) * mm});
            skLineSegment(sketch, "E2701", {"start": v(11.52, -20.37) * mm, "end": v(11.57, -20.41) * mm});
            skLineSegment(sketch, "E2702", {"start": v(11.57, -20.41) * mm, "end": v(11.63, -20.46) * mm});
            skLineSegment(sketch, "E2703", {"start": v(11.63, -20.46) * mm, "end": v(11.69, -20.5) * mm});
            skLineSegment(sketch, "E2704", {"start": v(11.69, -20.5) * mm, "end": v(11.74, -20.55) * mm});
            skLineSegment(sketch, "E2705", {"start": v(11.74, -20.55) * mm, "end": v(11.8, -20.6) * mm});
            skLineSegment(sketch, "E2706", {"start": v(11.8, -20.6) * mm, "end": v(11.86, -20.65) * mm});
            skLineSegment(sketch, "E2707", {"start": v(11.86, -20.65) * mm, "end": v(11.93, -20.7) * mm});
            skLineSegment(sketch, "E2708", {"start": v(11.93, -20.7) * mm, "end": v(12, -20.75) * mm});
            skLineSegment(sketch, "E2709", {"start": v(12, -20.75) * mm, "end": v(12.06, -20.8) * mm});
            skLineSegment(sketch, "E2710", {"start": v(12.06, -20.8) * mm, "end": v(12.16, -20.86) * mm});
            skLineSegment(sketch, "E2711", {"start": v(12.16, -20.86) * mm, "end": v(12.63, -20.58) * mm});
            skLineSegment(sketch, "E2712", {"start": v(12.63, -20.58) * mm, "end": v(12.61, -20.46) * mm});
            skLineSegment(sketch, "E2713", {"start": v(12.61, -20.46) * mm, "end": v(12.6, -20.38) * mm});
            skLineSegment(sketch, "E2714", {"start": v(12.6, -20.38) * mm, "end": v(12.59, -20.3) * mm});
            skLineSegment(sketch, "E2715", {"start": v(12.59, -20.3) * mm, "end": v(12.58, -20.22) * mm});
            skLineSegment(sketch, "E2716", {"start": v(12.58, -20.22) * mm, "end": v(12.56, -20.14) * mm});
            skLineSegment(sketch, "E2717", {"start": v(12.56, -20.14) * mm, "end": v(12.55, -20.07) * mm});
            skLineSegment(sketch, "E2718", {"start": v(12.55, -20.07) * mm, "end": v(12.54, -20) * mm});
            skLineSegment(sketch, "E2719", {"start": v(12.54, -20) * mm, "end": v(12.52, -19.92) * mm});
            skLineSegment(sketch, "E2720", {"start": v(12.52, -19.92) * mm, "end": v(12.5, -19.85) * mm});
            skLineSegment(sketch, "E2721", {"start": v(12.5, -19.85) * mm, "end": v(12.5, -19.79) * mm});
            skLineSegment(sketch, "E2722", {"start": v(12.5, -19.79) * mm, "end": v(12.48, -19.72) * mm});
            skLineSegment(sketch, "E2723", {"start": v(12.48, -19.72) * mm, "end": v(12.46, -19.66) * mm});
            skLineSegment(sketch, "E2724", {"start": v(12.46, -19.66) * mm, "end": v(12.45, -19.6) * mm});
            skLineSegment(sketch, "E2725", {"start": v(12.45, -19.6) * mm, "end": v(12.43, -19.53) * mm});
            skLineSegment(sketch, "E2726", {"start": v(12.43, -19.53) * mm, "end": v(12.41, -19.47) * mm});
            skLineSegment(sketch, "E2727", {"start": v(12.41, -19.47) * mm, "end": v(12.4, -19.42) * mm});
            skLineSegment(sketch, "E2728", {"start": v(12.4, -19.42) * mm, "end": v(12.38, -19.36) * mm});
            skLineSegment(sketch, "E2729", {"start": v(12.38, -19.36) * mm, "end": v(12.37, -19.3) * mm});
            skLineSegment(sketch, "E2730", {"start": v(12.37, -19.3) * mm, "end": v(12.35, -19.25) * mm});
            skLineSegment(sketch, "E2731", {"start": v(12.35, -19.25) * mm, "end": v(12.34, -19.2) * mm});
            skLineSegment(sketch, "E2732", {"start": v(12.34, -19.2) * mm, "end": v(12.3, -19.1) * mm});
            skLineSegment(sketch, "E2733", {"start": v(12.3, -19.1) * mm, "end": v(12.27, -19.02) * mm});
            skLineSegment(sketch, "E2734", {"start": v(12.27, -19.02) * mm, "end": v(12.25, -18.96) * mm});
            skArc(sketch, "E2735", {"start": v(12.25, -18.96) * mm, "mid": v(12.33, -18.59) * mm, "end": v(12.7, -18.65) * mm});
            skLineSegment(sketch, "E2736", {"start": v(12.7, -18.65) * mm, "end": v(12.76, -18.7) * mm});
            skLineSegment(sketch, "E2737", {"start": v(12.76, -18.7) * mm, "end": v(12.83, -18.76) * mm});
            skLineSegment(sketch, "E2738", {"start": v(12.83, -18.76) * mm, "end": v(12.9, -18.83) * mm});
            skLineSegment(sketch, "E2739", {"start": v(12.9, -18.83) * mm, "end": v(12.94, -18.86) * mm});
            skLineSegment(sketch, "E2740", {"start": v(12.94, -18.86) * mm, "end": v(12.98, -18.9) * mm});
            skLineSegment(sketch, "E2741", {"start": v(12.98, -18.9) * mm, "end": v(13.03, -18.93) * mm});
            skLineSegment(sketch, "E2742", {"start": v(13.03, -18.93) * mm, "end": v(13.07, -18.97) * mm});
            skLineSegment(sketch, "E2743", {"start": v(13.07, -18.97) * mm, "end": v(13.12, -19) * mm});
            skLineSegment(sketch, "E2744", {"start": v(13.12, -19) * mm, "end": v(13.17, -19.04) * mm});
            skLineSegment(sketch, "E2745", {"start": v(13.17, -19.04) * mm, "end": v(13.22, -19.08) * mm});
            skLineSegment(sketch, "E2746", {"start": v(13.22, -19.08) * mm, "end": v(13.27, -19.12) * mm});
            skLineSegment(sketch, "E2747", {"start": v(13.27, -19.12) * mm, "end": v(13.32, -19.16) * mm});
            skLineSegment(sketch, "E2748", {"start": v(13.32, -19.16) * mm, "end": v(13.38, -19.2) * mm});
            skLineSegment(sketch, "E2749", {"start": v(13.38, -19.2) * mm, "end": v(13.44, -19.24) * mm});
            skLineSegment(sketch, "E2750", {"start": v(13.44, -19.24) * mm, "end": v(13.5, -19.28) * mm});
            skLineSegment(sketch, "E2751", {"start": v(13.5, -19.28) * mm, "end": v(13.55, -19.32) * mm});
            skLineSegment(sketch, "E2752", {"start": v(13.55, -19.32) * mm, "end": v(13.62, -19.36) * mm});
            skLineSegment(sketch, "E2753", {"start": v(13.62, -19.36) * mm, "end": v(13.68, -19.4) * mm});
            skLineSegment(sketch, "E2754", {"start": v(13.68, -19.4) * mm, "end": v(13.75, -19.45) * mm});
            skLineSegment(sketch, "E2755", {"start": v(13.75, -19.45) * mm, "end": v(13.81, -19.49) * mm});
            skLineSegment(sketch, "E2756", {"start": v(13.81, -19.49) * mm, "end": v(13.88, -19.53) * mm});
            skLineSegment(sketch, "E2757", {"start": v(13.88, -19.53) * mm, "end": v(13.95, -19.57) * mm});
            skLineSegment(sketch, "E2758", {"start": v(13.95, -19.57) * mm, "end": v(14.06, -19.63) * mm});
            skLineSegment(sketch, "E2759", {"start": v(14.06, -19.63) * mm, "end": v(14.5, -19.3) * mm});
            skLineSegment(sketch, "E2760", {"start": v(14.5, -19.3) * mm, "end": v(14.48, -19.2) * mm});
            skLineSegment(sketch, "E2761", {"start": v(14.48, -19.2) * mm, "end": v(14.46, -19.11) * mm});
            skLineSegment(sketch, "E2762", {"start": v(14.46, -19.11) * mm, "end": v(14.44, -19.03) * mm});
            skLineSegment(sketch, "E2763", {"start": v(14.44, -19.03) * mm, "end": v(14.42, -18.95) * mm});
            skLineSegment(sketch, "E2764", {"start": v(14.42, -18.95) * mm, "end": v(14.4, -18.88) * mm});
            skLineSegment(sketch, "E2765", {"start": v(14.4, -18.88) * mm, "end": v(14.37, -18.8) * mm});
            skLineSegment(sketch, "E2766", {"start": v(14.37, -18.8) * mm, "end": v(14.35, -18.73) * mm});
            skLineSegment(sketch, "E2767", {"start": v(14.35, -18.73) * mm, "end": v(14.33, -18.66) * mm});
            skLineSegment(sketch, "E2768", {"start": v(14.33, -18.66) * mm, "end": v(14.31, -18.6) * mm});
            skLineSegment(sketch, "E2769", {"start": v(14.31, -18.6) * mm, "end": v(14.3, -18.53) * mm});
            skLineSegment(sketch, "E2770", {"start": v(14.3, -18.53) * mm, "end": v(14.27, -18.46) * mm});
            skLineSegment(sketch, "E2771", {"start": v(14.27, -18.46) * mm, "end": v(14.25, -18.4) * mm});
            skLineSegment(sketch, "E2772", {"start": v(14.25, -18.4) * mm, "end": v(14.23, -18.34) * mm});
            skLineSegment(sketch, "E2773", {"start": v(14.23, -18.34) * mm, "end": v(14.2, -18.28) * mm});
            skLineSegment(sketch, "E2774", {"start": v(14.2, -18.28) * mm, "end": v(14.18, -18.22) * mm});
            skLineSegment(sketch, "E2775", {"start": v(14.18, -18.22) * mm, "end": v(14.16, -18.17) * mm});
            skLineSegment(sketch, "E2776", {"start": v(14.16, -18.17) * mm, "end": v(14.14, -18.11) * mm});
            skLineSegment(sketch, "E2777", {"start": v(14.14, -18.11) * mm, "end": v(14.12, -18.06) * mm});
            skLineSegment(sketch, "E2778", {"start": v(14.12, -18.06) * mm, "end": v(14.1, -18.01) * mm});
            skLineSegment(sketch, "E2779", {"start": v(14.1, -18.01) * mm, "end": v(14.08, -17.96) * mm});
            skLineSegment(sketch, "E2780", {"start": v(14.08, -17.96) * mm, "end": v(14.04, -17.87) * mm});
            skLineSegment(sketch, "E2781", {"start": v(14.04, -17.87) * mm, "end": v(14, -17.79) * mm});
            skLineSegment(sketch, "E2782", {"start": v(14, -17.79) * mm, "end": v(13.97, -17.73) * mm});
            skArc(sketch, "E2783", {"start": v(13.97, -17.73) * mm, "mid": v(14.02, -17.35) * mm, "end": v(14.4, -17.38) * mm});
            skLineSegment(sketch, "E2784", {"start": v(14.4, -17.38) * mm, "end": v(14.45, -17.42) * mm});
            skLineSegment(sketch, "E2785", {"start": v(14.45, -17.42) * mm, "end": v(14.53, -17.48) * mm});
            skLineSegment(sketch, "E2786", {"start": v(14.53, -17.48) * mm, "end": v(14.6, -17.54) * mm});
            skLineSegment(sketch, "E2787", {"start": v(14.6, -17.54) * mm, "end": v(14.65, -17.57) * mm});
            skLineSegment(sketch, "E2788", {"start": v(14.65, -17.57) * mm, "end": v(14.7, -17.6) * mm});
            skLineSegment(sketch, "E2789", {"start": v(14.7, -17.6) * mm, "end": v(14.74, -17.63) * mm});
            skLineSegment(sketch, "E2790", {"start": v(14.74, -17.63) * mm, "end": v(14.8, -17.66) * mm});
            skLineSegment(sketch, "E2791", {"start": v(14.8, -17.66) * mm, "end": v(14.84, -17.7) * mm});
            skLineSegment(sketch, "E2792", {"start": v(14.84, -17.7) * mm, "end": v(14.9, -17.73) * mm});
            skLineSegment(sketch, "E2793", {"start": v(14.9, -17.73) * mm, "end": v(14.95, -17.76) * mm});
            skLineSegment(sketch, "E2794", {"start": v(14.95, -17.76) * mm, "end": v(15, -17.8) * mm});
            skLineSegment(sketch, "E2795", {"start": v(15, -17.8) * mm, "end": v(15.06, -17.83) * mm});
            skLineSegment(sketch, "E2796", {"start": v(15.06, -17.83) * mm, "end": v(15.12, -17.86) * mm});
            skLineSegment(sketch, "E2797", {"start": v(15.12, -17.86) * mm, "end": v(15.18, -17.9) * mm});
            skLineSegment(sketch, "E2798", {"start": v(15.18, -17.9) * mm, "end": v(15.24, -17.93) * mm});
            skLineSegment(sketch, "E2799", {"start": v(15.24, -17.93) * mm, "end": v(15.3, -17.97) * mm});
            skLineSegment(sketch, "E2800", {"start": v(15.3, -17.97) * mm, "end": v(15.37, -18) * mm});
            skLineSegment(sketch, "E2801", {"start": v(15.37, -18) * mm, "end": v(15.44, -18.04) * mm});
            skLineSegment(sketch, "E2802", {"start": v(15.44, -18.04) * mm, "end": v(15.5, -18.07) * mm});
            skLineSegment(sketch, "E2803", {"start": v(15.5, -18.07) * mm, "end": v(15.58, -18.1) * mm});
            skLineSegment(sketch, "E2804", {"start": v(15.58, -18.1) * mm, "end": v(15.65, -18.14) * mm});
            skLineSegment(sketch, "E2805", {"start": v(15.65, -18.14) * mm, "end": v(15.73, -18.18) * mm});
            skLineSegment(sketch, "E2806", {"start": v(15.73, -18.18) * mm, "end": v(15.83, -18.23) * mm});
            skLineSegment(sketch, "E2807", {"start": v(15.83, -18.23) * mm, "end": v(16.25, -17.86) * mm});
            skLineSegment(sketch, "E2808", {"start": v(16.25, -17.86) * mm, "end": v(16.2, -17.75) * mm});
            skLineSegment(sketch, "E2809", {"start": v(16.2, -17.75) * mm, "end": v(16.18, -17.67) * mm});
            skLineSegment(sketch, "E2810", {"start": v(16.18, -17.67) * mm, "end": v(16.15, -17.6) * mm});
            skLineSegment(sketch, "E2811", {"start": v(16.15, -17.6) * mm, "end": v(16.13, -17.52) * mm});
            skLineSegment(sketch, "E2812", {"start": v(16.13, -17.52) * mm, "end": v(16.1, -17.45) * mm});
            skLineSegment(sketch, "E2813", {"start": v(16.1, -17.45) * mm, "end": v(16.07, -17.38) * mm});
            skLineSegment(sketch, "E2814", {"start": v(16.07, -17.38) * mm, "end": v(16.04, -17.3) * mm});
            skLineSegment(sketch, "E2815", {"start": v(16.04, -17.3) * mm, "end": v(16.02, -17.24) * mm});
            skLineSegment(sketch, "E2816", {"start": v(16.02, -17.24) * mm, "end": v(15.99, -17.17) * mm});
            skLineSegment(sketch, "E2817", {"start": v(15.99, -17.17) * mm, "end": v(15.96, -17.1) * mm});
            skLineSegment(sketch, "E2818", {"start": v(15.96, -17.1) * mm, "end": v(15.94, -17.05) * mm});
            skLineSegment(sketch, "E2819", {"start": v(15.94, -17.05) * mm, "end": v(15.9, -16.99) * mm});
            skLineSegment(sketch, "E2820", {"start": v(15.9, -16.99) * mm, "end": v(15.88, -16.93) * mm});
            skLineSegment(sketch, "E2821", {"start": v(15.88, -16.93) * mm, "end": v(15.85, -16.87) * mm});
            skLineSegment(sketch, "E2822", {"start": v(15.85, -16.87) * mm, "end": v(15.83, -16.82) * mm});
            skLineSegment(sketch, "E2823", {"start": v(15.83, -16.82) * mm, "end": v(15.8, -16.76) * mm});
            skLineSegment(sketch, "E2824", {"start": v(15.8, -16.76) * mm, "end": v(15.78, -16.71) * mm});
            skLineSegment(sketch, "E2825", {"start": v(15.78, -16.71) * mm, "end": v(15.75, -16.66) * mm});
            skLineSegment(sketch, "E2826", {"start": v(15.75, -16.66) * mm, "end": v(15.73, -16.61) * mm});
            skLineSegment(sketch, "E2827", {"start": v(15.73, -16.61) * mm, "end": v(15.7, -16.57) * mm});
            skLineSegment(sketch, "E2828", {"start": v(15.7, -16.57) * mm, "end": v(15.65, -16.48) * mm});
            skLineSegment(sketch, "E2829", {"start": v(15.65, -16.48) * mm, "end": v(15.6, -16.4) * mm});
            skLineSegment(sketch, "E2830", {"start": v(15.6, -16.4) * mm, "end": v(15.57, -16.34) * mm});
            skArc(sketch, "E2831", {"start": v(15.57, -16.34) * mm, "mid": v(15.58, -15.96) * mm, "end": v(15.96, -15.96) * mm});
            skLineSegment(sketch, "E2832", {"start": v(15.96, -15.96) * mm, "end": v(16.02, -16) * mm});
            skLineSegment(sketch, "E2833", {"start": v(16.02, -16) * mm, "end": v(16.1, -16.04) * mm});
            skLineSegment(sketch, "E2834", {"start": v(16.1, -16.04) * mm, "end": v(16.19, -16.1) * mm});
            skLineSegment(sketch, "E2835", {"start": v(16.19, -16.1) * mm, "end": v(16.23, -16.12) * mm});
            skLineSegment(sketch, "E2836", {"start": v(16.23, -16.12) * mm, "end": v(16.28, -16.14) * mm});
            skLineSegment(sketch, "E2837", {"start": v(16.28, -16.14) * mm, "end": v(16.33, -16.17) * mm});
            skLineSegment(sketch, "E2838", {"start": v(16.33, -16.17) * mm, "end": v(16.38, -16.2) * mm});
            skLineSegment(sketch, "E2839", {"start": v(16.38, -16.2) * mm, "end": v(16.43, -16.22) * mm});
            skLineSegment(sketch, "E2840", {"start": v(16.43, -16.22) * mm, "end": v(16.49, -16.25) * mm});
            skLineSegment(sketch, "E2841", {"start": v(16.49, -16.25) * mm, "end": v(16.54, -16.28) * mm});
            skLineSegment(sketch, "E2842", {"start": v(16.54, -16.28) * mm, "end": v(16.6, -16.3) * mm});
            skLineSegment(sketch, "E2843", {"start": v(16.6, -16.3) * mm, "end": v(16.66, -16.34) * mm});
            skLineSegment(sketch, "E2844", {"start": v(16.66, -16.34) * mm, "end": v(16.72, -16.37) * mm});
            skLineSegment(sketch, "E2845", {"start": v(16.72, -16.37) * mm, "end": v(16.79, -16.4) * mm});
            skLineSegment(sketch, "E2846", {"start": v(16.79, -16.4) * mm, "end": v(16.85, -16.42) * mm});
            skLineSegment(sketch, "E2847", {"start": v(16.85, -16.42) * mm, "end": v(16.92, -16.45) * mm});
            skLineSegment(sketch, "E2848", {"start": v(16.92, -16.45) * mm, "end": v(16.99, -16.48) * mm});
            skLineSegment(sketch, "E2849", {"start": v(16.99, -16.48) * mm, "end": v(17.06, -16.51) * mm});
            skLineSegment(sketch, "E2850", {"start": v(17.06, -16.51) * mm, "end": v(17.13, -16.54) * mm});
            skLineSegment(sketch, "E2851", {"start": v(17.13, -16.54) * mm, "end": v(17.2, -16.57) * mm});
            skLineSegment(sketch, "E2852", {"start": v(17.2, -16.57) * mm, "end": v(17.28, -16.6) * mm});
            skLineSegment(sketch, "E2853", {"start": v(17.28, -16.6) * mm, "end": v(17.36, -16.63) * mm});
            skLineSegment(sketch, "E2854", {"start": v(17.36, -16.63) * mm, "end": v(17.47, -16.67) * mm});
            skLineSegment(sketch, "E2855", {"start": v(17.47, -16.67) * mm, "end": v(17.85, -16.26) * mm});
            skLineSegment(sketch, "E2856", {"start": v(17.85, -16.26) * mm, "end": v(17.8, -16.15) * mm});
            skLineSegment(sketch, "E2857", {"start": v(17.8, -16.15) * mm, "end": v(17.77, -16.08) * mm});
            skLineSegment(sketch, "E2858", {"start": v(17.77, -16.08) * mm, "end": v(17.73, -16) * mm});
            skLineSegment(sketch, "E2859", {"start": v(17.73, -16) * mm, "end": v(17.7, -15.93) * mm});
            skLineSegment(sketch, "E2860", {"start": v(17.7, -15.93) * mm, "end": v(17.66, -15.86) * mm});
            skLineSegment(sketch, "E2861", {"start": v(17.66, -15.86) * mm, "end": v(17.63, -15.8) * mm});
            skLineSegment(sketch, "E2862", {"start": v(17.63, -15.8) * mm, "end": v(17.6, -15.73) * mm});
            skLineSegment(sketch, "E2863", {"start": v(17.6, -15.73) * mm, "end": v(17.56, -15.66) * mm});
            skLineSegment(sketch, "E2864", {"start": v(17.56, -15.66) * mm, "end": v(17.53, -15.6) * mm});
            skLineSegment(sketch, "E2865", {"start": v(17.53, -15.6) * mm, "end": v(17.5, -15.54) * mm});
            skLineSegment(sketch, "E2866", {"start": v(17.5, -15.54) * mm, "end": v(17.46, -15.48) * mm});
            skLineSegment(sketch, "E2867", {"start": v(17.46, -15.48) * mm, "end": v(17.43, -15.42) * mm});
            skLineSegment(sketch, "E2868", {"start": v(17.43, -15.42) * mm, "end": v(17.4, -15.37) * mm});
            skLineSegment(sketch, "E2869", {"start": v(17.4, -15.37) * mm, "end": v(17.36, -15.31) * mm});
            skLineSegment(sketch, "E2870", {"start": v(17.36, -15.31) * mm, "end": v(17.33, -15.26) * mm});
            skLineSegment(sketch, "E2871", {"start": v(17.33, -15.26) * mm, "end": v(17.3, -15.2) * mm});
            skLineSegment(sketch, "E2872", {"start": v(17.3, -15.2) * mm, "end": v(17.27, -15.16) * mm});
            skLineSegment(sketch, "E2873", {"start": v(17.27, -15.16) * mm, "end": v(17.24, -15.11) * mm});
            skLineSegment(sketch, "E2874", {"start": v(17.24, -15.11) * mm, "end": v(17.21, -15.07) * mm});
            skLineSegment(sketch, "E2875", {"start": v(17.21, -15.07) * mm, "end": v(17.18, -15.02) * mm});
            skLineSegment(sketch, "E2876", {"start": v(17.18, -15.02) * mm, "end": v(17.13, -14.94) * mm});
            skLineSegment(sketch, "E2877", {"start": v(17.13, -14.94) * mm, "end": v(17.07, -14.86) * mm});
            skLineSegment(sketch, "E2878", {"start": v(17.07, -14.86) * mm, "end": v(17.03, -14.8) * mm});
            skArc(sketch, "E2879", {"start": v(17.03, -14.8) * mm, "mid": v(17, -14.43) * mm, "end": v(17.39, -14.4) * mm});
            skLineSegment(sketch, "E2880", {"start": v(17.39, -14.4) * mm, "end": v(17.45, -14.42) * mm});
            skLineSegment(sketch, "E2881", {"start": v(17.45, -14.42) * mm, "end": v(17.53, -14.46) * mm});
            skLineSegment(sketch, "E2882", {"start": v(17.53, -14.46) * mm, "end": v(17.62, -14.5) * mm});
            skLineSegment(sketch, "E2883", {"start": v(17.62, -14.5) * mm, "end": v(17.67, -14.53) * mm});
            skLineSegment(sketch, "E2884", {"start": v(17.67, -14.53) * mm, "end": v(17.72, -14.55) * mm});
            skLineSegment(sketch, "E2885", {"start": v(17.72, -14.55) * mm, "end": v(17.77, -14.57) * mm});
            skLineSegment(sketch, "E2886", {"start": v(17.77, -14.57) * mm, "end": v(17.82, -14.6) * mm});
            skLineSegment(sketch, "E2887", {"start": v(17.82, -14.6) * mm, "end": v(17.88, -14.61) * mm});
            skLineSegment(sketch, "E2888", {"start": v(17.88, -14.61) * mm, "end": v(17.94, -14.64) * mm});
            skLineSegment(sketch, "E2889", {"start": v(17.94, -14.64) * mm, "end": v(18, -14.66) * mm});
            skLineSegment(sketch, "E2890", {"start": v(18, -14.66) * mm, "end": v(18.06, -14.68) * mm});
            skLineSegment(sketch, "E2891", {"start": v(18.06, -14.68) * mm, "end": v(18.12, -14.7) * mm});
            skLineSegment(sketch, "E2892", {"start": v(18.12, -14.7) * mm, "end": v(18.18, -14.73) * mm});
            skLineSegment(sketch, "E2893", {"start": v(18.18, -14.73) * mm, "end": v(18.25, -14.75) * mm});
            skLineSegment(sketch, "E2894", {"start": v(18.25, -14.75) * mm, "end": v(18.32, -14.77) * mm});
            skLineSegment(sketch, "E2895", {"start": v(18.32, -14.77) * mm, "end": v(18.39, -14.8) * mm});
            skLineSegment(sketch, "E2896", {"start": v(18.39, -14.8) * mm, "end": v(18.46, -14.82) * mm});
            skLineSegment(sketch, "E2897", {"start": v(18.46, -14.82) * mm, "end": v(18.53, -14.84) * mm});
            skLineSegment(sketch, "E2898", {"start": v(18.53, -14.84) * mm, "end": v(18.6, -14.86) * mm});
            skLineSegment(sketch, "E2899", {"start": v(18.6, -14.86) * mm, "end": v(18.68, -14.88) * mm});
            skLineSegment(sketch, "E2900", {"start": v(18.68, -14.88) * mm, "end": v(18.76, -14.9) * mm});
            skLineSegment(sketch, "E2901", {"start": v(18.76, -14.9) * mm, "end": v(18.84, -14.93) * mm});
            skLineSegment(sketch, "E2902", {"start": v(18.84, -14.93) * mm, "end": v(18.95, -14.96) * mm});
            skLineSegment(sketch, "E2903", {"start": v(18.95, -14.96) * mm, "end": v(19.3, -14.52) * mm});
            skLineSegment(sketch, "E2904", {"start": v(19.3, -14.52) * mm, "end": v(19.23, -14.42) * mm});
            skLineSegment(sketch, "E2905", {"start": v(19.23, -14.42) * mm, "end": v(19.2, -14.34) * mm});
            skLineSegment(sketch, "E2906", {"start": v(19.2, -14.34) * mm, "end": v(19.15, -14.27) * mm});
            skLineSegment(sketch, "E2907", {"start": v(19.15, -14.27) * mm, "end": v(19.11, -14.2) * mm});
            skLineSegment(sketch, "E2908", {"start": v(19.11, -14.2) * mm, "end": v(19.07, -14.14) * mm});
            skLineSegment(sketch, "E2909", {"start": v(19.07, -14.14) * mm, "end": v(19.03, -14.07) * mm});
            skLineSegment(sketch, "E2910", {"start": v(19.03, -14.07) * mm, "end": v(18.99, -14.01) * mm});
            skLineSegment(sketch, "E2911", {"start": v(18.99, -14.01) * mm, "end": v(18.95, -13.95) * mm});
            skLineSegment(sketch, "E2912", {"start": v(18.95, -13.95) * mm, "end": v(18.91, -13.89) * mm});
            skLineSegment(sketch, "E2913", {"start": v(18.91, -13.89) * mm, "end": v(18.87, -13.83) * mm});
            skLineSegment(sketch, "E2914", {"start": v(18.87, -13.83) * mm, "end": v(18.83, -13.78) * mm});
            skLineSegment(sketch, "E2915", {"start": v(18.83, -13.78) * mm, "end": v(18.8, -13.72) * mm});
            skLineSegment(sketch, "E2916", {"start": v(18.8, -13.72) * mm, "end": v(18.76, -13.67) * mm});
            skLineSegment(sketch, "E2917", {"start": v(18.76, -13.67) * mm, "end": v(18.72, -13.62) * mm});
            skLineSegment(sketch, "E2918", {"start": v(18.72, -13.62) * mm, "end": v(18.69, -13.57) * mm});
            skLineSegment(sketch, "E2919", {"start": v(18.69, -13.57) * mm, "end": v(18.65, -13.52) * mm});
            skLineSegment(sketch, "E2920", {"start": v(18.65, -13.52) * mm, "end": v(18.61, -13.47) * mm});
            skLineSegment(sketch, "E2921", {"start": v(18.61, -13.47) * mm, "end": v(18.58, -13.43) * mm});
            skLineSegment(sketch, "E2922", {"start": v(18.58, -13.43) * mm, "end": v(18.55, -13.39) * mm});
            skLineSegment(sketch, "E2923", {"start": v(18.55, -13.39) * mm, "end": v(18.51, -13.35) * mm});
            skLineSegment(sketch, "E2924", {"start": v(18.51, -13.35) * mm, "end": v(18.45, -13.27) * mm});
            skLineSegment(sketch, "E2925", {"start": v(18.45, -13.27) * mm, "end": v(18.39, -13.2) * mm});
            skLineSegment(sketch, "E2926", {"start": v(18.39, -13.2) * mm, "end": v(18.34, -13.15) * mm});
            skArc(sketch, "E2927", {"start": v(18.34, -13.15) * mm, "mid": v(18.29, -12.77) * mm, "end": v(18.66, -12.7) * mm});
            skLineSegment(sketch, "E2928", {"start": v(18.66, -12.7) * mm, "end": v(18.72, -12.72) * mm});
            skLineSegment(sketch, "E2929", {"start": v(18.72, -12.72) * mm, "end": v(18.8, -12.76) * mm});
            skLineSegment(sketch, "E2930", {"start": v(18.8, -12.76) * mm, "end": v(18.9, -12.79) * mm});
            skLineSegment(sketch, "E2931", {"start": v(18.9, -12.79) * mm, "end": v(18.95, -12.8) * mm});
            skLineSegment(sketch, "E2932", {"start": v(18.95, -12.8) * mm, "end": v(19, -12.82) * mm});
            skLineSegment(sketch, "E2933", {"start": v(19, -12.82) * mm, "end": v(19.06, -12.84) * mm});
            skLineSegment(sketch, "E2934", {"start": v(19.06, -12.84) * mm, "end": v(19.11, -12.86) * mm});
            skLineSegment(sketch, "E2935", {"start": v(19.11, -12.86) * mm, "end": v(19.17, -12.87) * mm});
            skLineSegment(sketch, "E2936", {"start": v(19.17, -12.87) * mm, "end": v(19.23, -12.9) * mm});
            skLineSegment(sketch, "E2937", {"start": v(19.23, -12.9) * mm, "end": v(19.29, -12.9) * mm});
            skLineSegment(sketch, "E2938", {"start": v(19.29, -12.9) * mm, "end": v(19.35, -12.93) * mm});
            skLineSegment(sketch, "E2939", {"start": v(19.35, -12.93) * mm, "end": v(19.42, -12.94) * mm});
            skLineSegment(sketch, "E2940", {"start": v(19.42, -12.94) * mm, "end": v(19.48, -12.96) * mm});
            skLineSegment(sketch, "E2941", {"start": v(19.48, -12.96) * mm, "end": v(19.55, -12.98) * mm});
            skLineSegment(sketch, "E2942", {"start": v(19.55, -12.98) * mm, "end": v(19.62, -13) * mm});
            skLineSegment(sketch, "E2943", {"start": v(19.62, -13) * mm, "end": v(19.69, -13) * mm});
            skLineSegment(sketch, "E2944", {"start": v(19.69, -13) * mm, "end": v(19.76, -13.02) * mm});
            skLineSegment(sketch, "E2945", {"start": v(19.76, -13.02) * mm, "end": v(19.84, -13.04) * mm});
            skLineSegment(sketch, "E2946", {"start": v(19.84, -13.04) * mm, "end": v(19.91, -13.05) * mm});
            skLineSegment(sketch, "E2947", {"start": v(19.91, -13.05) * mm, "end": v(20, -13.07) * mm});
            skLineSegment(sketch, "E2948", {"start": v(20, -13.07) * mm, "end": v(20.07, -13.08) * mm});
            skLineSegment(sketch, "E2949", {"start": v(20.07, -13.08) * mm, "end": v(20.15, -13.1) * mm});
            skLineSegment(sketch, "E2950", {"start": v(20.15, -13.1) * mm, "end": v(20.27, -13.12) * mm});
            skLineSegment(sketch, "E2951", {"start": v(20.27, -13.12) * mm, "end": v(20.57, -12.65) * mm});
            skLineSegment(sketch, "E2952", {"start": v(20.57, -12.65) * mm, "end": v(20.5, -12.55) * mm});
            skLineSegment(sketch, "E2953", {"start": v(20.5, -12.55) * mm, "end": v(20.45, -12.48) * mm});
            skLineSegment(sketch, "E2954", {"start": v(20.45, -12.48) * mm, "end": v(20.4, -12.42) * mm});
            skLineSegment(sketch, "E2955", {"start": v(20.4, -12.42) * mm, "end": v(20.36, -12.35) * mm});
            skLineSegment(sketch, "E2956", {"start": v(20.36, -12.35) * mm, "end": v(20.31, -12.29) * mm});
            skLineSegment(sketch, "E2957", {"start": v(20.31, -12.29) * mm, "end": v(20.26, -12.23) * mm});
            skLineSegment(sketch, "E2958", {"start": v(20.26, -12.23) * mm, "end": v(20.22, -12.17) * mm});
            skLineSegment(sketch, "E2959", {"start": v(20.22, -12.17) * mm, "end": v(20.17, -12.11) * mm});
            skLineSegment(sketch, "E2960", {"start": v(20.17, -12.11) * mm, "end": v(20.13, -12.06) * mm});
            skLineSegment(sketch, "E2961", {"start": v(20.13, -12.06) * mm, "end": v(20.08, -12) * mm});
            skLineSegment(sketch, "E2962", {"start": v(20.08, -12) * mm, "end": v(20.04, -11.95) * mm});
            skLineSegment(sketch, "E2963", {"start": v(20.04, -11.95) * mm, "end": v(20, -11.9) * mm});
            skLineSegment(sketch, "E2964", {"start": v(20, -11.9) * mm, "end": v(19.96, -11.85) * mm});
            skLineSegment(sketch, "E2965", {"start": v(19.96, -11.85) * mm, "end": v(19.91, -11.8) * mm});
            skLineSegment(sketch, "E2966", {"start": v(19.91, -11.8) * mm, "end": v(19.87, -11.76) * mm});
            skLineSegment(sketch, "E2967", {"start": v(19.87, -11.76) * mm, "end": v(19.83, -11.71) * mm});
            skLineSegment(sketch, "E2968", {"start": v(19.83, -11.71) * mm, "end": v(19.8, -11.67) * mm});
            skLineSegment(sketch, "E2969", {"start": v(19.8, -11.67) * mm, "end": v(19.76, -11.63) * mm});
            skLineSegment(sketch, "E2970", {"start": v(19.76, -11.63) * mm, "end": v(19.72, -11.6) * mm});
            skLineSegment(sketch, "E2971", {"start": v(19.72, -11.6) * mm, "end": v(19.68, -11.55) * mm});
            skLineSegment(sketch, "E2972", {"start": v(19.68, -11.55) * mm, "end": v(19.61, -11.48) * mm});
            skLineSegment(sketch, "E2973", {"start": v(19.61, -11.48) * mm, "end": v(19.54, -11.42) * mm});
            skLineSegment(sketch, "E2974", {"start": v(19.54, -11.42) * mm, "end": v(19.5, -11.37) * mm});
            skArc(sketch, "E2975", {"start": v(19.5, -11.37) * mm, "mid": v(19.4, -11) * mm, "end": v(19.76, -10.9) * mm});
            skLineSegment(sketch, "E2976", {"start": v(19.76, -10.9) * mm, "end": v(19.83, -10.91) * mm});
            skLineSegment(sketch, "E2977", {"start": v(19.83, -10.91) * mm, "end": v(19.92, -10.94) * mm});
            skLineSegment(sketch, "E2978", {"start": v(19.92, -10.94) * mm, "end": v(20.02, -10.96) * mm});
            skLineSegment(sketch, "E2979", {"start": v(20.02, -10.96) * mm, "end": v(20.07, -10.97) * mm});
            skLineSegment(sketch, "E2980", {"start": v(20.07, -10.97) * mm, "end": v(20.12, -10.99) * mm});
            skLineSegment(sketch, "E2981", {"start": v(20.12, -10.99) * mm, "end": v(20.18, -11) * mm});
            skLineSegment(sketch, "E2982", {"start": v(20.18, -11) * mm, "end": v(20.23, -11.01) * mm});
            skLineSegment(sketch, "E2983", {"start": v(20.23, -11.01) * mm, "end": v(20.3, -11.02) * mm});
            skLineSegment(sketch, "E2984", {"start": v(20.3, -11.02) * mm, "end": v(20.35, -11.03) * mm});
            skLineSegment(sketch, "E2985", {"start": v(20.35, -11.03) * mm, "end": v(20.41, -11.05) * mm});
            skLineSegment(sketch, "E2986", {"start": v(20.41, -11.05) * mm, "end": v(20.48, -11.06) * mm});
            skLineSegment(sketch, "E2987", {"start": v(20.48, -11.06) * mm, "end": v(20.54, -11.07) * mm});
            skLineSegment(sketch, "E2988", {"start": v(20.54, -11.07) * mm, "end": v(20.6, -11.08) * mm});
            skLineSegment(sketch, "E2989", {"start": v(20.6, -11.08) * mm, "end": v(20.68, -11.09) * mm});
            skLineSegment(sketch, "E2990", {"start": v(20.68, -11.09) * mm, "end": v(20.75, -11.1) * mm});
            skLineSegment(sketch, "E2991", {"start": v(20.75, -11.1) * mm, "end": v(20.82, -11.1) * mm});
            skLineSegment(sketch, "E2992", {"start": v(20.82, -11.1) * mm, "end": v(20.9, -11.12) * mm});
            skLineSegment(sketch, "E2993", {"start": v(20.9, -11.12) * mm, "end": v(20.97, -11.12) * mm});
            skLineSegment(sketch, "E2994", {"start": v(20.97, -11.12) * mm, "end": v(21.05, -11.13) * mm});
            skLineSegment(sketch, "E2995", {"start": v(21.05, -11.13) * mm, "end": v(21.13, -11.14) * mm});
            skLineSegment(sketch, "E2996", {"start": v(21.13, -11.14) * mm, "end": v(21.2, -11.15) * mm});
            skLineSegment(sketch, "E2997", {"start": v(21.2, -11.15) * mm, "end": v(21.3, -11.15) * mm});
            skLineSegment(sketch, "E2998", {"start": v(21.3, -11.15) * mm, "end": v(21.41, -11.16) * mm});
            skLineSegment(sketch, "E2999", {"start": v(21.41, -11.16) * mm, "end": v(21.66, -10.67) * mm});
            skLineSegment(sketch, "E3000", {"start": v(21.66, -10.67) * mm, "end": v(21.58, -10.58) * mm});
            skLineSegment(sketch, "E3001", {"start": v(21.58, -10.58) * mm, "end": v(21.53, -10.51) * mm});
            skLineSegment(sketch, "E3002", {"start": v(21.53, -10.51) * mm, "end": v(21.48, -10.45) * mm});
            skLineSegment(sketch, "E3003", {"start": v(21.48, -10.45) * mm, "end": v(21.42, -10.4) * mm});
            skLineSegment(sketch, "E3004", {"start": v(21.42, -10.4) * mm, "end": v(21.37, -10.33) * mm});
            skLineSegment(sketch, "E3005", {"start": v(21.37, -10.33) * mm, "end": v(21.32, -10.28) * mm});
            skLineSegment(sketch, "E3006", {"start": v(21.32, -10.28) * mm, "end": v(21.27, -10.22) * mm});
            skLineSegment(sketch, "E3007", {"start": v(21.27, -10.22) * mm, "end": v(21.22, -10.17) * mm});
            skLineSegment(sketch, "E3008", {"start": v(21.22, -10.17) * mm, "end": v(21.17, -10.12) * mm});
            skLineSegment(sketch, "E3009", {"start": v(21.17, -10.12) * mm, "end": v(21.12, -10.07) * mm});
            skLineSegment(sketch, "E3010", {"start": v(21.12, -10.07) * mm, "end": v(21.07, -10.02) * mm});
            skLineSegment(sketch, "E3011", {"start": v(21.07, -10.02) * mm, "end": v(21.02, -9.97) * mm});
            skLineSegment(sketch, "E3012", {"start": v(21.02, -9.97) * mm, "end": v(20.98, -9.93) * mm});
            skLineSegment(sketch, "E3013", {"start": v(20.98, -9.93) * mm, "end": v(20.93, -9.89) * mm});
            skLineSegment(sketch, "E3014", {"start": v(20.93, -9.89) * mm, "end": v(20.89, -9.84) * mm});
            skLineSegment(sketch, "E3015", {"start": v(20.89, -9.84) * mm, "end": v(20.84, -9.8) * mm});
            skLineSegment(sketch, "E3016", {"start": v(20.84, -9.8) * mm, "end": v(20.8, -9.77) * mm});
            skLineSegment(sketch, "E3017", {"start": v(20.8, -9.77) * mm, "end": v(20.76, -9.73) * mm});
            skLineSegment(sketch, "E3018", {"start": v(20.76, -9.73) * mm, "end": v(20.72, -9.7) * mm});
            skLineSegment(sketch, "E3019", {"start": v(20.72, -9.7) * mm, "end": v(20.68, -9.66) * mm});
            skLineSegment(sketch, "E3020", {"start": v(20.68, -9.66) * mm, "end": v(20.6, -9.6) * mm});
            skLineSegment(sketch, "E3021", {"start": v(20.6, -9.6) * mm, "end": v(20.53, -9.54) * mm});
            skLineSegment(sketch, "E3022", {"start": v(20.53, -9.54) * mm, "end": v(20.47, -9.5) * mm});
            skArc(sketch, "E3023", {"start": v(20.47, -9.5) * mm, "mid": v(20.35, -9.14) * mm, "end": v(20.7, -9) * mm});
            skLineSegment(sketch, "E3024", {"start": v(20.7, -9) * mm, "end": v(20.76, -9) * mm});
            skLineSegment(sketch, "E3025", {"start": v(20.76, -9) * mm, "end": v(20.86, -9.02) * mm});
            skLineSegment(sketch, "E3026", {"start": v(20.86, -9.02) * mm, "end": v(20.96, -9.04) * mm});
            skLineSegment(sketch, "E3027", {"start": v(20.96, -9.04) * mm, "end": v(21, -9.05) * mm});
            skLineSegment(sketch, "E3028", {"start": v(21, -9.05) * mm, "end": v(21.06, -9.05) * mm});
            skLineSegment(sketch, "E3029", {"start": v(21.06, -9.05) * mm, "end": v(21.12, -9.06) * mm});
            skLineSegment(sketch, "E3030", {"start": v(21.12, -9.06) * mm, "end": v(21.17, -9.07) * mm});
            skLineSegment(sketch, "E3031", {"start": v(21.17, -9.07) * mm, "end": v(21.23, -9.07) * mm});
            skLineSegment(sketch, "E3032", {"start": v(21.23, -9.07) * mm, "end": v(21.3, -9.08) * mm});
            skLineSegment(sketch, "E3033", {"start": v(21.3, -9.08) * mm, "end": v(21.36, -9.08) * mm});
            skLineSegment(sketch, "E3034", {"start": v(21.36, -9.08) * mm, "end": v(21.42, -9.09) * mm});
            skLineSegment(sketch, "E3035", {"start": v(21.42, -9.09) * mm, "end": v(21.49, -9.1) * mm});
            skLineSegment(sketch, "E3036", {"start": v(21.49, -9.1) * mm, "end": v(21.56, -9.1) * mm});
            skLineSegment(sketch, "E3037", {"start": v(21.56, -9.1) * mm, "end": v(21.63, -9.1) * mm});
            skLineSegment(sketch, "E3038", {"start": v(21.63, -9.1) * mm, "end": v(21.7, -9.1) * mm});
            skLineSegment(sketch, "E3039", {"start": v(21.7, -9.1) * mm, "end": v(21.77, -9.1) * mm});
            skLineSegment(sketch, "E3040", {"start": v(21.77, -9.1) * mm, "end": v(21.84, -9.1) * mm});
            skLineSegment(sketch, "E3041", {"start": v(21.84, -9.1) * mm, "end": v(21.92, -9.11) * mm});
            skLineSegment(sketch, "E3042", {"start": v(21.92, -9.11) * mm, "end": v(22, -9.11) * mm});
            skLineSegment(sketch, "E3043", {"start": v(22, -9.11) * mm, "end": v(22.08, -9.11) * mm});
            skLineSegment(sketch, "E3044", {"start": v(22.08, -9.11) * mm, "end": v(22.16, -9.11) * mm});
            skLineSegment(sketch, "E3045", {"start": v(22.16, -9.11) * mm, "end": v(22.24, -9.1) * mm});
            skLineSegment(sketch, "E3046", {"start": v(22.24, -9.1) * mm, "end": v(22.36, -9.1) * mm});
            skLineSegment(sketch, "E3047", {"start": v(22.36, -9.1) * mm, "end": v(22.56, -8.59) * mm});
            skLineSegment(sketch, "E3048", {"start": v(22.56, -8.59) * mm, "end": v(22.48, -8.5) * mm});
            skLineSegment(sketch, "E3049", {"start": v(22.48, -8.5) * mm, "end": v(22.42, -8.45) * mm});
            skLineSegment(sketch, "E3050", {"start": v(22.42, -8.45) * mm, "end": v(22.36, -8.4) * mm});
            skLineSegment(sketch, "E3051", {"start": v(22.36, -8.4) * mm, "end": v(22.3, -8.34) * mm});
            skLineSegment(sketch, "E3052", {"start": v(22.3, -8.34) * mm, "end": v(22.25, -8.29) * mm});
            skLineSegment(sketch, "E3053", {"start": v(22.25, -8.29) * mm, "end": v(22.19, -8.23) * mm});
            skLineSegment(sketch, "E3054", {"start": v(22.19, -8.23) * mm, "end": v(22.13, -8.19) * mm});
            skLineSegment(sketch, "E3055", {"start": v(22.13, -8.19) * mm, "end": v(22.08, -8.14) * mm});
            skLineSegment(sketch, "E3056", {"start": v(22.08, -8.14) * mm, "end": v(22.02, -8.1) * mm});
            skLineSegment(sketch, "E3057", {"start": v(22.02, -8.1) * mm, "end": v(21.97, -8.05) * mm});
            skLineSegment(sketch, "E3058", {"start": v(21.97, -8.05) * mm, "end": v(21.92, -8) * mm});
            skLineSegment(sketch, "E3059", {"start": v(21.92, -8) * mm, "end": v(21.87, -7.96) * mm});
            skLineSegment(sketch, "E3060", {"start": v(21.87, -7.96) * mm, "end": v(21.82, -7.92) * mm});
            skLineSegment(sketch, "E3061", {"start": v(21.82, -7.92) * mm, "end": v(21.77, -7.88) * mm});
            skLineSegment(sketch, "E3062", {"start": v(21.77, -7.88) * mm, "end": v(21.72, -7.84) * mm});
            skLineSegment(sketch, "E3063", {"start": v(21.72, -7.84) * mm, "end": v(21.67, -7.8) * mm});
            skLineSegment(sketch, "E3064", {"start": v(21.67, -7.8) * mm, "end": v(21.62, -7.77) * mm});
            skLineSegment(sketch, "E3065", {"start": v(21.62, -7.77) * mm, "end": v(21.58, -7.74) * mm});
            skLineSegment(sketch, "E3066", {"start": v(21.58, -7.74) * mm, "end": v(21.53, -7.7) * mm});
            skLineSegment(sketch, "E3067", {"start": v(21.53, -7.7) * mm, "end": v(21.5, -7.68) * mm});
            skLineSegment(sketch, "E3068", {"start": v(21.5, -7.68) * mm, "end": v(21.4, -7.62) * mm});
            skLineSegment(sketch, "E3069", {"start": v(21.4, -7.62) * mm, "end": v(21.33, -7.57) * mm});
            skLineSegment(sketch, "E3070", {"start": v(21.33, -7.57) * mm, "end": v(21.27, -7.54) * mm});
            skArc(sketch, "E3071", {"start": v(21.27, -7.54) * mm, "mid": v(21.11, -7.2) * mm, "end": v(21.45, -7.02) * mm});
            skLineSegment(sketch, "E3072", {"start": v(21.45, -7.02) * mm, "end": v(21.52, -7.02) * mm});
            skLineSegment(sketch, "E3073", {"start": v(21.52, -7.02) * mm, "end": v(21.6, -7.03) * mm});
            skLineSegment(sketch, "E3074", {"start": v(21.6, -7.03) * mm, "end": v(21.7, -7.04) * mm});
            skLineSegment(sketch, "E3075", {"start": v(21.7, -7.04) * mm, "end": v(21.76, -7.04) * mm});
            skLineSegment(sketch, "E3076", {"start": v(21.76, -7.04) * mm, "end": v(21.82, -7.04) * mm});
            skLineSegment(sketch, "E3077", {"start": v(21.82, -7.04) * mm, "end": v(21.87, -7.04) * mm});
            skLineSegment(sketch, "E3078", {"start": v(21.87, -7.04) * mm, "end": v(21.93, -7.04) * mm});
            skLineSegment(sketch, "E3079", {"start": v(21.93, -7.04) * mm, "end": v(22, -7.04) * mm});
            skLineSegment(sketch, "E3080", {"start": v(22, -7.04) * mm, "end": v(22.05, -7.04) * mm});
            skLineSegment(sketch, "E3081", {"start": v(22.05, -7.04) * mm, "end": v(22.11, -7.04) * mm});
            skLineSegment(sketch, "E3082", {"start": v(22.11, -7.04) * mm, "end": v(22.18, -7.04) * mm});
            skLineSegment(sketch, "E3083", {"start": v(22.18, -7.04) * mm, "end": v(22.25, -7.04) * mm});
            skLineSegment(sketch, "E3084", {"start": v(22.25, -7.04) * mm, "end": v(22.31, -7.04) * mm});
            skLineSegment(sketch, "E3085", {"start": v(22.31, -7.04) * mm, "end": v(22.38, -7.04) * mm});
            skLineSegment(sketch, "E3086", {"start": v(22.38, -7.04) * mm, "end": v(22.45, -7.03) * mm});
            skLineSegment(sketch, "E3087", {"start": v(22.45, -7.03) * mm, "end": v(22.53, -7.03) * mm});
            skLineSegment(sketch, "E3088", {"start": v(22.53, -7.03) * mm, "end": v(22.6, -7.02) * mm});
            skLineSegment(sketch, "E3089", {"start": v(22.6, -7.02) * mm, "end": v(22.68, -7.02) * mm});
            skLineSegment(sketch, "E3090", {"start": v(22.68, -7.02) * mm, "end": v(22.76, -7.01) * mm});
            skLineSegment(sketch, "E3091", {"start": v(22.76, -7.01) * mm, "end": v(22.83, -7) * mm});
            skLineSegment(sketch, "E3092", {"start": v(22.83, -7) * mm, "end": v(22.92, -7) * mm});
            skLineSegment(sketch, "E3093", {"start": v(22.92, -7) * mm, "end": v(23, -6.99) * mm});
            skLineSegment(sketch, "E3094", {"start": v(23, -6.99) * mm, "end": v(23.12, -6.97) * mm});
            skLineSegment(sketch, "E3095", {"start": v(23.12, -6.97) * mm, "end": v(23.27, -6.44) * mm});
            skLineSegment(sketch, "E3096", {"start": v(23.27, -6.44) * mm, "end": v(23.18, -6.36) * mm});
            skLineSegment(sketch, "E3097", {"start": v(23.18, -6.36) * mm, "end": v(23.11, -6.31) * mm});
            skLineSegment(sketch, "E3098", {"start": v(23.11, -6.31) * mm, "end": v(23.05, -6.26) * mm});
            skLineSegment(sketch, "E3099", {"start": v(23.05, -6.26) * mm, "end": v(22.99, -6.21) * mm});
            skLineSegment(sketch, "E3100", {"start": v(22.99, -6.21) * mm, "end": v(22.92, -6.17) * mm});
            skLineSegment(sketch, "E3101", {"start": v(22.92, -6.17) * mm, "end": v(22.86, -6.12) * mm});
            skLineSegment(sketch, "E3102", {"start": v(22.86, -6.12) * mm, "end": v(22.8, -6.08) * mm});
            skLineSegment(sketch, "E3103", {"start": v(22.8, -6.08) * mm, "end": v(22.74, -6.03) * mm});
            skLineSegment(sketch, "E3104", {"start": v(22.74, -6.03) * mm, "end": v(22.68, -6) * mm});
            skLineSegment(sketch, "E3105", {"start": v(22.68, -6) * mm, "end": v(22.63, -5.95) * mm});
            skLineSegment(sketch, "E3106", {"start": v(22.63, -5.95) * mm, "end": v(22.57, -5.91) * mm});
            skLineSegment(sketch, "E3107", {"start": v(22.57, -5.91) * mm, "end": v(22.52, -5.88) * mm});
            skLineSegment(sketch, "E3108", {"start": v(22.52, -5.88) * mm, "end": v(22.46, -5.84) * mm});
            skLineSegment(sketch, "E3109", {"start": v(22.46, -5.84) * mm, "end": v(22.4, -5.8) * mm});
            skLineSegment(sketch, "E3110", {"start": v(22.4, -5.8) * mm, "end": v(22.36, -5.78) * mm});
            skLineSegment(sketch, "E3111", {"start": v(22.36, -5.78) * mm, "end": v(22.3, -5.74) * mm});
            skLineSegment(sketch, "E3112", {"start": v(22.3, -5.74) * mm, "end": v(22.26, -5.71) * mm});
            skLineSegment(sketch, "E3113", {"start": v(22.26, -5.71) * mm, "end": v(22.2, -5.69) * mm});
            skLineSegment(sketch, "E3114", {"start": v(22.2, -5.69) * mm, "end": v(22.16, -5.66) * mm});
            skLineSegment(sketch, "E3115", {"start": v(22.16, -5.66) * mm, "end": v(22.12, -5.63) * mm});
            skLineSegment(sketch, "E3116", {"start": v(22.12, -5.63) * mm, "end": v(22.03, -5.58) * mm});
            skLineSegment(sketch, "E3117", {"start": v(22.03, -5.58) * mm, "end": v(21.94, -5.54) * mm});
            skLineSegment(sketch, "E3118", {"start": v(21.94, -5.54) * mm, "end": v(21.89, -5.5) * mm});
            skArc(sketch, "E3119", {"start": v(21.89, -5.5) * mm, "mid": v(21.7, -5.18) * mm, "end": v(22.01, -4.98) * mm});
            skLineSegment(sketch, "E3120", {"start": v(22.01, -4.98) * mm, "end": v(22.08, -4.98) * mm});
            skLineSegment(sketch, "E3121", {"start": v(22.08, -4.98) * mm, "end": v(22.17, -4.98) * mm});
            skLineSegment(sketch, "E3122", {"start": v(22.17, -4.98) * mm, "end": v(22.27, -4.97) * mm});
            skLineSegment(sketch, "E3123", {"start": v(22.27, -4.97) * mm, "end": v(22.33, -4.97) * mm});
            skLineSegment(sketch, "E3124", {"start": v(22.33, -4.97) * mm, "end": v(22.38, -4.97) * mm});
            skLineSegment(sketch, "E3125", {"start": v(22.38, -4.97) * mm, "end": v(22.44, -4.96) * mm});
            skLineSegment(sketch, "E3126", {"start": v(22.44, -4.96) * mm, "end": v(22.5, -4.96) * mm});
            skLineSegment(sketch, "E3127", {"start": v(22.5, -4.96) * mm, "end": v(22.55, -4.95) * mm});
            skLineSegment(sketch, "E3128", {"start": v(22.55, -4.95) * mm, "end": v(22.61, -4.95) * mm});
            skLineSegment(sketch, "E3129", {"start": v(22.61, -4.95) * mm, "end": v(22.68, -4.94) * mm});
            skLineSegment(sketch, "E3130", {"start": v(22.68, -4.94) * mm, "end": v(22.74, -4.93) * mm});
            skLineSegment(sketch, "E3131", {"start": v(22.74, -4.93) * mm, "end": v(22.8, -4.93) * mm});
            skLineSegment(sketch, "E3132", {"start": v(22.8, -4.93) * mm, "end": v(22.87, -4.92) * mm});
            skLineSegment(sketch, "E3133", {"start": v(22.87, -4.92) * mm, "end": v(22.94, -4.9) * mm});
            skLineSegment(sketch, "E3134", {"start": v(22.94, -4.9) * mm, "end": v(23.01, -4.9) * mm});
            skLineSegment(sketch, "E3135", {"start": v(23.01, -4.9) * mm, "end": v(23.09, -4.89) * mm});
            skLineSegment(sketch, "E3136", {"start": v(23.09, -4.89) * mm, "end": v(23.16, -4.88) * mm});
            skLineSegment(sketch, "E3137", {"start": v(23.16, -4.88) * mm, "end": v(23.24, -4.86) * mm});
            skLineSegment(sketch, "E3138", {"start": v(23.24, -4.86) * mm, "end": v(23.31, -4.85) * mm});
            skLineSegment(sketch, "E3139", {"start": v(23.31, -4.85) * mm, "end": v(23.4, -4.83) * mm});
            skLineSegment(sketch, "E3140", {"start": v(23.4, -4.83) * mm, "end": v(23.47, -4.82) * mm});
            skLineSegment(sketch, "E3141", {"start": v(23.47, -4.82) * mm, "end": v(23.55, -4.8) * mm});
            skLineSegment(sketch, "E3142", {"start": v(23.55, -4.8) * mm, "end": v(23.67, -4.77) * mm});
            skLineSegment(sketch, "E3143", {"start": v(23.67, -4.77) * mm, "end": v(23.77, -4.23) * mm});
            skLineSegment(sketch, "E3144", {"start": v(23.77, -4.23) * mm, "end": v(23.67, -4.16) * mm});
            skLineSegment(sketch, "E3145", {"start": v(23.67, -4.16) * mm, "end": v(23.6, -4.12) * mm});
            skLineSegment(sketch, "E3146", {"start": v(23.6, -4.12) * mm, "end": v(23.53, -4.08) * mm});
            skLineSegment(sketch, "E3147", {"start": v(23.53, -4.08) * mm, "end": v(23.47, -4.03) * mm});
            skLineSegment(sketch, "E3148", {"start": v(23.47, -4.03) * mm, "end": v(23.4, -4) * mm});
            skLineSegment(sketch, "E3149", {"start": v(23.4, -4) * mm, "end": v(23.34, -3.95) * mm});
            skLineSegment(sketch, "E3150", {"start": v(23.34, -3.95) * mm, "end": v(23.27, -3.91) * mm});
            skLineSegment(sketch, "E3151", {"start": v(23.27, -3.91) * mm, "end": v(23.2, -3.88) * mm});
            skLineSegment(sketch, "E3152", {"start": v(23.2, -3.88) * mm, "end": v(23.15, -3.84) * mm});
            skLineSegment(sketch, "E3153", {"start": v(23.15, -3.84) * mm, "end": v(23.09, -3.8) * mm});
            skLineSegment(sketch, "E3154", {"start": v(23.09, -3.8) * mm, "end": v(23.03, -3.77) * mm});
            skLineSegment(sketch, "E3155", {"start": v(23.03, -3.77) * mm, "end": v(22.97, -3.74) * mm});
            skLineSegment(sketch, "E3156", {"start": v(22.97, -3.74) * mm, "end": v(22.91, -3.71) * mm});
            skLineSegment(sketch, "E3157", {"start": v(22.91, -3.71) * mm, "end": v(22.85, -3.68) * mm});
            skLineSegment(sketch, "E3158", {"start": v(22.85, -3.68) * mm, "end": v(22.8, -3.66) * mm});
            skLineSegment(sketch, "E3159", {"start": v(22.8, -3.66) * mm, "end": v(22.75, -3.63) * mm});
            skLineSegment(sketch, "E3160", {"start": v(22.75, -3.63) * mm, "end": v(22.7, -3.6) * mm});
            skLineSegment(sketch, "E3161", {"start": v(22.7, -3.6) * mm, "end": v(22.64, -3.58) * mm});
            skLineSegment(sketch, "E3162", {"start": v(22.64, -3.58) * mm, "end": v(22.6, -3.56) * mm});
            skLineSegment(sketch, "E3163", {"start": v(22.6, -3.56) * mm, "end": v(22.55, -3.54) * mm});
            skLineSegment(sketch, "E3164", {"start": v(22.55, -3.54) * mm, "end": v(22.45, -3.5) * mm});
            skLineSegment(sketch, "E3165", {"start": v(22.45, -3.5) * mm, "end": v(22.37, -3.46) * mm});
            skLineSegment(sketch, "E3166", {"start": v(22.37, -3.46) * mm, "end": v(22.3, -3.44) * mm});
            skArc(sketch, "E3167", {"start": v(22.3, -3.44) * mm, "mid": v(22.08, -3.13) * mm, "end": v(22.38, -2.9) * mm});
            skLineSegment(sketch, "E3168", {"start": v(22.38, -2.9) * mm, "end": v(22.45, -2.89) * mm});
            skLineSegment(sketch, "E3169", {"start": v(22.45, -2.89) * mm, "end": v(22.54, -2.88) * mm});
            skLineSegment(sketch, "E3170", {"start": v(22.54, -2.88) * mm, "end": v(22.64, -2.86) * mm});
            skLineSegment(sketch, "E3171", {"start": v(22.64, -2.86) * mm, "end": v(22.7, -2.86) * mm});
            skLineSegment(sketch, "E3172", {"start": v(22.7, -2.86) * mm, "end": v(22.75, -2.85) * mm});
            skLineSegment(sketch, "E3173", {"start": v(22.75, -2.85) * mm, "end": v(22.8, -2.84) * mm});
            skLineSegment(sketch, "E3174", {"start": v(22.8, -2.84) * mm, "end": v(22.86, -2.83) * mm});
            skLineSegment(sketch, "E3175", {"start": v(22.86, -2.83) * mm, "end": v(22.92, -2.82) * mm});
            skLineSegment(sketch, "E3176", {"start": v(22.92, -2.82) * mm, "end": v(22.98, -2.8) * mm});
            skLineSegment(sketch, "E3177", {"start": v(22.98, -2.8) * mm, "end": v(23.04, -2.8) * mm});
            skLineSegment(sketch, "E3178", {"start": v(23.04, -2.8) * mm, "end": v(23.1, -2.78) * mm});
            skLineSegment(sketch, "E3179", {"start": v(23.1, -2.78) * mm, "end": v(23.17, -2.77) * mm});
            skLineSegment(sketch, "E3180", {"start": v(23.17, -2.77) * mm, "end": v(23.23, -2.75) * mm});
            skLineSegment(sketch, "E3181", {"start": v(23.23, -2.75) * mm, "end": v(23.3, -2.74) * mm});
            skLineSegment(sketch, "E3182", {"start": v(23.3, -2.74) * mm, "end": v(23.37, -2.72) * mm});
            skLineSegment(sketch, "E3183", {"start": v(23.37, -2.72) * mm, "end": v(23.44, -2.7) * mm});
            skLineSegment(sketch, "E3184", {"start": v(23.44, -2.7) * mm, "end": v(23.51, -2.68) * mm});
            skLineSegment(sketch, "E3185", {"start": v(23.51, -2.68) * mm, "end": v(23.59, -2.66) * mm});
            skLineSegment(sketch, "E3186", {"start": v(23.59, -2.66) * mm, "end": v(23.66, -2.64) * mm});
            skLineSegment(sketch, "E3187", {"start": v(23.66, -2.64) * mm, "end": v(23.74, -2.62) * mm});
            skLineSegment(sketch, "E3188", {"start": v(23.74, -2.62) * mm, "end": v(23.82, -2.6) * mm});
            skLineSegment(sketch, "E3189", {"start": v(23.82, -2.6) * mm, "end": v(23.9, -2.57) * mm});
            skLineSegment(sketch, "E3190", {"start": v(23.9, -2.57) * mm, "end": v(24, -2.54) * mm});
            skLineSegment(sketch, "E3191", {"start": v(24, -2.54) * mm, "end": v(24.06, -1.99) * mm});
            skLineSegment(sketch, "E3192", {"start": v(24.06, -1.99) * mm, "end": v(23.96, -1.93) * mm});
            skLineSegment(sketch, "E3193", {"start": v(23.96, -1.93) * mm, "end": v(23.88, -1.9) * mm});
            skLineSegment(sketch, "E3194", {"start": v(23.88, -1.9) * mm, "end": v(23.81, -1.85) * mm});
            skLineSegment(sketch, "E3195", {"start": v(23.81, -1.85) * mm, "end": v(23.74, -1.82) * mm});
            skLineSegment(sketch, "E3196", {"start": v(23.74, -1.82) * mm, "end": v(23.67, -1.78) * mm});
            skLineSegment(sketch, "E3197", {"start": v(23.67, -1.78) * mm, "end": v(23.6, -1.75) * mm});
            skLineSegment(sketch, "E3198", {"start": v(23.6, -1.75) * mm, "end": v(23.54, -1.72) * mm});
            skLineSegment(sketch, "E3199", {"start": v(23.54, -1.72) * mm, "end": v(23.47, -1.69) * mm});
            skLineSegment(sketch, "E3200", {"start": v(23.47, -1.69) * mm, "end": v(23.4, -1.66) * mm});
            skLineSegment(sketch, "E3201", {"start": v(23.4, -1.66) * mm, "end": v(23.34, -1.63) * mm});
            skLineSegment(sketch, "E3202", {"start": v(23.34, -1.63) * mm, "end": v(23.28, -1.6) * mm});
            skLineSegment(sketch, "E3203", {"start": v(23.28, -1.6) * mm, "end": v(23.22, -1.58) * mm});
            skLineSegment(sketch, "E3204", {"start": v(23.22, -1.58) * mm, "end": v(23.16, -1.55) * mm});
            skLineSegment(sketch, "E3205", {"start": v(23.16, -1.55) * mm, "end": v(23.1, -1.53) * mm});
            skLineSegment(sketch, "E3206", {"start": v(23.1, -1.53) * mm, "end": v(23.04, -1.5) * mm});
            skLineSegment(sketch, "E3207", {"start": v(23.04, -1.5) * mm, "end": v(22.99, -1.48) * mm});
            skLineSegment(sketch, "E3208", {"start": v(22.99, -1.48) * mm, "end": v(22.93, -1.46) * mm});
            skLineSegment(sketch, "E3209", {"start": v(22.93, -1.46) * mm, "end": v(22.88, -1.44) * mm});
            skLineSegment(sketch, "E3210", {"start": v(22.88, -1.44) * mm, "end": v(22.83, -1.43) * mm});
            skLineSegment(sketch, "E3211", {"start": v(22.83, -1.43) * mm, "end": v(22.78, -1.4) * mm});
            skLineSegment(sketch, "E3212", {"start": v(22.78, -1.4) * mm, "end": v(22.68, -1.38) * mm});
            skLineSegment(sketch, "E3213", {"start": v(22.68, -1.38) * mm, "end": v(22.6, -1.35) * mm});
            skLineSegment(sketch, "E3214", {"start": v(22.6, -1.35) * mm, "end": v(22.53, -1.33) * mm});
            skArc(sketch, "E3215", {"start": v(22.53, -1.33) * mm, "mid": v(22.28, -1.05) * mm, "end": v(22.55, -0.79) * mm});
            skCircle(sketch, "E3216", {"center": v(0, 0) * mm, "radius": 4 * mm});
            skSolve(sketch);
        }
        {
            var Q0;
            Q0 = qSketchRegion(id + "F0", true);
            extrude(context, id + "F1", {"entities" : qUnion([Q0]), "depth" : 7 * mm});
        }
    });
